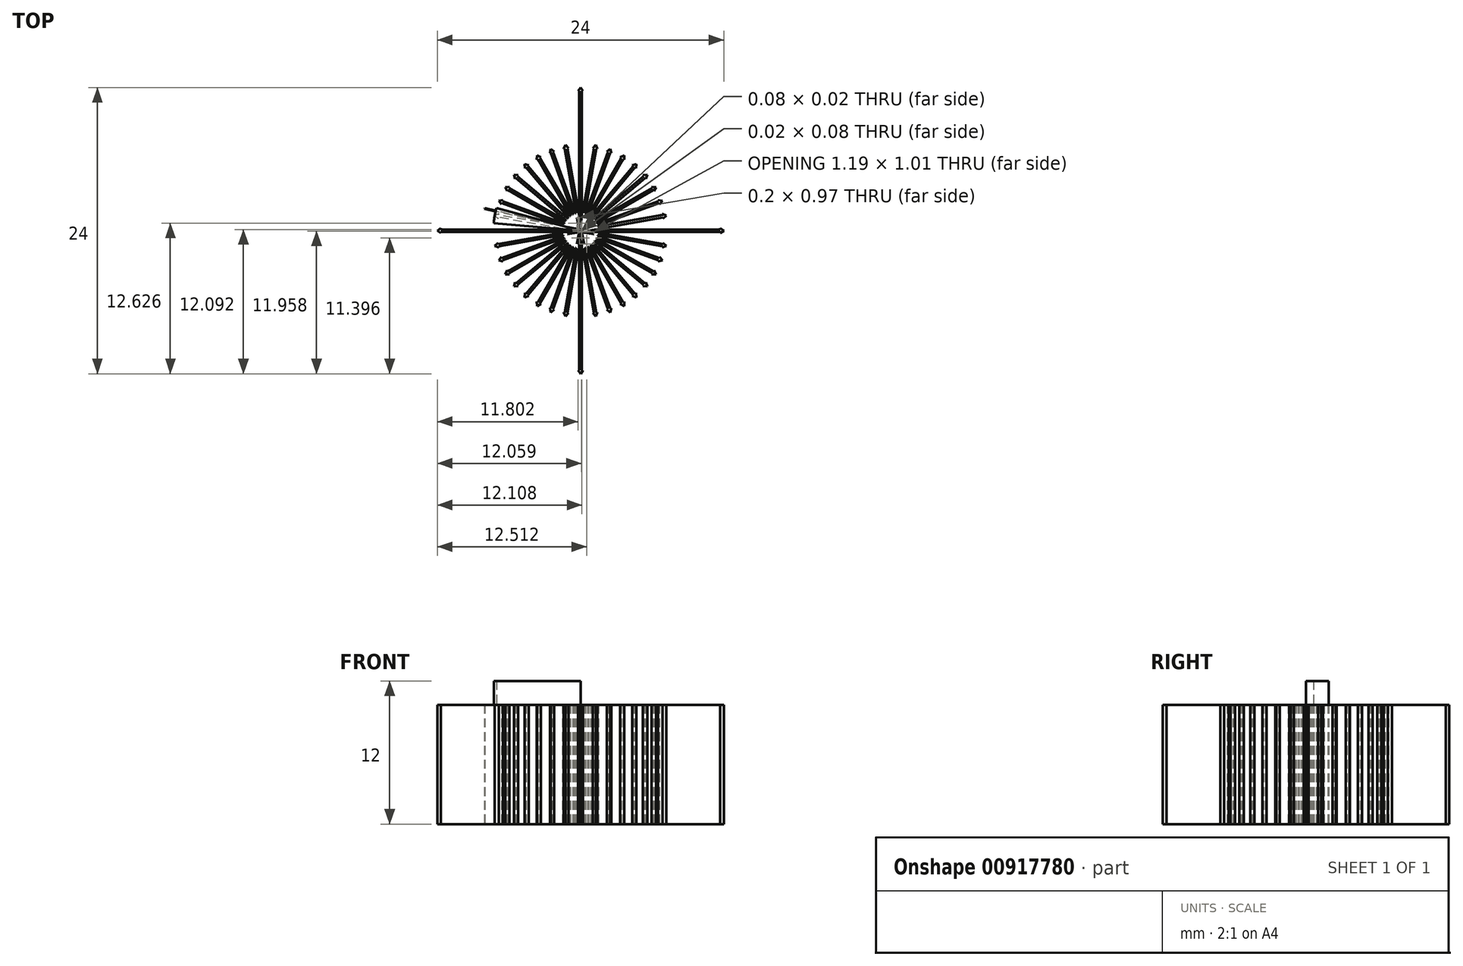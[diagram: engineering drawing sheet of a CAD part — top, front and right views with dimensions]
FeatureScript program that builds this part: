
annotation { "Feature Type Name" : "Feature", "Feature Type Description" : "" }
export const myFeature = defineFeature(function(context is Context, id is Id, definition is map)
    precondition{}
    {
        {
            var Q0;
            Q0=qCreatedBy(makeId("Top.planeOp"),FACE);
            var sketch = newSketch(context, id + "F0", { "sketchPlane" : qUnion([Q0])});
            skCircle(sketch, "E0", {"center": v(0, 0) * mm, "radius": 1.5 * mm});
            skLineSegment(sketch, "E1", {"start": v(0, 0) * mm, "end": v(0, 9.82) * mm, "construction": true});
            skLineSegment(sketch, "E2.bottom", {"start": v(-0.1, 0) * mm, "end": v(0.1, 0) * mm, "construction": true});
            skLineSegment(sketch, "E2.top", {"start": v(-0.1, 11.7) * mm, "end": v(0.1, 11.7) * mm});
            skLineSegment(sketch, "E2.left", {"start": v(-0.1, 0) * mm, "end": v(-0.1, 11.7) * mm});
            skLineSegment(sketch, "E2.right", {"start": v(0.1, 0) * mm, "end": v(0.1, 11.7) * mm});
            skLineSegment(sketch, "E3", {"start": v(0, 12) * mm, "end": v(-0.2, 11.7) * mm});
            skLineSegment(sketch, "E4", {"start": v(-0.2, 11.7) * mm, "end": v(0.2, 11.7) * mm});
            skLineSegment(sketch, "E5", {"start": v(0.2, 11.7) * mm, "end": v(0, 12) * mm});
            skLineSegment(sketch, "E6.1.0", {"start": v(0, 0.1) * mm, "end": v(-11.7, 0.1) * mm});
            skLineSegment(sketch, "E6.1.1", {"start": v(0, -0.1) * mm, "end": v(-11.7, -0.1) * mm});
            skLineSegment(sketch, "E6.1.2", {"start": v(-11.7, 0.2) * mm, "end": v(-12, 0) * mm});
            skLineSegment(sketch, "E6.1.3", {"start": v(-11.7, -0.2) * mm, "end": v(-11.7, 0.2) * mm});
            skLineSegment(sketch, "E6.1.4", {"start": v(-12, 0) * mm, "end": v(-11.7, -0.2) * mm});
            skLineSegment(sketch, "E6.2.0", {"start": v(-0.1, 0) * mm, "end": v(-0.1, -11.7) * mm});
            skLineSegment(sketch, "E6.2.1", {"start": v(0.1, 0) * mm, "end": v(0.1, -11.7) * mm});
            skLineSegment(sketch, "E6.2.2", {"start": v(-0.2, -11.7) * mm, "end": v(0, -12) * mm});
            skLineSegment(sketch, "E6.2.3", {"start": v(0.2, -11.7) * mm, "end": v(-0.2, -11.7) * mm});
            skLineSegment(sketch, "E6.2.4", {"start": v(0, -12) * mm, "end": v(0.2, -11.7) * mm});
            skLineSegment(sketch, "E6.3.0", {"start": v(0, -0.1) * mm, "end": v(11.7, -0.1) * mm});
            skLineSegment(sketch, "E6.3.1", {"start": v(0, 0.1) * mm, "end": v(11.7, 0.1) * mm});
            skLineSegment(sketch, "E6.3.2", {"start": v(11.7, -0.2) * mm, "end": v(12, 0) * mm});
            skLineSegment(sketch, "E6.3.3", {"start": v(11.7, 0.2) * mm, "end": v(11.7, -0.2) * mm});
            skLineSegment(sketch, "E6.3.4", {"start": v(12, 0) * mm, "end": v(11.7, 0.2) * mm});
            skLineSegment(sketch, "E7.anchor1", {"start": v(0, 0) * mm, "end": v(0.1, 0) * mm, "construction": true});
            skLineSegment(sketch, "E7.anchor2", {"start": v(0, 0) * mm, "end": v(0.1, -0.02) * mm, "construction": true});
            skLineSegment(sketch, "E8", {"start": v(0, 0) * mm, "end": v(1.22, 6.9) * mm, "construction": true});
            skLineSegment(sketch, "E9.bottom", {"start": v(-0.1, 0.02) * mm, "end": v(0.1, -0.02) * mm});
            skLineSegment(sketch, "E9.top", {"start": v(1.12, 6.91) * mm, "end": v(1.31, 6.88) * mm});
            skLineSegment(sketch, "E9.left", {"start": v(-0.1, 0.02) * mm, "end": v(1.12, 6.91) * mm});
            skLineSegment(sketch, "E9.right", {"start": v(0.1, -0.02) * mm, "end": v(1.31, 6.88) * mm});
            skLineSegment(sketch, "E10", {"start": v(1.27, 7.19) * mm, "end": v(1.02, 6.91) * mm});
            skLineSegment(sketch, "E11", {"start": v(1.02, 6.91) * mm, "end": v(1.4, 6.84) * mm});
            skLineSegment(sketch, "E12", {"start": v(1.4, 6.84) * mm, "end": v(1.27, 7.19) * mm});
            skLineSegment(sketch, "E13", {"start": v(1.22, 6.9) * mm, "end": v(1.26, 7.17) * mm, "construction": true});
            skLineSegment(sketch, "E14.1.0", {"start": v(0.1, -0.03) * mm, "end": v(2.49, 6.54) * mm});
            skLineSegment(sketch, "E14.1.1", {"start": v(-0.1, 0.03) * mm, "end": v(2.3, 6.61) * mm});
            skLineSegment(sketch, "E14.1.2", {"start": v(2.58, 6.5) * mm, "end": v(2.5, 6.86) * mm});
            skLineSegment(sketch, "E14.1.3", {"start": v(2.5, 6.86) * mm, "end": v(2.2, 6.63) * mm});
            skLineSegment(sketch, "E14.1.4", {"start": v(2.2, 6.63) * mm, "end": v(2.58, 6.5) * mm});
            skLineSegment(sketch, "E14.1.5", {"start": v(2.3, 6.61) * mm, "end": v(2.49, 6.54) * mm});
            skLineSegment(sketch, "E14.2.0", {"start": v(0.09, -0.05) * mm, "end": v(3.59, 6.01) * mm});
            skLineSegment(sketch, "E14.2.1", {"start": v(-0.09, 0.05) * mm, "end": v(3.41, 6.11) * mm});
            skLineSegment(sketch, "E14.2.2", {"start": v(3.66, 5.95) * mm, "end": v(3.65, 6.32) * mm});
            skLineSegment(sketch, "E14.2.3", {"start": v(3.65, 6.32) * mm, "end": v(3.32, 6.15) * mm});
            skLineSegment(sketch, "E14.2.4", {"start": v(3.32, 6.15) * mm, "end": v(3.66, 5.95) * mm});
            skLineSegment(sketch, "E14.2.5", {"start": v(3.41, 6.11) * mm, "end": v(3.59, 6.01) * mm});
            skLineSegment(sketch, "E14.3.0", {"start": v(0.08, -0.06) * mm, "end": v(4.58, 5.3) * mm});
            skLineSegment(sketch, "E14.3.1", {"start": v(-0.08, 0.06) * mm, "end": v(4.42, 5.43) * mm});
            skLineSegment(sketch, "E14.3.2", {"start": v(4.64, 5.22) * mm, "end": v(4.7, 5.6) * mm});
            skLineSegment(sketch, "E14.3.3", {"start": v(4.7, 5.6) * mm, "end": v(4.33, 5.48) * mm});
            skLineSegment(sketch, "E14.3.4", {"start": v(4.33, 5.48) * mm, "end": v(4.64, 5.22) * mm});
            skLineSegment(sketch, "E14.3.5", {"start": v(4.42, 5.43) * mm, "end": v(4.58, 5.3) * mm});
            skLineSegment(sketch, "E14.4.0", {"start": v(0.06, -0.08) * mm, "end": v(5.43, 4.42) * mm});
            skLineSegment(sketch, "E14.4.1", {"start": v(-0.06, 0.08) * mm, "end": v(5.3, 4.58) * mm});
            skLineSegment(sketch, "E14.4.2", {"start": v(5.48, 4.33) * mm, "end": v(5.6, 4.7) * mm});
            skLineSegment(sketch, "E14.4.3", {"start": v(5.6, 4.7) * mm, "end": v(5.22, 4.64) * mm});
            skLineSegment(sketch, "E14.4.4", {"start": v(5.22, 4.64) * mm, "end": v(5.48, 4.33) * mm});
            skLineSegment(sketch, "E14.4.5", {"start": v(5.3, 4.58) * mm, "end": v(5.43, 4.42) * mm});
            skLineSegment(sketch, "E14.5.0", {"start": v(0.05, -0.09) * mm, "end": v(6.11, 3.41) * mm});
            skLineSegment(sketch, "E14.5.1", {"start": v(-0.05, 0.09) * mm, "end": v(6.01, 3.59) * mm});
            skLineSegment(sketch, "E14.5.2", {"start": v(6.15, 3.32) * mm, "end": v(6.32, 3.65) * mm});
            skLineSegment(sketch, "E14.5.3", {"start": v(6.32, 3.65) * mm, "end": v(5.95, 3.66) * mm});
            skLineSegment(sketch, "E14.5.4", {"start": v(5.95, 3.66) * mm, "end": v(6.15, 3.32) * mm});
            skLineSegment(sketch, "E14.5.5", {"start": v(6.01, 3.59) * mm, "end": v(6.11, 3.41) * mm});
            skLineSegment(sketch, "E14.6.0", {"start": v(0.03, -0.1) * mm, "end": v(6.61, 2.3) * mm});
            skLineSegment(sketch, "E14.6.1", {"start": v(-0.03, 0.1) * mm, "end": v(6.54, 2.49) * mm});
            skLineSegment(sketch, "E14.6.2", {"start": v(6.63, 2.2) * mm, "end": v(6.86, 2.5) * mm});
            skLineSegment(sketch, "E14.6.3", {"start": v(6.86, 2.5) * mm, "end": v(6.5, 2.58) * mm});
            skLineSegment(sketch, "E14.6.4", {"start": v(6.5, 2.58) * mm, "end": v(6.63, 2.2) * mm});
            skLineSegment(sketch, "E14.6.5", {"start": v(6.54, 2.49) * mm, "end": v(6.61, 2.3) * mm});
            skLineSegment(sketch, "E14.7.0", {"start": v(0.02, -0.1) * mm, "end": v(6.91, 1.12) * mm});
            skLineSegment(sketch, "E14.7.1", {"start": v(-0.02, 0.1) * mm, "end": v(6.88, 1.31) * mm});
            skLineSegment(sketch, "E14.7.2", {"start": v(6.91, 1.02) * mm, "end": v(7.19, 1.27) * mm});
            skLineSegment(sketch, "E14.7.3", {"start": v(7.19, 1.27) * mm, "end": v(6.84, 1.4) * mm});
            skLineSegment(sketch, "E14.7.4", {"start": v(6.84, 1.4) * mm, "end": v(6.91, 1.02) * mm});
            skLineSegment(sketch, "E14.7.5", {"start": v(6.88, 1.31) * mm, "end": v(6.91, 1.12) * mm});
            skLineSegment(sketch, "E14.8.0", {"start": v(0, -0.1) * mm, "end": v(7, -0.1) * mm});
            skLineSegment(sketch, "E14.8.1", {"start": v(0, 0.1) * mm, "end": v(7, 0.1) * mm});
            skLineSegment(sketch, "E14.8.5", {"start": v(7, 0.1) * mm, "end": v(7, -0.1) * mm});
            skLineSegment(sketch, "E14.9.0", {"start": v(-0.02, -0.1) * mm, "end": v(6.88, -1.31) * mm});
            skLineSegment(sketch, "E14.9.1", {"start": v(0.02, 0.1) * mm, "end": v(6.91, -1.12) * mm});
            skLineSegment(sketch, "E14.9.2", {"start": v(6.84, -1.4) * mm, "end": v(7.19, -1.27) * mm});
            skLineSegment(sketch, "E14.9.3", {"start": v(7.19, -1.27) * mm, "end": v(6.91, -1.02) * mm});
            skLineSegment(sketch, "E14.9.4", {"start": v(6.91, -1.02) * mm, "end": v(6.84, -1.4) * mm});
            skLineSegment(sketch, "E14.9.5", {"start": v(6.91, -1.12) * mm, "end": v(6.88, -1.31) * mm});
            skLineSegment(sketch, "E14.10.0", {"start": v(-0.03, -0.1) * mm, "end": v(6.54, -2.49) * mm});
            skLineSegment(sketch, "E14.10.1", {"start": v(0.03, 0.1) * mm, "end": v(6.61, -2.3) * mm});
            skLineSegment(sketch, "E14.10.2", {"start": v(6.5, -2.58) * mm, "end": v(6.86, -2.5) * mm});
            skLineSegment(sketch, "E14.10.3", {"start": v(6.86, -2.5) * mm, "end": v(6.63, -2.2) * mm});
            skLineSegment(sketch, "E14.10.4", {"start": v(6.63, -2.2) * mm, "end": v(6.5, -2.58) * mm});
            skLineSegment(sketch, "E14.10.5", {"start": v(6.61, -2.3) * mm, "end": v(6.54, -2.49) * mm});
            skLineSegment(sketch, "E14.11.0", {"start": v(-0.05, -0.09) * mm, "end": v(6.01, -3.59) * mm});
            skLineSegment(sketch, "E14.11.1", {"start": v(0.05, 0.09) * mm, "end": v(6.11, -3.41) * mm});
            skLineSegment(sketch, "E14.11.2", {"start": v(5.95, -3.66) * mm, "end": v(6.32, -3.65) * mm});
            skLineSegment(sketch, "E14.11.3", {"start": v(6.32, -3.65) * mm, "end": v(6.15, -3.32) * mm});
            skLineSegment(sketch, "E14.11.4", {"start": v(6.15, -3.32) * mm, "end": v(5.95, -3.66) * mm});
            skLineSegment(sketch, "E14.11.5", {"start": v(6.11, -3.41) * mm, "end": v(6.01, -3.59) * mm});
            skLineSegment(sketch, "E14.12.0", {"start": v(-0.06, -0.08) * mm, "end": v(5.3, -4.58) * mm});
            skLineSegment(sketch, "E14.12.1", {"start": v(0.06, 0.08) * mm, "end": v(5.43, -4.42) * mm});
            skLineSegment(sketch, "E14.12.2", {"start": v(5.22, -4.64) * mm, "end": v(5.6, -4.7) * mm});
            skLineSegment(sketch, "E14.12.3", {"start": v(5.6, -4.7) * mm, "end": v(5.48, -4.33) * mm});
            skLineSegment(sketch, "E14.12.4", {"start": v(5.48, -4.33) * mm, "end": v(5.22, -4.64) * mm});
            skLineSegment(sketch, "E14.12.5", {"start": v(5.43, -4.42) * mm, "end": v(5.3, -4.58) * mm});
            skLineSegment(sketch, "E14.13.0", {"start": v(-0.08, -0.06) * mm, "end": v(4.42, -5.43) * mm});
            skLineSegment(sketch, "E14.13.1", {"start": v(0.08, 0.06) * mm, "end": v(4.58, -5.3) * mm});
            skLineSegment(sketch, "E14.13.2", {"start": v(4.33, -5.48) * mm, "end": v(4.7, -5.6) * mm});
            skLineSegment(sketch, "E14.13.3", {"start": v(4.7, -5.6) * mm, "end": v(4.64, -5.22) * mm});
            skLineSegment(sketch, "E14.13.4", {"start": v(4.64, -5.22) * mm, "end": v(4.33, -5.48) * mm});
            skLineSegment(sketch, "E14.13.5", {"start": v(4.58, -5.3) * mm, "end": v(4.42, -5.43) * mm});
            skLineSegment(sketch, "E14.14.0", {"start": v(-0.09, -0.05) * mm, "end": v(3.41, -6.11) * mm});
            skLineSegment(sketch, "E14.14.1", {"start": v(0.09, 0.05) * mm, "end": v(3.59, -6.01) * mm});
            skLineSegment(sketch, "E14.14.2", {"start": v(3.32, -6.15) * mm, "end": v(3.65, -6.32) * mm});
            skLineSegment(sketch, "E14.14.3", {"start": v(3.65, -6.32) * mm, "end": v(3.66, -5.95) * mm});
            skLineSegment(sketch, "E14.14.4", {"start": v(3.66, -5.95) * mm, "end": v(3.32, -6.15) * mm});
            skLineSegment(sketch, "E14.14.5", {"start": v(3.59, -6.01) * mm, "end": v(3.41, -6.11) * mm});
            skLineSegment(sketch, "E14.15.0", {"start": v(-0.1, -0.03) * mm, "end": v(2.3, -6.61) * mm});
            skLineSegment(sketch, "E14.15.1", {"start": v(0.1, 0.03) * mm, "end": v(2.49, -6.54) * mm});
            skLineSegment(sketch, "E14.15.2", {"start": v(2.2, -6.63) * mm, "end": v(2.5, -6.86) * mm});
            skLineSegment(sketch, "E14.15.3", {"start": v(2.5, -6.86) * mm, "end": v(2.58, -6.5) * mm});
            skLineSegment(sketch, "E14.15.4", {"start": v(2.58, -6.5) * mm, "end": v(2.2, -6.63) * mm});
            skLineSegment(sketch, "E14.15.5", {"start": v(2.49, -6.54) * mm, "end": v(2.3, -6.61) * mm});
            skLineSegment(sketch, "E14.16.0", {"start": v(-0.1, -0.02) * mm, "end": v(1.12, -6.91) * mm});
            skLineSegment(sketch, "E14.16.1", {"start": v(0.1, 0.02) * mm, "end": v(1.31, -6.88) * mm});
            skLineSegment(sketch, "E14.16.2", {"start": v(1.02, -6.91) * mm, "end": v(1.27, -7.19) * mm});
            skLineSegment(sketch, "E14.16.3", {"start": v(1.27, -7.19) * mm, "end": v(1.4, -6.84) * mm});
            skLineSegment(sketch, "E14.16.4", {"start": v(1.4, -6.84) * mm, "end": v(1.02, -6.91) * mm});
            skLineSegment(sketch, "E14.16.5", {"start": v(1.31, -6.88) * mm, "end": v(1.12, -6.91) * mm});
            skLineSegment(sketch, "E14.17.0", {"start": v(-0.1, 0) * mm, "end": v(-0.1, -7) * mm});
            skLineSegment(sketch, "E14.17.1", {"start": v(0.1, 0) * mm, "end": v(0.1, -7) * mm});
            skLineSegment(sketch, "E14.17.5", {"start": v(0.1, -7) * mm, "end": v(-0.1, -7) * mm});
            skLineSegment(sketch, "E14.18.0", {"start": v(-0.1, 0.02) * mm, "end": v(-1.31, -6.88) * mm});
            skLineSegment(sketch, "E14.18.1", {"start": v(0.1, -0.02) * mm, "end": v(-1.12, -6.91) * mm});
            skLineSegment(sketch, "E14.18.2", {"start": v(-1.4, -6.84) * mm, "end": v(-1.27, -7.19) * mm});
            skLineSegment(sketch, "E14.18.3", {"start": v(-1.27, -7.19) * mm, "end": v(-1.02, -6.91) * mm});
            skLineSegment(sketch, "E14.18.4", {"start": v(-1.02, -6.91) * mm, "end": v(-1.4, -6.84) * mm});
            skLineSegment(sketch, "E14.18.5", {"start": v(-1.12, -6.91) * mm, "end": v(-1.31, -6.88) * mm});
            skLineSegment(sketch, "E14.19.0", {"start": v(-0.1, 0.03) * mm, "end": v(-2.49, -6.54) * mm});
            skLineSegment(sketch, "E14.19.1", {"start": v(0.1, -0.03) * mm, "end": v(-2.3, -6.61) * mm});
            skLineSegment(sketch, "E14.19.2", {"start": v(-2.58, -6.5) * mm, "end": v(-2.5, -6.86) * mm});
            skLineSegment(sketch, "E14.19.3", {"start": v(-2.5, -6.86) * mm, "end": v(-2.2, -6.63) * mm});
            skLineSegment(sketch, "E14.19.4", {"start": v(-2.2, -6.63) * mm, "end": v(-2.58, -6.5) * mm});
            skLineSegment(sketch, "E14.19.5", {"start": v(-2.3, -6.61) * mm, "end": v(-2.49, -6.54) * mm});
            skLineSegment(sketch, "E14.20.0", {"start": v(-0.09, 0.05) * mm, "end": v(-3.59, -6.01) * mm});
            skLineSegment(sketch, "E14.20.1", {"start": v(0.09, -0.05) * mm, "end": v(-3.41, -6.11) * mm});
            skLineSegment(sketch, "E14.20.2", {"start": v(-3.66, -5.95) * mm, "end": v(-3.65, -6.32) * mm});
            skLineSegment(sketch, "E14.20.3", {"start": v(-3.65, -6.32) * mm, "end": v(-3.32, -6.15) * mm});
            skLineSegment(sketch, "E14.20.4", {"start": v(-3.32, -6.15) * mm, "end": v(-3.66, -5.95) * mm});
            skLineSegment(sketch, "E14.20.5", {"start": v(-3.41, -6.11) * mm, "end": v(-3.59, -6.01) * mm});
            skLineSegment(sketch, "E14.21.0", {"start": v(-0.08, 0.06) * mm, "end": v(-4.58, -5.3) * mm});
            skLineSegment(sketch, "E14.21.1", {"start": v(0.08, -0.06) * mm, "end": v(-4.42, -5.43) * mm});
            skLineSegment(sketch, "E14.21.2", {"start": v(-4.64, -5.22) * mm, "end": v(-4.7, -5.6) * mm});
            skLineSegment(sketch, "E14.21.3", {"start": v(-4.7, -5.6) * mm, "end": v(-4.33, -5.48) * mm});
            skLineSegment(sketch, "E14.21.4", {"start": v(-4.33, -5.48) * mm, "end": v(-4.64, -5.22) * mm});
            skLineSegment(sketch, "E14.21.5", {"start": v(-4.42, -5.43) * mm, "end": v(-4.58, -5.3) * mm});
            skLineSegment(sketch, "E14.22.0", {"start": v(-0.06, 0.08) * mm, "end": v(-5.43, -4.42) * mm});
            skLineSegment(sketch, "E14.22.1", {"start": v(0.06, -0.08) * mm, "end": v(-5.3, -4.58) * mm});
            skLineSegment(sketch, "E14.22.2", {"start": v(-5.48, -4.33) * mm, "end": v(-5.6, -4.7) * mm});
            skLineSegment(sketch, "E14.22.3", {"start": v(-5.6, -4.7) * mm, "end": v(-5.22, -4.64) * mm});
            skLineSegment(sketch, "E14.22.4", {"start": v(-5.22, -4.64) * mm, "end": v(-5.48, -4.33) * mm});
            skLineSegment(sketch, "E14.22.5", {"start": v(-5.3, -4.58) * mm, "end": v(-5.43, -4.42) * mm});
            skLineSegment(sketch, "E14.23.0", {"start": v(-0.05, 0.09) * mm, "end": v(-6.11, -3.41) * mm});
            skLineSegment(sketch, "E14.23.1", {"start": v(0.05, -0.09) * mm, "end": v(-6.01, -3.59) * mm});
            skLineSegment(sketch, "E14.23.2", {"start": v(-6.15, -3.32) * mm, "end": v(-6.32, -3.65) * mm});
            skLineSegment(sketch, "E14.23.3", {"start": v(-6.32, -3.65) * mm, "end": v(-5.95, -3.66) * mm});
            skLineSegment(sketch, "E14.23.4", {"start": v(-5.95, -3.66) * mm, "end": v(-6.15, -3.32) * mm});
            skLineSegment(sketch, "E14.23.5", {"start": v(-6.01, -3.59) * mm, "end": v(-6.11, -3.41) * mm});
            skLineSegment(sketch, "E14.24.0", {"start": v(-0.03, 0.1) * mm, "end": v(-6.61, -2.3) * mm});
            skLineSegment(sketch, "E14.24.1", {"start": v(0.03, -0.1) * mm, "end": v(-6.54, -2.49) * mm});
            skLineSegment(sketch, "E14.24.2", {"start": v(-6.63, -2.2) * mm, "end": v(-6.86, -2.5) * mm});
            skLineSegment(sketch, "E14.24.3", {"start": v(-6.86, -2.5) * mm, "end": v(-6.5, -2.58) * mm});
            skLineSegment(sketch, "E14.24.4", {"start": v(-6.5, -2.58) * mm, "end": v(-6.63, -2.2) * mm});
            skLineSegment(sketch, "E14.24.5", {"start": v(-6.54, -2.49) * mm, "end": v(-6.61, -2.3) * mm});
            skLineSegment(sketch, "E14.25.0", {"start": v(-0.02, 0.1) * mm, "end": v(-6.91, -1.12) * mm});
            skLineSegment(sketch, "E14.25.1", {"start": v(0.02, -0.1) * mm, "end": v(-6.88, -1.31) * mm});
            skLineSegment(sketch, "E14.25.2", {"start": v(-6.91, -1.02) * mm, "end": v(-7.19, -1.27) * mm});
            skLineSegment(sketch, "E14.25.3", {"start": v(-7.19, -1.27) * mm, "end": v(-6.84, -1.4) * mm});
            skLineSegment(sketch, "E14.25.4", {"start": v(-6.84, -1.4) * mm, "end": v(-6.91, -1.02) * mm});
            skLineSegment(sketch, "E14.25.5", {"start": v(-6.88, -1.31) * mm, "end": v(-6.91, -1.12) * mm});
            skLineSegment(sketch, "E14.26.0", {"start": v(0, 0.1) * mm, "end": v(-7, 0.1) * mm});
            skLineSegment(sketch, "E14.26.1", {"start": v(0, -0.1) * mm, "end": v(-7, -0.1) * mm});
            skLineSegment(sketch, "E14.26.5", {"start": v(-7, -0.1) * mm, "end": v(-7, 0.1) * mm});
            skLineSegment(sketch, "E14.27.0", {"start": v(0.02, 0.1) * mm, "end": v(-6.88, 1.31) * mm});
            skLineSegment(sketch, "E14.27.1", {"start": v(-0.02, -0.1) * mm, "end": v(-6.91, 1.12) * mm});
            skLineSegment(sketch, "E14.27.2", {"start": v(-6.84, 1.4) * mm, "end": v(-7.19, 1.27) * mm});
            skLineSegment(sketch, "E14.27.3", {"start": v(-7.19, 1.27) * mm, "end": v(-6.91, 1.02) * mm});
            skLineSegment(sketch, "E14.27.4", {"start": v(-6.91, 1.02) * mm, "end": v(-6.84, 1.4) * mm});
            skLineSegment(sketch, "E14.27.5", {"start": v(-6.91, 1.12) * mm, "end": v(-6.88, 1.31) * mm});
            skLineSegment(sketch, "E14.28.0", {"start": v(0.03, 0.1) * mm, "end": v(-6.54, 2.49) * mm});
            skLineSegment(sketch, "E14.28.1", {"start": v(-0.03, -0.1) * mm, "end": v(-6.61, 2.3) * mm});
            skLineSegment(sketch, "E14.28.2", {"start": v(-6.5, 2.58) * mm, "end": v(-6.86, 2.5) * mm});
            skLineSegment(sketch, "E14.28.3", {"start": v(-6.86, 2.5) * mm, "end": v(-6.63, 2.2) * mm});
            skLineSegment(sketch, "E14.28.4", {"start": v(-6.63, 2.2) * mm, "end": v(-6.5, 2.58) * mm});
            skLineSegment(sketch, "E14.28.5", {"start": v(-6.61, 2.3) * mm, "end": v(-6.54, 2.49) * mm});
            skLineSegment(sketch, "E14.29.0", {"start": v(0.05, 0.09) * mm, "end": v(-6.01, 3.59) * mm});
            skLineSegment(sketch, "E14.29.1", {"start": v(-0.05, -0.09) * mm, "end": v(-6.11, 3.41) * mm});
            skLineSegment(sketch, "E14.29.2", {"start": v(-5.95, 3.66) * mm, "end": v(-6.32, 3.65) * mm});
            skLineSegment(sketch, "E14.29.3", {"start": v(-6.32, 3.65) * mm, "end": v(-6.15, 3.32) * mm});
            skLineSegment(sketch, "E14.29.4", {"start": v(-6.15, 3.32) * mm, "end": v(-5.95, 3.66) * mm});
            skLineSegment(sketch, "E14.29.5", {"start": v(-6.11, 3.41) * mm, "end": v(-6.01, 3.59) * mm});
            skLineSegment(sketch, "E14.30.0", {"start": v(0.06, 0.08) * mm, "end": v(-5.3, 4.58) * mm});
            skLineSegment(sketch, "E14.30.1", {"start": v(-0.06, -0.08) * mm, "end": v(-5.43, 4.42) * mm});
            skLineSegment(sketch, "E14.30.2", {"start": v(-5.22, 4.64) * mm, "end": v(-5.6, 4.7) * mm});
            skLineSegment(sketch, "E14.30.3", {"start": v(-5.6, 4.7) * mm, "end": v(-5.48, 4.33) * mm});
            skLineSegment(sketch, "E14.30.4", {"start": v(-5.48, 4.33) * mm, "end": v(-5.22, 4.64) * mm});
            skLineSegment(sketch, "E14.30.5", {"start": v(-5.43, 4.42) * mm, "end": v(-5.3, 4.58) * mm});
            skLineSegment(sketch, "E14.31.0", {"start": v(0.08, 0.06) * mm, "end": v(-4.42, 5.43) * mm});
            skLineSegment(sketch, "E14.31.1", {"start": v(-0.08, -0.06) * mm, "end": v(-4.58, 5.3) * mm});
            skLineSegment(sketch, "E14.31.2", {"start": v(-4.33, 5.48) * mm, "end": v(-4.7, 5.6) * mm});
            skLineSegment(sketch, "E14.31.3", {"start": v(-4.7, 5.6) * mm, "end": v(-4.64, 5.22) * mm});
            skLineSegment(sketch, "E14.31.4", {"start": v(-4.64, 5.22) * mm, "end": v(-4.33, 5.48) * mm});
            skLineSegment(sketch, "E14.31.5", {"start": v(-4.58, 5.3) * mm, "end": v(-4.42, 5.43) * mm});
            skLineSegment(sketch, "E14.32.0", {"start": v(0.09, 0.05) * mm, "end": v(-3.41, 6.11) * mm});
            skLineSegment(sketch, "E14.32.1", {"start": v(-0.09, -0.05) * mm, "end": v(-3.59, 6.01) * mm});
            skLineSegment(sketch, "E14.32.2", {"start": v(-3.32, 6.15) * mm, "end": v(-3.65, 6.32) * mm});
            skLineSegment(sketch, "E14.32.3", {"start": v(-3.65, 6.32) * mm, "end": v(-3.66, 5.95) * mm});
            skLineSegment(sketch, "E14.32.4", {"start": v(-3.66, 5.95) * mm, "end": v(-3.32, 6.15) * mm});
            skLineSegment(sketch, "E14.32.5", {"start": v(-3.59, 6.01) * mm, "end": v(-3.41, 6.11) * mm});
            skLineSegment(sketch, "E14.33.0", {"start": v(0.1, 0.03) * mm, "end": v(-2.3, 6.61) * mm});
            skLineSegment(sketch, "E14.33.1", {"start": v(-0.1, -0.03) * mm, "end": v(-2.49, 6.54) * mm});
            skLineSegment(sketch, "E14.33.2", {"start": v(-2.2, 6.63) * mm, "end": v(-2.5, 6.86) * mm});
            skLineSegment(sketch, "E14.33.3", {"start": v(-2.5, 6.86) * mm, "end": v(-2.58, 6.5) * mm});
            skLineSegment(sketch, "E14.33.4", {"start": v(-2.58, 6.5) * mm, "end": v(-2.2, 6.63) * mm});
            skLineSegment(sketch, "E14.33.5", {"start": v(-2.49, 6.54) * mm, "end": v(-2.3, 6.61) * mm});
            skLineSegment(sketch, "E14.34.0", {"start": v(0.1, 0.02) * mm, "end": v(-1.12, 6.91) * mm});
            skLineSegment(sketch, "E14.34.1", {"start": v(-0.1, -0.02) * mm, "end": v(-1.31, 6.88) * mm});
            skLineSegment(sketch, "E14.34.2", {"start": v(-1.02, 6.91) * mm, "end": v(-1.27, 7.19) * mm});
            skLineSegment(sketch, "E14.34.3", {"start": v(-1.27, 7.19) * mm, "end": v(-1.4, 6.84) * mm});
            skLineSegment(sketch, "E14.34.4", {"start": v(-1.4, 6.84) * mm, "end": v(-1.02, 6.91) * mm});
            skLineSegment(sketch, "E14.34.5", {"start": v(-1.31, 6.88) * mm, "end": v(-1.12, 6.91) * mm});
            skLineSegment(sketch, "E14.35.0", {"start": v(0.1, 0) * mm, "end": v(0.1, 7) * mm});
            skLineSegment(sketch, "E14.35.1", {"start": v(-0.1, 0) * mm, "end": v(-0.1, 7) * mm});
            skLineSegment(sketch, "E14.35.5", {"start": v(-0.1, 7) * mm, "end": v(0.1, 7) * mm});
            skLineSegment(sketch, "E14.anchor1", {"start": v(0, 0) * mm, "end": v(-0.1, 0.02) * mm, "construction": true});
            skLineSegment(sketch, "E14.anchor2", {"start": v(0, 0) * mm, "end": v(-0.1, 0) * mm, "construction": true});
            skLineSegment(sketch, "E15", {"start": v(0, 0) * mm, "end": v(-8.04, 1.86) * mm, "construction": true});
            skLineSegment(sketch, "E16.0", {"start": v(-1.47, 0.31) * mm, "end": v(-8.05, 1.83) * mm});
            skLineSegment(sketch, "E17", {"start": v(-8.05, 1.83) * mm, "end": v(-8.04, 1.88) * mm});
            skPoint(sketch, "E18.orphan", {"position": v(0, -0.02) * mm});
            skLineSegment(sketch, "E19.trimOffspring", {"start": v(-1.46, 0.36) * mm, "end": v(-8.04, 1.88) * mm});
            skLineSegment(sketch, "E20.trimOffspring", {"start": v(-0.19, 0.07) * mm, "end": v(-0.19, 0.07) * mm});
            skPoint(sketch, "E21.0.start.orphan", {"position": v(0, 0.02) * mm});
            skSolve(sketch);
        }
        {
            var Q0;
            Q0=makeQuery(id+"F0.imprint","IMPRINT",FACE,{"disambiguationData":[TD([[makeQuery(id+"F0.imprint","IMPRINT",EDGE,{"derivedFrom":sQuery(id+"F0.wireOp",EDGE,"vvanIXAu-rXu3-wId7-brfe-paVfvKl2uOtP")}),1.0]])]});
            var Q1;
            {var subQ4=sQuery(id+"F0.wireOp",EDGE,"E3");Q1=makeQuery(id+"F0.imprint","IMPRINT",FACE,{"disambiguationData":[TD([[makeQuery(id+"F0.imprint","IMPRINT",EDGE,{"derivedFrom":subQ4}),1.0]])]});}
            var Q2;
            {var subQ2=sQuery(id+"F0.wireOp",EDGE,"E6.1.2");Q2=makeQuery(id+"F0.imprint","IMPRINT",FACE,{"disambiguationData":[TD([[makeQuery(id+"F0.imprint","IMPRINT",EDGE,{"derivedFrom":subQ2}),1.0]])]});}
            var Q3;
            {var subQ2=sQuery(id+"F0.wireOp",EDGE,"E6.2.2");Q3=makeQuery(id+"F0.imprint","IMPRINT",FACE,{"disambiguationData":[TD([[makeQuery(id+"F0.imprint","IMPRINT",EDGE,{"derivedFrom":subQ2}),1.0]])]});}
            var Q4;
            {var subQ2=sQuery(id+"F0.wireOp",EDGE,"E6.3.2");Q4=makeQuery(id+"F0.imprint","IMPRINT",FACE,{"disambiguationData":[TD([[makeQuery(id+"F0.imprint","IMPRINT",EDGE,{"derivedFrom":subQ2}),1.0]])]});}
            var Q5;
            {var subQ2=sQuery(id+"F0.wireOp",EDGE,"E9.top");Q5=makeQuery(id+"F0.imprint","IMPRINT",FACE,{"disambiguationData":[TD([[makeQuery(id+"F0.imprint","IMPRINT",EDGE,{"derivedFrom":subQ2}),1.0]])]});}
            var Q6;
            {var subQ5=sQuery(id+"F0.wireOp",EDGE,"E14.1.2");Q6=makeQuery(id+"F0.imprint","IMPRINT",FACE,{"disambiguationData":[TD([[makeQuery(id+"F0.imprint","IMPRINT",EDGE,{"derivedFrom":subQ5}),1.0]])]});}
            var Q7;
            {var subQ5=sQuery(id+"F0.wireOp",EDGE,"E14.2.2");Q7=makeQuery(id+"F0.imprint","IMPRINT",FACE,{"disambiguationData":[TD([[makeQuery(id+"F0.imprint","IMPRINT",EDGE,{"derivedFrom":subQ5}),1.0]])]});}
            var Q8;
            {var subQ5=sQuery(id+"F0.wireOp",EDGE,"E14.3.2");Q8=makeQuery(id+"F0.imprint","IMPRINT",FACE,{"disambiguationData":[TD([[makeQuery(id+"F0.imprint","IMPRINT",EDGE,{"derivedFrom":subQ5}),1.0]])]});}
            var Q9;
            {var subQ5=sQuery(id+"F0.wireOp",EDGE,"E14.4.2");Q9=makeQuery(id+"F0.imprint","IMPRINT",FACE,{"disambiguationData":[TD([[makeQuery(id+"F0.imprint","IMPRINT",EDGE,{"derivedFrom":subQ5}),1.0]])]});}
            var Q10;
            {var subQ5=sQuery(id+"F0.wireOp",EDGE,"E14.5.2");Q10=makeQuery(id+"F0.imprint","IMPRINT",FACE,{"disambiguationData":[TD([[makeQuery(id+"F0.imprint","IMPRINT",EDGE,{"derivedFrom":subQ5}),1.0]])]});}
            var Q11;
            {var subQ5=sQuery(id+"F0.wireOp",EDGE,"E14.6.2");Q11=makeQuery(id+"F0.imprint","IMPRINT",FACE,{"disambiguationData":[TD([[makeQuery(id+"F0.imprint","IMPRINT",EDGE,{"derivedFrom":subQ5}),1.0]])]});}
            var Q12;
            {var subQ5=sQuery(id+"F0.wireOp",EDGE,"E14.7.2");Q12=makeQuery(id+"F0.imprint","IMPRINT",FACE,{"disambiguationData":[TD([[makeQuery(id+"F0.imprint","IMPRINT",EDGE,{"derivedFrom":subQ5}),1.0]])]});}
            var Q13;
            {var subQ5=sQuery(id+"F0.wireOp",EDGE,"E14.9.2");Q13=makeQuery(id+"F0.imprint","IMPRINT",FACE,{"disambiguationData":[TD([[makeQuery(id+"F0.imprint","IMPRINT",EDGE,{"derivedFrom":subQ5}),1.0]])]});}
            var Q14;
            {var subQ5=sQuery(id+"F0.wireOp",EDGE,"E14.10.2");Q14=makeQuery(id+"F0.imprint","IMPRINT",FACE,{"disambiguationData":[TD([[makeQuery(id+"F0.imprint","IMPRINT",EDGE,{"derivedFrom":subQ5}),1.0]])]});}
            var Q15;
            {var subQ5=sQuery(id+"F0.wireOp",EDGE,"E14.11.2");Q15=makeQuery(id+"F0.imprint","IMPRINT",FACE,{"disambiguationData":[TD([[makeQuery(id+"F0.imprint","IMPRINT",EDGE,{"derivedFrom":subQ5}),1.0]])]});}
            var Q16;
            {var subQ5=sQuery(id+"F0.wireOp",EDGE,"E14.12.2");Q16=makeQuery(id+"F0.imprint","IMPRINT",FACE,{"disambiguationData":[TD([[makeQuery(id+"F0.imprint","IMPRINT",EDGE,{"derivedFrom":subQ5}),1.0]])]});}
            var Q17;
            {var subQ5=sQuery(id+"F0.wireOp",EDGE,"E14.13.2");Q17=makeQuery(id+"F0.imprint","IMPRINT",FACE,{"disambiguationData":[TD([[makeQuery(id+"F0.imprint","IMPRINT",EDGE,{"derivedFrom":subQ5}),1.0]])]});}
            var Q18;
            {var subQ5=sQuery(id+"F0.wireOp",EDGE,"E14.14.2");Q18=makeQuery(id+"F0.imprint","IMPRINT",FACE,{"disambiguationData":[TD([[makeQuery(id+"F0.imprint","IMPRINT",EDGE,{"derivedFrom":subQ5}),1.0]])]});}
            var Q19;
            {var subQ5=sQuery(id+"F0.wireOp",EDGE,"E14.15.2");Q19=makeQuery(id+"F0.imprint","IMPRINT",FACE,{"disambiguationData":[TD([[makeQuery(id+"F0.imprint","IMPRINT",EDGE,{"derivedFrom":subQ5}),1.0]])]});}
            var Q20;
            {var subQ5=sQuery(id+"F0.wireOp",EDGE,"E14.16.2");Q20=makeQuery(id+"F0.imprint","IMPRINT",FACE,{"disambiguationData":[TD([[makeQuery(id+"F0.imprint","IMPRINT",EDGE,{"derivedFrom":subQ5}),1.0]])]});}
            var Q21;
            {var subQ5=sQuery(id+"F0.wireOp",EDGE,"E14.18.2");Q21=makeQuery(id+"F0.imprint","IMPRINT",FACE,{"disambiguationData":[TD([[makeQuery(id+"F0.imprint","IMPRINT",EDGE,{"derivedFrom":subQ5}),1.0]])]});}
            var Q22;
            {var subQ5=sQuery(id+"F0.wireOp",EDGE,"E14.19.2");Q22=makeQuery(id+"F0.imprint","IMPRINT",FACE,{"disambiguationData":[TD([[makeQuery(id+"F0.imprint","IMPRINT",EDGE,{"derivedFrom":subQ5}),1.0]])]});}
            var Q23;
            {var subQ5=sQuery(id+"F0.wireOp",EDGE,"E14.20.2");Q23=makeQuery(id+"F0.imprint","IMPRINT",FACE,{"disambiguationData":[TD([[makeQuery(id+"F0.imprint","IMPRINT",EDGE,{"derivedFrom":subQ5}),1.0]])]});}
            var Q24;
            {var subQ5=sQuery(id+"F0.wireOp",EDGE,"E14.21.2");Q24=makeQuery(id+"F0.imprint","IMPRINT",FACE,{"disambiguationData":[TD([[makeQuery(id+"F0.imprint","IMPRINT",EDGE,{"derivedFrom":subQ5}),1.0]])]});}
            var Q25;
            {var subQ5=sQuery(id+"F0.wireOp",EDGE,"E14.22.2");Q25=makeQuery(id+"F0.imprint","IMPRINT",FACE,{"disambiguationData":[TD([[makeQuery(id+"F0.imprint","IMPRINT",EDGE,{"derivedFrom":subQ5}),1.0]])]});}
            var Q26;
            {var subQ5=sQuery(id+"F0.wireOp",EDGE,"E14.23.2");Q26=makeQuery(id+"F0.imprint","IMPRINT",FACE,{"disambiguationData":[TD([[makeQuery(id+"F0.imprint","IMPRINT",EDGE,{"derivedFrom":subQ5}),1.0]])]});}
            var Q27;
            {var subQ5=sQuery(id+"F0.wireOp",EDGE,"E14.24.2");Q27=makeQuery(id+"F0.imprint","IMPRINT",FACE,{"disambiguationData":[TD([[makeQuery(id+"F0.imprint","IMPRINT",EDGE,{"derivedFrom":subQ5}),1.0]])]});}
            var Q28;
            {var subQ5=sQuery(id+"F0.wireOp",EDGE,"E14.25.2");Q28=makeQuery(id+"F0.imprint","IMPRINT",FACE,{"disambiguationData":[TD([[makeQuery(id+"F0.imprint","IMPRINT",EDGE,{"derivedFrom":subQ5}),1.0]])]});}
            var Q29;
            {var subQ5=sQuery(id+"F0.wireOp",EDGE,"E14.27.2");Q29=makeQuery(id+"F0.imprint","IMPRINT",FACE,{"disambiguationData":[TD([[makeQuery(id+"F0.imprint","IMPRINT",EDGE,{"derivedFrom":subQ5}),1.0]])]});}
            var Q30;
            {var subQ5=sQuery(id+"F0.wireOp",EDGE,"E14.28.2");Q30=makeQuery(id+"F0.imprint","IMPRINT",FACE,{"disambiguationData":[TD([[makeQuery(id+"F0.imprint","IMPRINT",EDGE,{"derivedFrom":subQ5}),1.0]])]});}
            var Q31;
            {var subQ5=sQuery(id+"F0.wireOp",EDGE,"E14.29.2");Q31=makeQuery(id+"F0.imprint","IMPRINT",FACE,{"disambiguationData":[TD([[makeQuery(id+"F0.imprint","IMPRINT",EDGE,{"derivedFrom":subQ5}),1.0]])]});}
            var Q32;
            {var subQ5=sQuery(id+"F0.wireOp",EDGE,"E14.30.2");Q32=makeQuery(id+"F0.imprint","IMPRINT",FACE,{"disambiguationData":[TD([[makeQuery(id+"F0.imprint","IMPRINT",EDGE,{"derivedFrom":subQ5}),1.0]])]});}
            var Q33;
            {var subQ5=sQuery(id+"F0.wireOp",EDGE,"E14.31.2");Q33=makeQuery(id+"F0.imprint","IMPRINT",FACE,{"disambiguationData":[TD([[makeQuery(id+"F0.imprint","IMPRINT",EDGE,{"derivedFrom":subQ5}),1.0]])]});}
            var Q34;
            {var subQ5=sQuery(id+"F0.wireOp",EDGE,"E14.32.2");Q34=makeQuery(id+"F0.imprint","IMPRINT",FACE,{"disambiguationData":[TD([[makeQuery(id+"F0.imprint","IMPRINT",EDGE,{"derivedFrom":subQ5}),1.0]])]});}
            var Q35;
            {var subQ5=sQuery(id+"F0.wireOp",EDGE,"E14.33.2");Q35=makeQuery(id+"F0.imprint","IMPRINT",FACE,{"disambiguationData":[TD([[makeQuery(id+"F0.imprint","IMPRINT",EDGE,{"derivedFrom":subQ5}),1.0]])]});}
            var Q36;
            {var subQ5=sQuery(id+"F0.wireOp",EDGE,"E14.34.2");Q36=makeQuery(id+"F0.imprint","IMPRINT",FACE,{"disambiguationData":[TD([[makeQuery(id+"F0.imprint","IMPRINT",EDGE,{"derivedFrom":subQ5}),1.0]])]});}
            var Q37;
            {var subQ0=sQuery(id+"F0.wireOp",EDGE,"E14.7.0");var subQ1=sQuery(id+"F0.wireOp",EDGE,"E0");var subQ2=makeQuery(id+"F0.imprint","INTERSECT",VERTEX,{"derivedFrom":[subQ1,subQ0]});Q37=makeQuery(id+"F0.imprint","IMPRINT",FACE,{"disambiguationData":[TD([[makeQuery(id+"F0.imprint","IMPRINT",EDGE,{"disambiguationData":[TD([[subQ2,1.0]])],"derivedFrom":subQ1}),1.0]])]});}
            var Q38;
            {var subQ0=sQuery(id+"F0.wireOp",EDGE,"E14.7.0");var subQ1=sQuery(id+"F0.wireOp",EDGE,"E0");var subQ2=makeQuery(id+"F0.imprint","INTERSECT",VERTEX,{"derivedFrom":[subQ1,subQ0]});Q38=makeQuery(id+"F0.imprint","IMPRINT",FACE,{"disambiguationData":[TD([[makeQuery(id+"F0.imprint","IMPRINT",EDGE,{"disambiguationData":[TD([[subQ2,-1.0]])],"derivedFrom":subQ1}),-1.0]])]});}
            var Q39;
            {var subQ0=sQuery(id+"F0.wireOp",EDGE,"E14.7.1");var subQ1=sQuery(id+"F0.wireOp",EDGE,"E0");var subQ2=makeQuery(id+"F0.imprint","INTERSECT",VERTEX,{"derivedFrom":[subQ1,subQ0]});Q39=makeQuery(id+"F0.imprint","IMPRINT",FACE,{"disambiguationData":[TD([[makeQuery(id+"F0.imprint","IMPRINT",EDGE,{"disambiguationData":[TD([[subQ2,-1.0]])],"derivedFrom":subQ1}),1.0]])]});}
            var Q40;
            {var subQ0=sQuery(id+"F0.wireOp",EDGE,"E14.6.0");var subQ1=sQuery(id+"F0.wireOp",EDGE,"E0");var subQ2=makeQuery(id+"F0.imprint","INTERSECT",VERTEX,{"derivedFrom":[subQ1,subQ0]});Q40=makeQuery(id+"F0.imprint","IMPRINT",FACE,{"disambiguationData":[TD([[makeQuery(id+"F0.imprint","IMPRINT",EDGE,{"disambiguationData":[TD([[subQ2,-1.0]])],"derivedFrom":subQ1}),-1.0]])]});}
            var Q41;
            {var subQ0=sQuery(id+"F0.wireOp",EDGE,"E14.6.1");var subQ1=sQuery(id+"F0.wireOp",EDGE,"E0");var subQ2=makeQuery(id+"F0.imprint","INTERSECT",VERTEX,{"derivedFrom":[subQ1,subQ0]});Q41=makeQuery(id+"F0.imprint","IMPRINT",FACE,{"disambiguationData":[TD([[makeQuery(id+"F0.imprint","IMPRINT",EDGE,{"disambiguationData":[TD([[subQ2,-1.0]])],"derivedFrom":subQ1}),1.0]])]});}
            var Q42;
            {var subQ0=sQuery(id+"F0.wireOp",EDGE,"E14.5.0");var subQ1=sQuery(id+"F0.wireOp",EDGE,"E0");var subQ2=makeQuery(id+"F0.imprint","INTERSECT",VERTEX,{"derivedFrom":[subQ1,subQ0]});Q42=makeQuery(id+"F0.imprint","IMPRINT",FACE,{"disambiguationData":[TD([[makeQuery(id+"F0.imprint","IMPRINT",EDGE,{"disambiguationData":[TD([[subQ2,-1.0]])],"derivedFrom":subQ1}),-1.0]])]});}
            var Q43;
            {var subQ0=sQuery(id+"F0.wireOp",EDGE,"E14.5.1");var subQ1=sQuery(id+"F0.wireOp",EDGE,"E0");var subQ2=makeQuery(id+"F0.imprint","INTERSECT",VERTEX,{"derivedFrom":[subQ1,subQ0]});Q43=makeQuery(id+"F0.imprint","IMPRINT",FACE,{"disambiguationData":[TD([[makeQuery(id+"F0.imprint","IMPRINT",EDGE,{"disambiguationData":[TD([[subQ2,-1.0]])],"derivedFrom":subQ1}),1.0]])]});}
            var Q44;
            {var subQ0=sQuery(id+"F0.wireOp",EDGE,"E14.4.0");var subQ1=sQuery(id+"F0.wireOp",EDGE,"E0");var subQ2=makeQuery(id+"F0.imprint","INTERSECT",VERTEX,{"derivedFrom":[subQ1,subQ0]});Q44=makeQuery(id+"F0.imprint","IMPRINT",FACE,{"disambiguationData":[TD([[makeQuery(id+"F0.imprint","IMPRINT",EDGE,{"disambiguationData":[TD([[subQ2,-1.0]])],"derivedFrom":subQ1}),-1.0]])]});}
            var Q45;
            {var subQ0=sQuery(id+"F0.wireOp",EDGE,"E14.4.1");var subQ1=sQuery(id+"F0.wireOp",EDGE,"E0");var subQ2=makeQuery(id+"F0.imprint","INTERSECT",VERTEX,{"derivedFrom":[subQ1,subQ0]});Q45=makeQuery(id+"F0.imprint","IMPRINT",FACE,{"disambiguationData":[TD([[makeQuery(id+"F0.imprint","IMPRINT",EDGE,{"disambiguationData":[TD([[subQ2,-1.0]])],"derivedFrom":subQ1}),1.0]])]});}
            var Q46;
            {var subQ0=sQuery(id+"F0.wireOp",EDGE,"E14.3.0");var subQ1=sQuery(id+"F0.wireOp",EDGE,"E0");var subQ2=makeQuery(id+"F0.imprint","INTERSECT",VERTEX,{"derivedFrom":[subQ1,subQ0]});Q46=makeQuery(id+"F0.imprint","IMPRINT",FACE,{"disambiguationData":[TD([[makeQuery(id+"F0.imprint","IMPRINT",EDGE,{"disambiguationData":[TD([[subQ2,-1.0]])],"derivedFrom":subQ1}),-1.0]])]});}
            var Q47;
            {var subQ0=sQuery(id+"F0.wireOp",EDGE,"E14.3.1");var subQ1=sQuery(id+"F0.wireOp",EDGE,"E0");var subQ2=makeQuery(id+"F0.imprint","INTERSECT",VERTEX,{"derivedFrom":[subQ1,subQ0]});Q47=makeQuery(id+"F0.imprint","IMPRINT",FACE,{"disambiguationData":[TD([[makeQuery(id+"F0.imprint","IMPRINT",EDGE,{"disambiguationData":[TD([[subQ2,-1.0]])],"derivedFrom":subQ1}),1.0]])]});}
            var Q48;
            {var subQ0=sQuery(id+"F0.wireOp",EDGE,"E14.2.0");var subQ1=sQuery(id+"F0.wireOp",EDGE,"E0");var subQ2=makeQuery(id+"F0.imprint","INTERSECT",VERTEX,{"derivedFrom":[subQ1,subQ0]});Q48=makeQuery(id+"F0.imprint","IMPRINT",FACE,{"disambiguationData":[TD([[makeQuery(id+"F0.imprint","IMPRINT",EDGE,{"disambiguationData":[TD([[subQ2,-1.0]])],"derivedFrom":subQ1}),-1.0]])]});}
            var Q49;
            {var subQ0=sQuery(id+"F0.wireOp",EDGE,"E14.2.1");var subQ1=sQuery(id+"F0.wireOp",EDGE,"E0");var subQ2=makeQuery(id+"F0.imprint","INTERSECT",VERTEX,{"derivedFrom":[subQ1,subQ0]});Q49=makeQuery(id+"F0.imprint","IMPRINT",FACE,{"disambiguationData":[TD([[makeQuery(id+"F0.imprint","IMPRINT",EDGE,{"disambiguationData":[TD([[subQ2,-1.0]])],"derivedFrom":subQ1}),1.0]])]});}
            var Q50;
            {var subQ0=sQuery(id+"F0.wireOp",EDGE,"E14.1.0");var subQ1=sQuery(id+"F0.wireOp",EDGE,"E0");var subQ2=makeQuery(id+"F0.imprint","INTERSECT",VERTEX,{"derivedFrom":[subQ1,subQ0]});Q50=makeQuery(id+"F0.imprint","IMPRINT",FACE,{"disambiguationData":[TD([[makeQuery(id+"F0.imprint","IMPRINT",EDGE,{"disambiguationData":[TD([[subQ2,-1.0]])],"derivedFrom":subQ1}),-1.0]])]});}
            var Q51;
            {var subQ0=sQuery(id+"F0.wireOp",EDGE,"E14.1.1");var subQ1=sQuery(id+"F0.wireOp",EDGE,"E0");var subQ2=makeQuery(id+"F0.imprint","INTERSECT",VERTEX,{"derivedFrom":[subQ1,subQ0]});Q51=makeQuery(id+"F0.imprint","IMPRINT",FACE,{"disambiguationData":[TD([[makeQuery(id+"F0.imprint","IMPRINT",EDGE,{"disambiguationData":[TD([[subQ2,-1.0]])],"derivedFrom":subQ1}),1.0]])]});}
            var Q52;
            {var subQ0=sQuery(id+"F0.wireOp",EDGE,"E9.right");var subQ1=sQuery(id+"F0.wireOp",EDGE,"E0");var subQ2=makeQuery(id+"F0.imprint","INTERSECT",VERTEX,{"derivedFrom":[subQ1,subQ0]});Q52=makeQuery(id+"F0.imprint","IMPRINT",FACE,{"disambiguationData":[TD([[makeQuery(id+"F0.imprint","IMPRINT",EDGE,{"disambiguationData":[TD([[subQ2,-1.0]])],"derivedFrom":subQ1}),-1.0]])]});}
            var Q53;
            {var subQ0=sQuery(id+"F0.wireOp",EDGE,"E9.left");var subQ1=sQuery(id+"F0.wireOp",EDGE,"E0");var subQ2=makeQuery(id+"F0.imprint","INTERSECT",VERTEX,{"derivedFrom":[subQ1,subQ0]});Q53=makeQuery(id+"F0.imprint","IMPRINT",FACE,{"disambiguationData":[TD([[makeQuery(id+"F0.imprint","IMPRINT",EDGE,{"disambiguationData":[TD([[subQ2,-1.0]])],"derivedFrom":subQ1}),1.0]])]});}
            var Q54;
            {var subQ5=sQuery(id+"F0.wireOp",EDGE,"E14.35.5");Q54=makeQuery(id+"F0.imprint","IMPRINT",FACE,{"disambiguationData":[TD([[makeQuery(id+"F0.imprint","IMPRINT",EDGE,{"derivedFrom":subQ5}),-1.0]])]});}
            var Q55;
            {var subQ0=sQuery(id+"F0.wireOp",EDGE,"E14.35.1");var subQ1=sQuery(id+"F0.wireOp",EDGE,"E0");var subQ2=makeQuery(id+"F0.imprint","INTERSECT",VERTEX,{"derivedFrom":[subQ1,subQ0]});Q55=makeQuery(id+"F0.imprint","IMPRINT",FACE,{"disambiguationData":[TD([[makeQuery(id+"F0.imprint","IMPRINT",EDGE,{"disambiguationData":[TD([[subQ2,-1.0]])],"derivedFrom":subQ1}),1.0]])]});}
            var Q56;
            {var subQ0=sQuery(id+"F0.wireOp",EDGE,"E14.34.0");var subQ1=sQuery(id+"F0.wireOp",EDGE,"E0");var subQ2=makeQuery(id+"F0.imprint","INTERSECT",VERTEX,{"derivedFrom":[subQ1,subQ0]});Q56=makeQuery(id+"F0.imprint","IMPRINT",FACE,{"disambiguationData":[TD([[makeQuery(id+"F0.imprint","IMPRINT",EDGE,{"disambiguationData":[TD([[subQ2,-1.0]])],"derivedFrom":subQ1}),-1.0]])]});}
            var Q57;
            {var subQ0=sQuery(id+"F0.wireOp",EDGE,"E14.34.1");var subQ1=sQuery(id+"F0.wireOp",EDGE,"E0");var subQ2=makeQuery(id+"F0.imprint","INTERSECT",VERTEX,{"derivedFrom":[subQ1,subQ0]});Q57=makeQuery(id+"F0.imprint","IMPRINT",FACE,{"disambiguationData":[TD([[makeQuery(id+"F0.imprint","IMPRINT",EDGE,{"disambiguationData":[TD([[subQ2,-1.0]])],"derivedFrom":subQ1}),1.0]])]});}
            var Q58;
            {var subQ0=sQuery(id+"F0.wireOp",EDGE,"E14.33.0");var subQ1=sQuery(id+"F0.wireOp",EDGE,"E0");var subQ2=makeQuery(id+"F0.imprint","INTERSECT",VERTEX,{"derivedFrom":[subQ1,subQ0]});Q58=makeQuery(id+"F0.imprint","IMPRINT",FACE,{"disambiguationData":[TD([[makeQuery(id+"F0.imprint","IMPRINT",EDGE,{"disambiguationData":[TD([[subQ2,-1.0]])],"derivedFrom":subQ1}),-1.0]])]});}
            var Q59;
            {var subQ0=sQuery(id+"F0.wireOp",EDGE,"E14.33.1");var subQ1=sQuery(id+"F0.wireOp",EDGE,"E0");var subQ2=makeQuery(id+"F0.imprint","INTERSECT",VERTEX,{"derivedFrom":[subQ1,subQ0]});Q59=makeQuery(id+"F0.imprint","IMPRINT",FACE,{"disambiguationData":[TD([[makeQuery(id+"F0.imprint","IMPRINT",EDGE,{"disambiguationData":[TD([[subQ2,-1.0]])],"derivedFrom":subQ1}),1.0]])]});}
            var Q60;
            {var subQ0=sQuery(id+"F0.wireOp",EDGE,"E14.32.0");var subQ1=sQuery(id+"F0.wireOp",EDGE,"E0");var subQ2=makeQuery(id+"F0.imprint","INTERSECT",VERTEX,{"derivedFrom":[subQ1,subQ0]});Q60=makeQuery(id+"F0.imprint","IMPRINT",FACE,{"disambiguationData":[TD([[makeQuery(id+"F0.imprint","IMPRINT",EDGE,{"disambiguationData":[TD([[subQ2,-1.0]])],"derivedFrom":subQ1}),-1.0]])]});}
            var Q61;
            {var subQ0=sQuery(id+"F0.wireOp",EDGE,"E14.32.1");var subQ1=sQuery(id+"F0.wireOp",EDGE,"E0");var subQ2=makeQuery(id+"F0.imprint","INTERSECT",VERTEX,{"derivedFrom":[subQ1,subQ0]});Q61=makeQuery(id+"F0.imprint","IMPRINT",FACE,{"disambiguationData":[TD([[makeQuery(id+"F0.imprint","IMPRINT",EDGE,{"disambiguationData":[TD([[subQ2,-1.0]])],"derivedFrom":subQ1}),1.0]])]});}
            var Q62;
            {var subQ0=sQuery(id+"F0.wireOp",EDGE,"E14.31.0");var subQ1=sQuery(id+"F0.wireOp",EDGE,"E0");var subQ2=makeQuery(id+"F0.imprint","INTERSECT",VERTEX,{"derivedFrom":[subQ1,subQ0]});Q62=makeQuery(id+"F0.imprint","IMPRINT",FACE,{"disambiguationData":[TD([[makeQuery(id+"F0.imprint","IMPRINT",EDGE,{"disambiguationData":[TD([[subQ2,-1.0]])],"derivedFrom":subQ1}),-1.0]])]});}
            var Q63;
            {var subQ0=sQuery(id+"F0.wireOp",EDGE,"E14.31.1");var subQ1=sQuery(id+"F0.wireOp",EDGE,"E0");var subQ2=makeQuery(id+"F0.imprint","INTERSECT",VERTEX,{"derivedFrom":[subQ1,subQ0]});Q63=makeQuery(id+"F0.imprint","IMPRINT",FACE,{"disambiguationData":[TD([[makeQuery(id+"F0.imprint","IMPRINT",EDGE,{"disambiguationData":[TD([[subQ2,-1.0]])],"derivedFrom":subQ1}),1.0]])]});}
            var Q64;
            {var subQ0=sQuery(id+"F0.wireOp",EDGE,"E14.30.0");var subQ1=sQuery(id+"F0.wireOp",EDGE,"E0");var subQ2=makeQuery(id+"F0.imprint","INTERSECT",VERTEX,{"derivedFrom":[subQ1,subQ0]});Q64=makeQuery(id+"F0.imprint","IMPRINT",FACE,{"disambiguationData":[TD([[makeQuery(id+"F0.imprint","IMPRINT",EDGE,{"disambiguationData":[TD([[subQ2,-1.0]])],"derivedFrom":subQ1}),-1.0]])]});}
            var Q65;
            {var subQ0=sQuery(id+"F0.wireOp",EDGE,"E14.30.1");var subQ1=sQuery(id+"F0.wireOp",EDGE,"E0");var subQ2=makeQuery(id+"F0.imprint","INTERSECT",VERTEX,{"derivedFrom":[subQ1,subQ0]});Q65=makeQuery(id+"F0.imprint","IMPRINT",FACE,{"disambiguationData":[TD([[makeQuery(id+"F0.imprint","IMPRINT",EDGE,{"disambiguationData":[TD([[subQ2,-1.0]])],"derivedFrom":subQ1}),1.0]])]});}
            var Q66;
            {var subQ0=sQuery(id+"F0.wireOp",EDGE,"E14.29.0");var subQ1=sQuery(id+"F0.wireOp",EDGE,"E0");var subQ2=makeQuery(id+"F0.imprint","INTERSECT",VERTEX,{"derivedFrom":[subQ1,subQ0]});Q66=makeQuery(id+"F0.imprint","IMPRINT",FACE,{"disambiguationData":[TD([[makeQuery(id+"F0.imprint","IMPRINT",EDGE,{"disambiguationData":[TD([[subQ2,-1.0]])],"derivedFrom":subQ1}),-1.0]])]});}
            var Q67;
            {var subQ0=sQuery(id+"F0.wireOp",EDGE,"E14.29.1");var subQ1=sQuery(id+"F0.wireOp",EDGE,"E0");var subQ2=makeQuery(id+"F0.imprint","INTERSECT",VERTEX,{"derivedFrom":[subQ1,subQ0]});Q67=makeQuery(id+"F0.imprint","IMPRINT",FACE,{"disambiguationData":[TD([[makeQuery(id+"F0.imprint","IMPRINT",EDGE,{"disambiguationData":[TD([[subQ2,-1.0]])],"derivedFrom":subQ1}),1.0]])]});}
            var Q68;
            {var subQ0=sQuery(id+"F0.wireOp",EDGE,"E14.28.0");var subQ1=sQuery(id+"F0.wireOp",EDGE,"E0");var subQ2=makeQuery(id+"F0.imprint","INTERSECT",VERTEX,{"derivedFrom":[subQ1,subQ0]});Q68=makeQuery(id+"F0.imprint","IMPRINT",FACE,{"disambiguationData":[TD([[makeQuery(id+"F0.imprint","IMPRINT",EDGE,{"disambiguationData":[TD([[subQ2,-1.0]])],"derivedFrom":subQ1}),-1.0]])]});}
            var Q69;
            {var subQ0=sQuery(id+"F0.wireOp",EDGE,"E14.28.1");var subQ1=sQuery(id+"F0.wireOp",EDGE,"E0");var subQ2=makeQuery(id+"F0.imprint","INTERSECT",VERTEX,{"derivedFrom":[subQ1,subQ0]});Q69=makeQuery(id+"F0.imprint","IMPRINT",FACE,{"disambiguationData":[TD([[makeQuery(id+"F0.imprint","IMPRINT",EDGE,{"disambiguationData":[TD([[subQ2,-1.0]])],"derivedFrom":subQ1}),1.0]])]});}
            var Q70;
            {var subQ0=sQuery(id+"F0.wireOp",EDGE,"E14.27.0");var subQ1=sQuery(id+"F0.wireOp",EDGE,"E0");var subQ2=makeQuery(id+"F0.imprint","INTERSECT",VERTEX,{"derivedFrom":[subQ1,subQ0]});Q70=makeQuery(id+"F0.imprint","IMPRINT",FACE,{"disambiguationData":[TD([[makeQuery(id+"F0.imprint","IMPRINT",EDGE,{"disambiguationData":[TD([[subQ2,-1.0]])],"derivedFrom":subQ1}),-1.0]])]});}
            var Q71;
            {var subQ0=sQuery(id+"F0.wireOp",EDGE,"E14.27.1");var subQ1=sQuery(id+"F0.wireOp",EDGE,"E0");var subQ2=makeQuery(id+"F0.imprint","INTERSECT",VERTEX,{"derivedFrom":[subQ1,subQ0]});Q71=makeQuery(id+"F0.imprint","IMPRINT",FACE,{"disambiguationData":[TD([[makeQuery(id+"F0.imprint","IMPRINT",EDGE,{"disambiguationData":[TD([[subQ2,-1.0]])],"derivedFrom":subQ1}),1.0]])]});}
            var Q72;
            {var subQ5=sQuery(id+"F0.wireOp",EDGE,"E14.26.5");Q72=makeQuery(id+"F0.imprint","IMPRINT",FACE,{"disambiguationData":[TD([[makeQuery(id+"F0.imprint","IMPRINT",EDGE,{"derivedFrom":subQ5}),-1.0]])]});}
            var Q73;
            {var subQ0=sQuery(id+"F0.wireOp",EDGE,"E14.26.1");var subQ1=sQuery(id+"F0.wireOp",EDGE,"E0");var subQ2=makeQuery(id+"F0.imprint","INTERSECT",VERTEX,{"derivedFrom":[subQ1,subQ0]});Q73=makeQuery(id+"F0.imprint","IMPRINT",FACE,{"disambiguationData":[TD([[makeQuery(id+"F0.imprint","IMPRINT",EDGE,{"disambiguationData":[TD([[subQ2,-1.0]])],"derivedFrom":subQ1}),1.0]])]});}
            var Q74;
            {var subQ0=sQuery(id+"F0.wireOp",EDGE,"E14.25.0");var subQ1=sQuery(id+"F0.wireOp",EDGE,"E0");var subQ2=makeQuery(id+"F0.imprint","INTERSECT",VERTEX,{"derivedFrom":[subQ1,subQ0]});Q74=makeQuery(id+"F0.imprint","IMPRINT",FACE,{"disambiguationData":[TD([[makeQuery(id+"F0.imprint","IMPRINT",EDGE,{"disambiguationData":[TD([[subQ2,-1.0]])],"derivedFrom":subQ1}),-1.0]])]});}
            var Q75;
            {var subQ0=sQuery(id+"F0.wireOp",EDGE,"E14.25.1");var subQ1=sQuery(id+"F0.wireOp",EDGE,"E0");var subQ2=makeQuery(id+"F0.imprint","INTERSECT",VERTEX,{"derivedFrom":[subQ1,subQ0]});Q75=makeQuery(id+"F0.imprint","IMPRINT",FACE,{"disambiguationData":[TD([[makeQuery(id+"F0.imprint","IMPRINT",EDGE,{"disambiguationData":[TD([[subQ2,-1.0]])],"derivedFrom":subQ1}),1.0]])]});}
            var Q76;
            {var subQ0=sQuery(id+"F0.wireOp",EDGE,"E14.24.0");var subQ1=sQuery(id+"F0.wireOp",EDGE,"E0");var subQ2=makeQuery(id+"F0.imprint","INTERSECT",VERTEX,{"derivedFrom":[subQ1,subQ0]});Q76=makeQuery(id+"F0.imprint","IMPRINT",FACE,{"disambiguationData":[TD([[makeQuery(id+"F0.imprint","IMPRINT",EDGE,{"disambiguationData":[TD([[subQ2,-1.0]])],"derivedFrom":subQ1}),-1.0]])]});}
            var Q77;
            {var subQ0=sQuery(id+"F0.wireOp",EDGE,"E14.24.1");var subQ1=sQuery(id+"F0.wireOp",EDGE,"E0");var subQ2=makeQuery(id+"F0.imprint","INTERSECT",VERTEX,{"derivedFrom":[subQ1,subQ0]});Q77=makeQuery(id+"F0.imprint","IMPRINT",FACE,{"disambiguationData":[TD([[makeQuery(id+"F0.imprint","IMPRINT",EDGE,{"disambiguationData":[TD([[subQ2,-1.0]])],"derivedFrom":subQ1}),1.0]])]});}
            var Q78;
            {var subQ0=sQuery(id+"F0.wireOp",EDGE,"E14.23.0");var subQ1=sQuery(id+"F0.wireOp",EDGE,"E0");var subQ2=makeQuery(id+"F0.imprint","INTERSECT",VERTEX,{"derivedFrom":[subQ1,subQ0]});Q78=makeQuery(id+"F0.imprint","IMPRINT",FACE,{"disambiguationData":[TD([[makeQuery(id+"F0.imprint","IMPRINT",EDGE,{"disambiguationData":[TD([[subQ2,-1.0]])],"derivedFrom":subQ1}),-1.0]])]});}
            var Q79;
            {var subQ0=sQuery(id+"F0.wireOp",EDGE,"E14.23.1");var subQ1=sQuery(id+"F0.wireOp",EDGE,"E0");var subQ2=makeQuery(id+"F0.imprint","INTERSECT",VERTEX,{"derivedFrom":[subQ1,subQ0]});Q79=makeQuery(id+"F0.imprint","IMPRINT",FACE,{"disambiguationData":[TD([[makeQuery(id+"F0.imprint","IMPRINT",EDGE,{"disambiguationData":[TD([[subQ2,-1.0]])],"derivedFrom":subQ1}),1.0]])]});}
            var Q80;
            {var subQ0=sQuery(id+"F0.wireOp",EDGE,"E14.22.0");var subQ1=sQuery(id+"F0.wireOp",EDGE,"E0");var subQ2=makeQuery(id+"F0.imprint","INTERSECT",VERTEX,{"derivedFrom":[subQ1,subQ0]});Q80=makeQuery(id+"F0.imprint","IMPRINT",FACE,{"disambiguationData":[TD([[makeQuery(id+"F0.imprint","IMPRINT",EDGE,{"disambiguationData":[TD([[subQ2,-1.0]])],"derivedFrom":subQ1}),-1.0]])]});}
            var Q81;
            {var subQ0=sQuery(id+"F0.wireOp",EDGE,"E14.22.1");var subQ1=sQuery(id+"F0.wireOp",EDGE,"E0");var subQ2=makeQuery(id+"F0.imprint","INTERSECT",VERTEX,{"derivedFrom":[subQ1,subQ0]});Q81=makeQuery(id+"F0.imprint","IMPRINT",FACE,{"disambiguationData":[TD([[makeQuery(id+"F0.imprint","IMPRINT",EDGE,{"disambiguationData":[TD([[subQ2,-1.0]])],"derivedFrom":subQ1}),1.0]])]});}
            var Q82;
            {var subQ0=sQuery(id+"F0.wireOp",EDGE,"E14.21.0");var subQ1=sQuery(id+"F0.wireOp",EDGE,"E0");var subQ2=makeQuery(id+"F0.imprint","INTERSECT",VERTEX,{"derivedFrom":[subQ1,subQ0]});Q82=makeQuery(id+"F0.imprint","IMPRINT",FACE,{"disambiguationData":[TD([[makeQuery(id+"F0.imprint","IMPRINT",EDGE,{"disambiguationData":[TD([[subQ2,-1.0]])],"derivedFrom":subQ1}),-1.0]])]});}
            var Q83;
            {var subQ0=sQuery(id+"F0.wireOp",EDGE,"E14.21.1");var subQ1=sQuery(id+"F0.wireOp",EDGE,"E0");var subQ2=makeQuery(id+"F0.imprint","INTERSECT",VERTEX,{"derivedFrom":[subQ1,subQ0]});Q83=makeQuery(id+"F0.imprint","IMPRINT",FACE,{"disambiguationData":[TD([[makeQuery(id+"F0.imprint","IMPRINT",EDGE,{"disambiguationData":[TD([[subQ2,-1.0]])],"derivedFrom":subQ1}),1.0]])]});}
            var Q84;
            {var subQ0=sQuery(id+"F0.wireOp",EDGE,"E14.20.0");var subQ1=sQuery(id+"F0.wireOp",EDGE,"E0");var subQ2=makeQuery(id+"F0.imprint","INTERSECT",VERTEX,{"derivedFrom":[subQ1,subQ0]});Q84=makeQuery(id+"F0.imprint","IMPRINT",FACE,{"disambiguationData":[TD([[makeQuery(id+"F0.imprint","IMPRINT",EDGE,{"disambiguationData":[TD([[subQ2,-1.0]])],"derivedFrom":subQ1}),-1.0]])]});}
            var Q85;
            {var subQ0=sQuery(id+"F0.wireOp",EDGE,"E14.20.1");var subQ1=sQuery(id+"F0.wireOp",EDGE,"E0");var subQ2=makeQuery(id+"F0.imprint","INTERSECT",VERTEX,{"derivedFrom":[subQ1,subQ0]});Q85=makeQuery(id+"F0.imprint","IMPRINT",FACE,{"disambiguationData":[TD([[makeQuery(id+"F0.imprint","IMPRINT",EDGE,{"disambiguationData":[TD([[subQ2,-1.0]])],"derivedFrom":subQ1}),1.0]])]});}
            var Q86;
            {var subQ0=sQuery(id+"F0.wireOp",EDGE,"E14.19.0");var subQ1=sQuery(id+"F0.wireOp",EDGE,"E0");var subQ2=makeQuery(id+"F0.imprint","INTERSECT",VERTEX,{"derivedFrom":[subQ1,subQ0]});Q86=makeQuery(id+"F0.imprint","IMPRINT",FACE,{"disambiguationData":[TD([[makeQuery(id+"F0.imprint","IMPRINT",EDGE,{"disambiguationData":[TD([[subQ2,-1.0]])],"derivedFrom":subQ1}),-1.0]])]});}
            var Q87;
            {var subQ0=sQuery(id+"F0.wireOp",EDGE,"E14.19.1");var subQ1=sQuery(id+"F0.wireOp",EDGE,"E0");var subQ2=makeQuery(id+"F0.imprint","INTERSECT",VERTEX,{"derivedFrom":[subQ1,subQ0]});Q87=makeQuery(id+"F0.imprint","IMPRINT",FACE,{"disambiguationData":[TD([[makeQuery(id+"F0.imprint","IMPRINT",EDGE,{"disambiguationData":[TD([[subQ2,-1.0]])],"derivedFrom":subQ1}),1.0]])]});}
            var Q88;
            {var subQ0=sQuery(id+"F0.wireOp",EDGE,"E14.18.0");var subQ1=sQuery(id+"F0.wireOp",EDGE,"E0");var subQ2=makeQuery(id+"F0.imprint","INTERSECT",VERTEX,{"derivedFrom":[subQ1,subQ0]});Q88=makeQuery(id+"F0.imprint","IMPRINT",FACE,{"disambiguationData":[TD([[makeQuery(id+"F0.imprint","IMPRINT",EDGE,{"disambiguationData":[TD([[subQ2,-1.0]])],"derivedFrom":subQ1}),-1.0]])]});}
            var Q89;
            {var subQ0=sQuery(id+"F0.wireOp",EDGE,"E14.18.1");var subQ1=sQuery(id+"F0.wireOp",EDGE,"E0");var subQ2=makeQuery(id+"F0.imprint","INTERSECT",VERTEX,{"derivedFrom":[subQ1,subQ0]});Q89=makeQuery(id+"F0.imprint","IMPRINT",FACE,{"disambiguationData":[TD([[makeQuery(id+"F0.imprint","IMPRINT",EDGE,{"disambiguationData":[TD([[subQ2,-1.0]])],"derivedFrom":subQ1}),1.0]])]});}
            var Q90;
            {var subQ5=sQuery(id+"F0.wireOp",EDGE,"E14.17.5");Q90=makeQuery(id+"F0.imprint","IMPRINT",FACE,{"disambiguationData":[TD([[makeQuery(id+"F0.imprint","IMPRINT",EDGE,{"derivedFrom":subQ5}),-1.0]])]});}
            var Q91;
            {var subQ0=sQuery(id+"F0.wireOp",EDGE,"E14.17.1");var subQ1=sQuery(id+"F0.wireOp",EDGE,"E0");var subQ2=makeQuery(id+"F0.imprint","INTERSECT",VERTEX,{"derivedFrom":[subQ1,subQ0]});Q91=makeQuery(id+"F0.imprint","IMPRINT",FACE,{"disambiguationData":[TD([[makeQuery(id+"F0.imprint","IMPRINT",EDGE,{"disambiguationData":[TD([[subQ2,-1.0]])],"derivedFrom":subQ1}),1.0]])]});}
            var Q92;
            {var subQ0=sQuery(id+"F0.wireOp",EDGE,"E14.16.0");var subQ1=sQuery(id+"F0.wireOp",EDGE,"E0");var subQ2=makeQuery(id+"F0.imprint","INTERSECT",VERTEX,{"derivedFrom":[subQ1,subQ0]});Q92=makeQuery(id+"F0.imprint","IMPRINT",FACE,{"disambiguationData":[TD([[makeQuery(id+"F0.imprint","IMPRINT",EDGE,{"disambiguationData":[TD([[subQ2,-1.0]])],"derivedFrom":subQ1}),-1.0]])]});}
            var Q93;
            {var subQ0=sQuery(id+"F0.wireOp",EDGE,"E14.16.1");var subQ1=sQuery(id+"F0.wireOp",EDGE,"E0");var subQ2=makeQuery(id+"F0.imprint","INTERSECT",VERTEX,{"derivedFrom":[subQ1,subQ0]});Q93=makeQuery(id+"F0.imprint","IMPRINT",FACE,{"disambiguationData":[TD([[makeQuery(id+"F0.imprint","IMPRINT",EDGE,{"disambiguationData":[TD([[subQ2,-1.0]])],"derivedFrom":subQ1}),1.0]])]});}
            var Q94;
            {var subQ0=sQuery(id+"F0.wireOp",EDGE,"E14.15.0");var subQ1=sQuery(id+"F0.wireOp",EDGE,"E0");var subQ2=makeQuery(id+"F0.imprint","INTERSECT",VERTEX,{"derivedFrom":[subQ1,subQ0]});Q94=makeQuery(id+"F0.imprint","IMPRINT",FACE,{"disambiguationData":[TD([[makeQuery(id+"F0.imprint","IMPRINT",EDGE,{"disambiguationData":[TD([[subQ2,-1.0]])],"derivedFrom":subQ1}),-1.0]])]});}
            var Q95;
            {var subQ0=sQuery(id+"F0.wireOp",EDGE,"E14.15.1");var subQ1=sQuery(id+"F0.wireOp",EDGE,"E0");var subQ2=makeQuery(id+"F0.imprint","INTERSECT",VERTEX,{"derivedFrom":[subQ1,subQ0]});Q95=makeQuery(id+"F0.imprint","IMPRINT",FACE,{"disambiguationData":[TD([[makeQuery(id+"F0.imprint","IMPRINT",EDGE,{"disambiguationData":[TD([[subQ2,-1.0]])],"derivedFrom":subQ1}),1.0]])]});}
            var Q96;
            {var subQ0=sQuery(id+"F0.wireOp",EDGE,"E14.14.0");var subQ1=sQuery(id+"F0.wireOp",EDGE,"E0");var subQ2=makeQuery(id+"F0.imprint","INTERSECT",VERTEX,{"derivedFrom":[subQ1,subQ0]});Q96=makeQuery(id+"F0.imprint","IMPRINT",FACE,{"disambiguationData":[TD([[makeQuery(id+"F0.imprint","IMPRINT",EDGE,{"disambiguationData":[TD([[subQ2,-1.0]])],"derivedFrom":subQ1}),-1.0]])]});}
            var Q97;
            {var subQ0=sQuery(id+"F0.wireOp",EDGE,"E14.14.1");var subQ1=sQuery(id+"F0.wireOp",EDGE,"E0");var subQ2=makeQuery(id+"F0.imprint","INTERSECT",VERTEX,{"derivedFrom":[subQ1,subQ0]});Q97=makeQuery(id+"F0.imprint","IMPRINT",FACE,{"disambiguationData":[TD([[makeQuery(id+"F0.imprint","IMPRINT",EDGE,{"disambiguationData":[TD([[subQ2,-1.0]])],"derivedFrom":subQ1}),1.0]])]});}
            var Q98;
            {var subQ0=sQuery(id+"F0.wireOp",EDGE,"E14.13.0");var subQ1=sQuery(id+"F0.wireOp",EDGE,"E0");var subQ2=makeQuery(id+"F0.imprint","INTERSECT",VERTEX,{"derivedFrom":[subQ1,subQ0]});Q98=makeQuery(id+"F0.imprint","IMPRINT",FACE,{"disambiguationData":[TD([[makeQuery(id+"F0.imprint","IMPRINT",EDGE,{"disambiguationData":[TD([[subQ2,-1.0]])],"derivedFrom":subQ1}),-1.0]])]});}
            var Q99;
            {var subQ0=sQuery(id+"F0.wireOp",EDGE,"E14.13.1");var subQ1=sQuery(id+"F0.wireOp",EDGE,"E0");var subQ2=makeQuery(id+"F0.imprint","INTERSECT",VERTEX,{"derivedFrom":[subQ1,subQ0]});Q99=makeQuery(id+"F0.imprint","IMPRINT",FACE,{"disambiguationData":[TD([[makeQuery(id+"F0.imprint","IMPRINT",EDGE,{"disambiguationData":[TD([[subQ2,-1.0]])],"derivedFrom":subQ1}),1.0]])]});}
            var Q100;
            {var subQ0=sQuery(id+"F0.wireOp",EDGE,"E14.12.0");var subQ1=sQuery(id+"F0.wireOp",EDGE,"E0");var subQ2=makeQuery(id+"F0.imprint","INTERSECT",VERTEX,{"derivedFrom":[subQ1,subQ0]});Q100=makeQuery(id+"F0.imprint","IMPRINT",FACE,{"disambiguationData":[TD([[makeQuery(id+"F0.imprint","IMPRINT",EDGE,{"disambiguationData":[TD([[subQ2,-1.0]])],"derivedFrom":subQ1}),-1.0]])]});}
            var Q101;
            {var subQ0=sQuery(id+"F0.wireOp",EDGE,"E14.12.1");var subQ1=sQuery(id+"F0.wireOp",EDGE,"E0");var subQ2=makeQuery(id+"F0.imprint","INTERSECT",VERTEX,{"derivedFrom":[subQ1,subQ0]});Q101=makeQuery(id+"F0.imprint","IMPRINT",FACE,{"disambiguationData":[TD([[makeQuery(id+"F0.imprint","IMPRINT",EDGE,{"disambiguationData":[TD([[subQ2,-1.0]])],"derivedFrom":subQ1}),1.0]])]});}
            var Q102;
            {var subQ0=sQuery(id+"F0.wireOp",EDGE,"E14.11.0");var subQ1=sQuery(id+"F0.wireOp",EDGE,"E0");var subQ2=makeQuery(id+"F0.imprint","INTERSECT",VERTEX,{"derivedFrom":[subQ1,subQ0]});Q102=makeQuery(id+"F0.imprint","IMPRINT",FACE,{"disambiguationData":[TD([[makeQuery(id+"F0.imprint","IMPRINT",EDGE,{"disambiguationData":[TD([[subQ2,-1.0]])],"derivedFrom":subQ1}),-1.0]])]});}
            var Q103;
            {var subQ0=sQuery(id+"F0.wireOp",EDGE,"E14.11.1");var subQ1=sQuery(id+"F0.wireOp",EDGE,"E0");var subQ2=makeQuery(id+"F0.imprint","INTERSECT",VERTEX,{"derivedFrom":[subQ1,subQ0]});Q103=makeQuery(id+"F0.imprint","IMPRINT",FACE,{"disambiguationData":[TD([[makeQuery(id+"F0.imprint","IMPRINT",EDGE,{"disambiguationData":[TD([[subQ2,-1.0]])],"derivedFrom":subQ1}),1.0]])]});}
            var Q104;
            {var subQ0=sQuery(id+"F0.wireOp",EDGE,"E14.10.0");var subQ1=sQuery(id+"F0.wireOp",EDGE,"E0");var subQ2=makeQuery(id+"F0.imprint","INTERSECT",VERTEX,{"derivedFrom":[subQ1,subQ0]});Q104=makeQuery(id+"F0.imprint","IMPRINT",FACE,{"disambiguationData":[TD([[makeQuery(id+"F0.imprint","IMPRINT",EDGE,{"disambiguationData":[TD([[subQ2,-1.0]])],"derivedFrom":subQ1}),-1.0]])]});}
            var Q105;
            {var subQ0=sQuery(id+"F0.wireOp",EDGE,"E14.10.1");var subQ1=sQuery(id+"F0.wireOp",EDGE,"E0");var subQ2=makeQuery(id+"F0.imprint","INTERSECT",VERTEX,{"derivedFrom":[subQ1,subQ0]});Q105=makeQuery(id+"F0.imprint","IMPRINT",FACE,{"disambiguationData":[TD([[makeQuery(id+"F0.imprint","IMPRINT",EDGE,{"disambiguationData":[TD([[subQ2,-1.0]])],"derivedFrom":subQ1}),1.0]])]});}
            var Q106;
            {var subQ0=sQuery(id+"F0.wireOp",EDGE,"E14.9.0");var subQ1=sQuery(id+"F0.wireOp",EDGE,"E0");var subQ2=makeQuery(id+"F0.imprint","INTERSECT",VERTEX,{"derivedFrom":[subQ1,subQ0]});Q106=makeQuery(id+"F0.imprint","IMPRINT",FACE,{"disambiguationData":[TD([[makeQuery(id+"F0.imprint","IMPRINT",EDGE,{"disambiguationData":[TD([[subQ2,-1.0]])],"derivedFrom":subQ1}),-1.0]])]});}
            var Q107;
            {var subQ0=sQuery(id+"F0.wireOp",EDGE,"E14.9.1");var subQ1=sQuery(id+"F0.wireOp",EDGE,"E0");var subQ2=makeQuery(id+"F0.imprint","INTERSECT",VERTEX,{"derivedFrom":[subQ1,subQ0]});Q107=makeQuery(id+"F0.imprint","IMPRINT",FACE,{"disambiguationData":[TD([[makeQuery(id+"F0.imprint","IMPRINT",EDGE,{"disambiguationData":[TD([[subQ2,-1.0]])],"derivedFrom":subQ1}),1.0]])]});}
            var Q108;
            {var subQ5=sQuery(id+"F0.wireOp",EDGE,"E14.8.5");Q108=makeQuery(id+"F0.imprint","IMPRINT",FACE,{"disambiguationData":[TD([[makeQuery(id+"F0.imprint","IMPRINT",EDGE,{"derivedFrom":subQ5}),-1.0]])]});}
            var Q109;
            {var subQ0=sQuery(id+"F0.wireOp",EDGE,"E2.left");Q109=makeQuery(id+"F0.imprint","IMPRINT",FACE,{"disambiguationData":[TD([[makeQuery(id+"F0.imprint","IMPRINT",EDGE,{"derivedFrom":subQ0}),-1.0]])]});}
            var Q110;
            {var subQ0=sQuery(id+"F0.wireOp",EDGE,"E6.1.0");Q110=makeQuery(id+"F0.imprint","IMPRINT",FACE,{"disambiguationData":[TD([[makeQuery(id+"F0.imprint","IMPRINT",EDGE,{"derivedFrom":subQ0}),1.0]])]});}
            var Q111;
            {var subQ0=sQuery(id+"F0.wireOp",EDGE,"E6.2.0");Q111=makeQuery(id+"F0.imprint","IMPRINT",FACE,{"disambiguationData":[TD([[makeQuery(id+"F0.imprint","IMPRINT",EDGE,{"derivedFrom":subQ0}),1.0]])]});}
            var Q112;
            {var subQ0=sQuery(id+"F0.wireOp",EDGE,"E6.3.0");Q112=makeQuery(id+"F0.imprint","IMPRINT",FACE,{"disambiguationData":[TD([[makeQuery(id+"F0.imprint","IMPRINT",EDGE,{"derivedFrom":subQ0}),1.0]])]});}
            var Q113;
            {var subQ0=sQuery(id+"F0.wireOp",EDGE,"E9.top");Q113=makeQuery(id+"F0.imprint","IMPRINT",FACE,{"disambiguationData":[TD([[makeQuery(id+"F0.imprint","IMPRINT",EDGE,{"derivedFrom":subQ0}),-1.0]])]});}
            var Q114;
            {var subQ0=sQuery(id+"F0.wireOp",EDGE,"E14.1.5");Q114=makeQuery(id+"F0.imprint","IMPRINT",FACE,{"disambiguationData":[TD([[makeQuery(id+"F0.imprint","IMPRINT",EDGE,{"derivedFrom":subQ0}),-1.0]])]});}
            var Q115;
            {var subQ0=sQuery(id+"F0.wireOp",EDGE,"E14.2.5");Q115=makeQuery(id+"F0.imprint","IMPRINT",FACE,{"disambiguationData":[TD([[makeQuery(id+"F0.imprint","IMPRINT",EDGE,{"derivedFrom":subQ0}),-1.0]])]});}
            var Q116;
            {var subQ0=sQuery(id+"F0.wireOp",EDGE,"E14.3.5");Q116=makeQuery(id+"F0.imprint","IMPRINT",FACE,{"disambiguationData":[TD([[makeQuery(id+"F0.imprint","IMPRINT",EDGE,{"derivedFrom":subQ0}),-1.0]])]});}
            var Q117;
            {var subQ0=sQuery(id+"F0.wireOp",EDGE,"E14.4.5");Q117=makeQuery(id+"F0.imprint","IMPRINT",FACE,{"disambiguationData":[TD([[makeQuery(id+"F0.imprint","IMPRINT",EDGE,{"derivedFrom":subQ0}),-1.0]])]});}
            var Q118;
            {var subQ0=sQuery(id+"F0.wireOp",EDGE,"E14.5.5");Q118=makeQuery(id+"F0.imprint","IMPRINT",FACE,{"disambiguationData":[TD([[makeQuery(id+"F0.imprint","IMPRINT",EDGE,{"derivedFrom":subQ0}),-1.0]])]});}
            var Q119;
            {var subQ0=sQuery(id+"F0.wireOp",EDGE,"E14.6.5");Q119=makeQuery(id+"F0.imprint","IMPRINT",FACE,{"disambiguationData":[TD([[makeQuery(id+"F0.imprint","IMPRINT",EDGE,{"derivedFrom":subQ0}),-1.0]])]});}
            var Q120;
            {var subQ0=sQuery(id+"F0.wireOp",EDGE,"E14.7.5");Q120=makeQuery(id+"F0.imprint","IMPRINT",FACE,{"disambiguationData":[TD([[makeQuery(id+"F0.imprint","IMPRINT",EDGE,{"derivedFrom":subQ0}),-1.0]])]});}
            var Q121;
            {var subQ0=sQuery(id+"F0.wireOp",EDGE,"E14.9.5");Q121=makeQuery(id+"F0.imprint","IMPRINT",FACE,{"disambiguationData":[TD([[makeQuery(id+"F0.imprint","IMPRINT",EDGE,{"derivedFrom":subQ0}),-1.0]])]});}
            var Q122;
            {var subQ0=sQuery(id+"F0.wireOp",EDGE,"E14.10.5");Q122=makeQuery(id+"F0.imprint","IMPRINT",FACE,{"disambiguationData":[TD([[makeQuery(id+"F0.imprint","IMPRINT",EDGE,{"derivedFrom":subQ0}),-1.0]])]});}
            var Q123;
            {var subQ0=sQuery(id+"F0.wireOp",EDGE,"E14.11.5");Q123=makeQuery(id+"F0.imprint","IMPRINT",FACE,{"disambiguationData":[TD([[makeQuery(id+"F0.imprint","IMPRINT",EDGE,{"derivedFrom":subQ0}),-1.0]])]});}
            var Q124;
            {var subQ0=sQuery(id+"F0.wireOp",EDGE,"E14.12.5");Q124=makeQuery(id+"F0.imprint","IMPRINT",FACE,{"disambiguationData":[TD([[makeQuery(id+"F0.imprint","IMPRINT",EDGE,{"derivedFrom":subQ0}),-1.0]])]});}
            var Q125;
            {var subQ0=sQuery(id+"F0.wireOp",EDGE,"E14.13.5");Q125=makeQuery(id+"F0.imprint","IMPRINT",FACE,{"disambiguationData":[TD([[makeQuery(id+"F0.imprint","IMPRINT",EDGE,{"derivedFrom":subQ0}),-1.0]])]});}
            var Q126;
            {var subQ0=sQuery(id+"F0.wireOp",EDGE,"E14.14.5");Q126=makeQuery(id+"F0.imprint","IMPRINT",FACE,{"disambiguationData":[TD([[makeQuery(id+"F0.imprint","IMPRINT",EDGE,{"derivedFrom":subQ0}),-1.0]])]});}
            var Q127;
            {var subQ0=sQuery(id+"F0.wireOp",EDGE,"E14.15.5");Q127=makeQuery(id+"F0.imprint","IMPRINT",FACE,{"disambiguationData":[TD([[makeQuery(id+"F0.imprint","IMPRINT",EDGE,{"derivedFrom":subQ0}),-1.0]])]});}
            var Q128;
            {var subQ0=sQuery(id+"F0.wireOp",EDGE,"E14.16.5");Q128=makeQuery(id+"F0.imprint","IMPRINT",FACE,{"disambiguationData":[TD([[makeQuery(id+"F0.imprint","IMPRINT",EDGE,{"derivedFrom":subQ0}),-1.0]])]});}
            var Q129;
            {var subQ0=sQuery(id+"F0.wireOp",EDGE,"E14.18.5");Q129=makeQuery(id+"F0.imprint","IMPRINT",FACE,{"disambiguationData":[TD([[makeQuery(id+"F0.imprint","IMPRINT",EDGE,{"derivedFrom":subQ0}),-1.0]])]});}
            var Q130;
            {var subQ0=sQuery(id+"F0.wireOp",EDGE,"E14.19.5");Q130=makeQuery(id+"F0.imprint","IMPRINT",FACE,{"disambiguationData":[TD([[makeQuery(id+"F0.imprint","IMPRINT",EDGE,{"derivedFrom":subQ0}),-1.0]])]});}
            var Q131;
            {var subQ0=sQuery(id+"F0.wireOp",EDGE,"E14.20.5");Q131=makeQuery(id+"F0.imprint","IMPRINT",FACE,{"disambiguationData":[TD([[makeQuery(id+"F0.imprint","IMPRINT",EDGE,{"derivedFrom":subQ0}),-1.0]])]});}
            var Q132;
            {var subQ0=sQuery(id+"F0.wireOp",EDGE,"E14.21.5");Q132=makeQuery(id+"F0.imprint","IMPRINT",FACE,{"disambiguationData":[TD([[makeQuery(id+"F0.imprint","IMPRINT",EDGE,{"derivedFrom":subQ0}),-1.0]])]});}
            var Q133;
            {var subQ0=sQuery(id+"F0.wireOp",EDGE,"E14.22.5");Q133=makeQuery(id+"F0.imprint","IMPRINT",FACE,{"disambiguationData":[TD([[makeQuery(id+"F0.imprint","IMPRINT",EDGE,{"derivedFrom":subQ0}),-1.0]])]});}
            var Q134;
            {var subQ0=sQuery(id+"F0.wireOp",EDGE,"E14.23.5");Q134=makeQuery(id+"F0.imprint","IMPRINT",FACE,{"disambiguationData":[TD([[makeQuery(id+"F0.imprint","IMPRINT",EDGE,{"derivedFrom":subQ0}),-1.0]])]});}
            var Q135;
            {var subQ0=sQuery(id+"F0.wireOp",EDGE,"E14.24.5");Q135=makeQuery(id+"F0.imprint","IMPRINT",FACE,{"disambiguationData":[TD([[makeQuery(id+"F0.imprint","IMPRINT",EDGE,{"derivedFrom":subQ0}),-1.0]])]});}
            var Q136;
            {var subQ0=sQuery(id+"F0.wireOp",EDGE,"E14.25.5");Q136=makeQuery(id+"F0.imprint","IMPRINT",FACE,{"disambiguationData":[TD([[makeQuery(id+"F0.imprint","IMPRINT",EDGE,{"derivedFrom":subQ0}),-1.0]])]});}
            var Q137;
            {var subQ0=sQuery(id+"F0.wireOp",EDGE,"E14.27.5");Q137=makeQuery(id+"F0.imprint","IMPRINT",FACE,{"disambiguationData":[TD([[makeQuery(id+"F0.imprint","IMPRINT",EDGE,{"derivedFrom":subQ0}),-1.0]])]});}
            var Q138;
            {var subQ0=sQuery(id+"F0.wireOp",EDGE,"E14.28.5");Q138=makeQuery(id+"F0.imprint","IMPRINT",FACE,{"disambiguationData":[TD([[makeQuery(id+"F0.imprint","IMPRINT",EDGE,{"derivedFrom":subQ0}),-1.0]])]});}
            var Q139;
            {var subQ0=sQuery(id+"F0.wireOp",EDGE,"E14.29.5");Q139=makeQuery(id+"F0.imprint","IMPRINT",FACE,{"disambiguationData":[TD([[makeQuery(id+"F0.imprint","IMPRINT",EDGE,{"derivedFrom":subQ0}),-1.0]])]});}
            var Q140;
            {var subQ0=sQuery(id+"F0.wireOp",EDGE,"E14.30.5");Q140=makeQuery(id+"F0.imprint","IMPRINT",FACE,{"disambiguationData":[TD([[makeQuery(id+"F0.imprint","IMPRINT",EDGE,{"derivedFrom":subQ0}),-1.0]])]});}
            var Q141;
            {var subQ0=sQuery(id+"F0.wireOp",EDGE,"E14.31.5");Q141=makeQuery(id+"F0.imprint","IMPRINT",FACE,{"disambiguationData":[TD([[makeQuery(id+"F0.imprint","IMPRINT",EDGE,{"derivedFrom":subQ0}),-1.0]])]});}
            var Q142;
            {var subQ0=sQuery(id+"F0.wireOp",EDGE,"E14.32.5");Q142=makeQuery(id+"F0.imprint","IMPRINT",FACE,{"disambiguationData":[TD([[makeQuery(id+"F0.imprint","IMPRINT",EDGE,{"derivedFrom":subQ0}),-1.0]])]});}
            var Q143;
            {var subQ0=sQuery(id+"F0.wireOp",EDGE,"E14.33.5");Q143=makeQuery(id+"F0.imprint","IMPRINT",FACE,{"disambiguationData":[TD([[makeQuery(id+"F0.imprint","IMPRINT",EDGE,{"derivedFrom":subQ0}),-1.0]])]});}
            var Q144;
            {var subQ0=sQuery(id+"F0.wireOp",EDGE,"E14.34.5");Q144=makeQuery(id+"F0.imprint","IMPRINT",FACE,{"disambiguationData":[TD([[makeQuery(id+"F0.imprint","IMPRINT",EDGE,{"derivedFrom":subQ0}),-1.0]])]});}
            var Q145;
            {var subQ5=sQuery(id+"F0.wireOp",EDGE,"E0");var subQ7=sQuery(id+"F0.wireOp",EDGE,"E14.7.0");var subQ9=makeQuery(id+"F0.imprint","INTERSECT",VERTEX,{"derivedFrom":[subQ5,subQ7]});Q145=makeQuery(id+"F0.imprint","IMPRINT",FACE,{"disambiguationData":[TD([[makeQuery(id+"F0.imprint","IMPRINT",EDGE,{"disambiguationData":[TD([[subQ9,-1.0]])],"derivedFrom":subQ5}),1.0]])]});}
            var Q146;
            {var subQ1=sQuery(id+"F0.wireOp",EDGE,"E0");var subQ5=sQuery(id+"F0.wireOp",EDGE,"E14.6.0");var subQ6=makeQuery(id+"F0.imprint","INTERSECT",VERTEX,{"derivedFrom":[subQ1,subQ5]});Q146=makeQuery(id+"F0.imprint","IMPRINT",FACE,{"disambiguationData":[TD([[makeQuery(id+"F0.imprint","IMPRINT",EDGE,{"disambiguationData":[TD([[subQ6,-1.0]])],"derivedFrom":subQ1}),1.0]])]});}
            var Q147;
            {var subQ1=sQuery(id+"F0.wireOp",EDGE,"E0");var subQ5=sQuery(id+"F0.wireOp",EDGE,"E14.5.0");var subQ6=makeQuery(id+"F0.imprint","INTERSECT",VERTEX,{"derivedFrom":[subQ1,subQ5]});Q147=makeQuery(id+"F0.imprint","IMPRINT",FACE,{"disambiguationData":[TD([[makeQuery(id+"F0.imprint","IMPRINT",EDGE,{"disambiguationData":[TD([[subQ6,-1.0]])],"derivedFrom":subQ1}),1.0]])]});}
            var Q148;
            {var subQ1=sQuery(id+"F0.wireOp",EDGE,"E0");var subQ5=sQuery(id+"F0.wireOp",EDGE,"E14.4.0");var subQ6=makeQuery(id+"F0.imprint","INTERSECT",VERTEX,{"derivedFrom":[subQ1,subQ5]});Q148=makeQuery(id+"F0.imprint","IMPRINT",FACE,{"disambiguationData":[TD([[makeQuery(id+"F0.imprint","IMPRINT",EDGE,{"disambiguationData":[TD([[subQ6,-1.0]])],"derivedFrom":subQ1}),1.0]])]});}
            var Q149;
            {var subQ1=sQuery(id+"F0.wireOp",EDGE,"E0");var subQ5=sQuery(id+"F0.wireOp",EDGE,"E14.3.0");var subQ6=makeQuery(id+"F0.imprint","INTERSECT",VERTEX,{"derivedFrom":[subQ1,subQ5]});Q149=makeQuery(id+"F0.imprint","IMPRINT",FACE,{"disambiguationData":[TD([[makeQuery(id+"F0.imprint","IMPRINT",EDGE,{"disambiguationData":[TD([[subQ6,-1.0]])],"derivedFrom":subQ1}),1.0]])]});}
            var Q150;
            {var subQ5=sQuery(id+"F0.wireOp",EDGE,"E0");var subQ7=sQuery(id+"F0.wireOp",EDGE,"E14.2.0");var subQ8=makeQuery(id+"F0.imprint","INTERSECT",VERTEX,{"derivedFrom":[subQ5,subQ7]});Q150=makeQuery(id+"F0.imprint","IMPRINT",FACE,{"disambiguationData":[TD([[makeQuery(id+"F0.imprint","IMPRINT",EDGE,{"disambiguationData":[TD([[subQ8,-1.0]])],"derivedFrom":subQ5}),1.0]])]});}
            var Q151;
            {var subQ1=sQuery(id+"F0.wireOp",EDGE,"E0");var subQ5=sQuery(id+"F0.wireOp",EDGE,"E14.1.0");var subQ6=makeQuery(id+"F0.imprint","INTERSECT",VERTEX,{"derivedFrom":[subQ1,subQ5]});Q151=makeQuery(id+"F0.imprint","IMPRINT",FACE,{"disambiguationData":[TD([[makeQuery(id+"F0.imprint","IMPRINT",EDGE,{"disambiguationData":[TD([[subQ6,-1.0]])],"derivedFrom":subQ1}),1.0]])]});}
            var Q152;
            {var subQ1=sQuery(id+"F0.wireOp",EDGE,"E9.right");var subQ5=sQuery(id+"F0.wireOp",EDGE,"E0");var subQ6=makeQuery(id+"F0.imprint","INTERSECT",VERTEX,{"derivedFrom":[subQ5,subQ1]});Q152=makeQuery(id+"F0.imprint","IMPRINT",FACE,{"disambiguationData":[TD([[makeQuery(id+"F0.imprint","IMPRINT",EDGE,{"disambiguationData":[TD([[subQ6,-1.0]])],"derivedFrom":subQ5}),1.0]])]});}
            var Q153;
            {var subQ0=sQuery(id+"F0.wireOp",EDGE,"E14.35.0");var subQ1=sQuery(id+"F0.wireOp",EDGE,"E0");var subQ2=makeQuery(id+"F0.imprint","INTERSECT",VERTEX,{"derivedFrom":[subQ1,subQ0]});Q153=makeQuery(id+"F0.imprint","IMPRINT",FACE,{"disambiguationData":[TD([[makeQuery(id+"F0.imprint","IMPRINT",EDGE,{"disambiguationData":[TD([[subQ2,-1.0]])],"derivedFrom":subQ1}),1.0]])]});}
            var Q154;
            {var subQ1=sQuery(id+"F0.wireOp",EDGE,"E0");var subQ7=sQuery(id+"F0.wireOp",EDGE,"E14.34.0");var subQ9=makeQuery(id+"F0.imprint","INTERSECT",VERTEX,{"derivedFrom":[subQ1,subQ7]});Q154=makeQuery(id+"F0.imprint","IMPRINT",FACE,{"disambiguationData":[TD([[makeQuery(id+"F0.imprint","IMPRINT",EDGE,{"disambiguationData":[TD([[subQ9,-1.0]])],"derivedFrom":subQ1}),1.0]])]});}
            var Q155;
            {var subQ5=sQuery(id+"F0.wireOp",EDGE,"E0");var subQ7=sQuery(id+"F0.wireOp",EDGE,"E14.33.0");var subQ8=makeQuery(id+"F0.imprint","INTERSECT",VERTEX,{"derivedFrom":[subQ5,subQ7]});Q155=makeQuery(id+"F0.imprint","IMPRINT",FACE,{"disambiguationData":[TD([[makeQuery(id+"F0.imprint","IMPRINT",EDGE,{"disambiguationData":[TD([[subQ8,-1.0]])],"derivedFrom":subQ5}),1.0]])]});}
            var Q156;
            {var subQ1=sQuery(id+"F0.wireOp",EDGE,"E0");var subQ5=sQuery(id+"F0.wireOp",EDGE,"E14.32.0");var subQ6=makeQuery(id+"F0.imprint","INTERSECT",VERTEX,{"derivedFrom":[subQ1,subQ5]});Q156=makeQuery(id+"F0.imprint","IMPRINT",FACE,{"disambiguationData":[TD([[makeQuery(id+"F0.imprint","IMPRINT",EDGE,{"disambiguationData":[TD([[subQ6,-1.0]])],"derivedFrom":subQ1}),1.0]])]});}
            var Q157;
            {var subQ1=sQuery(id+"F0.wireOp",EDGE,"E0");var subQ5=sQuery(id+"F0.wireOp",EDGE,"E14.31.0");var subQ6=makeQuery(id+"F0.imprint","INTERSECT",VERTEX,{"derivedFrom":[subQ1,subQ5]});Q157=makeQuery(id+"F0.imprint","IMPRINT",FACE,{"disambiguationData":[TD([[makeQuery(id+"F0.imprint","IMPRINT",EDGE,{"disambiguationData":[TD([[subQ6,-1.0]])],"derivedFrom":subQ1}),1.0]])]});}
            var Q158;
            {var subQ1=sQuery(id+"F0.wireOp",EDGE,"E0");var subQ5=sQuery(id+"F0.wireOp",EDGE,"E14.30.0");var subQ6=makeQuery(id+"F0.imprint","INTERSECT",VERTEX,{"derivedFrom":[subQ1,subQ5]});Q158=makeQuery(id+"F0.imprint","IMPRINT",FACE,{"disambiguationData":[TD([[makeQuery(id+"F0.imprint","IMPRINT",EDGE,{"disambiguationData":[TD([[subQ6,-1.0]])],"derivedFrom":subQ1}),1.0]])]});}
            var Q159;
            {var subQ1=sQuery(id+"F0.wireOp",EDGE,"E0");var subQ5=sQuery(id+"F0.wireOp",EDGE,"E14.29.0");var subQ6=makeQuery(id+"F0.imprint","INTERSECT",VERTEX,{"derivedFrom":[subQ1,subQ5]});Q159=makeQuery(id+"F0.imprint","IMPRINT",FACE,{"disambiguationData":[TD([[makeQuery(id+"F0.imprint","IMPRINT",EDGE,{"disambiguationData":[TD([[subQ6,-1.0]])],"derivedFrom":subQ1}),1.0]])]});}
            var Q160;
            {var subQ5=sQuery(id+"F0.wireOp",EDGE,"E0");var subQ7=sQuery(id+"F0.wireOp",EDGE,"E14.28.0");var subQ8=makeQuery(id+"F0.imprint","INTERSECT",VERTEX,{"derivedFrom":[subQ5,subQ7]});Q160=makeQuery(id+"F0.imprint","IMPRINT",FACE,{"disambiguationData":[TD([[makeQuery(id+"F0.imprint","IMPRINT",EDGE,{"disambiguationData":[TD([[subQ8,-1.0]])],"derivedFrom":subQ5}),1.0]])]});}
            var Q161;
            {var subQ1=sQuery(id+"F0.wireOp",EDGE,"E0");var subQ5=sQuery(id+"F0.wireOp",EDGE,"E14.27.0");var subQ6=makeQuery(id+"F0.imprint","INTERSECT",VERTEX,{"derivedFrom":[subQ1,subQ5]});Q161=makeQuery(id+"F0.imprint","IMPRINT",FACE,{"disambiguationData":[TD([[makeQuery(id+"F0.imprint","IMPRINT",EDGE,{"disambiguationData":[TD([[subQ6,-1.0]])],"derivedFrom":subQ1}),1.0]])]});}
            var Q162;
            {var subQ0=sQuery(id+"F0.wireOp",EDGE,"E14.26.0");var subQ1=sQuery(id+"F0.wireOp",EDGE,"E0");var subQ2=makeQuery(id+"F0.imprint","INTERSECT",VERTEX,{"derivedFrom":[subQ1,subQ0]});Q162=makeQuery(id+"F0.imprint","IMPRINT",FACE,{"disambiguationData":[TD([[makeQuery(id+"F0.imprint","IMPRINT",EDGE,{"disambiguationData":[TD([[subQ2,-1.0]])],"derivedFrom":subQ1}),1.0]])]});}
            var Q163;
            {var subQ1=sQuery(id+"F0.wireOp",EDGE,"E0");var subQ7=sQuery(id+"F0.wireOp",EDGE,"E14.25.0");var subQ9=makeQuery(id+"F0.imprint","INTERSECT",VERTEX,{"derivedFrom":[subQ1,subQ7]});Q163=makeQuery(id+"F0.imprint","IMPRINT",FACE,{"disambiguationData":[TD([[makeQuery(id+"F0.imprint","IMPRINT",EDGE,{"disambiguationData":[TD([[subQ9,-1.0]])],"derivedFrom":subQ1}),1.0]])]});}
            var Q164;
            {var subQ5=sQuery(id+"F0.wireOp",EDGE,"E0");var subQ7=sQuery(id+"F0.wireOp",EDGE,"E14.24.0");var subQ8=makeQuery(id+"F0.imprint","INTERSECT",VERTEX,{"derivedFrom":[subQ5,subQ7]});Q164=makeQuery(id+"F0.imprint","IMPRINT",FACE,{"disambiguationData":[TD([[makeQuery(id+"F0.imprint","IMPRINT",EDGE,{"disambiguationData":[TD([[subQ8,-1.0]])],"derivedFrom":subQ5}),1.0]])]});}
            var Q165;
            {var subQ1=sQuery(id+"F0.wireOp",EDGE,"E0");var subQ5=sQuery(id+"F0.wireOp",EDGE,"E14.23.0");var subQ6=makeQuery(id+"F0.imprint","INTERSECT",VERTEX,{"derivedFrom":[subQ1,subQ5]});Q165=makeQuery(id+"F0.imprint","IMPRINT",FACE,{"disambiguationData":[TD([[makeQuery(id+"F0.imprint","IMPRINT",EDGE,{"disambiguationData":[TD([[subQ6,-1.0]])],"derivedFrom":subQ1}),1.0]])]});}
            var Q166;
            {var subQ1=sQuery(id+"F0.wireOp",EDGE,"E0");var subQ5=sQuery(id+"F0.wireOp",EDGE,"E14.22.0");var subQ6=makeQuery(id+"F0.imprint","INTERSECT",VERTEX,{"derivedFrom":[subQ1,subQ5]});Q166=makeQuery(id+"F0.imprint","IMPRINT",FACE,{"disambiguationData":[TD([[makeQuery(id+"F0.imprint","IMPRINT",EDGE,{"disambiguationData":[TD([[subQ6,-1.0]])],"derivedFrom":subQ1}),1.0]])]});}
            var Q167;
            {var subQ1=sQuery(id+"F0.wireOp",EDGE,"E0");var subQ5=sQuery(id+"F0.wireOp",EDGE,"E14.21.0");var subQ6=makeQuery(id+"F0.imprint","INTERSECT",VERTEX,{"derivedFrom":[subQ1,subQ5]});Q167=makeQuery(id+"F0.imprint","IMPRINT",FACE,{"disambiguationData":[TD([[makeQuery(id+"F0.imprint","IMPRINT",EDGE,{"disambiguationData":[TD([[subQ6,-1.0]])],"derivedFrom":subQ1}),1.0]])]});}
            var Q168;
            {var subQ1=sQuery(id+"F0.wireOp",EDGE,"E0");var subQ5=sQuery(id+"F0.wireOp",EDGE,"E14.20.0");var subQ6=makeQuery(id+"F0.imprint","INTERSECT",VERTEX,{"derivedFrom":[subQ1,subQ5]});Q168=makeQuery(id+"F0.imprint","IMPRINT",FACE,{"disambiguationData":[TD([[makeQuery(id+"F0.imprint","IMPRINT",EDGE,{"disambiguationData":[TD([[subQ6,-1.0]])],"derivedFrom":subQ1}),1.0]])]});}
            var Q169;
            {var subQ5=sQuery(id+"F0.wireOp",EDGE,"E0");var subQ7=sQuery(id+"F0.wireOp",EDGE,"E14.19.0");var subQ8=makeQuery(id+"F0.imprint","INTERSECT",VERTEX,{"derivedFrom":[subQ5,subQ7]});Q169=makeQuery(id+"F0.imprint","IMPRINT",FACE,{"disambiguationData":[TD([[makeQuery(id+"F0.imprint","IMPRINT",EDGE,{"disambiguationData":[TD([[subQ8,-1.0]])],"derivedFrom":subQ5}),1.0]])]});}
            var Q170;
            {var subQ1=sQuery(id+"F0.wireOp",EDGE,"E0");var subQ5=sQuery(id+"F0.wireOp",EDGE,"E14.18.0");var subQ6=makeQuery(id+"F0.imprint","INTERSECT",VERTEX,{"derivedFrom":[subQ1,subQ5]});Q170=makeQuery(id+"F0.imprint","IMPRINT",FACE,{"disambiguationData":[TD([[makeQuery(id+"F0.imprint","IMPRINT",EDGE,{"disambiguationData":[TD([[subQ6,-1.0]])],"derivedFrom":subQ1}),1.0]])]});}
            var Q171;
            {var subQ0=sQuery(id+"F0.wireOp",EDGE,"E14.17.0");var subQ1=sQuery(id+"F0.wireOp",EDGE,"E0");var subQ2=makeQuery(id+"F0.imprint","INTERSECT",VERTEX,{"derivedFrom":[subQ1,subQ0]});Q171=makeQuery(id+"F0.imprint","IMPRINT",FACE,{"disambiguationData":[TD([[makeQuery(id+"F0.imprint","IMPRINT",EDGE,{"disambiguationData":[TD([[subQ2,-1.0]])],"derivedFrom":subQ1}),1.0]])]});}
            var Q172;
            {var subQ1=sQuery(id+"F0.wireOp",EDGE,"E0");var subQ7=sQuery(id+"F0.wireOp",EDGE,"E14.16.0");var subQ9=makeQuery(id+"F0.imprint","INTERSECT",VERTEX,{"derivedFrom":[subQ1,subQ7]});Q172=makeQuery(id+"F0.imprint","IMPRINT",FACE,{"disambiguationData":[TD([[makeQuery(id+"F0.imprint","IMPRINT",EDGE,{"disambiguationData":[TD([[subQ9,-1.0]])],"derivedFrom":subQ1}),1.0]])]});}
            var Q173;
            {var subQ5=sQuery(id+"F0.wireOp",EDGE,"E0");var subQ7=sQuery(id+"F0.wireOp",EDGE,"E14.15.0");var subQ8=makeQuery(id+"F0.imprint","INTERSECT",VERTEX,{"derivedFrom":[subQ5,subQ7]});Q173=makeQuery(id+"F0.imprint","IMPRINT",FACE,{"disambiguationData":[TD([[makeQuery(id+"F0.imprint","IMPRINT",EDGE,{"disambiguationData":[TD([[subQ8,-1.0]])],"derivedFrom":subQ5}),1.0]])]});}
            var Q174;
            {var subQ1=sQuery(id+"F0.wireOp",EDGE,"E0");var subQ5=sQuery(id+"F0.wireOp",EDGE,"E14.14.0");var subQ6=makeQuery(id+"F0.imprint","INTERSECT",VERTEX,{"derivedFrom":[subQ1,subQ5]});Q174=makeQuery(id+"F0.imprint","IMPRINT",FACE,{"disambiguationData":[TD([[makeQuery(id+"F0.imprint","IMPRINT",EDGE,{"disambiguationData":[TD([[subQ6,-1.0]])],"derivedFrom":subQ1}),1.0]])]});}
            var Q175;
            {var subQ1=sQuery(id+"F0.wireOp",EDGE,"E0");var subQ5=sQuery(id+"F0.wireOp",EDGE,"E14.13.0");var subQ6=makeQuery(id+"F0.imprint","INTERSECT",VERTEX,{"derivedFrom":[subQ1,subQ5]});Q175=makeQuery(id+"F0.imprint","IMPRINT",FACE,{"disambiguationData":[TD([[makeQuery(id+"F0.imprint","IMPRINT",EDGE,{"disambiguationData":[TD([[subQ6,-1.0]])],"derivedFrom":subQ1}),1.0]])]});}
            var Q176;
            {var subQ1=sQuery(id+"F0.wireOp",EDGE,"E0");var subQ5=sQuery(id+"F0.wireOp",EDGE,"E14.12.0");var subQ6=makeQuery(id+"F0.imprint","INTERSECT",VERTEX,{"derivedFrom":[subQ1,subQ5]});Q176=makeQuery(id+"F0.imprint","IMPRINT",FACE,{"disambiguationData":[TD([[makeQuery(id+"F0.imprint","IMPRINT",EDGE,{"disambiguationData":[TD([[subQ6,-1.0]])],"derivedFrom":subQ1}),1.0]])]});}
            var Q177;
            {var subQ1=sQuery(id+"F0.wireOp",EDGE,"E0");var subQ5=sQuery(id+"F0.wireOp",EDGE,"E14.11.0");var subQ6=makeQuery(id+"F0.imprint","INTERSECT",VERTEX,{"derivedFrom":[subQ1,subQ5]});Q177=makeQuery(id+"F0.imprint","IMPRINT",FACE,{"disambiguationData":[TD([[makeQuery(id+"F0.imprint","IMPRINT",EDGE,{"disambiguationData":[TD([[subQ6,-1.0]])],"derivedFrom":subQ1}),1.0]])]});}
            var Q178;
            {var subQ5=sQuery(id+"F0.wireOp",EDGE,"E0");var subQ7=sQuery(id+"F0.wireOp",EDGE,"E14.10.0");var subQ8=makeQuery(id+"F0.imprint","INTERSECT",VERTEX,{"derivedFrom":[subQ5,subQ7]});Q178=makeQuery(id+"F0.imprint","IMPRINT",FACE,{"disambiguationData":[TD([[makeQuery(id+"F0.imprint","IMPRINT",EDGE,{"disambiguationData":[TD([[subQ8,-1.0]])],"derivedFrom":subQ5}),1.0]])]});}
            var Q179;
            {var subQ1=sQuery(id+"F0.wireOp",EDGE,"E0");var subQ5=sQuery(id+"F0.wireOp",EDGE,"E14.9.0");var subQ6=makeQuery(id+"F0.imprint","INTERSECT",VERTEX,{"derivedFrom":[subQ1,subQ5]});Q179=makeQuery(id+"F0.imprint","IMPRINT",FACE,{"disambiguationData":[TD([[makeQuery(id+"F0.imprint","IMPRINT",EDGE,{"disambiguationData":[TD([[subQ6,-1.0]])],"derivedFrom":subQ1}),1.0]])]});}
            var Q180;
            {var subQ1=sQuery(id+"F0.wireOp",EDGE,"E0");var subQ7=sQuery(id+"F0.wireOp",EDGE,"E14.8.1");var subQ9=makeQuery(id+"F0.imprint","INTERSECT",VERTEX,{"derivedFrom":[subQ1,subQ7]});Q180=makeQuery(id+"F0.imprint","IMPRINT",FACE,{"disambiguationData":[TD([[makeQuery(id+"F0.imprint","IMPRINT",EDGE,{"disambiguationData":[TD([[subQ9,1.0]])],"derivedFrom":subQ1}),1.0]])]});}
            var Q181;
            {var subQ0=sQuery(id+"F0.wireOp",EDGE,"E14.3.1");var subQ1=sQuery(id+"F0.wireOp",EDGE,"E9.right");var subQ2=makeQuery(id+"F0.imprint","INTERSECT",VERTEX,{"derivedFrom":[subQ1,subQ0]});Q181=makeQuery(id+"F0.imprint","IMPRINT",FACE,{"disambiguationData":[TD([[makeQuery(id+"F0.imprint","IMPRINT",EDGE,{"disambiguationData":[TD([[subQ2,-1.0]])],"derivedFrom":subQ1}),1.0]])]});}
            var Q182;
            {var subQ10=sQuery(id+"F0.wireOp",EDGE,"E9.bottom");Q182=makeQuery(id+"F0.imprint","IMPRINT",FACE,{"disambiguationData":[TD([[makeQuery(id+"F0.imprint","IMPRINT",EDGE,{"derivedFrom":subQ10}),-1.0]])]});}
            var Q183;
            {var subQ0=sQuery(id+"F0.wireOp",EDGE,"E14.10.1");var subQ1=sQuery(id+"F0.wireOp",EDGE,"E14.5.0");var subQ2=makeQuery(id+"F0.imprint","INTERSECT",VERTEX,{"derivedFrom":[subQ1,subQ0]});Q183=makeQuery(id+"F0.imprint","IMPRINT",FACE,{"disambiguationData":[TD([[makeQuery(id+"F0.imprint","IMPRINT",EDGE,{"disambiguationData":[TD([[subQ2,-1.0]])],"derivedFrom":subQ1}),-1.0]])]});}
            var Q184;
            {var subQ0=sQuery(id+"F0.wireOp",EDGE,"E14.29.1");var subQ1=sQuery(id+"F0.wireOp",EDGE,"E14.26.0");var subQ2=makeQuery(id+"F0.imprint","INTERSECT",VERTEX,{"derivedFrom":[subQ1,subQ0]});Q184=makeQuery(id+"F0.imprint","IMPRINT",FACE,{"disambiguationData":[TD([[makeQuery(id+"F0.imprint","IMPRINT",EDGE,{"disambiguationData":[TD([[subQ2,-1.0]])],"derivedFrom":subQ1}),-1.0]])]});}
            var Q185;
            {var subQ0=sQuery(id+"F0.wireOp",EDGE,"E14.8.1");var subQ1=sQuery(id+"F0.wireOp",EDGE,"E14.3.0");var subQ2=makeQuery(id+"F0.imprint","INTERSECT",VERTEX,{"derivedFrom":[subQ1,subQ0]});Q185=makeQuery(id+"F0.imprint","IMPRINT",FACE,{"disambiguationData":[TD([[makeQuery(id+"F0.imprint","IMPRINT",EDGE,{"disambiguationData":[TD([[subQ2,-1.0]])],"derivedFrom":subQ1}),-1.0]])]});}
            var Q186;
            {var subQ0=sQuery(id+"F0.wireOp",EDGE,"E14.20.1");var subQ1=sQuery(id+"F0.wireOp",EDGE,"E14.15.0");var subQ2=makeQuery(id+"F0.imprint","INTERSECT",VERTEX,{"derivedFrom":[subQ1,subQ0]});Q186=makeQuery(id+"F0.imprint","IMPRINT",FACE,{"disambiguationData":[TD([[makeQuery(id+"F0.imprint","IMPRINT",EDGE,{"disambiguationData":[TD([[subQ2,-1.0]])],"derivedFrom":subQ1}),-1.0]])]});}
            var Q187;
            {var subQ0=sQuery(id+"F0.wireOp",EDGE,"E14.5.1");var subQ1=sQuery(id+"F0.wireOp",EDGE,"E14.2.0");var subQ2=makeQuery(id+"F0.imprint","INTERSECT",VERTEX,{"derivedFrom":[subQ1,subQ0]});Q187=makeQuery(id+"F0.imprint","IMPRINT",FACE,{"disambiguationData":[TD([[makeQuery(id+"F0.imprint","IMPRINT",EDGE,{"disambiguationData":[TD([[subQ2,-1.0]])],"derivedFrom":subQ1}),-1.0]])]});}
            var Q188;
            {var subQ0=sQuery(id+"F0.wireOp",EDGE,"E14.30.1");var subQ1=sQuery(id+"F0.wireOp",EDGE,"E14.25.0");var subQ2=makeQuery(id+"F0.imprint","INTERSECT",VERTEX,{"derivedFrom":[subQ1,subQ0]});Q188=makeQuery(id+"F0.imprint","IMPRINT",FACE,{"disambiguationData":[TD([[makeQuery(id+"F0.imprint","IMPRINT",EDGE,{"disambiguationData":[TD([[subQ2,-1.0]])],"derivedFrom":subQ1}),-1.0]])]});}
            var Q189;
            {var subQ0=sQuery(id+"F0.wireOp",EDGE,"E14.34.1");var subQ1=sQuery(id+"F0.wireOp",EDGE,"E14.29.0");var subQ2=makeQuery(id+"F0.imprint","INTERSECT",VERTEX,{"derivedFrom":[subQ1,subQ0]});Q189=makeQuery(id+"F0.imprint","IMPRINT",FACE,{"disambiguationData":[TD([[makeQuery(id+"F0.imprint","IMPRINT",EDGE,{"disambiguationData":[TD([[subQ2,-1.0]])],"derivedFrom":subQ1}),-1.0]])]});}
            var Q190;
            {var subQ0=sQuery(id+"F0.wireOp",EDGE,"E14.32.1");var subQ1=sQuery(id+"F0.wireOp",EDGE,"E14.25.0");var subQ2=makeQuery(id+"F0.imprint","INTERSECT",VERTEX,{"derivedFrom":[subQ1,subQ0]});Q190=makeQuery(id+"F0.imprint","IMPRINT",FACE,{"disambiguationData":[TD([[makeQuery(id+"F0.imprint","IMPRINT",EDGE,{"disambiguationData":[TD([[subQ2,-1.0]])],"derivedFrom":subQ1}),-1.0]])]});}
            var Q191;
            {var subQ0=sQuery(id+"F0.wireOp",EDGE,"E14.18.1");var subQ1=sQuery(id+"F0.wireOp",EDGE,"E14.15.0");var subQ2=makeQuery(id+"F0.imprint","INTERSECT",VERTEX,{"derivedFrom":[subQ1,subQ0]});Q191=makeQuery(id+"F0.imprint","IMPRINT",FACE,{"disambiguationData":[TD([[makeQuery(id+"F0.imprint","IMPRINT",EDGE,{"disambiguationData":[TD([[subQ2,-1.0]])],"derivedFrom":subQ1}),-1.0]])]});}
            var Q192;
            {var subQ0=sQuery(id+"F0.wireOp",EDGE,"E14.12.1");var subQ1=sQuery(id+"F0.wireOp",EDGE,"E14.8.0");var subQ2=makeQuery(id+"F0.imprint","INTERSECT",VERTEX,{"derivedFrom":[subQ1,subQ0]});Q192=makeQuery(id+"F0.imprint","IMPRINT",FACE,{"disambiguationData":[TD([[makeQuery(id+"F0.imprint","IMPRINT",EDGE,{"disambiguationData":[TD([[subQ2,-1.0]])],"derivedFrom":subQ1}),-1.0]])]});}
            var Q193;
            {var subQ0=sQuery(id+"F0.wireOp",EDGE,"E14.21.1");var subQ1=sQuery(id+"F0.wireOp",EDGE,"E14.14.0");var subQ2=makeQuery(id+"F0.imprint","INTERSECT",VERTEX,{"derivedFrom":[subQ1,subQ0]});Q193=makeQuery(id+"F0.imprint","IMPRINT",FACE,{"disambiguationData":[TD([[makeQuery(id+"F0.imprint","IMPRINT",EDGE,{"disambiguationData":[TD([[subQ2,-1.0]])],"derivedFrom":subQ1}),-1.0]])]});}
            var Q194;
            {var subQ0=sQuery(id+"F0.wireOp",EDGE,"E14.13.1");var subQ1=sQuery(id+"F0.wireOp",EDGE,"E14.7.0");var subQ2=makeQuery(id+"F0.imprint","INTERSECT",VERTEX,{"derivedFrom":[subQ1,subQ0]});Q194=makeQuery(id+"F0.imprint","IMPRINT",FACE,{"disambiguationData":[TD([[makeQuery(id+"F0.imprint","IMPRINT",EDGE,{"disambiguationData":[TD([[subQ2,-1.0]])],"derivedFrom":subQ1}),-1.0]])]});}
            var Q195;
            {var subQ0=sQuery(id+"F0.wireOp",EDGE,"E14.30.1");var subQ1=sQuery(id+"F0.wireOp",EDGE,"E14.26.0");var subQ2=makeQuery(id+"F0.imprint","INTERSECT",VERTEX,{"derivedFrom":[subQ1,subQ0]});Q195=makeQuery(id+"F0.imprint","IMPRINT",FACE,{"disambiguationData":[TD([[makeQuery(id+"F0.imprint","IMPRINT",EDGE,{"disambiguationData":[TD([[subQ2,-1.0]])],"derivedFrom":subQ1}),-1.0]])]});}
            var Q196;
            {var subQ0=sQuery(id+"F0.wireOp",EDGE,"E14.33.0");var subQ1=sQuery(id+"F0.wireOp",EDGE,"E14.2.1");var subQ2=makeQuery(id+"F0.imprint","INTERSECT",VERTEX,{"derivedFrom":[subQ1,subQ0]});Q196=makeQuery(id+"F0.imprint","IMPRINT",FACE,{"disambiguationData":[TD([[makeQuery(id+"F0.imprint","IMPRINT",EDGE,{"disambiguationData":[TD([[subQ2,-1.0]])],"derivedFrom":subQ1}),-1.0]])]});}
            var Q197;
            {var subQ0=sQuery(id+"F0.wireOp",EDGE,"E14.29.1");var subQ1=sQuery(id+"F0.wireOp",EDGE,"E14.23.0");var subQ2=makeQuery(id+"F0.imprint","INTERSECT",VERTEX,{"derivedFrom":[subQ1,subQ0]});Q197=makeQuery(id+"F0.imprint","IMPRINT",FACE,{"disambiguationData":[TD([[makeQuery(id+"F0.imprint","IMPRINT",EDGE,{"disambiguationData":[TD([[subQ2,-1.0]])],"derivedFrom":subQ1}),-1.0]])]});}
            var Q198;
            {var subQ0=sQuery(id+"F0.wireOp",EDGE,"E14.13.1");var subQ1=sQuery(id+"F0.wireOp",EDGE,"E14.8.0");var subQ2=makeQuery(id+"F0.imprint","INTERSECT",VERTEX,{"derivedFrom":[subQ1,subQ0]});Q198=makeQuery(id+"F0.imprint","IMPRINT",FACE,{"disambiguationData":[TD([[makeQuery(id+"F0.imprint","IMPRINT",EDGE,{"disambiguationData":[TD([[subQ2,-1.0]])],"derivedFrom":subQ1}),-1.0]])]});}
            var Q199;
            {var subQ0=sQuery(id+"F0.wireOp",EDGE,"E14.18.1");var subQ1=sQuery(id+"F0.wireOp",EDGE,"E14.13.0");var subQ2=makeQuery(id+"F0.imprint","INTERSECT",VERTEX,{"derivedFrom":[subQ1,subQ0]});Q199=makeQuery(id+"F0.imprint","IMPRINT",FACE,{"disambiguationData":[TD([[makeQuery(id+"F0.imprint","IMPRINT",EDGE,{"disambiguationData":[TD([[subQ2,-1.0]])],"derivedFrom":subQ1}),-1.0]])]});}
            var Q200;
            {var subQ0=sQuery(id+"F0.wireOp",EDGE,"E14.32.0");var subQ1=sQuery(id+"F0.wireOp",EDGE,"E14.3.1");var subQ2=makeQuery(id+"F0.imprint","INTERSECT",VERTEX,{"derivedFrom":[subQ1,subQ0]});Q200=makeQuery(id+"F0.imprint","IMPRINT",FACE,{"disambiguationData":[TD([[makeQuery(id+"F0.imprint","IMPRINT",EDGE,{"disambiguationData":[TD([[subQ2,-1.0]])],"derivedFrom":subQ1}),-1.0]])]});}
            var Q201;
            {var subQ0=sQuery(id+"F0.wireOp",EDGE,"E14.22.1");var subQ1=sQuery(id+"F0.wireOp",EDGE,"E14.18.0");var subQ2=makeQuery(id+"F0.imprint","INTERSECT",VERTEX,{"derivedFrom":[subQ1,subQ0]});Q201=makeQuery(id+"F0.imprint","IMPRINT",FACE,{"disambiguationData":[TD([[makeQuery(id+"F0.imprint","IMPRINT",EDGE,{"disambiguationData":[TD([[subQ2,-1.0]])],"derivedFrom":subQ1}),-1.0]])]});}
            var Q202;
            {var subQ0=sQuery(id+"F0.wireOp",EDGE,"E14.24.1");var subQ1=sQuery(id+"F0.wireOp",EDGE,"E14.21.0");var subQ2=makeQuery(id+"F0.imprint","INTERSECT",VERTEX,{"derivedFrom":[subQ1,subQ0]});Q202=makeQuery(id+"F0.imprint","IMPRINT",FACE,{"disambiguationData":[TD([[makeQuery(id+"F0.imprint","IMPRINT",EDGE,{"disambiguationData":[TD([[subQ2,-1.0]])],"derivedFrom":subQ1}),-1.0]])]});}
            var Q203;
            {var subQ0=sQuery(id+"F0.wireOp",EDGE,"E14.8.1");var subQ1=sQuery(id+"F0.wireOp",EDGE,"E14.2.0");var subQ2=makeQuery(id+"F0.imprint","INTERSECT",VERTEX,{"derivedFrom":[subQ1,subQ0]});Q203=makeQuery(id+"F0.imprint","IMPRINT",FACE,{"disambiguationData":[TD([[makeQuery(id+"F0.imprint","IMPRINT",EDGE,{"disambiguationData":[TD([[subQ2,-1.0]])],"derivedFrom":subQ1}),-1.0]])]});}
            var Q204;
            {var subQ0=sQuery(id+"F0.wireOp",EDGE,"E14.9.1");var subQ1=sQuery(id+"F0.wireOp",EDGE,"E14.3.0");var subQ2=makeQuery(id+"F0.imprint","INTERSECT",VERTEX,{"derivedFrom":[subQ1,subQ0]});Q204=makeQuery(id+"F0.imprint","IMPRINT",FACE,{"disambiguationData":[TD([[makeQuery(id+"F0.imprint","IMPRINT",EDGE,{"disambiguationData":[TD([[subQ2,-1.0]])],"derivedFrom":subQ1}),-1.0]])]});}
            var Q205;
            {var subQ0=sQuery(id+"F0.wireOp",EDGE,"E14.35.1");var subQ1=sQuery(id+"F0.wireOp",EDGE,"E14.29.0");var subQ2=makeQuery(id+"F0.imprint","INTERSECT",VERTEX,{"derivedFrom":[subQ1,subQ0]});Q205=makeQuery(id+"F0.imprint","IMPRINT",FACE,{"disambiguationData":[TD([[makeQuery(id+"F0.imprint","IMPRINT",EDGE,{"disambiguationData":[TD([[subQ2,-1.0]])],"derivedFrom":subQ1}),-1.0]])]});}
            var Q206;
            {var subQ0=sQuery(id+"F0.wireOp",EDGE,"E14.19.1");var subQ1=sQuery(id+"F0.wireOp",EDGE,"E14.14.0");var subQ2=makeQuery(id+"F0.imprint","INTERSECT",VERTEX,{"derivedFrom":[subQ1,subQ0]});Q206=makeQuery(id+"F0.imprint","IMPRINT",FACE,{"disambiguationData":[TD([[makeQuery(id+"F0.imprint","IMPRINT",EDGE,{"disambiguationData":[TD([[subQ2,-1.0]])],"derivedFrom":subQ1}),-1.0]])]});}
            var Q207;
            {var subQ0=sQuery(id+"F0.wireOp",EDGE,"E14.12.1");var subQ1=sQuery(id+"F0.wireOp",EDGE,"E14.9.0");var subQ2=makeQuery(id+"F0.imprint","INTERSECT",VERTEX,{"derivedFrom":[subQ1,subQ0]});Q207=makeQuery(id+"F0.imprint","IMPRINT",FACE,{"disambiguationData":[TD([[makeQuery(id+"F0.imprint","IMPRINT",EDGE,{"disambiguationData":[TD([[subQ2,-1.0]])],"derivedFrom":subQ1}),-1.0]])]});}
            var Q208;
            {var subQ0=sQuery(id+"F0.wireOp",EDGE,"E14.20.1");var subQ1=sQuery(id+"F0.wireOp",EDGE,"E14.16.0");var subQ2=makeQuery(id+"F0.imprint","INTERSECT",VERTEX,{"derivedFrom":[subQ1,subQ0]});Q208=makeQuery(id+"F0.imprint","IMPRINT",FACE,{"disambiguationData":[TD([[makeQuery(id+"F0.imprint","IMPRINT",EDGE,{"disambiguationData":[TD([[subQ2,-1.0]])],"derivedFrom":subQ1}),-1.0]])]});}
            var Q209;
            {var subQ0=sQuery(id+"F0.wireOp",EDGE,"E14.14.1");var subQ1=sQuery(id+"F0.wireOp",EDGE,"E14.10.0");var subQ2=makeQuery(id+"F0.imprint","INTERSECT",VERTEX,{"derivedFrom":[subQ1,subQ0]});Q209=makeQuery(id+"F0.imprint","IMPRINT",FACE,{"disambiguationData":[TD([[makeQuery(id+"F0.imprint","IMPRINT",EDGE,{"disambiguationData":[TD([[subQ2,-1.0]])],"derivedFrom":subQ1}),-1.0]])]});}
            var Q210;
            {var subQ0=sQuery(id+"F0.wireOp",EDGE,"E14.11.1");var subQ1=sQuery(id+"F0.wireOp",EDGE,"E14.5.0");var subQ2=makeQuery(id+"F0.imprint","INTERSECT",VERTEX,{"derivedFrom":[subQ1,subQ0]});Q210=makeQuery(id+"F0.imprint","IMPRINT",FACE,{"disambiguationData":[TD([[makeQuery(id+"F0.imprint","IMPRINT",EDGE,{"disambiguationData":[TD([[subQ2,-1.0]])],"derivedFrom":subQ1}),-1.0]])]});}
            var Q211;
            {var subQ0=sQuery(id+"F0.wireOp",EDGE,"E14.27.1");var subQ1=sQuery(id+"F0.wireOp",EDGE,"E14.22.0");var subQ2=makeQuery(id+"F0.imprint","INTERSECT",VERTEX,{"derivedFrom":[subQ1,subQ0]});Q211=makeQuery(id+"F0.imprint","IMPRINT",FACE,{"disambiguationData":[TD([[makeQuery(id+"F0.imprint","IMPRINT",EDGE,{"disambiguationData":[TD([[subQ2,-1.0]])],"derivedFrom":subQ1}),-1.0]])]});}
            var Q212;
            {var subQ0=sQuery(id+"F0.wireOp",EDGE,"E14.32.0");var subQ1=sQuery(id+"F0.wireOp",EDGE,"E14.2.1");var subQ2=makeQuery(id+"F0.imprint","INTERSECT",VERTEX,{"derivedFrom":[subQ1,subQ0]});Q212=makeQuery(id+"F0.imprint","IMPRINT",FACE,{"disambiguationData":[TD([[makeQuery(id+"F0.imprint","IMPRINT",EDGE,{"disambiguationData":[TD([[subQ2,-1.0]])],"derivedFrom":subQ1}),-1.0]])]});}
            var Q213;
            {var subQ0=sQuery(id+"F0.wireOp",EDGE,"E14.23.1");var subQ1=sQuery(id+"F0.wireOp",EDGE,"E14.18.0");var subQ2=makeQuery(id+"F0.imprint","INTERSECT",VERTEX,{"derivedFrom":[subQ1,subQ0]});Q213=makeQuery(id+"F0.imprint","IMPRINT",FACE,{"disambiguationData":[TD([[makeQuery(id+"F0.imprint","IMPRINT",EDGE,{"disambiguationData":[TD([[subQ2,-1.0]])],"derivedFrom":subQ1}),-1.0]])]});}
            var Q214;
            {var subQ0=sQuery(id+"F0.wireOp",EDGE,"E14.7.1");var subQ1=sQuery(id+"F0.wireOp",EDGE,"E14.3.0");var subQ2=makeQuery(id+"F0.imprint","INTERSECT",VERTEX,{"derivedFrom":[subQ1,subQ0]});Q214=makeQuery(id+"F0.imprint","IMPRINT",FACE,{"disambiguationData":[TD([[makeQuery(id+"F0.imprint","IMPRINT",EDGE,{"disambiguationData":[TD([[subQ2,-1.0]])],"derivedFrom":subQ1}),-1.0]])]});}
            var Q215;
            {var subQ0=sQuery(id+"F0.wireOp",EDGE,"E14.27.1");var subQ1=sQuery(id+"F0.wireOp",EDGE,"E14.24.0");var subQ2=makeQuery(id+"F0.imprint","INTERSECT",VERTEX,{"derivedFrom":[subQ1,subQ0]});Q215=makeQuery(id+"F0.imprint","IMPRINT",FACE,{"disambiguationData":[TD([[makeQuery(id+"F0.imprint","IMPRINT",EDGE,{"disambiguationData":[TD([[subQ2,-1.0]])],"derivedFrom":subQ1}),-1.0]])]});}
            var Q216;
            {var subQ0=sQuery(id+"F0.wireOp",EDGE,"E14.28.1");var subQ1=sQuery(id+"F0.wireOp",EDGE,"E14.22.0");var subQ2=makeQuery(id+"F0.imprint","INTERSECT",VERTEX,{"derivedFrom":[subQ1,subQ0]});Q216=makeQuery(id+"F0.imprint","IMPRINT",FACE,{"disambiguationData":[TD([[makeQuery(id+"F0.imprint","IMPRINT",EDGE,{"disambiguationData":[TD([[subQ2,-1.0]])],"derivedFrom":subQ1}),-1.0]])]});}
            var Q217;
            {var subQ0=sQuery(id+"F0.wireOp",EDGE,"E14.6.1");var subQ1=sQuery(id+"F0.wireOp",EDGE,"E9.right");var subQ2=makeQuery(id+"F0.imprint","INTERSECT",VERTEX,{"derivedFrom":[subQ1,subQ0]});Q217=makeQuery(id+"F0.imprint","IMPRINT",FACE,{"disambiguationData":[TD([[makeQuery(id+"F0.imprint","IMPRINT",EDGE,{"disambiguationData":[TD([[subQ2,-1.0]])],"derivedFrom":subQ1}),-1.0]])]});}
            var Q218;
            {var subQ0=sQuery(id+"F0.wireOp",EDGE,"E14.34.0");var subQ1=sQuery(id+"F0.wireOp",EDGE,"E9.left");var subQ2=makeQuery(id+"F0.imprint","INTERSECT",VERTEX,{"derivedFrom":[subQ1,subQ0]});Q218=makeQuery(id+"F0.imprint","IMPRINT",FACE,{"disambiguationData":[TD([[makeQuery(id+"F0.imprint","IMPRINT",EDGE,{"disambiguationData":[TD([[subQ2,-1.0]])],"derivedFrom":subQ1}),-1.0]])]});}
            var Q219;
            {var subQ0=sQuery(id+"F0.wireOp",EDGE,"E14.17.1");var subQ1=sQuery(id+"F0.wireOp",EDGE,"E14.14.0");var subQ2=makeQuery(id+"F0.imprint","INTERSECT",VERTEX,{"derivedFrom":[subQ1,subQ0]});Q219=makeQuery(id+"F0.imprint","IMPRINT",FACE,{"disambiguationData":[TD([[makeQuery(id+"F0.imprint","IMPRINT",EDGE,{"disambiguationData":[TD([[subQ2,-1.0]])],"derivedFrom":subQ1}),-1.0]])]});}
            var Q220;
            {var subQ0=sQuery(id+"F0.wireOp",EDGE,"E14.23.1");var subQ1=sQuery(id+"F0.wireOp",EDGE,"E14.20.0");var subQ2=makeQuery(id+"F0.imprint","INTERSECT",VERTEX,{"derivedFrom":[subQ1,subQ0]});Q220=makeQuery(id+"F0.imprint","IMPRINT",FACE,{"disambiguationData":[TD([[makeQuery(id+"F0.imprint","IMPRINT",EDGE,{"disambiguationData":[TD([[subQ2,-1.0]])],"derivedFrom":subQ1}),-1.0]])]});}
            var Q221;
            {var subQ0=sQuery(id+"F0.wireOp",EDGE,"E14.11.1");var subQ1=sQuery(id+"F0.wireOp",EDGE,"E14.4.0");var subQ2=makeQuery(id+"F0.imprint","INTERSECT",VERTEX,{"derivedFrom":[subQ1,subQ0]});Q221=makeQuery(id+"F0.imprint","IMPRINT",FACE,{"disambiguationData":[TD([[makeQuery(id+"F0.imprint","IMPRINT",EDGE,{"disambiguationData":[TD([[subQ2,-1.0]])],"derivedFrom":subQ1}),-1.0]])]});}
            var Q222;
            {var subQ0=sQuery(id+"F0.wireOp",EDGE,"E14.22.1");var subQ1=sQuery(id+"F0.wireOp",EDGE,"E14.17.0");var subQ2=makeQuery(id+"F0.imprint","INTERSECT",VERTEX,{"derivedFrom":[subQ1,subQ0]});Q222=makeQuery(id+"F0.imprint","IMPRINT",FACE,{"disambiguationData":[TD([[makeQuery(id+"F0.imprint","IMPRINT",EDGE,{"disambiguationData":[TD([[subQ2,-1.0]])],"derivedFrom":subQ1}),-1.0]])]});}
            var Q223;
            {var subQ0=sQuery(id+"F0.wireOp",EDGE,"E14.28.1");var subQ1=sQuery(id+"F0.wireOp",EDGE,"E14.21.0");var subQ2=makeQuery(id+"F0.imprint","INTERSECT",VERTEX,{"derivedFrom":[subQ1,subQ0]});Q223=makeQuery(id+"F0.imprint","IMPRINT",FACE,{"disambiguationData":[TD([[makeQuery(id+"F0.imprint","IMPRINT",EDGE,{"disambiguationData":[TD([[subQ2,-1.0]])],"derivedFrom":subQ1}),-1.0]])]});}
            var Q224;
            {var subQ0=sQuery(id+"F0.wireOp",EDGE,"E14.10.1");var subQ1=sQuery(id+"F0.wireOp",EDGE,"E14.7.0");var subQ2=makeQuery(id+"F0.imprint","INTERSECT",VERTEX,{"derivedFrom":[subQ1,subQ0]});Q224=makeQuery(id+"F0.imprint","IMPRINT",FACE,{"disambiguationData":[TD([[makeQuery(id+"F0.imprint","IMPRINT",EDGE,{"disambiguationData":[TD([[subQ2,-1.0]])],"derivedFrom":subQ1}),-1.0]])]});}
            var Q225;
            {var subQ0=sQuery(id+"F0.wireOp",EDGE,"E14.32.1");var subQ1=sQuery(id+"F0.wireOp",EDGE,"E14.26.0");var subQ2=makeQuery(id+"F0.imprint","INTERSECT",VERTEX,{"derivedFrom":[subQ1,subQ0]});Q225=makeQuery(id+"F0.imprint","IMPRINT",FACE,{"disambiguationData":[TD([[makeQuery(id+"F0.imprint","IMPRINT",EDGE,{"disambiguationData":[TD([[subQ2,-1.0]])],"derivedFrom":subQ1}),-1.0]])]});}
            var Q226;
            {var subQ0=sQuery(id+"F0.wireOp",EDGE,"E14.7.1");var subQ1=sQuery(id+"F0.wireOp",EDGE,"E14.4.0");var subQ2=makeQuery(id+"F0.imprint","INTERSECT",VERTEX,{"derivedFrom":[subQ1,subQ0]});Q226=makeQuery(id+"F0.imprint","IMPRINT",FACE,{"disambiguationData":[TD([[makeQuery(id+"F0.imprint","IMPRINT",EDGE,{"disambiguationData":[TD([[subQ2,-1.0]])],"derivedFrom":subQ1}),-1.0]])]});}
            var Q227;
            {var subQ0=sQuery(id+"F0.wireOp",EDGE,"E14.32.0");var subQ1=sQuery(id+"F0.wireOp",EDGE,"E14.4.1");var subQ2=makeQuery(id+"F0.imprint","INTERSECT",VERTEX,{"derivedFrom":[subQ1,subQ0]});Q227=makeQuery(id+"F0.imprint","IMPRINT",FACE,{"disambiguationData":[TD([[makeQuery(id+"F0.imprint","IMPRINT",EDGE,{"disambiguationData":[TD([[subQ2,-1.0]])],"derivedFrom":subQ1}),-1.0]])]});}
            var Q228;
            {var subQ0=sQuery(id+"F0.wireOp",EDGE,"E14.33.1");var subQ1=sQuery(id+"F0.wireOp",EDGE,"E14.27.0");var subQ2=makeQuery(id+"F0.imprint","INTERSECT",VERTEX,{"derivedFrom":[subQ1,subQ0]});Q228=makeQuery(id+"F0.imprint","IMPRINT",FACE,{"disambiguationData":[TD([[makeQuery(id+"F0.imprint","IMPRINT",EDGE,{"disambiguationData":[TD([[subQ2,-1.0]])],"derivedFrom":subQ1}),-1.0]])]});}
            var Q229;
            {var subQ0=sQuery(id+"F0.wireOp",EDGE,"E14.32.1");var subQ1=sQuery(id+"F0.wireOp",EDGE,"E14.29.0");var subQ2=makeQuery(id+"F0.imprint","INTERSECT",VERTEX,{"derivedFrom":[subQ1,subQ0]});Q229=makeQuery(id+"F0.imprint","IMPRINT",FACE,{"disambiguationData":[TD([[makeQuery(id+"F0.imprint","IMPRINT",EDGE,{"disambiguationData":[TD([[subQ2,-1.0]])],"derivedFrom":subQ1}),-1.0]])]});}
            var Q230;
            {var subQ0=sQuery(id+"F0.wireOp",EDGE,"E14.34.1");var subQ1=sQuery(id+"F0.wireOp",EDGE,"E14.30.0");var subQ2=makeQuery(id+"F0.imprint","INTERSECT",VERTEX,{"derivedFrom":[subQ1,subQ0]});Q230=makeQuery(id+"F0.imprint","IMPRINT",FACE,{"disambiguationData":[TD([[makeQuery(id+"F0.imprint","IMPRINT",EDGE,{"disambiguationData":[TD([[subQ2,-1.0]])],"derivedFrom":subQ1}),-1.0]])]});}
            var Q231;
            {var subQ0=sQuery(id+"F0.wireOp",EDGE,"E14.26.1");var subQ1=sQuery(id+"F0.wireOp",EDGE,"E14.22.0");var subQ2=makeQuery(id+"F0.imprint","INTERSECT",VERTEX,{"derivedFrom":[subQ1,subQ0]});Q231=makeQuery(id+"F0.imprint","IMPRINT",FACE,{"disambiguationData":[TD([[makeQuery(id+"F0.imprint","IMPRINT",EDGE,{"disambiguationData":[TD([[subQ2,-1.0]])],"derivedFrom":subQ1}),-1.0]])]});}
            var Q232;
            {var subQ0=sQuery(id+"F0.wireOp",EDGE,"E14.35.1");var subQ1=sQuery(id+"F0.wireOp",EDGE,"E14.30.0");var subQ2=makeQuery(id+"F0.imprint","INTERSECT",VERTEX,{"derivedFrom":[subQ1,subQ0]});Q232=makeQuery(id+"F0.imprint","IMPRINT",FACE,{"disambiguationData":[TD([[makeQuery(id+"F0.imprint","IMPRINT",EDGE,{"disambiguationData":[TD([[subQ2,-1.0]])],"derivedFrom":subQ1}),-1.0]])]});}
            var Q233;
            {var subQ0=sQuery(id+"F0.wireOp",EDGE,"E14.8.1");var subQ1=sQuery(id+"F0.wireOp",EDGE,"E14.5.0");var subQ2=makeQuery(id+"F0.imprint","INTERSECT",VERTEX,{"derivedFrom":[subQ1,subQ0]});Q233=makeQuery(id+"F0.imprint","IMPRINT",FACE,{"disambiguationData":[TD([[makeQuery(id+"F0.imprint","IMPRINT",EDGE,{"disambiguationData":[TD([[subQ2,-1.0]])],"derivedFrom":subQ1}),-1.0]])]});}
            var Q234;
            {var subQ0=sQuery(id+"F0.wireOp",EDGE,"E14.15.1");var subQ1=sQuery(id+"F0.wireOp",EDGE,"E14.11.0");var subQ2=makeQuery(id+"F0.imprint","INTERSECT",VERTEX,{"derivedFrom":[subQ1,subQ0]});Q234=makeQuery(id+"F0.imprint","IMPRINT",FACE,{"disambiguationData":[TD([[makeQuery(id+"F0.imprint","IMPRINT",EDGE,{"disambiguationData":[TD([[subQ2,-1.0]])],"derivedFrom":subQ1}),-1.0]])]});}
            var Q235;
            {var subQ0=sQuery(id+"F0.wireOp",EDGE,"E14.30.1");var subQ1=sQuery(id+"F0.wireOp",EDGE,"E14.27.0");var subQ2=makeQuery(id+"F0.imprint","INTERSECT",VERTEX,{"derivedFrom":[subQ1,subQ0]});Q235=makeQuery(id+"F0.imprint","IMPRINT",FACE,{"disambiguationData":[TD([[makeQuery(id+"F0.imprint","IMPRINT",EDGE,{"disambiguationData":[TD([[subQ2,-1.0]])],"derivedFrom":subQ1}),-1.0]])]});}
            var Q236;
            {var subQ0=sQuery(id+"F0.wireOp",EDGE,"E14.35.1");var subQ1=sQuery(id+"F0.wireOp",EDGE,"E14.28.0");var subQ2=makeQuery(id+"F0.imprint","INTERSECT",VERTEX,{"derivedFrom":[subQ1,subQ0]});Q236=makeQuery(id+"F0.imprint","IMPRINT",FACE,{"disambiguationData":[TD([[makeQuery(id+"F0.imprint","IMPRINT",EDGE,{"disambiguationData":[TD([[subQ2,-1.0]])],"derivedFrom":subQ1}),-1.0]])]});}
            var Q237;
            {var subQ0=sQuery(id+"F0.wireOp",EDGE,"E14.16.1");var subQ1=sQuery(id+"F0.wireOp",EDGE,"E14.11.0");var subQ2=makeQuery(id+"F0.imprint","INTERSECT",VERTEX,{"derivedFrom":[subQ1,subQ0]});Q237=makeQuery(id+"F0.imprint","IMPRINT",FACE,{"disambiguationData":[TD([[makeQuery(id+"F0.imprint","IMPRINT",EDGE,{"disambiguationData":[TD([[subQ2,-1.0]])],"derivedFrom":subQ1}),-1.0]])]});}
            var Q238;
            {var subQ0=sQuery(id+"F0.wireOp",EDGE,"E14.19.1");var subQ1=sQuery(id+"F0.wireOp",EDGE,"E14.15.0");var subQ2=makeQuery(id+"F0.imprint","INTERSECT",VERTEX,{"derivedFrom":[subQ1,subQ0]});Q238=makeQuery(id+"F0.imprint","IMPRINT",FACE,{"disambiguationData":[TD([[makeQuery(id+"F0.imprint","IMPRINT",EDGE,{"disambiguationData":[TD([[subQ2,-1.0]])],"derivedFrom":subQ1}),-1.0]])]});}
            var Q239;
            {var subQ0=sQuery(id+"F0.wireOp",EDGE,"E14.16.1");var subQ1=sQuery(id+"F0.wireOp",EDGE,"E14.12.0");var subQ2=makeQuery(id+"F0.imprint","INTERSECT",VERTEX,{"derivedFrom":[subQ1,subQ0]});Q239=makeQuery(id+"F0.imprint","IMPRINT",FACE,{"disambiguationData":[TD([[makeQuery(id+"F0.imprint","IMPRINT",EDGE,{"disambiguationData":[TD([[subQ2,-1.0]])],"derivedFrom":subQ1}),-1.0]])]});}
            var Q240;
            {var subQ0=sQuery(id+"F0.wireOp",EDGE,"E14.32.1");var subQ1=sQuery(id+"F0.wireOp",EDGE,"E14.28.0");var subQ2=makeQuery(id+"F0.imprint","INTERSECT",VERTEX,{"derivedFrom":[subQ1,subQ0]});Q240=makeQuery(id+"F0.imprint","IMPRINT",FACE,{"disambiguationData":[TD([[makeQuery(id+"F0.imprint","IMPRINT",EDGE,{"disambiguationData":[TD([[subQ2,-1.0]])],"derivedFrom":subQ1}),-1.0]])]});}
            var Q241;
            {var subQ0=sQuery(id+"F0.wireOp",EDGE,"E14.33.1");var subQ1=sQuery(id+"F0.wireOp",EDGE,"E14.30.0");var subQ2=makeQuery(id+"F0.imprint","INTERSECT",VERTEX,{"derivedFrom":[subQ1,subQ0]});Q241=makeQuery(id+"F0.imprint","IMPRINT",FACE,{"disambiguationData":[TD([[makeQuery(id+"F0.imprint","IMPRINT",EDGE,{"disambiguationData":[TD([[subQ2,-1.0]])],"derivedFrom":subQ1}),-1.0]])]});}
            var Q242;
            {var subQ0=sQuery(id+"F0.wireOp",EDGE,"E14.28.1");var subQ1=sQuery(id+"F0.wireOp",EDGE,"E14.25.0");var subQ2=makeQuery(id+"F0.imprint","INTERSECT",VERTEX,{"derivedFrom":[subQ1,subQ0]});Q242=makeQuery(id+"F0.imprint","IMPRINT",FACE,{"disambiguationData":[TD([[makeQuery(id+"F0.imprint","IMPRINT",EDGE,{"disambiguationData":[TD([[subQ2,-1.0]])],"derivedFrom":subQ1}),-1.0]])]});}
            var Q243;
            {var subQ0=sQuery(id+"F0.wireOp",EDGE,"E14.24.1");var subQ1=sQuery(id+"F0.wireOp",EDGE,"E14.20.0");var subQ2=makeQuery(id+"F0.imprint","INTERSECT",VERTEX,{"derivedFrom":[subQ1,subQ0]});Q243=makeQuery(id+"F0.imprint","IMPRINT",FACE,{"disambiguationData":[TD([[makeQuery(id+"F0.imprint","IMPRINT",EDGE,{"disambiguationData":[TD([[subQ2,-1.0]])],"derivedFrom":subQ1}),-1.0]])]});}
            var Q244;
            {var subQ0=sQuery(id+"F0.wireOp",EDGE,"E14.33.0");var subQ1=sQuery(id+"F0.wireOp",EDGE,"E14.1.1");var subQ2=makeQuery(id+"F0.imprint","INTERSECT",VERTEX,{"derivedFrom":[subQ1,subQ0]});Q244=makeQuery(id+"F0.imprint","IMPRINT",FACE,{"disambiguationData":[TD([[makeQuery(id+"F0.imprint","IMPRINT",EDGE,{"disambiguationData":[TD([[subQ2,-1.0]])],"derivedFrom":subQ1}),-1.0]])]});}
            var Q245;
            {var subQ0=sQuery(id+"F0.wireOp",EDGE,"E14.10.1");var subQ1=sQuery(id+"F0.wireOp",EDGE,"E14.6.0");var subQ2=makeQuery(id+"F0.imprint","INTERSECT",VERTEX,{"derivedFrom":[subQ1,subQ0]});Q245=makeQuery(id+"F0.imprint","IMPRINT",FACE,{"disambiguationData":[TD([[makeQuery(id+"F0.imprint","IMPRINT",EDGE,{"disambiguationData":[TD([[subQ2,-1.0]])],"derivedFrom":subQ1}),-1.0]])]});}
            var Q246;
            {var subQ0=sQuery(id+"F0.wireOp",EDGE,"E14.31.0");var subQ1=sQuery(id+"F0.wireOp",EDGE,"E14.1.1");var subQ2=makeQuery(id+"F0.imprint","INTERSECT",VERTEX,{"derivedFrom":[subQ1,subQ0]});Q246=makeQuery(id+"F0.imprint","IMPRINT",FACE,{"disambiguationData":[TD([[makeQuery(id+"F0.imprint","IMPRINT",EDGE,{"disambiguationData":[TD([[subQ2,-1.0]])],"derivedFrom":subQ1}),-1.0]])]});}
            var Q247;
            {var subQ0=sQuery(id+"F0.wireOp",EDGE,"E14.33.0");var subQ1=sQuery(id+"F0.wireOp",EDGE,"E9.left");var subQ2=makeQuery(id+"F0.imprint","INTERSECT",VERTEX,{"derivedFrom":[subQ1,subQ0]});Q247=makeQuery(id+"F0.imprint","IMPRINT",FACE,{"disambiguationData":[TD([[makeQuery(id+"F0.imprint","IMPRINT",EDGE,{"disambiguationData":[TD([[subQ2,-1.0]])],"derivedFrom":subQ1}),-1.0]])]});}
            var Q248;
            {var subQ0=sQuery(id+"F0.wireOp",EDGE,"E14.33.0");var subQ1=sQuery(id+"F0.wireOp",EDGE,"E14.3.1");var subQ2=makeQuery(id+"F0.imprint","INTERSECT",VERTEX,{"derivedFrom":[subQ1,subQ0]});Q248=makeQuery(id+"F0.imprint","IMPRINT",FACE,{"disambiguationData":[TD([[makeQuery(id+"F0.imprint","IMPRINT",EDGE,{"disambiguationData":[TD([[subQ2,-1.0]])],"derivedFrom":subQ1}),-1.0]])]});}
            var Q249;
            {var subQ0=sQuery(id+"F0.wireOp",EDGE,"E14.31.1");var subQ1=sQuery(id+"F0.wireOp",EDGE,"E14.26.0");var subQ2=makeQuery(id+"F0.imprint","INTERSECT",VERTEX,{"derivedFrom":[subQ1,subQ0]});Q249=makeQuery(id+"F0.imprint","IMPRINT",FACE,{"disambiguationData":[TD([[makeQuery(id+"F0.imprint","IMPRINT",EDGE,{"disambiguationData":[TD([[subQ2,-1.0]])],"derivedFrom":subQ1}),-1.0]])]});}
            var Q250;
            {var subQ0=sQuery(id+"F0.wireOp",EDGE,"E14.13.1");var subQ1=sQuery(id+"F0.wireOp",EDGE,"E14.10.0");var subQ2=makeQuery(id+"F0.imprint","INTERSECT",VERTEX,{"derivedFrom":[subQ1,subQ0]});Q250=makeQuery(id+"F0.imprint","IMPRINT",FACE,{"disambiguationData":[TD([[makeQuery(id+"F0.imprint","IMPRINT",EDGE,{"disambiguationData":[TD([[subQ2,-1.0]])],"derivedFrom":subQ1}),-1.0]])]});}
            var Q251;
            {var subQ0=sQuery(id+"F0.wireOp",EDGE,"E14.9.1");var subQ1=sQuery(id+"F0.wireOp",EDGE,"E14.5.0");var subQ2=makeQuery(id+"F0.imprint","INTERSECT",VERTEX,{"derivedFrom":[subQ1,subQ0]});Q251=makeQuery(id+"F0.imprint","IMPRINT",FACE,{"disambiguationData":[TD([[makeQuery(id+"F0.imprint","IMPRINT",EDGE,{"disambiguationData":[TD([[subQ2,-1.0]])],"derivedFrom":subQ1}),-1.0]])]});}
            var Q252;
            {var subQ0=sQuery(id+"F0.wireOp",EDGE,"E14.32.0");var subQ1=sQuery(id+"F0.wireOp",EDGE,"E14.1.1");var subQ2=makeQuery(id+"F0.imprint","INTERSECT",VERTEX,{"derivedFrom":[subQ1,subQ0]});Q252=makeQuery(id+"F0.imprint","IMPRINT",FACE,{"disambiguationData":[TD([[makeQuery(id+"F0.imprint","IMPRINT",EDGE,{"disambiguationData":[TD([[subQ2,-1.0]])],"derivedFrom":subQ1}),-1.0]])]});}
            var Q253;
            {var subQ0=sQuery(id+"F0.wireOp",EDGE,"E14.14.1");var subQ1=sQuery(id+"F0.wireOp",EDGE,"E14.7.0");var subQ2=makeQuery(id+"F0.imprint","INTERSECT",VERTEX,{"derivedFrom":[subQ1,subQ0]});Q253=makeQuery(id+"F0.imprint","IMPRINT",FACE,{"disambiguationData":[TD([[makeQuery(id+"F0.imprint","IMPRINT",EDGE,{"disambiguationData":[TD([[subQ2,-1.0]])],"derivedFrom":subQ1}),-1.0]])]});}
            var Q254;
            {var subQ0=sQuery(id+"F0.wireOp",EDGE,"E14.19.1");var subQ1=sQuery(id+"F0.wireOp",EDGE,"E14.13.0");var subQ2=makeQuery(id+"F0.imprint","INTERSECT",VERTEX,{"derivedFrom":[subQ1,subQ0]});Q254=makeQuery(id+"F0.imprint","IMPRINT",FACE,{"disambiguationData":[TD([[makeQuery(id+"F0.imprint","IMPRINT",EDGE,{"disambiguationData":[TD([[subQ2,-1.0]])],"derivedFrom":subQ1}),-1.0]])]});}
            var Q255;
            {var subQ0=sQuery(id+"F0.wireOp",EDGE,"E14.15.1");var subQ1=sQuery(id+"F0.wireOp",EDGE,"E14.12.0");var subQ2=makeQuery(id+"F0.imprint","INTERSECT",VERTEX,{"derivedFrom":[subQ1,subQ0]});Q255=makeQuery(id+"F0.imprint","IMPRINT",FACE,{"disambiguationData":[TD([[makeQuery(id+"F0.imprint","IMPRINT",EDGE,{"disambiguationData":[TD([[subQ2,-1.0]])],"derivedFrom":subQ1}),-1.0]])]});}
            var Q256;
            {var subQ0=sQuery(id+"F0.wireOp",EDGE,"E14.4.1");var subQ1=sQuery(id+"F0.wireOp",EDGE,"E9.right");var subQ2=makeQuery(id+"F0.imprint","INTERSECT",VERTEX,{"derivedFrom":[subQ1,subQ0]});Q256=makeQuery(id+"F0.imprint","IMPRINT",FACE,{"disambiguationData":[TD([[makeQuery(id+"F0.imprint","IMPRINT",EDGE,{"disambiguationData":[TD([[subQ2,-1.0]])],"derivedFrom":subQ1}),1.0]])]});}
            var Q257;
            {var subQ0=sQuery(id+"F0.wireOp",EDGE,"E14.14.1");var subQ1=sQuery(id+"F0.wireOp",EDGE,"E14.8.0");var subQ2=makeQuery(id+"F0.imprint","INTERSECT",VERTEX,{"derivedFrom":[subQ1,subQ0]});Q257=makeQuery(id+"F0.imprint","IMPRINT",FACE,{"disambiguationData":[TD([[makeQuery(id+"F0.imprint","IMPRINT",EDGE,{"disambiguationData":[TD([[subQ2,-1.0]])],"derivedFrom":subQ1}),-1.0]])]});}
            var Q258;
            {var subQ0=sQuery(id+"F0.wireOp",EDGE,"E14.32.1");var subQ1=sQuery(id+"F0.wireOp",EDGE,"E14.27.0");var subQ2=makeQuery(id+"F0.imprint","INTERSECT",VERTEX,{"derivedFrom":[subQ1,subQ0]});Q258=makeQuery(id+"F0.imprint","IMPRINT",FACE,{"disambiguationData":[TD([[makeQuery(id+"F0.imprint","IMPRINT",EDGE,{"disambiguationData":[TD([[subQ2,-1.0]])],"derivedFrom":subQ1}),-1.0]])]});}
            var Q259;
            {var subQ0=sQuery(id+"F0.wireOp",EDGE,"E14.30.1");var subQ1=sQuery(id+"F0.wireOp",EDGE,"E14.24.0");var subQ2=makeQuery(id+"F0.imprint","INTERSECT",VERTEX,{"derivedFrom":[subQ1,subQ0]});Q259=makeQuery(id+"F0.imprint","IMPRINT",FACE,{"disambiguationData":[TD([[makeQuery(id+"F0.imprint","IMPRINT",EDGE,{"disambiguationData":[TD([[subQ2,-1.0]])],"derivedFrom":subQ1}),-1.0]])]});}
            var Q260;
            {var subQ0=sQuery(id+"F0.wireOp",EDGE,"E14.17.1");var subQ1=sQuery(id+"F0.wireOp",EDGE,"E14.12.0");var subQ2=makeQuery(id+"F0.imprint","INTERSECT",VERTEX,{"derivedFrom":[subQ1,subQ0]});Q260=makeQuery(id+"F0.imprint","IMPRINT",FACE,{"disambiguationData":[TD([[makeQuery(id+"F0.imprint","IMPRINT",EDGE,{"disambiguationData":[TD([[subQ2,-1.0]])],"derivedFrom":subQ1}),-1.0]])]});}
            var Q261;
            {var subQ0=sQuery(id+"F0.wireOp",EDGE,"E14.6.1");var subQ1=sQuery(id+"F0.wireOp",EDGE,"E14.2.0");var subQ2=makeQuery(id+"F0.imprint","INTERSECT",VERTEX,{"derivedFrom":[subQ1,subQ0]});Q261=makeQuery(id+"F0.imprint","IMPRINT",FACE,{"disambiguationData":[TD([[makeQuery(id+"F0.imprint","IMPRINT",EDGE,{"disambiguationData":[TD([[subQ2,-1.0]])],"derivedFrom":subQ1}),-1.0]])]});}
            var Q262;
            {var subQ0=sQuery(id+"F0.wireOp",EDGE,"E14.11.1");var subQ1=sQuery(id+"F0.wireOp",EDGE,"E14.7.0");var subQ2=makeQuery(id+"F0.imprint","INTERSECT",VERTEX,{"derivedFrom":[subQ1,subQ0]});Q262=makeQuery(id+"F0.imprint","IMPRINT",FACE,{"disambiguationData":[TD([[makeQuery(id+"F0.imprint","IMPRINT",EDGE,{"disambiguationData":[TD([[subQ2,-1.0]])],"derivedFrom":subQ1}),-1.0]])]});}
            var Q263;
            {var subQ0=sQuery(id+"F0.wireOp",EDGE,"E14.15.1");var subQ1=sQuery(id+"F0.wireOp",EDGE,"E14.10.0");var subQ2=makeQuery(id+"F0.imprint","INTERSECT",VERTEX,{"derivedFrom":[subQ1,subQ0]});Q263=makeQuery(id+"F0.imprint","IMPRINT",FACE,{"disambiguationData":[TD([[makeQuery(id+"F0.imprint","IMPRINT",EDGE,{"disambiguationData":[TD([[subQ2,-1.0]])],"derivedFrom":subQ1}),-1.0]])]});}
            var Q264;
            {var subQ0=sQuery(id+"F0.wireOp",EDGE,"E14.33.1");var subQ1=sQuery(id+"F0.wireOp",EDGE,"E14.28.0");var subQ2=makeQuery(id+"F0.imprint","INTERSECT",VERTEX,{"derivedFrom":[subQ1,subQ0]});Q264=makeQuery(id+"F0.imprint","IMPRINT",FACE,{"disambiguationData":[TD([[makeQuery(id+"F0.imprint","IMPRINT",EDGE,{"disambiguationData":[TD([[subQ2,-1.0]])],"derivedFrom":subQ1}),-1.0]])]});}
            var Q265;
            {var subQ0=sQuery(id+"F0.wireOp",EDGE,"E14.32.0");var subQ1=sQuery(id+"F0.wireOp",EDGE,"E9.left");var subQ2=makeQuery(id+"F0.imprint","INTERSECT",VERTEX,{"derivedFrom":[subQ1,subQ0]});Q265=makeQuery(id+"F0.imprint","IMPRINT",FACE,{"disambiguationData":[TD([[makeQuery(id+"F0.imprint","IMPRINT",EDGE,{"disambiguationData":[TD([[subQ2,-1.0]])],"derivedFrom":subQ1}),-1.0]])]});}
            var Q266;
            {var subQ0=sQuery(id+"F0.wireOp",EDGE,"E14.9.1");var subQ1=sQuery(id+"F0.wireOp",EDGE,"E14.6.0");var subQ2=makeQuery(id+"F0.imprint","INTERSECT",VERTEX,{"derivedFrom":[subQ1,subQ0]});Q266=makeQuery(id+"F0.imprint","IMPRINT",FACE,{"disambiguationData":[TD([[makeQuery(id+"F0.imprint","IMPRINT",EDGE,{"disambiguationData":[TD([[subQ2,-1.0]])],"derivedFrom":subQ1}),-1.0]])]});}
            var Q267;
            {var subQ0=sQuery(id+"F0.wireOp",EDGE,"E14.25.1");var subQ1=sQuery(id+"F0.wireOp",EDGE,"E14.21.0");var subQ2=makeQuery(id+"F0.imprint","INTERSECT",VERTEX,{"derivedFrom":[subQ1,subQ0]});Q267=makeQuery(id+"F0.imprint","IMPRINT",FACE,{"disambiguationData":[TD([[makeQuery(id+"F0.imprint","IMPRINT",EDGE,{"disambiguationData":[TD([[subQ2,-1.0]])],"derivedFrom":subQ1}),-1.0]])]});}
            var Q268;
            {var subQ0=sQuery(id+"F0.wireOp",EDGE,"E14.15.1");var subQ1=sQuery(id+"F0.wireOp",EDGE,"E14.9.0");var subQ2=makeQuery(id+"F0.imprint","INTERSECT",VERTEX,{"derivedFrom":[subQ1,subQ0]});Q268=makeQuery(id+"F0.imprint","IMPRINT",FACE,{"disambiguationData":[TD([[makeQuery(id+"F0.imprint","IMPRINT",EDGE,{"disambiguationData":[TD([[subQ2,-1.0]])],"derivedFrom":subQ1}),-1.0]])]});}
            var Q269;
            {var subQ0=sQuery(id+"F0.wireOp",EDGE,"E14.25.1");var subQ1=sQuery(id+"F0.wireOp",EDGE,"E14.19.0");var subQ2=makeQuery(id+"F0.imprint","INTERSECT",VERTEX,{"derivedFrom":[subQ1,subQ0]});Q269=makeQuery(id+"F0.imprint","IMPRINT",FACE,{"disambiguationData":[TD([[makeQuery(id+"F0.imprint","IMPRINT",EDGE,{"disambiguationData":[TD([[subQ2,-1.0]])],"derivedFrom":subQ1}),-1.0]])]});}
            var Q270;
            {var subQ0=sQuery(id+"F0.wireOp",EDGE,"E14.33.1");var subQ1=sQuery(id+"F0.wireOp",EDGE,"E14.29.0");var subQ2=makeQuery(id+"F0.imprint","INTERSECT",VERTEX,{"derivedFrom":[subQ1,subQ0]});Q270=makeQuery(id+"F0.imprint","IMPRINT",FACE,{"disambiguationData":[TD([[makeQuery(id+"F0.imprint","IMPRINT",EDGE,{"disambiguationData":[TD([[subQ2,-1.0]])],"derivedFrom":subQ1}),-1.0]])]});}
            var Q271;
            {var subQ0=sQuery(id+"F0.wireOp",EDGE,"E14.13.1");var subQ1=sQuery(id+"F0.wireOp",EDGE,"E14.9.0");var subQ2=makeQuery(id+"F0.imprint","INTERSECT",VERTEX,{"derivedFrom":[subQ1,subQ0]});Q271=makeQuery(id+"F0.imprint","IMPRINT",FACE,{"disambiguationData":[TD([[makeQuery(id+"F0.imprint","IMPRINT",EDGE,{"disambiguationData":[TD([[subQ2,-1.0]])],"derivedFrom":subQ1}),-1.0]])]});}
            var Q272;
            {var subQ0=sQuery(id+"F0.wireOp",EDGE,"E14.31.1");var subQ1=sQuery(id+"F0.wireOp",EDGE,"E14.25.0");var subQ2=makeQuery(id+"F0.imprint","INTERSECT",VERTEX,{"derivedFrom":[subQ1,subQ0]});Q272=makeQuery(id+"F0.imprint","IMPRINT",FACE,{"disambiguationData":[TD([[makeQuery(id+"F0.imprint","IMPRINT",EDGE,{"disambiguationData":[TD([[subQ2,-1.0]])],"derivedFrom":subQ1}),-1.0]])]});}
            var Q273;
            {var subQ0=sQuery(id+"F0.wireOp",EDGE,"E14.26.1");var subQ1=sQuery(id+"F0.wireOp",EDGE,"E14.20.0");var subQ2=makeQuery(id+"F0.imprint","INTERSECT",VERTEX,{"derivedFrom":[subQ1,subQ0]});Q273=makeQuery(id+"F0.imprint","IMPRINT",FACE,{"disambiguationData":[TD([[makeQuery(id+"F0.imprint","IMPRINT",EDGE,{"disambiguationData":[TD([[subQ2,-1.0]])],"derivedFrom":subQ1}),-1.0]])]});}
            var Q274;
            {var subQ0=sQuery(id+"F0.wireOp",EDGE,"E14.34.0");var subQ1=sQuery(id+"F0.wireOp",EDGE,"E14.3.1");var subQ2=makeQuery(id+"F0.imprint","INTERSECT",VERTEX,{"derivedFrom":[subQ1,subQ0]});Q274=makeQuery(id+"F0.imprint","IMPRINT",FACE,{"disambiguationData":[TD([[makeQuery(id+"F0.imprint","IMPRINT",EDGE,{"disambiguationData":[TD([[subQ2,-1.0]])],"derivedFrom":subQ1}),-1.0]])]});}
            var Q275;
            {var subQ0=sQuery(id+"F0.wireOp",EDGE,"E14.18.1");var subQ1=sQuery(id+"F0.wireOp",EDGE,"E14.12.0");var subQ2=makeQuery(id+"F0.imprint","INTERSECT",VERTEX,{"derivedFrom":[subQ1,subQ0]});Q275=makeQuery(id+"F0.imprint","IMPRINT",FACE,{"disambiguationData":[TD([[makeQuery(id+"F0.imprint","IMPRINT",EDGE,{"disambiguationData":[TD([[subQ2,-1.0]])],"derivedFrom":subQ1}),-1.0]])]});}
            var Q276;
            {var subQ0=sQuery(id+"F0.wireOp",EDGE,"E14.31.1");var subQ1=sQuery(id+"F0.wireOp",EDGE,"E14.28.0");var subQ2=makeQuery(id+"F0.imprint","INTERSECT",VERTEX,{"derivedFrom":[subQ1,subQ0]});Q276=makeQuery(id+"F0.imprint","IMPRINT",FACE,{"disambiguationData":[TD([[makeQuery(id+"F0.imprint","IMPRINT",EDGE,{"disambiguationData":[TD([[subQ2,-1.0]])],"derivedFrom":subQ1}),-1.0]])]});}
            var Q277;
            {var subQ0=sQuery(id+"F0.wireOp",EDGE,"E14.34.1");var subQ1=sQuery(id+"F0.wireOp",EDGE,"E14.28.0");var subQ2=makeQuery(id+"F0.imprint","INTERSECT",VERTEX,{"derivedFrom":[subQ1,subQ0]});Q277=makeQuery(id+"F0.imprint","IMPRINT",FACE,{"disambiguationData":[TD([[makeQuery(id+"F0.imprint","IMPRINT",EDGE,{"disambiguationData":[TD([[subQ2,-1.0]])],"derivedFrom":subQ1}),-1.0]])]});}
            var Q278;
            {var subQ0=sQuery(id+"F0.wireOp",EDGE,"E14.30.0");var subQ1=sQuery(id+"F0.wireOp",EDGE,"E9.left");var subQ2=makeQuery(id+"F0.imprint","INTERSECT",VERTEX,{"derivedFrom":[subQ1,subQ0]});Q278=makeQuery(id+"F0.imprint","IMPRINT",FACE,{"disambiguationData":[TD([[makeQuery(id+"F0.imprint","IMPRINT",EDGE,{"disambiguationData":[TD([[subQ2,-1.0]])],"derivedFrom":subQ1}),1.0]])]});}
            var Q279;
            {var subQ0=sQuery(id+"F0.wireOp",EDGE,"E14.3.1");var subQ1=sQuery(id+"F0.wireOp",EDGE,"E9.right");var subQ2=makeQuery(id+"F0.imprint","INTERSECT",VERTEX,{"derivedFrom":[subQ1,subQ0]});Q279=makeQuery(id+"F0.imprint","IMPRINT",FACE,{"disambiguationData":[TD([[makeQuery(id+"F0.imprint","IMPRINT",EDGE,{"disambiguationData":[TD([[subQ2,-1.0]])],"derivedFrom":subQ1}),-1.0]])]});}
            var Q280;
            {var subQ0=sQuery(id+"F0.wireOp",EDGE,"E14.9.1");var subQ1=sQuery(id+"F0.wireOp",EDGE,"E14.4.0");var subQ2=makeQuery(id+"F0.imprint","INTERSECT",VERTEX,{"derivedFrom":[subQ1,subQ0]});Q280=makeQuery(id+"F0.imprint","IMPRINT",FACE,{"disambiguationData":[TD([[makeQuery(id+"F0.imprint","IMPRINT",EDGE,{"disambiguationData":[TD([[subQ2,-1.0]])],"derivedFrom":subQ1}),-1.0]])]});}
            var Q281;
            {var subQ0=sQuery(id+"F0.wireOp",EDGE,"E14.31.1");var subQ1=sQuery(id+"F0.wireOp",EDGE,"E14.27.0");var subQ2=makeQuery(id+"F0.imprint","INTERSECT",VERTEX,{"derivedFrom":[subQ1,subQ0]});Q281=makeQuery(id+"F0.imprint","IMPRINT",FACE,{"disambiguationData":[TD([[makeQuery(id+"F0.imprint","IMPRINT",EDGE,{"disambiguationData":[TD([[subQ2,-1.0]])],"derivedFrom":subQ1}),-1.0]])]});}
            var Q282;
            {var subQ0=sQuery(id+"F0.wireOp",EDGE,"E14.8.1");var subQ1=sQuery(id+"F0.wireOp",EDGE,"E14.4.0");var subQ2=makeQuery(id+"F0.imprint","INTERSECT",VERTEX,{"derivedFrom":[subQ1,subQ0]});Q282=makeQuery(id+"F0.imprint","IMPRINT",FACE,{"disambiguationData":[TD([[makeQuery(id+"F0.imprint","IMPRINT",EDGE,{"disambiguationData":[TD([[subQ2,-1.0]])],"derivedFrom":subQ1}),-1.0]])]});}
            var Q283;
            {var subQ0=sQuery(id+"F0.wireOp",EDGE,"E14.6.1");var subQ1=sQuery(id+"F0.wireOp",EDGE,"E14.1.0");var subQ2=makeQuery(id+"F0.imprint","INTERSECT",VERTEX,{"derivedFrom":[subQ1,subQ0]});Q283=makeQuery(id+"F0.imprint","IMPRINT",FACE,{"disambiguationData":[TD([[makeQuery(id+"F0.imprint","IMPRINT",EDGE,{"disambiguationData":[TD([[subQ2,-1.0]])],"derivedFrom":subQ1}),-1.0]])]});}
            var Q284;
            {var subQ0=sQuery(id+"F0.wireOp",EDGE,"E14.26.1");var subQ1=sQuery(id+"F0.wireOp",EDGE,"E14.21.0");var subQ2=makeQuery(id+"F0.imprint","INTERSECT",VERTEX,{"derivedFrom":[subQ1,subQ0]});Q284=makeQuery(id+"F0.imprint","IMPRINT",FACE,{"disambiguationData":[TD([[makeQuery(id+"F0.imprint","IMPRINT",EDGE,{"disambiguationData":[TD([[subQ2,-1.0]])],"derivedFrom":subQ1}),-1.0]])]});}
            var Q285;
            {var subQ0=sQuery(id+"F0.wireOp",EDGE,"E14.21.1");var subQ1=sQuery(id+"F0.wireOp",EDGE,"E14.17.0");var subQ2=makeQuery(id+"F0.imprint","INTERSECT",VERTEX,{"derivedFrom":[subQ1,subQ0]});Q285=makeQuery(id+"F0.imprint","IMPRINT",FACE,{"disambiguationData":[TD([[makeQuery(id+"F0.imprint","IMPRINT",EDGE,{"disambiguationData":[TD([[subQ2,-1.0]])],"derivedFrom":subQ1}),-1.0]])]});}
            var Q286;
            {var subQ0=sQuery(id+"F0.wireOp",EDGE,"E14.22.1");var subQ1=sQuery(id+"F0.wireOp",EDGE,"E14.16.0");var subQ2=makeQuery(id+"F0.imprint","INTERSECT",VERTEX,{"derivedFrom":[subQ1,subQ0]});Q286=makeQuery(id+"F0.imprint","IMPRINT",FACE,{"disambiguationData":[TD([[makeQuery(id+"F0.imprint","IMPRINT",EDGE,{"disambiguationData":[TD([[subQ2,-1.0]])],"derivedFrom":subQ1}),-1.0]])]});}
            var Q287;
            {var subQ0=sQuery(id+"F0.wireOp",EDGE,"E14.21.1");var subQ1=sQuery(id+"F0.wireOp",EDGE,"E14.16.0");var subQ2=makeQuery(id+"F0.imprint","INTERSECT",VERTEX,{"derivedFrom":[subQ1,subQ0]});Q287=makeQuery(id+"F0.imprint","IMPRINT",FACE,{"disambiguationData":[TD([[makeQuery(id+"F0.imprint","IMPRINT",EDGE,{"disambiguationData":[TD([[subQ2,-1.0]])],"derivedFrom":subQ1}),-1.0]])]});}
            var Q288;
            {var subQ0=sQuery(id+"F0.wireOp",EDGE,"E14.10.1");var subQ1=sQuery(id+"F0.wireOp",EDGE,"E14.4.0");var subQ2=makeQuery(id+"F0.imprint","INTERSECT",VERTEX,{"derivedFrom":[subQ1,subQ0]});Q288=makeQuery(id+"F0.imprint","IMPRINT",FACE,{"disambiguationData":[TD([[makeQuery(id+"F0.imprint","IMPRINT",EDGE,{"disambiguationData":[TD([[subQ2,-1.0]])],"derivedFrom":subQ1}),-1.0]])]});}
            var Q289;
            {var subQ0=sQuery(id+"F0.wireOp",EDGE,"E14.22.1");var subQ1=sQuery(id+"F0.wireOp",EDGE,"E14.19.0");var subQ2=makeQuery(id+"F0.imprint","INTERSECT",VERTEX,{"derivedFrom":[subQ1,subQ0]});Q289=makeQuery(id+"F0.imprint","IMPRINT",FACE,{"disambiguationData":[TD([[makeQuery(id+"F0.imprint","IMPRINT",EDGE,{"disambiguationData":[TD([[subQ2,-1.0]])],"derivedFrom":subQ1}),-1.0]])]});}
            var Q290;
            {var subQ0=sQuery(id+"F0.wireOp",EDGE,"E14.34.1");var subQ1=sQuery(id+"F0.wireOp",EDGE,"E14.31.0");var subQ2=makeQuery(id+"F0.imprint","INTERSECT",VERTEX,{"derivedFrom":[subQ1,subQ0]});Q290=makeQuery(id+"F0.imprint","IMPRINT",FACE,{"disambiguationData":[TD([[makeQuery(id+"F0.imprint","IMPRINT",EDGE,{"disambiguationData":[TD([[subQ2,-1.0]])],"derivedFrom":subQ1}),-1.0]])]});}
            var Q291;
            {var subQ0=sQuery(id+"F0.wireOp",EDGE,"E14.15.1");var subQ1=sQuery(id+"F0.wireOp",EDGE,"E14.7.0");var subQ2=makeQuery(id+"F0.imprint","INTERSECT",VERTEX,{"derivedFrom":[subQ1,subQ0]});Q291=makeQuery(id+"F0.imprint","IMPRINT",FACE,{"disambiguationData":[TD([[makeQuery(id+"F0.imprint","IMPRINT",EDGE,{"disambiguationData":[TD([[subQ2,-1.0]])],"derivedFrom":subQ1}),-1.0]])]});}
            var Q292;
            {var subQ0=sQuery(id+"F0.wireOp",EDGE,"E14.12.1");var subQ1=sQuery(id+"F0.wireOp",EDGE,"E14.6.0");var subQ2=makeQuery(id+"F0.imprint","INTERSECT",VERTEX,{"derivedFrom":[subQ1,subQ0]});Q292=makeQuery(id+"F0.imprint","IMPRINT",FACE,{"disambiguationData":[TD([[makeQuery(id+"F0.imprint","IMPRINT",EDGE,{"disambiguationData":[TD([[subQ2,-1.0]])],"derivedFrom":subQ1}),-1.0]])]});}
            var Q293;
            {var subQ0=sQuery(id+"F0.wireOp",EDGE,"E14.33.0");var subQ1=sQuery(id+"F0.wireOp",EDGE,"E9.left");var subQ2=makeQuery(id+"F0.imprint","INTERSECT",VERTEX,{"derivedFrom":[subQ1,subQ0]});Q293=makeQuery(id+"F0.imprint","IMPRINT",FACE,{"disambiguationData":[TD([[makeQuery(id+"F0.imprint","IMPRINT",EDGE,{"disambiguationData":[TD([[subQ2,-1.0]])],"derivedFrom":subQ1}),1.0]])]});}
            var Q294;
            {var subQ0=sQuery(id+"F0.wireOp",EDGE,"E14.4.1");var subQ1=sQuery(id+"F0.wireOp",EDGE,"E9.right");var subQ2=makeQuery(id+"F0.imprint","INTERSECT",VERTEX,{"derivedFrom":[subQ1,subQ0]});Q294=makeQuery(id+"F0.imprint","IMPRINT",FACE,{"disambiguationData":[TD([[makeQuery(id+"F0.imprint","IMPRINT",EDGE,{"disambiguationData":[TD([[subQ2,-1.0]])],"derivedFrom":subQ1}),-1.0]])]});}
            var Q295;
            {var subQ0=sQuery(id+"F0.wireOp",EDGE,"E14.34.0");var subQ1=sQuery(id+"F0.wireOp",EDGE,"E14.2.1");var subQ2=makeQuery(id+"F0.imprint","INTERSECT",VERTEX,{"derivedFrom":[subQ1,subQ0]});Q295=makeQuery(id+"F0.imprint","IMPRINT",FACE,{"disambiguationData":[TD([[makeQuery(id+"F0.imprint","IMPRINT",EDGE,{"disambiguationData":[TD([[subQ2,-1.0]])],"derivedFrom":subQ1}),-1.0]])]});}
            var Q296;
            {var subQ0=sQuery(id+"F0.wireOp",EDGE,"E14.31.0");var subQ1=sQuery(id+"F0.wireOp",EDGE,"E9.left");var subQ2=makeQuery(id+"F0.imprint","INTERSECT",VERTEX,{"derivedFrom":[subQ1,subQ0]});Q296=makeQuery(id+"F0.imprint","IMPRINT",FACE,{"disambiguationData":[TD([[makeQuery(id+"F0.imprint","IMPRINT",EDGE,{"disambiguationData":[TD([[subQ2,-1.0]])],"derivedFrom":subQ1}),1.0]])]});}
            var Q297;
            {var subQ0=sQuery(id+"F0.wireOp",EDGE,"E14.27.1");var subQ1=sQuery(id+"F0.wireOp",EDGE,"E14.21.0");var subQ2=makeQuery(id+"F0.imprint","INTERSECT",VERTEX,{"derivedFrom":[subQ1,subQ0]});Q297=makeQuery(id+"F0.imprint","IMPRINT",FACE,{"disambiguationData":[TD([[makeQuery(id+"F0.imprint","IMPRINT",EDGE,{"disambiguationData":[TD([[subQ2,-1.0]])],"derivedFrom":subQ1}),-1.0]])]});}
            var Q298;
            {var subQ0=sQuery(id+"F0.wireOp",EDGE,"E14.2.1");var subQ1=sQuery(id+"F0.wireOp",EDGE,"E9.right");var subQ2=makeQuery(id+"F0.imprint","INTERSECT",VERTEX,{"derivedFrom":[subQ1,subQ0]});Q298=makeQuery(id+"F0.imprint","IMPRINT",FACE,{"disambiguationData":[TD([[makeQuery(id+"F0.imprint","IMPRINT",EDGE,{"disambiguationData":[TD([[subQ2,-1.0]])],"derivedFrom":subQ1}),1.0]])]});}
            var Q299;
            {var subQ0=sQuery(id+"F0.wireOp",EDGE,"E14.23.1");var subQ1=sQuery(id+"F0.wireOp",EDGE,"E14.19.0");var subQ2=makeQuery(id+"F0.imprint","INTERSECT",VERTEX,{"derivedFrom":[subQ1,subQ0]});Q299=makeQuery(id+"F0.imprint","IMPRINT",FACE,{"disambiguationData":[TD([[makeQuery(id+"F0.imprint","IMPRINT",EDGE,{"disambiguationData":[TD([[subQ2,-1.0]])],"derivedFrom":subQ1}),-1.0]])]});}
            var Q300;
            {var subQ0=sQuery(id+"F0.wireOp",EDGE,"E14.14.1");var subQ1=sQuery(id+"F0.wireOp",EDGE,"E14.11.0");var subQ2=makeQuery(id+"F0.imprint","INTERSECT",VERTEX,{"derivedFrom":[subQ1,subQ0]});Q300=makeQuery(id+"F0.imprint","IMPRINT",FACE,{"disambiguationData":[TD([[makeQuery(id+"F0.imprint","IMPRINT",EDGE,{"disambiguationData":[TD([[subQ2,-1.0]])],"derivedFrom":subQ1}),-1.0]])]});}
            var Q301;
            {var subQ0=sQuery(id+"F0.wireOp",EDGE,"E14.26.1");var subQ1=sQuery(id+"F0.wireOp",EDGE,"E14.23.0");var subQ2=makeQuery(id+"F0.imprint","INTERSECT",VERTEX,{"derivedFrom":[subQ1,subQ0]});Q301=makeQuery(id+"F0.imprint","IMPRINT",FACE,{"disambiguationData":[TD([[makeQuery(id+"F0.imprint","IMPRINT",EDGE,{"disambiguationData":[TD([[subQ2,-1.0]])],"derivedFrom":subQ1}),-1.0]])]});}
            var Q302;
            {var subQ0=sQuery(id+"F0.wireOp",EDGE,"E14.18.1");var subQ1=sQuery(id+"F0.wireOp",EDGE,"E14.14.0");var subQ2=makeQuery(id+"F0.imprint","INTERSECT",VERTEX,{"derivedFrom":[subQ1,subQ0]});Q302=makeQuery(id+"F0.imprint","IMPRINT",FACE,{"disambiguationData":[TD([[makeQuery(id+"F0.imprint","IMPRINT",EDGE,{"disambiguationData":[TD([[subQ2,-1.0]])],"derivedFrom":subQ1}),-1.0]])]});}
            var Q303;
            {var subQ0=sQuery(id+"F0.wireOp",EDGE,"E14.16.1");var subQ1=sQuery(id+"F0.wireOp",EDGE,"E14.13.0");var subQ2=makeQuery(id+"F0.imprint","INTERSECT",VERTEX,{"derivedFrom":[subQ1,subQ0]});Q303=makeQuery(id+"F0.imprint","IMPRINT",FACE,{"disambiguationData":[TD([[makeQuery(id+"F0.imprint","IMPRINT",EDGE,{"disambiguationData":[TD([[subQ2,-1.0]])],"derivedFrom":subQ1}),-1.0]])]});}
            var Q304;
            {var subQ0=sQuery(id+"F0.wireOp",EDGE,"E14.35.1");var subQ1=sQuery(id+"F0.wireOp",EDGE,"E14.31.0");var subQ2=makeQuery(id+"F0.imprint","INTERSECT",VERTEX,{"derivedFrom":[subQ1,subQ0]});Q304=makeQuery(id+"F0.imprint","IMPRINT",FACE,{"disambiguationData":[TD([[makeQuery(id+"F0.imprint","IMPRINT",EDGE,{"disambiguationData":[TD([[subQ2,-1.0]])],"derivedFrom":subQ1}),-1.0]])]});}
            var Q305;
            {var subQ0=sQuery(id+"F0.wireOp",EDGE,"E14.29.1");var subQ1=sQuery(id+"F0.wireOp",EDGE,"E14.25.0");var subQ2=makeQuery(id+"F0.imprint","INTERSECT",VERTEX,{"derivedFrom":[subQ1,subQ0]});Q305=makeQuery(id+"F0.imprint","IMPRINT",FACE,{"disambiguationData":[TD([[makeQuery(id+"F0.imprint","IMPRINT",EDGE,{"disambiguationData":[TD([[subQ2,-1.0]])],"derivedFrom":subQ1}),-1.0]])]});}
            var Q306;
            {var subQ0=sQuery(id+"F0.wireOp",EDGE,"E14.21.1");var subQ1=sQuery(id+"F0.wireOp",EDGE,"E14.18.0");var subQ2=makeQuery(id+"F0.imprint","INTERSECT",VERTEX,{"derivedFrom":[subQ1,subQ0]});Q306=makeQuery(id+"F0.imprint","IMPRINT",FACE,{"disambiguationData":[TD([[makeQuery(id+"F0.imprint","IMPRINT",EDGE,{"disambiguationData":[TD([[subQ2,-1.0]])],"derivedFrom":subQ1}),-1.0]])]});}
            var Q307;
            {var subQ0=sQuery(id+"F0.wireOp",EDGE,"E14.19.1");var subQ1=sQuery(id+"F0.wireOp",EDGE,"E14.16.0");var subQ2=makeQuery(id+"F0.imprint","INTERSECT",VERTEX,{"derivedFrom":[subQ1,subQ0]});Q307=makeQuery(id+"F0.imprint","IMPRINT",FACE,{"disambiguationData":[TD([[makeQuery(id+"F0.imprint","IMPRINT",EDGE,{"disambiguationData":[TD([[subQ2,-1.0]])],"derivedFrom":subQ1}),-1.0]])]});}
            var Q308;
            {var subQ0=sQuery(id+"F0.wireOp",EDGE,"E14.5.1");var subQ1=sQuery(id+"F0.wireOp",EDGE,"E14.1.0");var subQ2=makeQuery(id+"F0.imprint","INTERSECT",VERTEX,{"derivedFrom":[subQ1,subQ0]});Q308=makeQuery(id+"F0.imprint","IMPRINT",FACE,{"disambiguationData":[TD([[makeQuery(id+"F0.imprint","IMPRINT",EDGE,{"disambiguationData":[TD([[subQ2,-1.0]])],"derivedFrom":subQ1}),-1.0]])]});}
            var Q309;
            {var subQ0=sQuery(id+"F0.wireOp",EDGE,"E14.30.1");var subQ1=sQuery(id+"F0.wireOp",EDGE,"E14.22.0");var subQ2=makeQuery(id+"F0.imprint","INTERSECT",VERTEX,{"derivedFrom":[subQ1,subQ0]});Q309=makeQuery(id+"F0.imprint","IMPRINT",FACE,{"disambiguationData":[TD([[makeQuery(id+"F0.imprint","IMPRINT",EDGE,{"disambiguationData":[TD([[subQ2,-1.0]])],"derivedFrom":subQ1}),-1.0]])]});}
            var Q310;
            {var subQ0=sQuery(id+"F0.wireOp",EDGE,"E14.29.1");var subQ1=sQuery(id+"F0.wireOp",EDGE,"E14.24.0");var subQ2=makeQuery(id+"F0.imprint","INTERSECT",VERTEX,{"derivedFrom":[subQ1,subQ0]});Q310=makeQuery(id+"F0.imprint","IMPRINT",FACE,{"disambiguationData":[TD([[makeQuery(id+"F0.imprint","IMPRINT",EDGE,{"disambiguationData":[TD([[subQ2,-1.0]])],"derivedFrom":subQ1}),-1.0]])]});}
            var Q311;
            {var subQ0=sQuery(id+"F0.wireOp",EDGE,"E14.25.1");var subQ1=sQuery(id+"F0.wireOp",EDGE,"E14.22.0");var subQ2=makeQuery(id+"F0.imprint","INTERSECT",VERTEX,{"derivedFrom":[subQ1,subQ0]});Q311=makeQuery(id+"F0.imprint","IMPRINT",FACE,{"disambiguationData":[TD([[makeQuery(id+"F0.imprint","IMPRINT",EDGE,{"disambiguationData":[TD([[subQ2,-1.0]])],"derivedFrom":subQ1}),-1.0]])]});}
            var Q312;
            {var subQ0=sQuery(id+"F0.wireOp",EDGE,"E14.16.1");var subQ1=sQuery(id+"F0.wireOp",EDGE,"E14.10.0");var subQ2=makeQuery(id+"F0.imprint","INTERSECT",VERTEX,{"derivedFrom":[subQ1,subQ0]});Q312=makeQuery(id+"F0.imprint","IMPRINT",FACE,{"disambiguationData":[TD([[makeQuery(id+"F0.imprint","IMPRINT",EDGE,{"disambiguationData":[TD([[subQ2,-1.0]])],"derivedFrom":subQ1}),-1.0]])]});}
            var Q313;
            {var subQ0=sQuery(id+"F0.wireOp",EDGE,"E14.28.1");var subQ1=sQuery(id+"F0.wireOp",EDGE,"E14.24.0");var subQ2=makeQuery(id+"F0.imprint","INTERSECT",VERTEX,{"derivedFrom":[subQ1,subQ0]});Q313=makeQuery(id+"F0.imprint","IMPRINT",FACE,{"disambiguationData":[TD([[makeQuery(id+"F0.imprint","IMPRINT",EDGE,{"disambiguationData":[TD([[subQ2,-1.0]])],"derivedFrom":subQ1}),-1.0]])]});}
            var Q314;
            {var subQ0=sQuery(id+"F0.wireOp",EDGE,"E14.5.1");var subQ1=sQuery(id+"F0.wireOp",EDGE,"E9.right");var subQ2=makeQuery(id+"F0.imprint","INTERSECT",VERTEX,{"derivedFrom":[subQ1,subQ0]});Q314=makeQuery(id+"F0.imprint","IMPRINT",FACE,{"disambiguationData":[TD([[makeQuery(id+"F0.imprint","IMPRINT",EDGE,{"disambiguationData":[TD([[subQ2,-1.0]])],"derivedFrom":subQ1}),1.0]])]});}
            var Q315;
            {var subQ0=sQuery(id+"F0.wireOp",EDGE,"E14.34.0");var subQ1=sQuery(id+"F0.wireOp",EDGE,"E14.4.1");var subQ2=makeQuery(id+"F0.imprint","INTERSECT",VERTEX,{"derivedFrom":[subQ1,subQ0]});Q315=makeQuery(id+"F0.imprint","IMPRINT",FACE,{"disambiguationData":[TD([[makeQuery(id+"F0.imprint","IMPRINT",EDGE,{"disambiguationData":[TD([[subQ2,-1.0]])],"derivedFrom":subQ1}),-1.0]])]});}
            var Q316;
            {var subQ0=sQuery(id+"F0.wireOp",EDGE,"E14.20.1");var subQ1=sQuery(id+"F0.wireOp",EDGE,"E14.17.0");var subQ2=makeQuery(id+"F0.imprint","INTERSECT",VERTEX,{"derivedFrom":[subQ1,subQ0]});Q316=makeQuery(id+"F0.imprint","IMPRINT",FACE,{"disambiguationData":[TD([[makeQuery(id+"F0.imprint","IMPRINT",EDGE,{"disambiguationData":[TD([[subQ2,-1.0]])],"derivedFrom":subQ1}),-1.0]])]});}
            var Q317;
            {var subQ0=sQuery(id+"F0.wireOp",EDGE,"E14.17.1");var subQ1=sQuery(id+"F0.wireOp",EDGE,"E14.13.0");var subQ2=makeQuery(id+"F0.imprint","INTERSECT",VERTEX,{"derivedFrom":[subQ1,subQ0]});Q317=makeQuery(id+"F0.imprint","IMPRINT",FACE,{"disambiguationData":[TD([[makeQuery(id+"F0.imprint","IMPRINT",EDGE,{"disambiguationData":[TD([[subQ2,-1.0]])],"derivedFrom":subQ1}),-1.0]])]});}
            var Q318;
            {var subQ0=sQuery(id+"F0.wireOp",EDGE,"E14.12.1");var subQ1=sQuery(id+"F0.wireOp",EDGE,"E14.7.0");var subQ2=makeQuery(id+"F0.imprint","INTERSECT",VERTEX,{"derivedFrom":[subQ1,subQ0]});Q318=makeQuery(id+"F0.imprint","IMPRINT",FACE,{"disambiguationData":[TD([[makeQuery(id+"F0.imprint","IMPRINT",EDGE,{"disambiguationData":[TD([[subQ2,-1.0]])],"derivedFrom":subQ1}),-1.0]])]});}
            var Q319;
            {var subQ0=sQuery(id+"F0.wireOp",EDGE,"E14.20.1");var subQ1=sQuery(id+"F0.wireOp",EDGE,"E14.14.0");var subQ2=makeQuery(id+"F0.imprint","INTERSECT",VERTEX,{"derivedFrom":[subQ1,subQ0]});Q319=makeQuery(id+"F0.imprint","IMPRINT",FACE,{"disambiguationData":[TD([[makeQuery(id+"F0.imprint","IMPRINT",EDGE,{"disambiguationData":[TD([[subQ2,-1.0]])],"derivedFrom":subQ1}),-1.0]])]});}
            var Q320;
            {var subQ0=sQuery(id+"F0.wireOp",EDGE,"E14.24.1");var subQ1=sQuery(id+"F0.wireOp",EDGE,"E14.18.0");var subQ2=makeQuery(id+"F0.imprint","INTERSECT",VERTEX,{"derivedFrom":[subQ1,subQ0]});Q320=makeQuery(id+"F0.imprint","IMPRINT",FACE,{"disambiguationData":[TD([[makeQuery(id+"F0.imprint","IMPRINT",EDGE,{"disambiguationData":[TD([[subQ2,-1.0]])],"derivedFrom":subQ1}),-1.0]])]});}
            var Q321;
            {var subQ0=sQuery(id+"F0.wireOp",EDGE,"E14.34.0");var subQ1=sQuery(id+"F0.wireOp",EDGE,"E14.1.1");var subQ2=makeQuery(id+"F0.imprint","INTERSECT",VERTEX,{"derivedFrom":[subQ1,subQ0]});Q321=makeQuery(id+"F0.imprint","IMPRINT",FACE,{"disambiguationData":[TD([[makeQuery(id+"F0.imprint","IMPRINT",EDGE,{"disambiguationData":[TD([[subQ2,-1.0]])],"derivedFrom":subQ1}),-1.0]])]});}
            var Q322;
            {var subQ0=sQuery(id+"F0.wireOp",EDGE,"E14.4.1");var subQ1=sQuery(id+"F0.wireOp",EDGE,"E14.1.0");var subQ2=makeQuery(id+"F0.imprint","INTERSECT",VERTEX,{"derivedFrom":[subQ1,subQ0]});Q322=makeQuery(id+"F0.imprint","IMPRINT",FACE,{"disambiguationData":[TD([[makeQuery(id+"F0.imprint","IMPRINT",EDGE,{"disambiguationData":[TD([[subQ2,-1.0]])],"derivedFrom":subQ1}),-1.0]])]});}
            var Q323;
            {var subQ0=sQuery(id+"F0.wireOp",EDGE,"E14.11.1");var subQ1=sQuery(id+"F0.wireOp",EDGE,"E14.6.0");var subQ2=makeQuery(id+"F0.imprint","INTERSECT",VERTEX,{"derivedFrom":[subQ1,subQ0]});Q323=makeQuery(id+"F0.imprint","IMPRINT",FACE,{"disambiguationData":[TD([[makeQuery(id+"F0.imprint","IMPRINT",EDGE,{"disambiguationData":[TD([[subQ2,-1.0]])],"derivedFrom":subQ1}),-1.0]])]});}
            var Q324;
            {var subQ0=sQuery(id+"F0.wireOp",EDGE,"E14.27.1");var subQ1=sQuery(id+"F0.wireOp",EDGE,"E14.20.0");var subQ2=makeQuery(id+"F0.imprint","INTERSECT",VERTEX,{"derivedFrom":[subQ1,subQ0]});Q324=makeQuery(id+"F0.imprint","IMPRINT",FACE,{"disambiguationData":[TD([[makeQuery(id+"F0.imprint","IMPRINT",EDGE,{"disambiguationData":[TD([[subQ2,-1.0]])],"derivedFrom":subQ1}),-1.0]])]});}
            var Q325;
            {var subQ0=sQuery(id+"F0.wireOp",EDGE,"E14.7.1");var subQ1=sQuery(id+"F0.wireOp",EDGE,"E14.1.0");var subQ2=makeQuery(id+"F0.imprint","INTERSECT",VERTEX,{"derivedFrom":[subQ1,subQ0]});Q325=makeQuery(id+"F0.imprint","IMPRINT",FACE,{"disambiguationData":[TD([[makeQuery(id+"F0.imprint","IMPRINT",EDGE,{"disambiguationData":[TD([[subQ2,-1.0]])],"derivedFrom":subQ1}),-1.0]])]});}
            var Q326;
            {var subQ0=sQuery(id+"F0.wireOp",EDGE,"E14.7.1");var subQ1=sQuery(id+"F0.wireOp",EDGE,"E14.2.0");var subQ2=makeQuery(id+"F0.imprint","INTERSECT",VERTEX,{"derivedFrom":[subQ1,subQ0]});Q326=makeQuery(id+"F0.imprint","IMPRINT",FACE,{"disambiguationData":[TD([[makeQuery(id+"F0.imprint","IMPRINT",EDGE,{"disambiguationData":[TD([[subQ2,-1.0]])],"derivedFrom":subQ1}),-1.0]])]});}
            var Q327;
            {var subQ0=sQuery(id+"F0.wireOp",EDGE,"E14.23.1");var subQ1=sQuery(id+"F0.wireOp",EDGE,"E14.17.0");var subQ2=makeQuery(id+"F0.imprint","INTERSECT",VERTEX,{"derivedFrom":[subQ1,subQ0]});Q327=makeQuery(id+"F0.imprint","IMPRINT",FACE,{"disambiguationData":[TD([[makeQuery(id+"F0.imprint","IMPRINT",EDGE,{"disambiguationData":[TD([[subQ2,-1.0]])],"derivedFrom":subQ1}),-1.0]])]});}
            var Q328;
            {var subQ0=sQuery(id+"F0.wireOp",EDGE,"E14.14.1");var subQ1=sQuery(id+"F0.wireOp",EDGE,"E14.9.0");var subQ2=makeQuery(id+"F0.imprint","INTERSECT",VERTEX,{"derivedFrom":[subQ1,subQ0]});Q328=makeQuery(id+"F0.imprint","IMPRINT",FACE,{"disambiguationData":[TD([[makeQuery(id+"F0.imprint","IMPRINT",EDGE,{"disambiguationData":[TD([[subQ2,-1.0]])],"derivedFrom":subQ1}),-1.0]])]});}
            var Q329;
            {var subQ0=sQuery(id+"F0.wireOp",EDGE,"E14.32.0");var subQ1=sQuery(id+"F0.wireOp",EDGE,"E9.left");var subQ2=makeQuery(id+"F0.imprint","INTERSECT",VERTEX,{"derivedFrom":[subQ1,subQ0]});Q329=makeQuery(id+"F0.imprint","IMPRINT",FACE,{"disambiguationData":[TD([[makeQuery(id+"F0.imprint","IMPRINT",EDGE,{"disambiguationData":[TD([[subQ2,-1.0]])],"derivedFrom":subQ1}),1.0]])]});}
            var Q330;
            {var subQ0=sQuery(id+"F0.wireOp",EDGE,"E14.6.1");var subQ1=sQuery(id+"F0.wireOp",EDGE,"E14.3.0");var subQ2=makeQuery(id+"F0.imprint","INTERSECT",VERTEX,{"derivedFrom":[subQ1,subQ0]});Q330=makeQuery(id+"F0.imprint","IMPRINT",FACE,{"disambiguationData":[TD([[makeQuery(id+"F0.imprint","IMPRINT",EDGE,{"disambiguationData":[TD([[subQ2,-1.0]])],"derivedFrom":subQ1}),-1.0]])]});}
            var Q331;
            {var subQ0=sQuery(id+"F0.wireOp",EDGE,"E14.35.1");var subQ1=sQuery(id+"F0.wireOp",EDGE,"E14.32.0");var subQ2=makeQuery(id+"F0.imprint","INTERSECT",VERTEX,{"derivedFrom":[subQ1,subQ0]});Q331=makeQuery(id+"F0.imprint","IMPRINT",FACE,{"disambiguationData":[TD([[makeQuery(id+"F0.imprint","IMPRINT",EDGE,{"disambiguationData":[TD([[subQ2,-1.0]])],"derivedFrom":subQ1}),-1.0]])]});}
            var Q332;
            {var subQ0=sQuery(id+"F0.wireOp",EDGE,"E14.25.1");var subQ1=sQuery(id+"F0.wireOp",EDGE,"E14.20.0");var subQ2=makeQuery(id+"F0.imprint","INTERSECT",VERTEX,{"derivedFrom":[subQ1,subQ0]});Q332=makeQuery(id+"F0.imprint","IMPRINT",FACE,{"disambiguationData":[TD([[makeQuery(id+"F0.imprint","IMPRINT",EDGE,{"disambiguationData":[TD([[subQ2,-1.0]])],"derivedFrom":subQ1}),-1.0]])]});}
            var Q333;
            {var subQ0=sQuery(id+"F0.wireOp",EDGE,"E14.31.1");var subQ1=sQuery(id+"F0.wireOp",EDGE,"E14.23.0");var subQ2=makeQuery(id+"F0.imprint","INTERSECT",VERTEX,{"derivedFrom":[subQ1,subQ0]});Q333=makeQuery(id+"F0.imprint","IMPRINT",FACE,{"disambiguationData":[TD([[makeQuery(id+"F0.imprint","IMPRINT",EDGE,{"disambiguationData":[TD([[subQ2,-1.0]])],"derivedFrom":subQ1}),-1.0]])]});}
            var Q334;
            {var subQ0=sQuery(id+"F0.wireOp",EDGE,"E14.24.1");var subQ1=sQuery(id+"F0.wireOp",EDGE,"E14.19.0");var subQ2=makeQuery(id+"F0.imprint","INTERSECT",VERTEX,{"derivedFrom":[subQ1,subQ0]});Q334=makeQuery(id+"F0.imprint","IMPRINT",FACE,{"disambiguationData":[TD([[makeQuery(id+"F0.imprint","IMPRINT",EDGE,{"disambiguationData":[TD([[subQ2,-1.0]])],"derivedFrom":subQ1}),-1.0]])]});}
            var Q335;
            {var subQ0=sQuery(id+"F0.wireOp",EDGE,"E14.11.1");var subQ1=sQuery(id+"F0.wireOp",EDGE,"E14.8.0");var subQ2=makeQuery(id+"F0.imprint","INTERSECT",VERTEX,{"derivedFrom":[subQ1,subQ0]});Q335=makeQuery(id+"F0.imprint","IMPRINT",FACE,{"disambiguationData":[TD([[makeQuery(id+"F0.imprint","IMPRINT",EDGE,{"disambiguationData":[TD([[subQ2,-1.0]])],"derivedFrom":subQ1}),-1.0]])]});}
            var Q336;
            {var subQ0=sQuery(id+"F0.wireOp",EDGE,"E14.28.1");var subQ1=sQuery(id+"F0.wireOp",EDGE,"E14.23.0");var subQ2=makeQuery(id+"F0.imprint","INTERSECT",VERTEX,{"derivedFrom":[subQ1,subQ0]});Q336=makeQuery(id+"F0.imprint","IMPRINT",FACE,{"disambiguationData":[TD([[makeQuery(id+"F0.imprint","IMPRINT",EDGE,{"disambiguationData":[TD([[subQ2,-1.0]])],"derivedFrom":subQ1}),-1.0]])]});}
            var Q337;
            {var subQ0=sQuery(id+"F0.wireOp",EDGE,"E14.27.1");var subQ1=sQuery(id+"F0.wireOp",EDGE,"E14.23.0");var subQ2=makeQuery(id+"F0.imprint","INTERSECT",VERTEX,{"derivedFrom":[subQ1,subQ0]});Q337=makeQuery(id+"F0.imprint","IMPRINT",FACE,{"disambiguationData":[TD([[makeQuery(id+"F0.imprint","IMPRINT",EDGE,{"disambiguationData":[TD([[subQ2,-1.0]])],"derivedFrom":subQ1}),-1.0]])]});}
            var Q338;
            {var subQ0=sQuery(id+"F0.wireOp",EDGE,"E14.18.1");var subQ1=sQuery(id+"F0.wireOp",EDGE,"E14.10.0");var subQ2=makeQuery(id+"F0.imprint","INTERSECT",VERTEX,{"derivedFrom":[subQ1,subQ0]});Q338=makeQuery(id+"F0.imprint","IMPRINT",FACE,{"disambiguationData":[TD([[makeQuery(id+"F0.imprint","IMPRINT",EDGE,{"disambiguationData":[TD([[subQ2,-1.0]])],"derivedFrom":subQ1}),-1.0]])]});}
            var Q339;
            {var subQ0=sQuery(id+"F0.wireOp",EDGE,"E14.16.1");var subQ1=sQuery(id+"F0.wireOp",EDGE,"E14.9.0");var subQ2=makeQuery(id+"F0.imprint","INTERSECT",VERTEX,{"derivedFrom":[subQ1,subQ0]});Q339=makeQuery(id+"F0.imprint","IMPRINT",FACE,{"disambiguationData":[TD([[makeQuery(id+"F0.imprint","IMPRINT",EDGE,{"disambiguationData":[TD([[subQ2,-1.0]])],"derivedFrom":subQ1}),-1.0]])]});}
            var Q340;
            {var subQ0=sQuery(id+"F0.wireOp",EDGE,"E14.23.1");var subQ1=sQuery(id+"F0.wireOp",EDGE,"E14.15.0");var subQ2=makeQuery(id+"F0.imprint","INTERSECT",VERTEX,{"derivedFrom":[subQ1,subQ0]});Q340=makeQuery(id+"F0.imprint","IMPRINT",FACE,{"disambiguationData":[TD([[makeQuery(id+"F0.imprint","IMPRINT",EDGE,{"disambiguationData":[TD([[subQ2,-1.0]])],"derivedFrom":subQ1}),-1.0]])]});}
            var Q341;
            {var subQ0=sQuery(id+"F0.wireOp",EDGE,"E14.20.1");var subQ1=sQuery(id+"F0.wireOp",EDGE,"E14.13.0");var subQ2=makeQuery(id+"F0.imprint","INTERSECT",VERTEX,{"derivedFrom":[subQ1,subQ0]});Q341=makeQuery(id+"F0.imprint","IMPRINT",FACE,{"disambiguationData":[TD([[makeQuery(id+"F0.imprint","IMPRINT",EDGE,{"disambiguationData":[TD([[subQ2,-1.0]])],"derivedFrom":subQ1}),-1.0]])]});}
            var Q342;
            {var subQ0=sQuery(id+"F0.wireOp",EDGE,"E14.17.1");var subQ1=sQuery(id+"F0.wireOp",EDGE,"E14.10.0");var subQ2=makeQuery(id+"F0.imprint","INTERSECT",VERTEX,{"derivedFrom":[subQ1,subQ0]});Q342=makeQuery(id+"F0.imprint","IMPRINT",FACE,{"disambiguationData":[TD([[makeQuery(id+"F0.imprint","IMPRINT",EDGE,{"disambiguationData":[TD([[subQ2,-1.0]])],"derivedFrom":subQ1}),-1.0]])]});}
            var Q343;
            {var subQ0=sQuery(id+"F0.wireOp",EDGE,"E14.31.0");var subQ1=sQuery(id+"F0.wireOp",EDGE,"E14.3.1");var subQ2=makeQuery(id+"F0.imprint","INTERSECT",VERTEX,{"derivedFrom":[subQ1,subQ0]});Q343=makeQuery(id+"F0.imprint","IMPRINT",FACE,{"disambiguationData":[TD([[makeQuery(id+"F0.imprint","IMPRINT",EDGE,{"disambiguationData":[TD([[subQ2,-1.0]])],"derivedFrom":subQ1}),-1.0]])]});}
            var Q344;
            {var subQ0=sQuery(id+"F0.wireOp",EDGE,"E14.5.1");var subQ1=sQuery(id+"F0.wireOp",EDGE,"E9.right");var subQ2=makeQuery(id+"F0.imprint","INTERSECT",VERTEX,{"derivedFrom":[subQ1,subQ0]});Q344=makeQuery(id+"F0.imprint","IMPRINT",FACE,{"disambiguationData":[TD([[makeQuery(id+"F0.imprint","IMPRINT",EDGE,{"disambiguationData":[TD([[subQ2,-1.0]])],"derivedFrom":subQ1}),-1.0]])]});}
            var Q345;
            {var subQ0=sQuery(id+"F0.wireOp",EDGE,"E14.31.1");var subQ1=sQuery(id+"F0.wireOp",EDGE,"E14.24.0");var subQ2=makeQuery(id+"F0.imprint","INTERSECT",VERTEX,{"derivedFrom":[subQ1,subQ0]});Q345=makeQuery(id+"F0.imprint","IMPRINT",FACE,{"disambiguationData":[TD([[makeQuery(id+"F0.imprint","IMPRINT",EDGE,{"disambiguationData":[TD([[subQ2,-1.0]])],"derivedFrom":subQ1}),-1.0]])]});}
            var Q346;
            {var subQ0=sQuery(id+"F0.wireOp",EDGE,"E14.10.1");var subQ1=sQuery(id+"F0.wireOp",EDGE,"E14.3.0");var subQ2=makeQuery(id+"F0.imprint","INTERSECT",VERTEX,{"derivedFrom":[subQ1,subQ0]});Q346=makeQuery(id+"F0.imprint","IMPRINT",FACE,{"disambiguationData":[TD([[makeQuery(id+"F0.imprint","IMPRINT",EDGE,{"disambiguationData":[TD([[subQ2,-1.0]])],"derivedFrom":subQ1}),-1.0]])]});}
            var Q347;
            {var subQ0=sQuery(id+"F0.wireOp",EDGE,"E14.17.1");var subQ1=sQuery(id+"F0.wireOp",EDGE,"E14.11.0");var subQ2=makeQuery(id+"F0.imprint","INTERSECT",VERTEX,{"derivedFrom":[subQ1,subQ0]});Q347=makeQuery(id+"F0.imprint","IMPRINT",FACE,{"disambiguationData":[TD([[makeQuery(id+"F0.imprint","IMPRINT",EDGE,{"disambiguationData":[TD([[subQ2,-1.0]])],"derivedFrom":subQ1}),-1.0]])]});}
            var Q348;
            {var subQ0=sQuery(id+"F0.wireOp",EDGE,"E14.26.1");var subQ1=sQuery(id+"F0.wireOp",EDGE,"E14.18.0");var subQ2=makeQuery(id+"F0.imprint","INTERSECT",VERTEX,{"derivedFrom":[subQ1,subQ0]});Q348=makeQuery(id+"F0.imprint","IMPRINT",FACE,{"disambiguationData":[TD([[makeQuery(id+"F0.imprint","IMPRINT",EDGE,{"disambiguationData":[TD([[subQ2,-1.0]])],"derivedFrom":subQ1}),-1.0]])]});}
            var Q349;
            {var subQ0=sQuery(id+"F0.wireOp",EDGE,"E14.29.1");var subQ1=sQuery(id+"F0.wireOp",EDGE,"E14.22.0");var subQ2=makeQuery(id+"F0.imprint","INTERSECT",VERTEX,{"derivedFrom":[subQ1,subQ0]});Q349=makeQuery(id+"F0.imprint","IMPRINT",FACE,{"disambiguationData":[TD([[makeQuery(id+"F0.imprint","IMPRINT",EDGE,{"disambiguationData":[TD([[subQ2,-1.0]])],"derivedFrom":subQ1}),-1.0]])]});}
            var Q350;
            {var subQ0=sQuery(id+"F0.wireOp",EDGE,"E14.25.1");var subQ1=sQuery(id+"F0.wireOp",EDGE,"E14.18.0");var subQ2=makeQuery(id+"F0.imprint","INTERSECT",VERTEX,{"derivedFrom":[subQ1,subQ0]});Q350=makeQuery(id+"F0.imprint","IMPRINT",FACE,{"disambiguationData":[TD([[makeQuery(id+"F0.imprint","IMPRINT",EDGE,{"disambiguationData":[TD([[subQ2,-1.0]])],"derivedFrom":subQ1}),-1.0]])]});}
            var Q351;
            {var subQ0=sQuery(id+"F0.wireOp",EDGE,"E14.29.0");var subQ1=sQuery(id+"F0.wireOp",EDGE,"E9.left");var subQ2=makeQuery(id+"F0.imprint","INTERSECT",VERTEX,{"derivedFrom":[subQ1,subQ0]});Q351=makeQuery(id+"F0.imprint","IMPRINT",FACE,{"disambiguationData":[TD([[makeQuery(id+"F0.imprint","IMPRINT",EDGE,{"disambiguationData":[TD([[subQ2,-1.0]])],"derivedFrom":subQ1}),1.0]])]});}
            var Q352;
            {var subQ0=sQuery(id+"F0.wireOp",EDGE,"E14.19.1");var subQ1=sQuery(id+"F0.wireOp",EDGE,"E14.12.0");var subQ2=makeQuery(id+"F0.imprint","INTERSECT",VERTEX,{"derivedFrom":[subQ1,subQ0]});Q352=makeQuery(id+"F0.imprint","IMPRINT",FACE,{"disambiguationData":[TD([[makeQuery(id+"F0.imprint","IMPRINT",EDGE,{"disambiguationData":[TD([[subQ2,-1.0]])],"derivedFrom":subQ1}),-1.0]])]});}
            var Q353;
            {var subQ0=sQuery(id+"F0.wireOp",EDGE,"E14.32.1");var subQ1=sQuery(id+"F0.wireOp",EDGE,"E14.23.0");var subQ2=makeQuery(id+"F0.imprint","INTERSECT",VERTEX,{"derivedFrom":[subQ1,subQ0]});Q353=makeQuery(id+"F0.imprint","IMPRINT",FACE,{"disambiguationData":[TD([[makeQuery(id+"F0.imprint","IMPRINT",EDGE,{"disambiguationData":[TD([[subQ2,-1.0]])],"derivedFrom":subQ1}),-1.0]])]});}
            var Q354;
            {var subQ0=sQuery(id+"F0.wireOp",EDGE,"E14.28.1");var subQ1=sQuery(id+"F0.wireOp",EDGE,"E14.20.0");var subQ2=makeQuery(id+"F0.imprint","INTERSECT",VERTEX,{"derivedFrom":[subQ1,subQ0]});Q354=makeQuery(id+"F0.imprint","IMPRINT",FACE,{"disambiguationData":[TD([[makeQuery(id+"F0.imprint","IMPRINT",EDGE,{"disambiguationData":[TD([[subQ2,-1.0]])],"derivedFrom":subQ1}),-1.0]])]});}
            var Q355;
            {var subQ0=sQuery(id+"F0.wireOp",EDGE,"E14.15.1");var subQ1=sQuery(id+"F0.wireOp",EDGE,"E14.8.0");var subQ2=makeQuery(id+"F0.imprint","INTERSECT",VERTEX,{"derivedFrom":[subQ1,subQ0]});Q355=makeQuery(id+"F0.imprint","IMPRINT",FACE,{"disambiguationData":[TD([[makeQuery(id+"F0.imprint","IMPRINT",EDGE,{"disambiguationData":[TD([[subQ2,-1.0]])],"derivedFrom":subQ1}),-1.0]])]});}
            var Q356;
            {var subQ0=sQuery(id+"F0.wireOp",EDGE,"E14.12.1");var subQ1=sQuery(id+"F0.wireOp",EDGE,"E14.4.0");var subQ2=makeQuery(id+"F0.imprint","INTERSECT",VERTEX,{"derivedFrom":[subQ1,subQ0]});Q356=makeQuery(id+"F0.imprint","IMPRINT",FACE,{"disambiguationData":[TD([[makeQuery(id+"F0.imprint","IMPRINT",EDGE,{"disambiguationData":[TD([[subQ2,-1.0]])],"derivedFrom":subQ1}),-1.0]])]});}
            var Q357;
            {var subQ0=sQuery(id+"F0.wireOp",EDGE,"E14.33.0");var subQ1=sQuery(id+"F0.wireOp",EDGE,"E14.4.1");var subQ2=makeQuery(id+"F0.imprint","INTERSECT",VERTEX,{"derivedFrom":[subQ1,subQ0]});Q357=makeQuery(id+"F0.imprint","IMPRINT",FACE,{"disambiguationData":[TD([[makeQuery(id+"F0.imprint","IMPRINT",EDGE,{"disambiguationData":[TD([[subQ2,-1.0]])],"derivedFrom":subQ1}),-1.0]])]});}
            var Q358;
            {var subQ0=sQuery(id+"F0.wireOp",EDGE,"E14.31.0");var subQ1=sQuery(id+"F0.wireOp",EDGE,"E14.2.1");var subQ2=makeQuery(id+"F0.imprint","INTERSECT",VERTEX,{"derivedFrom":[subQ1,subQ0]});Q358=makeQuery(id+"F0.imprint","IMPRINT",FACE,{"disambiguationData":[TD([[makeQuery(id+"F0.imprint","IMPRINT",EDGE,{"disambiguationData":[TD([[subQ2,-1.0]])],"derivedFrom":subQ1}),-1.0]])]});}
            var Q359;
            {var subQ0=sQuery(id+"F0.wireOp",EDGE,"E14.34.1");var subQ1=sQuery(id+"F0.wireOp",EDGE,"E14.26.0");var subQ2=makeQuery(id+"F0.imprint","INTERSECT",VERTEX,{"derivedFrom":[subQ1,subQ0]});Q359=makeQuery(id+"F0.imprint","IMPRINT",FACE,{"disambiguationData":[TD([[makeQuery(id+"F0.imprint","IMPRINT",EDGE,{"disambiguationData":[TD([[subQ2,-1.0]])],"derivedFrom":subQ1}),-1.0]])]});}
            var Q360;
            {var subQ0=sQuery(id+"F0.wireOp",EDGE,"E14.33.1");var subQ1=sQuery(id+"F0.wireOp",EDGE,"E14.26.0");var subQ2=makeQuery(id+"F0.imprint","INTERSECT",VERTEX,{"derivedFrom":[subQ1,subQ0]});Q360=makeQuery(id+"F0.imprint","IMPRINT",FACE,{"disambiguationData":[TD([[makeQuery(id+"F0.imprint","IMPRINT",EDGE,{"disambiguationData":[TD([[subQ2,-1.0]])],"derivedFrom":subQ1}),-1.0]])]});}
            var Q361;
            {var subQ0=sQuery(id+"F0.wireOp",EDGE,"E14.33.1");var subQ1=sQuery(id+"F0.wireOp",EDGE,"E14.24.0");var subQ2=makeQuery(id+"F0.imprint","INTERSECT",VERTEX,{"derivedFrom":[subQ1,subQ0]});Q361=makeQuery(id+"F0.imprint","IMPRINT",FACE,{"disambiguationData":[TD([[makeQuery(id+"F0.imprint","IMPRINT",EDGE,{"disambiguationData":[TD([[subQ2,-1.0]])],"derivedFrom":subQ1}),-1.0]])]});}
            var Q362;
            {var subQ0=sQuery(id+"F0.wireOp",EDGE,"E14.12.1");var subQ1=sQuery(id+"F0.wireOp",EDGE,"E14.5.0");var subQ2=makeQuery(id+"F0.imprint","INTERSECT",VERTEX,{"derivedFrom":[subQ1,subQ0]});Q362=makeQuery(id+"F0.imprint","IMPRINT",FACE,{"disambiguationData":[TD([[makeQuery(id+"F0.imprint","IMPRINT",EDGE,{"disambiguationData":[TD([[subQ2,-1.0]])],"derivedFrom":subQ1}),-1.0]])]});}
            var Q363;
            {var subQ0=sQuery(id+"F0.wireOp",EDGE,"E14.28.1");var subQ1=sQuery(id+"F0.wireOp",EDGE,"E14.19.0");var subQ2=makeQuery(id+"F0.imprint","INTERSECT",VERTEX,{"derivedFrom":[subQ1,subQ0]});Q363=makeQuery(id+"F0.imprint","IMPRINT",FACE,{"disambiguationData":[TD([[makeQuery(id+"F0.imprint","IMPRINT",EDGE,{"disambiguationData":[TD([[subQ2,-1.0]])],"derivedFrom":subQ1}),-1.0]])]});}
            var Q364;
            {var subQ0=sQuery(id+"F0.wireOp",EDGE,"E14.31.0");var subQ1=sQuery(id+"F0.wireOp",EDGE,"E9.left");var subQ2=makeQuery(id+"F0.imprint","INTERSECT",VERTEX,{"derivedFrom":[subQ1,subQ0]});Q364=makeQuery(id+"F0.imprint","IMPRINT",FACE,{"disambiguationData":[TD([[makeQuery(id+"F0.imprint","IMPRINT",EDGE,{"disambiguationData":[TD([[subQ2,-1.0]])],"derivedFrom":subQ1}),-1.0]])]});}
            var Q365;
            {var subQ0=sQuery(id+"F0.wireOp",EDGE,"E14.7.1");var subQ1=sQuery(id+"F0.wireOp",EDGE,"E9.right");var subQ2=makeQuery(id+"F0.imprint","INTERSECT",VERTEX,{"derivedFrom":[subQ1,subQ0]});Q365=makeQuery(id+"F0.imprint","IMPRINT",FACE,{"disambiguationData":[TD([[makeQuery(id+"F0.imprint","IMPRINT",EDGE,{"disambiguationData":[TD([[subQ2,-1.0]])],"derivedFrom":subQ1}),-1.0]])]});}
            var Q366;
            {var subQ0=sQuery(id+"F0.wireOp",EDGE,"E14.13.1");var subQ1=sQuery(id+"F0.wireOp",EDGE,"E14.6.0");var subQ2=makeQuery(id+"F0.imprint","INTERSECT",VERTEX,{"derivedFrom":[subQ1,subQ0]});Q366=makeQuery(id+"F0.imprint","IMPRINT",FACE,{"disambiguationData":[TD([[makeQuery(id+"F0.imprint","IMPRINT",EDGE,{"disambiguationData":[TD([[subQ2,-1.0]])],"derivedFrom":subQ1}),-1.0]])]});}
            var Q367;
            {var subQ0=sQuery(id+"F0.wireOp",EDGE,"E14.30.1");var subQ1=sQuery(id+"F0.wireOp",EDGE,"E14.23.0");var subQ2=makeQuery(id+"F0.imprint","INTERSECT",VERTEX,{"derivedFrom":[subQ1,subQ0]});Q367=makeQuery(id+"F0.imprint","IMPRINT",FACE,{"disambiguationData":[TD([[makeQuery(id+"F0.imprint","IMPRINT",EDGE,{"disambiguationData":[TD([[subQ2,-1.0]])],"derivedFrom":subQ1}),-1.0]])]});}
            var Q368;
            {var subQ0=sQuery(id+"F0.wireOp",EDGE,"E14.31.1");var subQ1=sQuery(id+"F0.wireOp",EDGE,"E14.21.0");var subQ2=makeQuery(id+"F0.imprint","INTERSECT",VERTEX,{"derivedFrom":[subQ1,subQ0]});Q368=makeQuery(id+"F0.imprint","IMPRINT",FACE,{"disambiguationData":[TD([[makeQuery(id+"F0.imprint","IMPRINT",EDGE,{"disambiguationData":[TD([[subQ2,-1.0]])],"derivedFrom":subQ1}),-1.0]])]});}
            var Q369;
            {var subQ0=sQuery(id+"F0.wireOp",EDGE,"E14.34.1");var subQ1=sQuery(id+"F0.wireOp",EDGE,"E14.27.0");var subQ2=makeQuery(id+"F0.imprint","INTERSECT",VERTEX,{"derivedFrom":[subQ1,subQ0]});Q369=makeQuery(id+"F0.imprint","IMPRINT",FACE,{"disambiguationData":[TD([[makeQuery(id+"F0.imprint","IMPRINT",EDGE,{"disambiguationData":[TD([[subQ2,-1.0]])],"derivedFrom":subQ1}),-1.0]])]});}
            var Q370;
            {var subQ0=sQuery(id+"F0.wireOp",EDGE,"E14.6.1");var subQ1=sQuery(id+"F0.wireOp",EDGE,"E9.right");var subQ2=makeQuery(id+"F0.imprint","INTERSECT",VERTEX,{"derivedFrom":[subQ1,subQ0]});Q370=makeQuery(id+"F0.imprint","IMPRINT",FACE,{"disambiguationData":[TD([[makeQuery(id+"F0.imprint","IMPRINT",EDGE,{"disambiguationData":[TD([[subQ2,-1.0]])],"derivedFrom":subQ1}),1.0]])]});}
            var Q371;
            {var subQ0=sQuery(id+"F0.wireOp",EDGE,"E14.21.1");var subQ1=sQuery(id+"F0.wireOp",EDGE,"E14.15.0");var subQ2=makeQuery(id+"F0.imprint","INTERSECT",VERTEX,{"derivedFrom":[subQ1,subQ0]});Q371=makeQuery(id+"F0.imprint","IMPRINT",FACE,{"disambiguationData":[TD([[makeQuery(id+"F0.imprint","IMPRINT",EDGE,{"disambiguationData":[TD([[subQ2,-1.0]])],"derivedFrom":subQ1}),-1.0]])]});}
            var Q372;
            {var subQ0=sQuery(id+"F0.wireOp",EDGE,"E14.23.1");var subQ1=sQuery(id+"F0.wireOp",EDGE,"E14.16.0");var subQ2=makeQuery(id+"F0.imprint","INTERSECT",VERTEX,{"derivedFrom":[subQ1,subQ0]});Q372=makeQuery(id+"F0.imprint","IMPRINT",FACE,{"disambiguationData":[TD([[makeQuery(id+"F0.imprint","IMPRINT",EDGE,{"disambiguationData":[TD([[subQ2,-1.0]])],"derivedFrom":subQ1}),-1.0]])]});}
            var Q373;
            {var subQ0=sQuery(id+"F0.wireOp",EDGE,"E14.8.1");var subQ1=sQuery(id+"F0.wireOp",EDGE,"E14.1.0");var subQ2=makeQuery(id+"F0.imprint","INTERSECT",VERTEX,{"derivedFrom":[subQ1,subQ0]});Q373=makeQuery(id+"F0.imprint","IMPRINT",FACE,{"disambiguationData":[TD([[makeQuery(id+"F0.imprint","IMPRINT",EDGE,{"disambiguationData":[TD([[subQ2,-1.0]])],"derivedFrom":subQ1}),-1.0]])]});}
            var Q374;
            {var subQ0=sQuery(id+"F0.wireOp",EDGE,"E14.24.1");var subQ1=sQuery(id+"F0.wireOp",EDGE,"E14.17.0");var subQ2=makeQuery(id+"F0.imprint","INTERSECT",VERTEX,{"derivedFrom":[subQ1,subQ0]});Q374=makeQuery(id+"F0.imprint","IMPRINT",FACE,{"disambiguationData":[TD([[makeQuery(id+"F0.imprint","IMPRINT",EDGE,{"disambiguationData":[TD([[subQ2,-1.0]])],"derivedFrom":subQ1}),-1.0]])]});}
            var Q375;
            {var subQ0=sQuery(id+"F0.wireOp",EDGE,"E14.30.0");var subQ1=sQuery(id+"F0.wireOp",EDGE,"E14.1.1");var subQ2=makeQuery(id+"F0.imprint","INTERSECT",VERTEX,{"derivedFrom":[subQ1,subQ0]});Q375=makeQuery(id+"F0.imprint","IMPRINT",FACE,{"disambiguationData":[TD([[makeQuery(id+"F0.imprint","IMPRINT",EDGE,{"disambiguationData":[TD([[subQ2,-1.0]])],"derivedFrom":subQ1}),-1.0]])]});}
            var Q376;
            {var subQ0=sQuery(id+"F0.wireOp",EDGE,"E14.21.1");var subQ1=sQuery(id+"F0.wireOp",EDGE,"E14.13.0");var subQ2=makeQuery(id+"F0.imprint","INTERSECT",VERTEX,{"derivedFrom":[subQ1,subQ0]});Q376=makeQuery(id+"F0.imprint","IMPRINT",FACE,{"disambiguationData":[TD([[makeQuery(id+"F0.imprint","IMPRINT",EDGE,{"disambiguationData":[TD([[subQ2,-1.0]])],"derivedFrom":subQ1}),-1.0]])]});}
            var Q377;
            {var subQ0=sQuery(id+"F0.wireOp",EDGE,"E14.26.1");var subQ1=sQuery(id+"F0.wireOp",EDGE,"E14.19.0");var subQ2=makeQuery(id+"F0.imprint","INTERSECT",VERTEX,{"derivedFrom":[subQ1,subQ0]});Q377=makeQuery(id+"F0.imprint","IMPRINT",FACE,{"disambiguationData":[TD([[makeQuery(id+"F0.imprint","IMPRINT",EDGE,{"disambiguationData":[TD([[subQ2,-1.0]])],"derivedFrom":subQ1}),-1.0]])]});}
            var Q378;
            {var subQ0=sQuery(id+"F0.wireOp",EDGE,"E14.22.1");var subQ1=sQuery(id+"F0.wireOp",EDGE,"E14.15.0");var subQ2=makeQuery(id+"F0.imprint","INTERSECT",VERTEX,{"derivedFrom":[subQ1,subQ0]});Q378=makeQuery(id+"F0.imprint","IMPRINT",FACE,{"disambiguationData":[TD([[makeQuery(id+"F0.imprint","IMPRINT",EDGE,{"disambiguationData":[TD([[subQ2,-1.0]])],"derivedFrom":subQ1}),-1.0]])]});}
            var Q379;
            {var subQ0=sQuery(id+"F0.wireOp",EDGE,"E14.28.0");var subQ1=sQuery(id+"F0.wireOp",EDGE,"E9.left");var subQ2=makeQuery(id+"F0.imprint","INTERSECT",VERTEX,{"derivedFrom":[subQ1,subQ0]});Q379=makeQuery(id+"F0.imprint","IMPRINT",FACE,{"disambiguationData":[TD([[makeQuery(id+"F0.imprint","IMPRINT",EDGE,{"disambiguationData":[TD([[subQ2,-1.0]])],"derivedFrom":subQ1}),1.0]])]});}
            var Q380;
            {var subQ0=sQuery(id+"F0.wireOp",EDGE,"E14.33.1");var subQ1=sQuery(id+"F0.wireOp",EDGE,"E14.25.0");var subQ2=makeQuery(id+"F0.imprint","INTERSECT",VERTEX,{"derivedFrom":[subQ1,subQ0]});Q380=makeQuery(id+"F0.imprint","IMPRINT",FACE,{"disambiguationData":[TD([[makeQuery(id+"F0.imprint","IMPRINT",EDGE,{"disambiguationData":[TD([[subQ2,-1.0]])],"derivedFrom":subQ1}),-1.0]])]});}
            var Q381;
            {var subQ0=sQuery(id+"F0.wireOp",EDGE,"E14.22.1");var subQ1=sQuery(id+"F0.wireOp",EDGE,"E14.14.0");var subQ2=makeQuery(id+"F0.imprint","INTERSECT",VERTEX,{"derivedFrom":[subQ1,subQ0]});Q381=makeQuery(id+"F0.imprint","IMPRINT",FACE,{"disambiguationData":[TD([[makeQuery(id+"F0.imprint","IMPRINT",EDGE,{"disambiguationData":[TD([[subQ2,-1.0]])],"derivedFrom":subQ1}),-1.0]])]});}
            var Q382;
            {var subQ0=sQuery(id+"F0.wireOp",EDGE,"E14.27.1");var subQ1=sQuery(id+"F0.wireOp",EDGE,"E14.19.0");var subQ2=makeQuery(id+"F0.imprint","INTERSECT",VERTEX,{"derivedFrom":[subQ1,subQ0]});Q382=makeQuery(id+"F0.imprint","IMPRINT",FACE,{"disambiguationData":[TD([[makeQuery(id+"F0.imprint","IMPRINT",EDGE,{"disambiguationData":[TD([[subQ2,-1.0]])],"derivedFrom":subQ1}),-1.0]])]});}
            var Q383;
            {var subQ0=sQuery(id+"F0.wireOp",EDGE,"E14.9.1");var subQ1=sQuery(id+"F0.wireOp",EDGE,"E14.2.0");var subQ2=makeQuery(id+"F0.imprint","INTERSECT",VERTEX,{"derivedFrom":[subQ1,subQ0]});Q383=makeQuery(id+"F0.imprint","IMPRINT",FACE,{"disambiguationData":[TD([[makeQuery(id+"F0.imprint","IMPRINT",EDGE,{"disambiguationData":[TD([[subQ2,-1.0]])],"derivedFrom":subQ1}),-1.0]])]});}
            var Q384;
            {var subQ0=sQuery(id+"F0.wireOp",EDGE,"E14.30.0");var subQ1=sQuery(id+"F0.wireOp",EDGE,"E9.left");var subQ2=makeQuery(id+"F0.imprint","INTERSECT",VERTEX,{"derivedFrom":[subQ1,subQ0]});Q384=makeQuery(id+"F0.imprint","IMPRINT",FACE,{"disambiguationData":[TD([[makeQuery(id+"F0.imprint","IMPRINT",EDGE,{"disambiguationData":[TD([[subQ2,-1.0]])],"derivedFrom":subQ1}),-1.0]])]});}
            var Q385;
            {var subQ0=sQuery(id+"F0.wireOp",EDGE,"E14.25.1");var subQ1=sQuery(id+"F0.wireOp",EDGE,"E14.17.0");var subQ2=makeQuery(id+"F0.imprint","INTERSECT",VERTEX,{"derivedFrom":[subQ1,subQ0]});Q385=makeQuery(id+"F0.imprint","IMPRINT",FACE,{"disambiguationData":[TD([[makeQuery(id+"F0.imprint","IMPRINT",EDGE,{"disambiguationData":[TD([[subQ2,-1.0]])],"derivedFrom":subQ1}),-1.0]])]});}
            var Q386;
            {var subQ0=sQuery(id+"F0.wireOp",EDGE,"E14.14.1");var subQ1=sQuery(id+"F0.wireOp",EDGE,"E14.6.0");var subQ2=makeQuery(id+"F0.imprint","INTERSECT",VERTEX,{"derivedFrom":[subQ1,subQ0]});Q386=makeQuery(id+"F0.imprint","IMPRINT",FACE,{"disambiguationData":[TD([[makeQuery(id+"F0.imprint","IMPRINT",EDGE,{"disambiguationData":[TD([[subQ2,-1.0]])],"derivedFrom":subQ1}),-1.0]])]});}
            var Q387;
            {var subQ0=sQuery(id+"F0.wireOp",EDGE,"E14.32.1");var subQ1=sQuery(id+"F0.wireOp",EDGE,"E14.24.0");var subQ2=makeQuery(id+"F0.imprint","INTERSECT",VERTEX,{"derivedFrom":[subQ1,subQ0]});Q387=makeQuery(id+"F0.imprint","IMPRINT",FACE,{"disambiguationData":[TD([[makeQuery(id+"F0.imprint","IMPRINT",EDGE,{"disambiguationData":[TD([[subQ2,-1.0]])],"derivedFrom":subQ1}),-1.0]])]});}
            var Q388;
            {var subQ0=sQuery(id+"F0.wireOp",EDGE,"E14.11.1");var subQ1=sQuery(id+"F0.wireOp",EDGE,"E14.3.0");var subQ2=makeQuery(id+"F0.imprint","INTERSECT",VERTEX,{"derivedFrom":[subQ1,subQ0]});Q388=makeQuery(id+"F0.imprint","IMPRINT",FACE,{"disambiguationData":[TD([[makeQuery(id+"F0.imprint","IMPRINT",EDGE,{"disambiguationData":[TD([[subQ2,-1.0]])],"derivedFrom":subQ1}),-1.0]])]});}
            var Q389;
            {var subQ0=sQuery(id+"F0.wireOp",EDGE,"E14.8.1");var subQ1=sQuery(id+"F0.wireOp",EDGE,"E9.right");var subQ2=makeQuery(id+"F0.imprint","INTERSECT",VERTEX,{"derivedFrom":[subQ1,subQ0]});Q389=makeQuery(id+"F0.imprint","IMPRINT",FACE,{"disambiguationData":[TD([[makeQuery(id+"F0.imprint","IMPRINT",EDGE,{"disambiguationData":[TD([[subQ2,-1.0]])],"derivedFrom":subQ1}),-1.0]])]});}
            var Q390;
            {var subQ0=sQuery(id+"F0.wireOp",EDGE,"E14.16.1");var subQ1=sQuery(id+"F0.wireOp",EDGE,"E14.8.0");var subQ2=makeQuery(id+"F0.imprint","INTERSECT",VERTEX,{"derivedFrom":[subQ1,subQ0]});Q390=makeQuery(id+"F0.imprint","IMPRINT",FACE,{"disambiguationData":[TD([[makeQuery(id+"F0.imprint","IMPRINT",EDGE,{"disambiguationData":[TD([[subQ2,-1.0]])],"derivedFrom":subQ1}),-1.0]])]});}
            var Q391;
            {var subQ0=sQuery(id+"F0.wireOp",EDGE,"E14.24.1");var subQ1=sQuery(id+"F0.wireOp",EDGE,"E14.16.0");var subQ2=makeQuery(id+"F0.imprint","INTERSECT",VERTEX,{"derivedFrom":[subQ1,subQ0]});Q391=makeQuery(id+"F0.imprint","IMPRINT",FACE,{"disambiguationData":[TD([[makeQuery(id+"F0.imprint","IMPRINT",EDGE,{"disambiguationData":[TD([[subQ2,-1.0]])],"derivedFrom":subQ1}),-1.0]])]});}
            var Q392;
            {var subQ0=sQuery(id+"F0.wireOp",EDGE,"E14.13.1");var subQ1=sQuery(id+"F0.wireOp",EDGE,"E14.5.0");var subQ2=makeQuery(id+"F0.imprint","INTERSECT",VERTEX,{"derivedFrom":[subQ1,subQ0]});Q392=makeQuery(id+"F0.imprint","IMPRINT",FACE,{"disambiguationData":[TD([[makeQuery(id+"F0.imprint","IMPRINT",EDGE,{"disambiguationData":[TD([[subQ2,-1.0]])],"derivedFrom":subQ1}),-1.0]])]});}
            var Q393;
            {var subQ0=sQuery(id+"F0.wireOp",EDGE,"E14.10.1");var subQ1=sQuery(id+"F0.wireOp",EDGE,"E14.2.0");var subQ2=makeQuery(id+"F0.imprint","INTERSECT",VERTEX,{"derivedFrom":[subQ1,subQ0]});Q393=makeQuery(id+"F0.imprint","IMPRINT",FACE,{"disambiguationData":[TD([[makeQuery(id+"F0.imprint","IMPRINT",EDGE,{"disambiguationData":[TD([[subQ2,-1.0]])],"derivedFrom":subQ1}),-1.0]])]});}
            var Q394;
            {var subQ0=sQuery(id+"F0.wireOp",EDGE,"E14.34.0");var subQ1=sQuery(id+"F0.wireOp",EDGE,"E14.5.1");var subQ2=makeQuery(id+"F0.imprint","INTERSECT",VERTEX,{"derivedFrom":[subQ1,subQ0]});Q394=makeQuery(id+"F0.imprint","IMPRINT",FACE,{"disambiguationData":[TD([[makeQuery(id+"F0.imprint","IMPRINT",EDGE,{"disambiguationData":[TD([[subQ2,-1.0]])],"derivedFrom":subQ1}),-1.0]])]});}
            var Q395;
            {var subQ0=sQuery(id+"F0.wireOp",EDGE,"E14.29.0");var subQ1=sQuery(id+"F0.wireOp",EDGE,"E9.left");var subQ2=makeQuery(id+"F0.imprint","INTERSECT",VERTEX,{"derivedFrom":[subQ1,subQ0]});Q395=makeQuery(id+"F0.imprint","IMPRINT",FACE,{"disambiguationData":[TD([[makeQuery(id+"F0.imprint","IMPRINT",EDGE,{"disambiguationData":[TD([[subQ2,-1.0]])],"derivedFrom":subQ1}),-1.0]])]});}
            var Q396;
            {var subQ0=sQuery(id+"F0.wireOp",EDGE,"E14.30.1");var subQ1=sQuery(id+"F0.wireOp",EDGE,"E14.21.0");var subQ2=makeQuery(id+"F0.imprint","INTERSECT",VERTEX,{"derivedFrom":[subQ1,subQ0]});Q396=makeQuery(id+"F0.imprint","IMPRINT",FACE,{"disambiguationData":[TD([[makeQuery(id+"F0.imprint","IMPRINT",EDGE,{"disambiguationData":[TD([[subQ2,-1.0]])],"derivedFrom":subQ1}),-1.0]])]});}
            var Q397;
            {var subQ0=sQuery(id+"F0.wireOp",EDGE,"E14.18.1");var subQ1=sQuery(id+"F0.wireOp",EDGE,"E14.11.0");var subQ2=makeQuery(id+"F0.imprint","INTERSECT",VERTEX,{"derivedFrom":[subQ1,subQ0]});Q397=makeQuery(id+"F0.imprint","IMPRINT",FACE,{"disambiguationData":[TD([[makeQuery(id+"F0.imprint","IMPRINT",EDGE,{"disambiguationData":[TD([[subQ2,-1.0]])],"derivedFrom":subQ1}),-1.0]])]});}
            var Q398;
            {var subQ0=sQuery(id+"F0.wireOp",EDGE,"E14.30.0");var subQ1=sQuery(id+"F0.wireOp",EDGE,"E14.2.1");var subQ2=makeQuery(id+"F0.imprint","INTERSECT",VERTEX,{"derivedFrom":[subQ1,subQ0]});Q398=makeQuery(id+"F0.imprint","IMPRINT",FACE,{"disambiguationData":[TD([[makeQuery(id+"F0.imprint","IMPRINT",EDGE,{"disambiguationData":[TD([[subQ2,-1.0]])],"derivedFrom":subQ1}),-1.0]])]});}
            var Q399;
            {var subQ0=sQuery(id+"F0.wireOp",EDGE,"E14.29.1");var subQ1=sQuery(id+"F0.wireOp",EDGE,"E14.21.0");var subQ2=makeQuery(id+"F0.imprint","INTERSECT",VERTEX,{"derivedFrom":[subQ1,subQ0]});Q399=makeQuery(id+"F0.imprint","IMPRINT",FACE,{"disambiguationData":[TD([[makeQuery(id+"F0.imprint","IMPRINT",EDGE,{"disambiguationData":[TD([[subQ2,-1.0]])],"derivedFrom":subQ1}),-1.0]])]});}
            var Q400;
            {var subQ0=sQuery(id+"F0.wireOp",EDGE,"E14.23.1");var subQ1=sQuery(id+"F0.wireOp",EDGE,"E14.14.0");var subQ2=makeQuery(id+"F0.imprint","INTERSECT",VERTEX,{"derivedFrom":[subQ1,subQ0]});Q400=makeQuery(id+"F0.imprint","IMPRINT",FACE,{"disambiguationData":[TD([[makeQuery(id+"F0.imprint","IMPRINT",EDGE,{"disambiguationData":[TD([[subQ2,-1.0]])],"derivedFrom":subQ1}),-1.0]])]});}
            var Q401;
            {var subQ0=sQuery(id+"F0.wireOp",EDGE,"E14.20.1");var subQ1=sQuery(id+"F0.wireOp",EDGE,"E14.12.0");var subQ2=makeQuery(id+"F0.imprint","INTERSECT",VERTEX,{"derivedFrom":[subQ1,subQ0]});Q401=makeQuery(id+"F0.imprint","IMPRINT",FACE,{"disambiguationData":[TD([[makeQuery(id+"F0.imprint","IMPRINT",EDGE,{"disambiguationData":[TD([[subQ2,-1.0]])],"derivedFrom":subQ1}),-1.0]])]});}
            var Q402;
            {var subQ0=sQuery(id+"F0.wireOp",EDGE,"E14.9.1");var subQ1=sQuery(id+"F0.wireOp",EDGE,"E14.1.0");var subQ2=makeQuery(id+"F0.imprint","INTERSECT",VERTEX,{"derivedFrom":[subQ1,subQ0]});Q402=makeQuery(id+"F0.imprint","IMPRINT",FACE,{"disambiguationData":[TD([[makeQuery(id+"F0.imprint","IMPRINT",EDGE,{"disambiguationData":[TD([[subQ2,-1.0]])],"derivedFrom":subQ1}),-1.0]])]});}
            var Q403;
            {var subQ0=sQuery(id+"F0.wireOp",EDGE,"E14.35.1");var subQ1=sQuery(id+"F0.wireOp",EDGE,"E14.27.0");var subQ2=makeQuery(id+"F0.imprint","INTERSECT",VERTEX,{"derivedFrom":[subQ1,subQ0]});Q403=makeQuery(id+"F0.imprint","IMPRINT",FACE,{"disambiguationData":[TD([[makeQuery(id+"F0.imprint","IMPRINT",EDGE,{"disambiguationData":[TD([[subQ2,-1.0]])],"derivedFrom":subQ1}),-1.0]])]});}
            var Q404;
            {var subQ0=sQuery(id+"F0.wireOp",EDGE,"E14.22.1");var subQ1=sQuery(id+"F0.wireOp",EDGE,"E14.13.0");var subQ2=makeQuery(id+"F0.imprint","INTERSECT",VERTEX,{"derivedFrom":[subQ1,subQ0]});Q404=makeQuery(id+"F0.imprint","IMPRINT",FACE,{"disambiguationData":[TD([[makeQuery(id+"F0.imprint","IMPRINT",EDGE,{"disambiguationData":[TD([[subQ2,-1.0]])],"derivedFrom":subQ1}),-1.0]])]});}
            var Q405;
            {var subQ0=sQuery(id+"F0.wireOp",EDGE,"E14.29.0");var subQ1=sQuery(id+"F0.wireOp",EDGE,"E14.1.1");var subQ2=makeQuery(id+"F0.imprint","INTERSECT",VERTEX,{"derivedFrom":[subQ1,subQ0]});Q405=makeQuery(id+"F0.imprint","IMPRINT",FACE,{"disambiguationData":[TD([[makeQuery(id+"F0.imprint","IMPRINT",EDGE,{"disambiguationData":[TD([[subQ2,-1.0]])],"derivedFrom":subQ1}),-1.0]])]});}
            var Q406;
            {var subQ0=sQuery(id+"F0.wireOp",EDGE,"E14.7.1");var subQ1=sQuery(id+"F0.wireOp",EDGE,"E9.right");var subQ2=makeQuery(id+"F0.imprint","INTERSECT",VERTEX,{"derivedFrom":[subQ1,subQ0]});Q406=makeQuery(id+"F0.imprint","IMPRINT",FACE,{"disambiguationData":[TD([[makeQuery(id+"F0.imprint","IMPRINT",EDGE,{"disambiguationData":[TD([[subQ2,-1.0]])],"derivedFrom":subQ1}),1.0]])]});}
            var Q407;
            {var subQ0=sQuery(id+"F0.wireOp",EDGE,"E14.21.1");var subQ1=sQuery(id+"F0.wireOp",EDGE,"E14.12.0");var subQ2=makeQuery(id+"F0.imprint","INTERSECT",VERTEX,{"derivedFrom":[subQ1,subQ0]});Q407=makeQuery(id+"F0.imprint","IMPRINT",FACE,{"disambiguationData":[TD([[makeQuery(id+"F0.imprint","IMPRINT",EDGE,{"disambiguationData":[TD([[subQ2,-1.0]])],"derivedFrom":subQ1}),-1.0]])]});}
            var Q408;
            {var subQ0=sQuery(id+"F0.wireOp",EDGE,"E14.13.1");var subQ1=sQuery(id+"F0.wireOp",EDGE,"E14.4.0");var subQ2=makeQuery(id+"F0.imprint","INTERSECT",VERTEX,{"derivedFrom":[subQ1,subQ0]});Q408=makeQuery(id+"F0.imprint","IMPRINT",FACE,{"disambiguationData":[TD([[makeQuery(id+"F0.imprint","IMPRINT",EDGE,{"disambiguationData":[TD([[subQ2,-1.0]])],"derivedFrom":subQ1}),-1.0]])]});}
            var Q409;
            {var subQ0=sQuery(id+"F0.wireOp",EDGE,"E14.14.1");var subQ1=sQuery(id+"F0.wireOp",EDGE,"E14.5.0");var subQ2=makeQuery(id+"F0.imprint","INTERSECT",VERTEX,{"derivedFrom":[subQ1,subQ0]});Q409=makeQuery(id+"F0.imprint","IMPRINT",FACE,{"disambiguationData":[TD([[makeQuery(id+"F0.imprint","IMPRINT",EDGE,{"disambiguationData":[TD([[subQ2,-1.0]])],"derivedFrom":subQ1}),-1.0]])]});}
            var Q410;
            {var subQ0=sQuery(id+"F0.wireOp",EDGE,"E14.31.1");var subQ1=sQuery(id+"F0.wireOp",EDGE,"E14.22.0");var subQ2=makeQuery(id+"F0.imprint","INTERSECT",VERTEX,{"derivedFrom":[subQ1,subQ0]});Q410=makeQuery(id+"F0.imprint","IMPRINT",FACE,{"disambiguationData":[TD([[makeQuery(id+"F0.imprint","IMPRINT",EDGE,{"disambiguationData":[TD([[subQ2,-1.0]])],"derivedFrom":subQ1}),-1.0]])]});}
            var Q411;
            {var subQ0=sQuery(id+"F0.wireOp",EDGE,"E14.29.1");var subQ1=sQuery(id+"F0.wireOp",EDGE,"E14.20.0");var subQ2=makeQuery(id+"F0.imprint","INTERSECT",VERTEX,{"derivedFrom":[subQ1,subQ0]});Q411=makeQuery(id+"F0.imprint","IMPRINT",FACE,{"disambiguationData":[TD([[makeQuery(id+"F0.imprint","IMPRINT",EDGE,{"disambiguationData":[TD([[subQ2,-1.0]])],"derivedFrom":subQ1}),-1.0]])]});}
            var Q412;
            {var subQ0=sQuery(id+"F0.wireOp",EDGE,"E14.17.1");var subQ1=sQuery(id+"F0.wireOp",EDGE,"E14.9.0");var subQ2=makeQuery(id+"F0.imprint","INTERSECT",VERTEX,{"derivedFrom":[subQ1,subQ0]});Q412=makeQuery(id+"F0.imprint","IMPRINT",FACE,{"disambiguationData":[TD([[makeQuery(id+"F0.imprint","IMPRINT",EDGE,{"disambiguationData":[TD([[subQ2,-1.0]])],"derivedFrom":subQ1}),-1.0]])]});}
            var Q413;
            {var subQ0=sQuery(id+"F0.wireOp",EDGE,"E14.19.1");var subQ1=sQuery(id+"F0.wireOp",EDGE,"E14.11.0");var subQ2=makeQuery(id+"F0.imprint","INTERSECT",VERTEX,{"derivedFrom":[subQ1,subQ0]});Q413=makeQuery(id+"F0.imprint","IMPRINT",FACE,{"disambiguationData":[TD([[makeQuery(id+"F0.imprint","IMPRINT",EDGE,{"disambiguationData":[TD([[subQ2,-1.0]])],"derivedFrom":subQ1}),-1.0]])]});}
            var Q414;
            {var subQ0=sQuery(id+"F0.wireOp",EDGE,"E14.11.1");var subQ1=sQuery(id+"F0.wireOp",EDGE,"E14.2.0");var subQ2=makeQuery(id+"F0.imprint","INTERSECT",VERTEX,{"derivedFrom":[subQ1,subQ0]});Q414=makeQuery(id+"F0.imprint","IMPRINT",FACE,{"disambiguationData":[TD([[makeQuery(id+"F0.imprint","IMPRINT",EDGE,{"disambiguationData":[TD([[subQ2,-1.0]])],"derivedFrom":subQ1}),-1.0]])]});}
            var Q415;
            {var subQ0=sQuery(id+"F0.wireOp",EDGE,"E14.12.1");var subQ1=sQuery(id+"F0.wireOp",EDGE,"E14.3.0");var subQ2=makeQuery(id+"F0.imprint","INTERSECT",VERTEX,{"derivedFrom":[subQ1,subQ0]});Q415=makeQuery(id+"F0.imprint","IMPRINT",FACE,{"disambiguationData":[TD([[makeQuery(id+"F0.imprint","IMPRINT",EDGE,{"disambiguationData":[TD([[subQ2,-1.0]])],"derivedFrom":subQ1}),-1.0]])]});}
            var Q416;
            {var subQ0=sQuery(id+"F0.wireOp",EDGE,"E14.18.1");var subQ1=sQuery(id+"F0.wireOp",EDGE,"E14.7.0");var subQ2=makeQuery(id+"F0.imprint","INTERSECT",VERTEX,{"derivedFrom":[subQ1,subQ0]});Q416=makeQuery(id+"F0.imprint","IMPRINT",FACE,{"disambiguationData":[TD([[makeQuery(id+"F0.imprint","IMPRINT",EDGE,{"disambiguationData":[TD([[subQ2,-1.0]])],"derivedFrom":subQ1}),-1.0]])]});}
            var Q417;
            {var subQ0=sQuery(id+"F0.wireOp",EDGE,"E14.34.0");var subQ1=sQuery(id+"F0.wireOp",EDGE,"E14.7.1");var subQ2=makeQuery(id+"F0.imprint","INTERSECT",VERTEX,{"derivedFrom":[subQ1,subQ0]});Q417=makeQuery(id+"F0.imprint","IMPRINT",FACE,{"disambiguationData":[TD([[makeQuery(id+"F0.imprint","IMPRINT",EDGE,{"disambiguationData":[TD([[subQ2,-1.0]])],"derivedFrom":subQ1}),-1.0]])]});}
            var Q418;
            {var subQ0=sQuery(id+"F0.wireOp",EDGE,"E14.18.1");var subQ1=sQuery(id+"F0.wireOp",EDGE,"E14.9.0");var subQ2=makeQuery(id+"F0.imprint","INTERSECT",VERTEX,{"derivedFrom":[subQ1,subQ0]});Q418=makeQuery(id+"F0.imprint","IMPRINT",FACE,{"disambiguationData":[TD([[makeQuery(id+"F0.imprint","IMPRINT",EDGE,{"disambiguationData":[TD([[subQ2,-1.0]])],"derivedFrom":subQ1}),-1.0]])]});}
            var Q419;
            {var subQ0=sQuery(id+"F0.wireOp",EDGE,"E14.20.1");var subQ1=sQuery(id+"F0.wireOp",EDGE,"E14.11.0");var subQ2=makeQuery(id+"F0.imprint","INTERSECT",VERTEX,{"derivedFrom":[subQ1,subQ0]});Q419=makeQuery(id+"F0.imprint","IMPRINT",FACE,{"disambiguationData":[TD([[makeQuery(id+"F0.imprint","IMPRINT",EDGE,{"disambiguationData":[TD([[subQ2,-1.0]])],"derivedFrom":subQ1}),-1.0]])]});}
            var Q420;
            {var subQ0=sQuery(id+"F0.wireOp",EDGE,"E14.9.1");var subQ1=sQuery(id+"F0.wireOp",EDGE,"E9.right");var subQ2=makeQuery(id+"F0.imprint","INTERSECT",VERTEX,{"derivedFrom":[subQ1,subQ0]});Q420=makeQuery(id+"F0.imprint","IMPRINT",FACE,{"disambiguationData":[TD([[makeQuery(id+"F0.imprint","IMPRINT",EDGE,{"disambiguationData":[TD([[subQ2,-1.0]])],"derivedFrom":subQ1}),-1.0]])]});}
            var Q421;
            {var subQ0=sQuery(id+"F0.wireOp",EDGE,"E14.34.1");var subQ1=sQuery(id+"F0.wireOp",EDGE,"E14.25.0");var subQ2=makeQuery(id+"F0.imprint","INTERSECT",VERTEX,{"derivedFrom":[subQ1,subQ0]});Q421=makeQuery(id+"F0.imprint","IMPRINT",FACE,{"disambiguationData":[TD([[makeQuery(id+"F0.imprint","IMPRINT",EDGE,{"disambiguationData":[TD([[subQ2,-1.0]])],"derivedFrom":subQ1}),-1.0]])]});}
            var Q422;
            {var subQ0=sQuery(id+"F0.wireOp",EDGE,"E14.16.1");var subQ1=sQuery(id+"F0.wireOp",EDGE,"E14.7.0");var subQ2=makeQuery(id+"F0.imprint","INTERSECT",VERTEX,{"derivedFrom":[subQ1,subQ0]});Q422=makeQuery(id+"F0.imprint","IMPRINT",FACE,{"disambiguationData":[TD([[makeQuery(id+"F0.imprint","IMPRINT",EDGE,{"disambiguationData":[TD([[subQ2,-1.0]])],"derivedFrom":subQ1}),-1.0]])]});}
            var Q423;
            {var subQ0=sQuery(id+"F0.wireOp",EDGE,"E14.34.0");var subQ1=sQuery(id+"F0.wireOp",EDGE,"E14.6.1");var subQ2=makeQuery(id+"F0.imprint","INTERSECT",VERTEX,{"derivedFrom":[subQ1,subQ0]});Q423=makeQuery(id+"F0.imprint","IMPRINT",FACE,{"disambiguationData":[TD([[makeQuery(id+"F0.imprint","IMPRINT",EDGE,{"disambiguationData":[TD([[subQ2,-1.0]])],"derivedFrom":subQ1}),-1.0]])]});}
            var Q424;
            {var subQ0=sQuery(id+"F0.wireOp",EDGE,"E14.27.1");var subQ1=sQuery(id+"F0.wireOp",EDGE,"E14.18.0");var subQ2=makeQuery(id+"F0.imprint","INTERSECT",VERTEX,{"derivedFrom":[subQ1,subQ0]});Q424=makeQuery(id+"F0.imprint","IMPRINT",FACE,{"disambiguationData":[TD([[makeQuery(id+"F0.imprint","IMPRINT",EDGE,{"disambiguationData":[TD([[subQ2,-1.0]])],"derivedFrom":subQ1}),-1.0]])]});}
            var Q425;
            {var subQ0=sQuery(id+"F0.wireOp",EDGE,"E14.17.1");var subQ1=sQuery(id+"F0.wireOp",EDGE,"E14.7.0");var subQ2=makeQuery(id+"F0.imprint","INTERSECT",VERTEX,{"derivedFrom":[subQ1,subQ0]});Q425=makeQuery(id+"F0.imprint","IMPRINT",FACE,{"disambiguationData":[TD([[makeQuery(id+"F0.imprint","IMPRINT",EDGE,{"disambiguationData":[TD([[subQ2,-1.0]])],"derivedFrom":subQ1}),-1.0]])]});}
            var Q426;
            {var subQ0=sQuery(id+"F0.wireOp",EDGE,"E14.33.0");var subQ1=sQuery(id+"F0.wireOp",EDGE,"E14.6.1");var subQ2=makeQuery(id+"F0.imprint","INTERSECT",VERTEX,{"derivedFrom":[subQ1,subQ0]});Q426=makeQuery(id+"F0.imprint","IMPRINT",FACE,{"disambiguationData":[TD([[makeQuery(id+"F0.imprint","IMPRINT",EDGE,{"disambiguationData":[TD([[subQ2,-1.0]])],"derivedFrom":subQ1}),-1.0]])]});}
            var Q427;
            {var subQ0=sQuery(id+"F0.wireOp",EDGE,"E14.20.1");var subQ1=sQuery(id+"F0.wireOp",EDGE,"E14.7.0");var subQ2=makeQuery(id+"F0.imprint","INTERSECT",VERTEX,{"derivedFrom":[subQ1,subQ0]});Q427=makeQuery(id+"F0.imprint","IMPRINT",FACE,{"disambiguationData":[TD([[makeQuery(id+"F0.imprint","IMPRINT",EDGE,{"disambiguationData":[TD([[subQ2,-1.0]])],"derivedFrom":subQ1}),-1.0]])]});}
            var Q428;
            {var subQ0=sQuery(id+"F0.wireOp",EDGE,"E14.32.0");var subQ1=sQuery(id+"F0.wireOp",EDGE,"E14.6.1");var subQ2=makeQuery(id+"F0.imprint","INTERSECT",VERTEX,{"derivedFrom":[subQ1,subQ0]});Q428=makeQuery(id+"F0.imprint","IMPRINT",FACE,{"disambiguationData":[TD([[makeQuery(id+"F0.imprint","IMPRINT",EDGE,{"disambiguationData":[TD([[subQ2,-1.0]])],"derivedFrom":subQ1}),-1.0]])]});}
            var Q429;
            {var subQ0=sQuery(id+"F0.wireOp",EDGE,"E14.35.1");var subQ1=sQuery(id+"F0.wireOp",EDGE,"E14.26.0");var subQ2=makeQuery(id+"F0.imprint","INTERSECT",VERTEX,{"derivedFrom":[subQ1,subQ0]});Q429=makeQuery(id+"F0.imprint","IMPRINT",FACE,{"disambiguationData":[TD([[makeQuery(id+"F0.imprint","IMPRINT",EDGE,{"disambiguationData":[TD([[subQ2,-1.0]])],"derivedFrom":subQ1}),-1.0]])]});}
            var Q430;
            {var subQ0=sQuery(id+"F0.wireOp",EDGE,"E14.26.1");var subQ1=sQuery(id+"F0.wireOp",EDGE,"E14.17.0");var subQ2=makeQuery(id+"F0.imprint","INTERSECT",VERTEX,{"derivedFrom":[subQ1,subQ0]});Q430=makeQuery(id+"F0.imprint","IMPRINT",FACE,{"disambiguationData":[TD([[makeQuery(id+"F0.imprint","IMPRINT",EDGE,{"disambiguationData":[TD([[subQ2,-1.0]])],"derivedFrom":subQ1}),-1.0]])]});}
            var Q431;
            {var subQ0=sQuery(id+"F0.wireOp",EDGE,"E14.34.0");var subQ1=sQuery(id+"F0.wireOp",EDGE,"E14.8.1");var subQ2=makeQuery(id+"F0.imprint","INTERSECT",VERTEX,{"derivedFrom":[subQ1,subQ0]});Q431=makeQuery(id+"F0.imprint","IMPRINT",FACE,{"disambiguationData":[TD([[makeQuery(id+"F0.imprint","IMPRINT",EDGE,{"disambiguationData":[TD([[subQ2,-1.0]])],"derivedFrom":subQ1}),-1.0]])]});}
            var Q432;
            {var subQ0=sQuery(id+"F0.wireOp",EDGE,"E14.19.1");var subQ1=sQuery(id+"F0.wireOp",EDGE,"E14.9.0");var subQ2=makeQuery(id+"F0.imprint","INTERSECT",VERTEX,{"derivedFrom":[subQ1,subQ0]});Q432=makeQuery(id+"F0.imprint","IMPRINT",FACE,{"disambiguationData":[TD([[makeQuery(id+"F0.imprint","IMPRINT",EDGE,{"disambiguationData":[TD([[subQ2,-1.0]])],"derivedFrom":subQ1}),-1.0]])]});}
            var Q433;
            {var subQ0=sQuery(id+"F0.wireOp",EDGE,"E14.25.1");var subQ1=sQuery(id+"F0.wireOp",EDGE,"E14.16.0");var subQ2=makeQuery(id+"F0.imprint","INTERSECT",VERTEX,{"derivedFrom":[subQ1,subQ0]});Q433=makeQuery(id+"F0.imprint","IMPRINT",FACE,{"disambiguationData":[TD([[makeQuery(id+"F0.imprint","IMPRINT",EDGE,{"disambiguationData":[TD([[subQ2,-1.0]])],"derivedFrom":subQ1}),-1.0]])]});}
            var Q434;
            {var subQ0=sQuery(id+"F0.wireOp",EDGE,"E14.19.1");var subQ1=sQuery(id+"F0.wireOp",EDGE,"E14.7.0");var subQ2=makeQuery(id+"F0.imprint","INTERSECT",VERTEX,{"derivedFrom":[subQ1,subQ0]});Q434=makeQuery(id+"F0.imprint","IMPRINT",FACE,{"disambiguationData":[TD([[makeQuery(id+"F0.imprint","IMPRINT",EDGE,{"disambiguationData":[TD([[subQ2,-1.0]])],"derivedFrom":subQ1}),-1.0]])]});}
            var Q435;
            {var subQ0=sQuery(id+"F0.wireOp",EDGE,"E14.19.1");var subQ1=sQuery(id+"F0.wireOp",EDGE,"E14.10.0");var subQ2=makeQuery(id+"F0.imprint","INTERSECT",VERTEX,{"derivedFrom":[subQ1,subQ0]});Q435=makeQuery(id+"F0.imprint","IMPRINT",FACE,{"disambiguationData":[TD([[makeQuery(id+"F0.imprint","IMPRINT",EDGE,{"disambiguationData":[TD([[subQ2,-1.0]])],"derivedFrom":subQ1}),-1.0]])]});}
            var Q436;
            {var subQ0=sQuery(id+"F0.wireOp",EDGE,"E14.32.0");var subQ1=sQuery(id+"F0.wireOp",EDGE,"E14.7.1");var subQ2=makeQuery(id+"F0.imprint","INTERSECT",VERTEX,{"derivedFrom":[subQ1,subQ0]});Q436=makeQuery(id+"F0.imprint","IMPRINT",FACE,{"disambiguationData":[TD([[makeQuery(id+"F0.imprint","IMPRINT",EDGE,{"disambiguationData":[TD([[subQ2,-1.0]])],"derivedFrom":subQ1}),-1.0]])]});}
            var Q437;
            {var subQ0=sQuery(id+"F0.wireOp",EDGE,"E14.27.0");var subQ1=sQuery(id+"F0.wireOp",EDGE,"E9.left");var subQ2=makeQuery(id+"F0.imprint","INTERSECT",VERTEX,{"derivedFrom":[subQ1,subQ0]});Q437=makeQuery(id+"F0.imprint","IMPRINT",FACE,{"disambiguationData":[TD([[makeQuery(id+"F0.imprint","IMPRINT",EDGE,{"disambiguationData":[TD([[subQ2,-1.0]])],"derivedFrom":subQ1}),1.0]])]});}
            var Q438;
            {var subQ0=sQuery(id+"F0.wireOp",EDGE,"E14.27.1");var subQ1=sQuery(id+"F0.wireOp",EDGE,"E14.17.0");var subQ2=makeQuery(id+"F0.imprint","INTERSECT",VERTEX,{"derivedFrom":[subQ1,subQ0]});Q438=makeQuery(id+"F0.imprint","IMPRINT",FACE,{"disambiguationData":[TD([[makeQuery(id+"F0.imprint","IMPRINT",EDGE,{"disambiguationData":[TD([[subQ2,-1.0]])],"derivedFrom":subQ1}),-1.0]])]});}
            var Q439;
            {var subQ0=sQuery(id+"F0.wireOp",EDGE,"E14.8.1");var subQ1=sQuery(id+"F0.wireOp",EDGE,"E9.right");var subQ2=makeQuery(id+"F0.imprint","INTERSECT",VERTEX,{"derivedFrom":[subQ1,subQ0]});Q439=makeQuery(id+"F0.imprint","IMPRINT",FACE,{"disambiguationData":[TD([[makeQuery(id+"F0.imprint","IMPRINT",EDGE,{"disambiguationData":[TD([[subQ2,-1.0]])],"derivedFrom":subQ1}),1.0]])]});}
            var Q440;
            {var subQ0=sQuery(id+"F0.wireOp",EDGE,"E14.18.1");var subQ1=sQuery(id+"F0.wireOp",EDGE,"E14.8.0");var subQ2=makeQuery(id+"F0.imprint","INTERSECT",VERTEX,{"derivedFrom":[subQ1,subQ0]});Q440=makeQuery(id+"F0.imprint","IMPRINT",FACE,{"disambiguationData":[TD([[makeQuery(id+"F0.imprint","IMPRINT",EDGE,{"disambiguationData":[TD([[subQ2,-1.0]])],"derivedFrom":subQ1}),-1.0]])]});}
            var Q441;
            {var subQ0=sQuery(id+"F0.wireOp",EDGE,"E14.33.0");var subQ1=sQuery(id+"F0.wireOp",EDGE,"E14.5.1");var subQ2=makeQuery(id+"F0.imprint","INTERSECT",VERTEX,{"derivedFrom":[subQ1,subQ0]});Q441=makeQuery(id+"F0.imprint","IMPRINT",FACE,{"disambiguationData":[TD([[makeQuery(id+"F0.imprint","IMPRINT",EDGE,{"disambiguationData":[TD([[subQ2,-1.0]])],"derivedFrom":subQ1}),-1.0]])]});}
            var Q442;
            {var subQ0=sQuery(id+"F0.wireOp",EDGE,"E14.35.1");var subQ1=sQuery(id+"F0.wireOp",EDGE,"E14.25.0");var subQ2=makeQuery(id+"F0.imprint","INTERSECT",VERTEX,{"derivedFrom":[subQ1,subQ0]});Q442=makeQuery(id+"F0.imprint","IMPRINT",FACE,{"disambiguationData":[TD([[makeQuery(id+"F0.imprint","IMPRINT",EDGE,{"disambiguationData":[TD([[subQ2,-1.0]])],"derivedFrom":subQ1}),-1.0]])]});}
            var Q443;
            {var subQ0=sQuery(id+"F0.wireOp",EDGE,"E14.20.1");var subQ1=sQuery(id+"F0.wireOp",EDGE,"E14.9.0");var subQ2=makeQuery(id+"F0.imprint","INTERSECT",VERTEX,{"derivedFrom":[subQ1,subQ0]});Q443=makeQuery(id+"F0.imprint","IMPRINT",FACE,{"disambiguationData":[TD([[makeQuery(id+"F0.imprint","IMPRINT",EDGE,{"disambiguationData":[TD([[subQ2,-1.0]])],"derivedFrom":subQ1}),-1.0]])]});}
            var Q444;
            {var subQ0=sQuery(id+"F0.wireOp",EDGE,"E14.35.1");var subQ1=sQuery(id+"F0.wireOp",EDGE,"E14.22.0");var subQ2=makeQuery(id+"F0.imprint","INTERSECT",VERTEX,{"derivedFrom":[subQ1,subQ0]});Q444=makeQuery(id+"F0.imprint","IMPRINT",FACE,{"disambiguationData":[TD([[makeQuery(id+"F0.imprint","IMPRINT",EDGE,{"disambiguationData":[TD([[subQ2,-1.0]])],"derivedFrom":subQ1}),-1.0]])]});}
            var Q445;
            {var subQ0=sQuery(id+"F0.wireOp",EDGE,"E14.33.1");var subQ1=sQuery(id+"F0.wireOp",EDGE,"E14.23.0");var subQ2=makeQuery(id+"F0.imprint","INTERSECT",VERTEX,{"derivedFrom":[subQ1,subQ0]});Q445=makeQuery(id+"F0.imprint","IMPRINT",FACE,{"disambiguationData":[TD([[makeQuery(id+"F0.imprint","IMPRINT",EDGE,{"disambiguationData":[TD([[subQ2,-1.0]])],"derivedFrom":subQ1}),-1.0]])]});}
            var Q446;
            {var subQ0=sQuery(id+"F0.wireOp",EDGE,"E14.34.0");var subQ1=sQuery(id+"F0.wireOp",EDGE,"E14.9.1");var subQ2=makeQuery(id+"F0.imprint","INTERSECT",VERTEX,{"derivedFrom":[subQ1,subQ0]});Q446=makeQuery(id+"F0.imprint","IMPRINT",FACE,{"disambiguationData":[TD([[makeQuery(id+"F0.imprint","IMPRINT",EDGE,{"disambiguationData":[TD([[subQ2,-1.0]])],"derivedFrom":subQ1}),-1.0]])]});}
            var Q447;
            {var subQ49=sQuery(id+"F0.wireOp",EDGE,"E9.bottom");Q447=makeQuery(id+"F0.imprint","IMPRINT",FACE,{"disambiguationData":[TD([[makeQuery(id+"F0.imprint","IMPRINT",EDGE,{"derivedFrom":subQ49}),1.0]])]});}
            var Q448;
            {var subQ0=sQuery(id+"F0.wireOp",EDGE,"E14.26.0");var subQ1=sQuery(id+"F0.wireOp",EDGE,"E9.left");var subQ2=makeQuery(id+"F0.imprint","INTERSECT",VERTEX,{"derivedFrom":[subQ1,subQ0]});Q448=makeQuery(id+"F0.imprint","IMPRINT",FACE,{"disambiguationData":[TD([[makeQuery(id+"F0.imprint","IMPRINT",EDGE,{"disambiguationData":[TD([[subQ2,-1.0]])],"derivedFrom":subQ1}),1.0]])]});}
            var Q449;
            {var subQ0=sQuery(id+"F0.wireOp",EDGE,"E14.32.0");var subQ1=sQuery(id+"F0.wireOp",EDGE,"E14.5.1");var subQ2=makeQuery(id+"F0.imprint","INTERSECT",VERTEX,{"derivedFrom":[subQ1,subQ0]});Q449=makeQuery(id+"F0.imprint","IMPRINT",FACE,{"disambiguationData":[TD([[makeQuery(id+"F0.imprint","IMPRINT",EDGE,{"disambiguationData":[TD([[subQ2,-1.0]])],"derivedFrom":subQ1}),-1.0]])]});}
            var Q450;
            {var subQ0=sQuery(id+"F0.wireOp",EDGE,"E14.26.1");var subQ1=sQuery(id+"F0.wireOp",EDGE,"E14.16.0");var subQ2=makeQuery(id+"F0.imprint","INTERSECT",VERTEX,{"derivedFrom":[subQ1,subQ0]});Q450=makeQuery(id+"F0.imprint","IMPRINT",FACE,{"disambiguationData":[TD([[makeQuery(id+"F0.imprint","IMPRINT",EDGE,{"disambiguationData":[TD([[subQ2,-1.0]])],"derivedFrom":subQ1}),-1.0]])]});}
            var Q451;
            {var subQ0=sQuery(id+"F0.wireOp",EDGE,"E14.20.1");var subQ1=sQuery(id+"F0.wireOp",EDGE,"E14.8.0");var subQ2=makeQuery(id+"F0.imprint","INTERSECT",VERTEX,{"derivedFrom":[subQ1,subQ0]});Q451=makeQuery(id+"F0.imprint","IMPRINT",FACE,{"disambiguationData":[TD([[makeQuery(id+"F0.imprint","IMPRINT",EDGE,{"disambiguationData":[TD([[subQ2,-1.0]])],"derivedFrom":subQ1}),-1.0]])]});}
            var Q452;
            {var subQ0=sQuery(id+"F0.wireOp",EDGE,"E14.10.1");var subQ1=sQuery(id+"F0.wireOp",EDGE,"E14.1.0");var subQ2=makeQuery(id+"F0.imprint","INTERSECT",VERTEX,{"derivedFrom":[subQ1,subQ0]});Q452=makeQuery(id+"F0.imprint","IMPRINT",FACE,{"disambiguationData":[TD([[makeQuery(id+"F0.imprint","IMPRINT",EDGE,{"disambiguationData":[TD([[subQ2,-1.0]])],"derivedFrom":subQ1}),-1.0]])]});}
            var Q453;
            {var subQ0=sQuery(id+"F0.wireOp",EDGE,"E14.17.1");var subQ1=sQuery(id+"F0.wireOp",EDGE,"E14.8.0");var subQ2=makeQuery(id+"F0.imprint","INTERSECT",VERTEX,{"derivedFrom":[subQ1,subQ0]});Q453=makeQuery(id+"F0.imprint","IMPRINT",FACE,{"disambiguationData":[TD([[makeQuery(id+"F0.imprint","IMPRINT",EDGE,{"disambiguationData":[TD([[subQ2,-1.0]])],"derivedFrom":subQ1}),-1.0]])]});}
            var Q454;
            {var subQ0=sQuery(id+"F0.wireOp",EDGE,"E14.32.0");var subQ1=sQuery(id+"F0.wireOp",EDGE,"E14.8.1");var subQ2=makeQuery(id+"F0.imprint","INTERSECT",VERTEX,{"derivedFrom":[subQ1,subQ0]});Q454=makeQuery(id+"F0.imprint","IMPRINT",FACE,{"disambiguationData":[TD([[makeQuery(id+"F0.imprint","IMPRINT",EDGE,{"disambiguationData":[TD([[subQ2,-1.0]])],"derivedFrom":subQ1}),-1.0]])]});}
            var Q455;
            {var subQ0=sQuery(id+"F0.wireOp",EDGE,"E14.9.1");var subQ1=sQuery(id+"F0.wireOp",EDGE,"E9.right");var subQ2=makeQuery(id+"F0.imprint","INTERSECT",VERTEX,{"derivedFrom":[subQ1,subQ0]});Q455=makeQuery(id+"F0.imprint","IMPRINT",FACE,{"disambiguationData":[TD([[makeQuery(id+"F0.imprint","IMPRINT",EDGE,{"disambiguationData":[TD([[subQ2,-1.0]])],"derivedFrom":subQ1}),1.0]])]});}
            var Q456;
            {var subQ0=sQuery(id+"F0.wireOp",EDGE,"E14.29.0");var subQ1=sQuery(id+"F0.wireOp",EDGE,"E14.2.1");var subQ2=makeQuery(id+"F0.imprint","INTERSECT",VERTEX,{"derivedFrom":[subQ1,subQ0]});Q456=makeQuery(id+"F0.imprint","IMPRINT",FACE,{"disambiguationData":[TD([[makeQuery(id+"F0.imprint","IMPRINT",EDGE,{"disambiguationData":[TD([[subQ2,-1.0]])],"derivedFrom":subQ1}),-1.0]])]});}
            var Q457;
            {var subQ0=sQuery(id+"F0.wireOp",EDGE,"E14.33.0");var subQ1=sQuery(id+"F0.wireOp",EDGE,"E14.8.1");var subQ2=makeQuery(id+"F0.imprint","INTERSECT",VERTEX,{"derivedFrom":[subQ1,subQ0]});Q457=makeQuery(id+"F0.imprint","IMPRINT",FACE,{"disambiguationData":[TD([[makeQuery(id+"F0.imprint","IMPRINT",EDGE,{"disambiguationData":[TD([[subQ2,-1.0]])],"derivedFrom":subQ1}),-1.0]])]});}
            var Q458;
            {var subQ0=sQuery(id+"F0.wireOp",EDGE,"E14.24.0");var subQ1=sQuery(id+"F0.wireOp",EDGE,"E14.5.1");var subQ2=makeQuery(id+"F0.imprint","INTERSECT",VERTEX,{"derivedFrom":[subQ1,subQ0]});Q458=makeQuery(id+"F0.imprint","IMPRINT",FACE,{"disambiguationData":[TD([[makeQuery(id+"F0.imprint","IMPRINT",EDGE,{"disambiguationData":[TD([[subQ2,-1.0]])],"derivedFrom":subQ1}),-1.0]])]});}
            var Q459;
            {var subQ0=sQuery(id+"F0.wireOp",EDGE,"E14.26.0");var subQ1=sQuery(id+"F0.wireOp",EDGE,"E14.2.1");var subQ2=makeQuery(id+"F0.imprint","INTERSECT",VERTEX,{"derivedFrom":[subQ1,subQ0]});Q459=makeQuery(id+"F0.imprint","IMPRINT",FACE,{"disambiguationData":[TD([[makeQuery(id+"F0.imprint","IMPRINT",EDGE,{"disambiguationData":[TD([[subQ2,-1.0]])],"derivedFrom":subQ1}),-1.0]])]});}
            var Q460;
            {var subQ0=sQuery(id+"F0.wireOp",EDGE,"E14.34.1");var subQ1=sQuery(id+"F0.wireOp",EDGE,"E14.24.0");var subQ2=makeQuery(id+"F0.imprint","INTERSECT",VERTEX,{"derivedFrom":[subQ1,subQ0]});Q460=makeQuery(id+"F0.imprint","IMPRINT",FACE,{"disambiguationData":[TD([[makeQuery(id+"F0.imprint","IMPRINT",EDGE,{"disambiguationData":[TD([[subQ2,-1.0]])],"derivedFrom":subQ1}),-1.0]])]});}
            var Q461;
            {var subQ0=sQuery(id+"F0.wireOp",EDGE,"E14.21.0");var subQ1=sQuery(id+"F0.wireOp",EDGE,"E14.2.1");var subQ2=makeQuery(id+"F0.imprint","INTERSECT",VERTEX,{"derivedFrom":[subQ1,subQ0]});Q461=makeQuery(id+"F0.imprint","IMPRINT",FACE,{"disambiguationData":[TD([[makeQuery(id+"F0.imprint","IMPRINT",EDGE,{"disambiguationData":[TD([[subQ2,-1.0]])],"derivedFrom":subQ1}),-1.0]])]});}
            var Q462;
            {var subQ0=sQuery(id+"F0.wireOp",EDGE,"E14.19.1");var subQ1=sQuery(id+"F0.wireOp",EDGE,"E14.8.0");var subQ2=makeQuery(id+"F0.imprint","INTERSECT",VERTEX,{"derivedFrom":[subQ1,subQ0]});Q462=makeQuery(id+"F0.imprint","IMPRINT",FACE,{"disambiguationData":[TD([[makeQuery(id+"F0.imprint","IMPRINT",EDGE,{"disambiguationData":[TD([[subQ2,-1.0]])],"derivedFrom":subQ1}),-1.0]])]});}
            var Q463;
            {var subQ0=sQuery(id+"F0.wireOp",EDGE,"E14.35.1");var subQ1=sQuery(id+"F0.wireOp",EDGE,"E14.23.0");var subQ2=makeQuery(id+"F0.imprint","INTERSECT",VERTEX,{"derivedFrom":[subQ1,subQ0]});Q463=makeQuery(id+"F0.imprint","IMPRINT",FACE,{"disambiguationData":[TD([[makeQuery(id+"F0.imprint","IMPRINT",EDGE,{"disambiguationData":[TD([[subQ2,-1.0]])],"derivedFrom":subQ1}),-1.0]])]});}
            var Q464;
            {var subQ0=sQuery(id+"F0.wireOp",EDGE,"E14.30.0");var subQ1=sQuery(id+"F0.wireOp",EDGE,"E14.4.1");var subQ2=makeQuery(id+"F0.imprint","INTERSECT",VERTEX,{"derivedFrom":[subQ1,subQ0]});Q464=makeQuery(id+"F0.imprint","IMPRINT",FACE,{"disambiguationData":[TD([[makeQuery(id+"F0.imprint","IMPRINT",EDGE,{"disambiguationData":[TD([[subQ2,-1.0]])],"derivedFrom":subQ1}),-1.0]])]});}
            var Q465;
            {var subQ0=sQuery(id+"F0.wireOp",EDGE,"E14.26.0");var subQ1=sQuery(id+"F0.wireOp",EDGE,"E14.7.1");var subQ2=makeQuery(id+"F0.imprint","INTERSECT",VERTEX,{"derivedFrom":[subQ1,subQ0]});Q465=makeQuery(id+"F0.imprint","IMPRINT",FACE,{"disambiguationData":[TD([[makeQuery(id+"F0.imprint","IMPRINT",EDGE,{"disambiguationData":[TD([[subQ2,-1.0]])],"derivedFrom":subQ1}),-1.0]])]});}
            var Q466;
            {var subQ0=sQuery(id+"F0.wireOp",EDGE,"E14.28.0");var subQ1=sQuery(id+"F0.wireOp",EDGE,"E14.9.1");var subQ2=makeQuery(id+"F0.imprint","INTERSECT",VERTEX,{"derivedFrom":[subQ1,subQ0]});Q466=makeQuery(id+"F0.imprint","IMPRINT",FACE,{"disambiguationData":[TD([[makeQuery(id+"F0.imprint","IMPRINT",EDGE,{"disambiguationData":[TD([[subQ2,-1.0]])],"derivedFrom":subQ1}),-1.0]])]});}
            var Q467;
            {var subQ0=sQuery(id+"F0.wireOp",EDGE,"E14.20.1");var subQ1=sQuery(id+"F0.wireOp",EDGE,"E14.10.0");var subQ2=makeQuery(id+"F0.imprint","INTERSECT",VERTEX,{"derivedFrom":[subQ1,subQ0]});Q467=makeQuery(id+"F0.imprint","IMPRINT",FACE,{"disambiguationData":[TD([[makeQuery(id+"F0.imprint","IMPRINT",EDGE,{"disambiguationData":[TD([[subQ2,-1.0]])],"derivedFrom":subQ1}),-1.0]])]});}
            var Q468;
            {var subQ0=sQuery(id+"F0.wireOp",EDGE,"E14.27.1");var subQ1=sQuery(id+"F0.wireOp",EDGE,"E14.16.0");var subQ2=makeQuery(id+"F0.imprint","INTERSECT",VERTEX,{"derivedFrom":[subQ1,subQ0]});Q468=makeQuery(id+"F0.imprint","IMPRINT",FACE,{"disambiguationData":[TD([[makeQuery(id+"F0.imprint","IMPRINT",EDGE,{"disambiguationData":[TD([[subQ2,-1.0]])],"derivedFrom":subQ1}),-1.0]])]});}
            var Q469;
            {var subQ0=sQuery(id+"F0.wireOp",EDGE,"E14.25.0");var subQ1=sQuery(id+"F0.wireOp",EDGE,"E9.left");var subQ2=makeQuery(id+"F0.imprint","INTERSECT",VERTEX,{"derivedFrom":[subQ1,subQ0]});Q469=makeQuery(id+"F0.imprint","IMPRINT",FACE,{"disambiguationData":[TD([[makeQuery(id+"F0.imprint","IMPRINT",EDGE,{"disambiguationData":[TD([[subQ2,-1.0]])],"derivedFrom":subQ1}),1.0]])]});}
            var Q470;
            {var subQ0=sQuery(id+"F0.wireOp",EDGE,"E14.29.0");var subQ1=sQuery(id+"F0.wireOp",EDGE,"E14.10.1");var subQ2=makeQuery(id+"F0.imprint","INTERSECT",VERTEX,{"derivedFrom":[subQ1,subQ0]});Q470=makeQuery(id+"F0.imprint","IMPRINT",FACE,{"disambiguationData":[TD([[makeQuery(id+"F0.imprint","IMPRINT",EDGE,{"disambiguationData":[TD([[subQ2,-1.0]])],"derivedFrom":subQ1}),-1.0]])]});}
            var Q471;
            {var subQ0=sQuery(id+"F0.wireOp",EDGE,"E14.30.0");var subQ1=sQuery(id+"F0.wireOp",EDGE,"E14.11.1");var subQ2=makeQuery(id+"F0.imprint","INTERSECT",VERTEX,{"derivedFrom":[subQ1,subQ0]});Q471=makeQuery(id+"F0.imprint","IMPRINT",FACE,{"disambiguationData":[TD([[makeQuery(id+"F0.imprint","IMPRINT",EDGE,{"disambiguationData":[TD([[subQ2,-1.0]])],"derivedFrom":subQ1}),-1.0]])]});}
            var Q472;
            {var subQ0=sQuery(id+"F0.wireOp",EDGE,"E14.28.0");var subQ1=sQuery(id+"F0.wireOp",EDGE,"E14.1.1");var subQ2=makeQuery(id+"F0.imprint","INTERSECT",VERTEX,{"derivedFrom":[subQ1,subQ0]});Q472=makeQuery(id+"F0.imprint","IMPRINT",FACE,{"disambiguationData":[TD([[makeQuery(id+"F0.imprint","IMPRINT",EDGE,{"disambiguationData":[TD([[subQ2,-1.0]])],"derivedFrom":subQ1}),-1.0]])]});}
            var Q473;
            {var subQ0=sQuery(id+"F0.wireOp",EDGE,"E14.11.1");var subQ1=sQuery(id+"F0.wireOp",EDGE,"E14.1.0");var subQ2=makeQuery(id+"F0.imprint","INTERSECT",VERTEX,{"derivedFrom":[subQ1,subQ0]});Q473=makeQuery(id+"F0.imprint","IMPRINT",FACE,{"disambiguationData":[TD([[makeQuery(id+"F0.imprint","IMPRINT",EDGE,{"disambiguationData":[TD([[subQ2,-1.0]])],"derivedFrom":subQ1}),-1.0]])]});}
            var Q474;
            {var subQ0=sQuery(id+"F0.wireOp",EDGE,"E14.10.1");var subQ1=sQuery(id+"F0.wireOp",EDGE,"E9.right");var subQ2=makeQuery(id+"F0.imprint","INTERSECT",VERTEX,{"derivedFrom":[subQ1,subQ0]});Q474=makeQuery(id+"F0.imprint","IMPRINT",FACE,{"disambiguationData":[TD([[makeQuery(id+"F0.imprint","IMPRINT",EDGE,{"disambiguationData":[TD([[subQ2,-1.0]])],"derivedFrom":subQ1}),1.0]])]});}
            var Q475;
            {var subQ0=sQuery(id+"F0.wireOp",EDGE,"E14.31.0");var subQ1=sQuery(id+"F0.wireOp",EDGE,"E14.5.1");var subQ2=makeQuery(id+"F0.imprint","INTERSECT",VERTEX,{"derivedFrom":[subQ1,subQ0]});Q475=makeQuery(id+"F0.imprint","IMPRINT",FACE,{"disambiguationData":[TD([[makeQuery(id+"F0.imprint","IMPRINT",EDGE,{"disambiguationData":[TD([[subQ2,-1.0]])],"derivedFrom":subQ1}),-1.0]])]});}
            var Q476;
            {var subQ0=sQuery(id+"F0.wireOp",EDGE,"E14.29.0");var subQ1=sQuery(id+"F0.wireOp",EDGE,"E14.4.1");var subQ2=makeQuery(id+"F0.imprint","INTERSECT",VERTEX,{"derivedFrom":[subQ1,subQ0]});Q476=makeQuery(id+"F0.imprint","IMPRINT",FACE,{"disambiguationData":[TD([[makeQuery(id+"F0.imprint","IMPRINT",EDGE,{"disambiguationData":[TD([[subQ2,-1.0]])],"derivedFrom":subQ1}),-1.0]])]});}
            var Q477;
            {var subQ0=sQuery(id+"F0.wireOp",EDGE,"E14.27.0");var subQ1=sQuery(id+"F0.wireOp",EDGE,"E14.5.1");var subQ2=makeQuery(id+"F0.imprint","INTERSECT",VERTEX,{"derivedFrom":[subQ1,subQ0]});Q477=makeQuery(id+"F0.imprint","IMPRINT",FACE,{"disambiguationData":[TD([[makeQuery(id+"F0.imprint","IMPRINT",EDGE,{"disambiguationData":[TD([[subQ2,-1.0]])],"derivedFrom":subQ1}),-1.0]])]});}
            var Q478;
            {var subQ0=sQuery(id+"F0.wireOp",EDGE,"E14.29.0");var subQ1=sQuery(id+"F0.wireOp",EDGE,"E14.9.1");var subQ2=makeQuery(id+"F0.imprint","INTERSECT",VERTEX,{"derivedFrom":[subQ1,subQ0]});Q478=makeQuery(id+"F0.imprint","IMPRINT",FACE,{"disambiguationData":[TD([[makeQuery(id+"F0.imprint","IMPRINT",EDGE,{"disambiguationData":[TD([[subQ2,-1.0]])],"derivedFrom":subQ1}),-1.0]])]});}
            var Q479;
            {var subQ0=sQuery(id+"F0.wireOp",EDGE,"E14.21.1");var subQ1=sQuery(id+"F0.wireOp",EDGE,"E14.7.0");var subQ2=makeQuery(id+"F0.imprint","INTERSECT",VERTEX,{"derivedFrom":[subQ1,subQ0]});Q479=makeQuery(id+"F0.imprint","IMPRINT",FACE,{"disambiguationData":[TD([[makeQuery(id+"F0.imprint","IMPRINT",EDGE,{"disambiguationData":[TD([[subQ2,-1.0]])],"derivedFrom":subQ1}),-1.0]])]});}
            var Q480;
            {var subQ0=sQuery(id+"F0.wireOp",EDGE,"E14.31.0");var subQ1=sQuery(id+"F0.wireOp",EDGE,"E14.9.1");var subQ2=makeQuery(id+"F0.imprint","INTERSECT",VERTEX,{"derivedFrom":[subQ1,subQ0]});Q480=makeQuery(id+"F0.imprint","IMPRINT",FACE,{"disambiguationData":[TD([[makeQuery(id+"F0.imprint","IMPRINT",EDGE,{"disambiguationData":[TD([[subQ2,-1.0]])],"derivedFrom":subQ1}),-1.0]])]});}
            var Q481;
            {var subQ0=sQuery(id+"F0.wireOp",EDGE,"E14.24.0");var subQ1=sQuery(id+"F0.wireOp",EDGE,"E14.1.1");var subQ2=makeQuery(id+"F0.imprint","INTERSECT",VERTEX,{"derivedFrom":[subQ1,subQ0]});Q481=makeQuery(id+"F0.imprint","IMPRINT",FACE,{"disambiguationData":[TD([[makeQuery(id+"F0.imprint","IMPRINT",EDGE,{"disambiguationData":[TD([[subQ2,-1.0]])],"derivedFrom":subQ1}),-1.0]])]});}
            var Q482;
            {var subQ0=sQuery(id+"F0.wireOp",EDGE,"E14.23.1");var subQ1=sQuery(id+"F0.wireOp",EDGE,"E14.13.0");var subQ2=makeQuery(id+"F0.imprint","INTERSECT",VERTEX,{"derivedFrom":[subQ1,subQ0]});Q482=makeQuery(id+"F0.imprint","IMPRINT",FACE,{"disambiguationData":[TD([[makeQuery(id+"F0.imprint","IMPRINT",EDGE,{"disambiguationData":[TD([[subQ2,-1.0]])],"derivedFrom":subQ1}),-1.0]])]});}
            var Q483;
            {var subQ0=sQuery(id+"F0.wireOp",EDGE,"E14.28.0");var subQ1=sQuery(id+"F0.wireOp",EDGE,"E14.2.1");var subQ2=makeQuery(id+"F0.imprint","INTERSECT",VERTEX,{"derivedFrom":[subQ1,subQ0]});Q483=makeQuery(id+"F0.imprint","IMPRINT",FACE,{"disambiguationData":[TD([[makeQuery(id+"F0.imprint","IMPRINT",EDGE,{"disambiguationData":[TD([[subQ2,-1.0]])],"derivedFrom":subQ1}),-1.0]])]});}
            var Q484;
            {var subQ0=sQuery(id+"F0.wireOp",EDGE,"E14.29.0");var subQ1=sQuery(id+"F0.wireOp",EDGE,"E14.6.1");var subQ2=makeQuery(id+"F0.imprint","INTERSECT",VERTEX,{"derivedFrom":[subQ1,subQ0]});Q484=makeQuery(id+"F0.imprint","IMPRINT",FACE,{"disambiguationData":[TD([[makeQuery(id+"F0.imprint","IMPRINT",EDGE,{"disambiguationData":[TD([[subQ2,-1.0]])],"derivedFrom":subQ1}),-1.0]])]});}
            var Q485;
            {var subQ0=sQuery(id+"F0.wireOp",EDGE,"E14.23.1");var subQ1=sQuery(id+"F0.wireOp",EDGE,"E14.11.0");var subQ2=makeQuery(id+"F0.imprint","INTERSECT",VERTEX,{"derivedFrom":[subQ1,subQ0]});Q485=makeQuery(id+"F0.imprint","IMPRINT",FACE,{"disambiguationData":[TD([[makeQuery(id+"F0.imprint","IMPRINT",EDGE,{"disambiguationData":[TD([[subQ2,-1.0]])],"derivedFrom":subQ1}),-1.0]])]});}
            var Q486;
            {var subQ0=sQuery(id+"F0.wireOp",EDGE,"E14.34.1");var subQ1=sQuery(id+"F0.wireOp",EDGE,"E14.23.0");var subQ2=makeQuery(id+"F0.imprint","INTERSECT",VERTEX,{"derivedFrom":[subQ1,subQ0]});Q486=makeQuery(id+"F0.imprint","IMPRINT",FACE,{"disambiguationData":[TD([[makeQuery(id+"F0.imprint","IMPRINT",EDGE,{"disambiguationData":[TD([[subQ2,-1.0]])],"derivedFrom":subQ1}),-1.0]])]});}
            var Q487;
            {var subQ0=sQuery(id+"F0.wireOp",EDGE,"E14.26.0");var subQ1=sQuery(id+"F0.wireOp",EDGE,"E14.6.1");var subQ2=makeQuery(id+"F0.imprint","INTERSECT",VERTEX,{"derivedFrom":[subQ1,subQ0]});Q487=makeQuery(id+"F0.imprint","IMPRINT",FACE,{"disambiguationData":[TD([[makeQuery(id+"F0.imprint","IMPRINT",EDGE,{"disambiguationData":[TD([[subQ2,-1.0]])],"derivedFrom":subQ1}),-1.0]])]});}
            var Q488;
            {var subQ0=sQuery(id+"F0.wireOp",EDGE,"E14.25.0");var subQ1=sQuery(id+"F0.wireOp",EDGE,"E14.2.1");var subQ2=makeQuery(id+"F0.imprint","INTERSECT",VERTEX,{"derivedFrom":[subQ1,subQ0]});Q488=makeQuery(id+"F0.imprint","IMPRINT",FACE,{"disambiguationData":[TD([[makeQuery(id+"F0.imprint","IMPRINT",EDGE,{"disambiguationData":[TD([[subQ2,-1.0]])],"derivedFrom":subQ1}),-1.0]])]});}
            var Q489;
            {var subQ0=sQuery(id+"F0.wireOp",EDGE,"E14.27.1");var subQ1=sQuery(id+"F0.wireOp",EDGE,"E14.14.0");var subQ2=makeQuery(id+"F0.imprint","INTERSECT",VERTEX,{"derivedFrom":[subQ1,subQ0]});Q489=makeQuery(id+"F0.imprint","IMPRINT",FACE,{"disambiguationData":[TD([[makeQuery(id+"F0.imprint","IMPRINT",EDGE,{"disambiguationData":[TD([[subQ2,-1.0]])],"derivedFrom":subQ1}),-1.0]])]});}
            var Q490;
            {var subQ0=sQuery(id+"F0.wireOp",EDGE,"E14.21.1");var subQ1=sQuery(id+"F0.wireOp",EDGE,"E14.10.0");var subQ2=makeQuery(id+"F0.imprint","INTERSECT",VERTEX,{"derivedFrom":[subQ1,subQ0]});Q490=makeQuery(id+"F0.imprint","IMPRINT",FACE,{"disambiguationData":[TD([[makeQuery(id+"F0.imprint","IMPRINT",EDGE,{"disambiguationData":[TD([[subQ2,-1.0]])],"derivedFrom":subQ1}),-1.0]])]});}
            var Q491;
            {var subQ0=sQuery(id+"F0.wireOp",EDGE,"E14.10.1");var subQ1=sQuery(id+"F0.wireOp",EDGE,"E9.right");var subQ2=makeQuery(id+"F0.imprint","INTERSECT",VERTEX,{"derivedFrom":[subQ1,subQ0]});Q491=makeQuery(id+"F0.imprint","IMPRINT",FACE,{"disambiguationData":[TD([[makeQuery(id+"F0.imprint","IMPRINT",EDGE,{"disambiguationData":[TD([[subQ2,-1.0]])],"derivedFrom":subQ1}),-1.0]])]});}
            var Q492;
            {var subQ0=sQuery(id+"F0.wireOp",EDGE,"E14.24.1");var subQ1=sQuery(id+"F0.wireOp",EDGE,"E14.14.0");var subQ2=makeQuery(id+"F0.imprint","INTERSECT",VERTEX,{"derivedFrom":[subQ1,subQ0]});Q492=makeQuery(id+"F0.imprint","IMPRINT",FACE,{"disambiguationData":[TD([[makeQuery(id+"F0.imprint","IMPRINT",EDGE,{"disambiguationData":[TD([[subQ2,-1.0]])],"derivedFrom":subQ1}),-1.0]])]});}
            var Q493;
            {var subQ0=sQuery(id+"F0.wireOp",EDGE,"E14.31.0");var subQ1=sQuery(id+"F0.wireOp",EDGE,"E14.4.1");var subQ2=makeQuery(id+"F0.imprint","INTERSECT",VERTEX,{"derivedFrom":[subQ1,subQ0]});Q493=makeQuery(id+"F0.imprint","IMPRINT",FACE,{"disambiguationData":[TD([[makeQuery(id+"F0.imprint","IMPRINT",EDGE,{"disambiguationData":[TD([[subQ2,-1.0]])],"derivedFrom":subQ1}),-1.0]])]});}
            var Q494;
            {var subQ0=sQuery(id+"F0.wireOp",EDGE,"E14.33.0");var subQ1=sQuery(id+"F0.wireOp",EDGE,"E14.7.1");var subQ2=makeQuery(id+"F0.imprint","INTERSECT",VERTEX,{"derivedFrom":[subQ1,subQ0]});Q494=makeQuery(id+"F0.imprint","IMPRINT",FACE,{"disambiguationData":[TD([[makeQuery(id+"F0.imprint","IMPRINT",EDGE,{"disambiguationData":[TD([[subQ2,-1.0]])],"derivedFrom":subQ1}),-1.0]])]});}
            var Q495;
            {var subQ0=sQuery(id+"F0.wireOp",EDGE,"E14.28.0");var subQ1=sQuery(id+"F0.wireOp",EDGE,"E9.left");var subQ2=makeQuery(id+"F0.imprint","INTERSECT",VERTEX,{"derivedFrom":[subQ1,subQ0]});Q495=makeQuery(id+"F0.imprint","IMPRINT",FACE,{"disambiguationData":[TD([[makeQuery(id+"F0.imprint","IMPRINT",EDGE,{"disambiguationData":[TD([[subQ2,-1.0]])],"derivedFrom":subQ1}),-1.0]])]});}
            var Q496;
            {var subQ0=sQuery(id+"F0.wireOp",EDGE,"E14.21.1");var subQ1=sQuery(id+"F0.wireOp",EDGE,"E14.11.0");var subQ2=makeQuery(id+"F0.imprint","INTERSECT",VERTEX,{"derivedFrom":[subQ1,subQ0]});Q496=makeQuery(id+"F0.imprint","IMPRINT",FACE,{"disambiguationData":[TD([[makeQuery(id+"F0.imprint","IMPRINT",EDGE,{"disambiguationData":[TD([[subQ2,-1.0]])],"derivedFrom":subQ1}),-1.0]])]});}
            var Q497;
            {var subQ0=sQuery(id+"F0.wireOp",EDGE,"E14.30.0");var subQ1=sQuery(id+"F0.wireOp",EDGE,"E14.6.1");var subQ2=makeQuery(id+"F0.imprint","INTERSECT",VERTEX,{"derivedFrom":[subQ1,subQ0]});Q497=makeQuery(id+"F0.imprint","IMPRINT",FACE,{"disambiguationData":[TD([[makeQuery(id+"F0.imprint","IMPRINT",EDGE,{"disambiguationData":[TD([[subQ2,-1.0]])],"derivedFrom":subQ1}),-1.0]])]});}
            var Q498;
            {var subQ0=sQuery(id+"F0.wireOp",EDGE,"E14.28.0");var subQ1=sQuery(id+"F0.wireOp",EDGE,"E14.7.1");var subQ2=makeQuery(id+"F0.imprint","INTERSECT",VERTEX,{"derivedFrom":[subQ1,subQ0]});Q498=makeQuery(id+"F0.imprint","IMPRINT",FACE,{"disambiguationData":[TD([[makeQuery(id+"F0.imprint","IMPRINT",EDGE,{"disambiguationData":[TD([[subQ2,-1.0]])],"derivedFrom":subQ1}),-1.0]])]});}
            var Q499;
            {var subQ0=sQuery(id+"F0.wireOp",EDGE,"E14.25.1");var subQ1=sQuery(id+"F0.wireOp",EDGE,"E14.7.0");var subQ2=makeQuery(id+"F0.imprint","INTERSECT",VERTEX,{"derivedFrom":[subQ1,subQ0]});Q499=makeQuery(id+"F0.imprint","IMPRINT",FACE,{"disambiguationData":[TD([[makeQuery(id+"F0.imprint","IMPRINT",EDGE,{"disambiguationData":[TD([[subQ2,-1.0]])],"derivedFrom":subQ1}),-1.0]])]});}
            var Q500;
            {var subQ0=sQuery(id+"F0.wireOp",EDGE,"E14.26.0");var subQ1=sQuery(id+"F0.wireOp",EDGE,"E14.5.1");var subQ2=makeQuery(id+"F0.imprint","INTERSECT",VERTEX,{"derivedFrom":[subQ1,subQ0]});Q500=makeQuery(id+"F0.imprint","IMPRINT",FACE,{"disambiguationData":[TD([[makeQuery(id+"F0.imprint","IMPRINT",EDGE,{"disambiguationData":[TD([[subQ2,-1.0]])],"derivedFrom":subQ1}),-1.0]])]});}
            var Q501;
            {var subQ0=sQuery(id+"F0.wireOp",EDGE,"E14.24.1");var subQ1=sQuery(id+"F0.wireOp",EDGE,"E14.6.0");var subQ2=makeQuery(id+"F0.imprint","INTERSECT",VERTEX,{"derivedFrom":[subQ1,subQ0]});Q501=makeQuery(id+"F0.imprint","IMPRINT",FACE,{"disambiguationData":[TD([[makeQuery(id+"F0.imprint","IMPRINT",EDGE,{"disambiguationData":[TD([[subQ2,-1.0]])],"derivedFrom":subQ1}),-1.0]])]});}
            var Q502;
            {var subQ0=sQuery(id+"F0.wireOp",EDGE,"E14.23.0");var subQ1=sQuery(id+"F0.wireOp",EDGE,"E14.1.1");var subQ2=makeQuery(id+"F0.imprint","INTERSECT",VERTEX,{"derivedFrom":[subQ1,subQ0]});Q502=makeQuery(id+"F0.imprint","IMPRINT",FACE,{"disambiguationData":[TD([[makeQuery(id+"F0.imprint","IMPRINT",EDGE,{"disambiguationData":[TD([[subQ2,-1.0]])],"derivedFrom":subQ1}),-1.0]])]});}
            var Q503;
            {var subQ0=sQuery(id+"F0.wireOp",EDGE,"E14.31.0");var subQ1=sQuery(id+"F0.wireOp",EDGE,"E14.7.1");var subQ2=makeQuery(id+"F0.imprint","INTERSECT",VERTEX,{"derivedFrom":[subQ1,subQ0]});Q503=makeQuery(id+"F0.imprint","IMPRINT",FACE,{"disambiguationData":[TD([[makeQuery(id+"F0.imprint","IMPRINT",EDGE,{"disambiguationData":[TD([[subQ2,-1.0]])],"derivedFrom":subQ1}),-1.0]])]});}
            var Q504;
            {var subQ0=sQuery(id+"F0.wireOp",EDGE,"E14.22.1");var subQ1=sQuery(id+"F0.wireOp",EDGE,"E14.11.0");var subQ2=makeQuery(id+"F0.imprint","INTERSECT",VERTEX,{"derivedFrom":[subQ1,subQ0]});Q504=makeQuery(id+"F0.imprint","IMPRINT",FACE,{"disambiguationData":[TD([[makeQuery(id+"F0.imprint","IMPRINT",EDGE,{"disambiguationData":[TD([[subQ2,-1.0]])],"derivedFrom":subQ1}),-1.0]])]});}
            var Q505;
            {var subQ0=sQuery(id+"F0.wireOp",EDGE,"E14.30.0");var subQ1=sQuery(id+"F0.wireOp",EDGE,"E14.5.1");var subQ2=makeQuery(id+"F0.imprint","INTERSECT",VERTEX,{"derivedFrom":[subQ1,subQ0]});Q505=makeQuery(id+"F0.imprint","IMPRINT",FACE,{"disambiguationData":[TD([[makeQuery(id+"F0.imprint","IMPRINT",EDGE,{"disambiguationData":[TD([[subQ2,-1.0]])],"derivedFrom":subQ1}),-1.0]])]});}
            var Q506;
            {var subQ0=sQuery(id+"F0.wireOp",EDGE,"E14.21.1");var subQ1=sQuery(id+"F0.wireOp",EDGE,"E14.8.0");var subQ2=makeQuery(id+"F0.imprint","INTERSECT",VERTEX,{"derivedFrom":[subQ1,subQ0]});Q506=makeQuery(id+"F0.imprint","IMPRINT",FACE,{"disambiguationData":[TD([[makeQuery(id+"F0.imprint","IMPRINT",EDGE,{"disambiguationData":[TD([[subQ2,-1.0]])],"derivedFrom":subQ1}),-1.0]])]});}
            var Q507;
            {var subQ0=sQuery(id+"F0.wireOp",EDGE,"E14.11.1");var subQ1=sQuery(id+"F0.wireOp",EDGE,"E9.right");var subQ2=makeQuery(id+"F0.imprint","INTERSECT",VERTEX,{"derivedFrom":[subQ1,subQ0]});Q507=makeQuery(id+"F0.imprint","IMPRINT",FACE,{"disambiguationData":[TD([[makeQuery(id+"F0.imprint","IMPRINT",EDGE,{"disambiguationData":[TD([[subQ2,-1.0]])],"derivedFrom":subQ1}),-1.0]])]});}
            var Q508;
            {var subQ0=sQuery(id+"F0.wireOp",EDGE,"E14.27.0");var subQ1=sQuery(id+"F0.wireOp",EDGE,"E9.left");var subQ2=makeQuery(id+"F0.imprint","INTERSECT",VERTEX,{"derivedFrom":[subQ1,subQ0]});Q508=makeQuery(id+"F0.imprint","IMPRINT",FACE,{"disambiguationData":[TD([[makeQuery(id+"F0.imprint","IMPRINT",EDGE,{"disambiguationData":[TD([[subQ2,-1.0]])],"derivedFrom":subQ1}),-1.0]])]});}
            var Q509;
            {var subQ0=sQuery(id+"F0.wireOp",EDGE,"E14.27.1");var subQ1=sQuery(id+"F0.wireOp",EDGE,"E14.9.0");var subQ2=makeQuery(id+"F0.imprint","INTERSECT",VERTEX,{"derivedFrom":[subQ1,subQ0]});Q509=makeQuery(id+"F0.imprint","IMPRINT",FACE,{"disambiguationData":[TD([[makeQuery(id+"F0.imprint","IMPRINT",EDGE,{"disambiguationData":[TD([[subQ2,-1.0]])],"derivedFrom":subQ1}),-1.0]])]});}
            var Q510;
            {var subQ0=sQuery(id+"F0.wireOp",EDGE,"E14.25.1");var subQ1=sQuery(id+"F0.wireOp",EDGE,"E14.15.0");var subQ2=makeQuery(id+"F0.imprint","INTERSECT",VERTEX,{"derivedFrom":[subQ1,subQ0]});Q510=makeQuery(id+"F0.imprint","IMPRINT",FACE,{"disambiguationData":[TD([[makeQuery(id+"F0.imprint","IMPRINT",EDGE,{"disambiguationData":[TD([[subQ2,-1.0]])],"derivedFrom":subQ1}),-1.0]])]});}
            var Q511;
            {var subQ0=sQuery(id+"F0.wireOp",EDGE,"E14.24.0");var subQ1=sQuery(id+"F0.wireOp",EDGE,"E9.left");var subQ2=makeQuery(id+"F0.imprint","INTERSECT",VERTEX,{"derivedFrom":[subQ1,subQ0]});Q511=makeQuery(id+"F0.imprint","IMPRINT",FACE,{"disambiguationData":[TD([[makeQuery(id+"F0.imprint","IMPRINT",EDGE,{"disambiguationData":[TD([[subQ2,-1.0]])],"derivedFrom":subQ1}),1.0]])]});}
            var Q512;
            {var subQ0=sQuery(id+"F0.wireOp",EDGE,"E14.25.0");var subQ1=sQuery(id+"F0.wireOp",EDGE,"E14.1.1");var subQ2=makeQuery(id+"F0.imprint","INTERSECT",VERTEX,{"derivedFrom":[subQ1,subQ0]});Q512=makeQuery(id+"F0.imprint","IMPRINT",FACE,{"disambiguationData":[TD([[makeQuery(id+"F0.imprint","IMPRINT",EDGE,{"disambiguationData":[TD([[subQ2,-1.0]])],"derivedFrom":subQ1}),-1.0]])]});}
            var Q513;
            {var subQ0=sQuery(id+"F0.wireOp",EDGE,"E14.30.0");var subQ1=sQuery(id+"F0.wireOp",EDGE,"E14.9.1");var subQ2=makeQuery(id+"F0.imprint","INTERSECT",VERTEX,{"derivedFrom":[subQ1,subQ0]});Q513=makeQuery(id+"F0.imprint","IMPRINT",FACE,{"disambiguationData":[TD([[makeQuery(id+"F0.imprint","IMPRINT",EDGE,{"disambiguationData":[TD([[subQ2,-1.0]])],"derivedFrom":subQ1}),-1.0]])]});}
            var Q514;
            {var subQ0=sQuery(id+"F0.wireOp",EDGE,"E14.29.0");var subQ1=sQuery(id+"F0.wireOp",EDGE,"E14.3.1");var subQ2=makeQuery(id+"F0.imprint","INTERSECT",VERTEX,{"derivedFrom":[subQ1,subQ0]});Q514=makeQuery(id+"F0.imprint","IMPRINT",FACE,{"disambiguationData":[TD([[makeQuery(id+"F0.imprint","IMPRINT",EDGE,{"disambiguationData":[TD([[subQ2,-1.0]])],"derivedFrom":subQ1}),-1.0]])]});}
            var Q515;
            {var subQ0=sQuery(id+"F0.wireOp",EDGE,"E14.33.0");var subQ1=sQuery(id+"F0.wireOp",EDGE,"E14.9.1");var subQ2=makeQuery(id+"F0.imprint","INTERSECT",VERTEX,{"derivedFrom":[subQ1,subQ0]});Q515=makeQuery(id+"F0.imprint","IMPRINT",FACE,{"disambiguationData":[TD([[makeQuery(id+"F0.imprint","IMPRINT",EDGE,{"disambiguationData":[TD([[subQ2,-1.0]])],"derivedFrom":subQ1}),-1.0]])]});}
            var Q516;
            {var subQ0=sQuery(id+"F0.wireOp",EDGE,"E14.30.0");var subQ1=sQuery(id+"F0.wireOp",EDGE,"E14.3.1");var subQ2=makeQuery(id+"F0.imprint","INTERSECT",VERTEX,{"derivedFrom":[subQ1,subQ0]});Q516=makeQuery(id+"F0.imprint","IMPRINT",FACE,{"disambiguationData":[TD([[makeQuery(id+"F0.imprint","IMPRINT",EDGE,{"disambiguationData":[TD([[subQ2,-1.0]])],"derivedFrom":subQ1}),-1.0]])]});}
            var Q517;
            {var subQ0=sQuery(id+"F0.wireOp",EDGE,"E14.26.1");var subQ1=sQuery(id+"F0.wireOp",EDGE,"E14.14.0");var subQ2=makeQuery(id+"F0.imprint","INTERSECT",VERTEX,{"derivedFrom":[subQ1,subQ0]});Q517=makeQuery(id+"F0.imprint","IMPRINT",FACE,{"disambiguationData":[TD([[makeQuery(id+"F0.imprint","IMPRINT",EDGE,{"disambiguationData":[TD([[subQ2,-1.0]])],"derivedFrom":subQ1}),-1.0]])]});}
            var Q518;
            {var subQ0=sQuery(id+"F0.wireOp",EDGE,"E14.24.1");var subQ1=sQuery(id+"F0.wireOp",EDGE,"E14.13.0");var subQ2=makeQuery(id+"F0.imprint","INTERSECT",VERTEX,{"derivedFrom":[subQ1,subQ0]});Q518=makeQuery(id+"F0.imprint","IMPRINT",FACE,{"disambiguationData":[TD([[makeQuery(id+"F0.imprint","IMPRINT",EDGE,{"disambiguationData":[TD([[subQ2,-1.0]])],"derivedFrom":subQ1}),-1.0]])]});}
            var Q519;
            {var subQ0=sQuery(id+"F0.wireOp",EDGE,"E14.28.0");var subQ1=sQuery(id+"F0.wireOp",EDGE,"E14.3.1");var subQ2=makeQuery(id+"F0.imprint","INTERSECT",VERTEX,{"derivedFrom":[subQ1,subQ0]});Q519=makeQuery(id+"F0.imprint","IMPRINT",FACE,{"disambiguationData":[TD([[makeQuery(id+"F0.imprint","IMPRINT",EDGE,{"disambiguationData":[TD([[subQ2,-1.0]])],"derivedFrom":subQ1}),-1.0]])]});}
            var Q520;
            {var subQ0=sQuery(id+"F0.wireOp",EDGE,"E14.31.0");var subQ1=sQuery(id+"F0.wireOp",EDGE,"E14.6.1");var subQ2=makeQuery(id+"F0.imprint","INTERSECT",VERTEX,{"derivedFrom":[subQ1,subQ0]});Q520=makeQuery(id+"F0.imprint","IMPRINT",FACE,{"disambiguationData":[TD([[makeQuery(id+"F0.imprint","IMPRINT",EDGE,{"disambiguationData":[TD([[subQ2,-1.0]])],"derivedFrom":subQ1}),-1.0]])]});}
            var Q521;
            {var subQ0=sQuery(id+"F0.wireOp",EDGE,"E14.34.0");var subQ1=sQuery(id+"F0.wireOp",EDGE,"E14.10.1");var subQ2=makeQuery(id+"F0.imprint","INTERSECT",VERTEX,{"derivedFrom":[subQ1,subQ0]});Q521=makeQuery(id+"F0.imprint","IMPRINT",FACE,{"disambiguationData":[TD([[makeQuery(id+"F0.imprint","IMPRINT",EDGE,{"disambiguationData":[TD([[subQ2,-1.0]])],"derivedFrom":subQ1}),-1.0]])]});}
            var Q522;
            {var subQ0=sQuery(id+"F0.wireOp",EDGE,"E14.29.0");var subQ1=sQuery(id+"F0.wireOp",EDGE,"E14.5.1");var subQ2=makeQuery(id+"F0.imprint","INTERSECT",VERTEX,{"derivedFrom":[subQ1,subQ0]});Q522=makeQuery(id+"F0.imprint","IMPRINT",FACE,{"disambiguationData":[TD([[makeQuery(id+"F0.imprint","IMPRINT",EDGE,{"disambiguationData":[TD([[subQ2,-1.0]])],"derivedFrom":subQ1}),-1.0]])]});}
            var Q523;
            {var subQ0=sQuery(id+"F0.wireOp",EDGE,"E14.30.0");var subQ1=sQuery(id+"F0.wireOp",EDGE,"E14.10.1");var subQ2=makeQuery(id+"F0.imprint","INTERSECT",VERTEX,{"derivedFrom":[subQ1,subQ0]});Q523=makeQuery(id+"F0.imprint","IMPRINT",FACE,{"disambiguationData":[TD([[makeQuery(id+"F0.imprint","IMPRINT",EDGE,{"disambiguationData":[TD([[subQ2,-1.0]])],"derivedFrom":subQ1}),-1.0]])]});}
            var Q524;
            {var subQ0=sQuery(id+"F0.wireOp",EDGE,"E14.27.0");var subQ1=sQuery(id+"F0.wireOp",EDGE,"E14.1.1");var subQ2=makeQuery(id+"F0.imprint","INTERSECT",VERTEX,{"derivedFrom":[subQ1,subQ0]});Q524=makeQuery(id+"F0.imprint","IMPRINT",FACE,{"disambiguationData":[TD([[makeQuery(id+"F0.imprint","IMPRINT",EDGE,{"disambiguationData":[TD([[subQ2,-1.0]])],"derivedFrom":subQ1}),-1.0]])]});}
            var Q525;
            {var subQ0=sQuery(id+"F0.wireOp",EDGE,"E14.23.1");var subQ1=sQuery(id+"F0.wireOp",EDGE,"E14.12.0");var subQ2=makeQuery(id+"F0.imprint","INTERSECT",VERTEX,{"derivedFrom":[subQ1,subQ0]});Q525=makeQuery(id+"F0.imprint","IMPRINT",FACE,{"disambiguationData":[TD([[makeQuery(id+"F0.imprint","IMPRINT",EDGE,{"disambiguationData":[TD([[subQ2,-1.0]])],"derivedFrom":subQ1}),-1.0]])]});}
            var Q526;
            {var subQ0=sQuery(id+"F0.wireOp",EDGE,"E14.22.1");var subQ1=sQuery(id+"F0.wireOp",EDGE,"E14.10.0");var subQ2=makeQuery(id+"F0.imprint","INTERSECT",VERTEX,{"derivedFrom":[subQ1,subQ0]});Q526=makeQuery(id+"F0.imprint","IMPRINT",FACE,{"disambiguationData":[TD([[makeQuery(id+"F0.imprint","IMPRINT",EDGE,{"disambiguationData":[TD([[subQ2,-1.0]])],"derivedFrom":subQ1}),-1.0]])]});}
            var Q527;
            {var subQ0=sQuery(id+"F0.wireOp",EDGE,"E14.23.1");var subQ1=sQuery(id+"F0.wireOp",EDGE,"E14.7.0");var subQ2=makeQuery(id+"F0.imprint","INTERSECT",VERTEX,{"derivedFrom":[subQ1,subQ0]});Q527=makeQuery(id+"F0.imprint","IMPRINT",FACE,{"disambiguationData":[TD([[makeQuery(id+"F0.imprint","IMPRINT",EDGE,{"disambiguationData":[TD([[subQ2,-1.0]])],"derivedFrom":subQ1}),-1.0]])]});}
            var Q528;
            {var subQ0=sQuery(id+"F0.wireOp",EDGE,"E14.24.1");var subQ1=sQuery(id+"F0.wireOp",EDGE,"E14.15.0");var subQ2=makeQuery(id+"F0.imprint","INTERSECT",VERTEX,{"derivedFrom":[subQ1,subQ0]});Q528=makeQuery(id+"F0.imprint","IMPRINT",FACE,{"disambiguationData":[TD([[makeQuery(id+"F0.imprint","IMPRINT",EDGE,{"disambiguationData":[TD([[subQ2,-1.0]])],"derivedFrom":subQ1}),-1.0]])]});}
            var Q529;
            {var subQ0=sQuery(id+"F0.wireOp",EDGE,"E14.24.0");var subQ1=sQuery(id+"F0.wireOp",EDGE,"E9.left");var subQ2=makeQuery(id+"F0.imprint","INTERSECT",VERTEX,{"derivedFrom":[subQ1,subQ0]});Q529=makeQuery(id+"F0.imprint","IMPRINT",FACE,{"disambiguationData":[TD([[makeQuery(id+"F0.imprint","IMPRINT",EDGE,{"disambiguationData":[TD([[subQ2,-1.0]])],"derivedFrom":subQ1}),-1.0]])]});}
            var Q530;
            {var subQ0=sQuery(id+"F0.wireOp",EDGE,"E14.19.1");var subQ1=sQuery(id+"F0.wireOp",EDGE,"E14.6.0");var subQ2=makeQuery(id+"F0.imprint","INTERSECT",VERTEX,{"derivedFrom":[subQ1,subQ0]});Q530=makeQuery(id+"F0.imprint","IMPRINT",FACE,{"disambiguationData":[TD([[makeQuery(id+"F0.imprint","IMPRINT",EDGE,{"disambiguationData":[TD([[subQ2,-1.0]])],"derivedFrom":subQ1}),-1.0]])]});}
            var Q531;
            {var subQ0=sQuery(id+"F0.wireOp",EDGE,"E14.27.1");var subQ1=sQuery(id+"F0.wireOp",EDGE,"E14.10.0");var subQ2=makeQuery(id+"F0.imprint","INTERSECT",VERTEX,{"derivedFrom":[subQ1,subQ0]});Q531=makeQuery(id+"F0.imprint","IMPRINT",FACE,{"disambiguationData":[TD([[makeQuery(id+"F0.imprint","IMPRINT",EDGE,{"disambiguationData":[TD([[subQ2,-1.0]])],"derivedFrom":subQ1}),-1.0]])]});}
            var Q532;
            {var subQ0=sQuery(id+"F0.wireOp",EDGE,"E14.25.1");var subQ1=sQuery(id+"F0.wireOp",EDGE,"E14.8.0");var subQ2=makeQuery(id+"F0.imprint","INTERSECT",VERTEX,{"derivedFrom":[subQ1,subQ0]});Q532=makeQuery(id+"F0.imprint","IMPRINT",FACE,{"disambiguationData":[TD([[makeQuery(id+"F0.imprint","IMPRINT",EDGE,{"disambiguationData":[TD([[subQ2,-1.0]])],"derivedFrom":subQ1}),-1.0]])]});}
            var Q533;
            {var subQ0=sQuery(id+"F0.wireOp",EDGE,"E14.25.1");var subQ1=sQuery(id+"F0.wireOp",EDGE,"E14.14.0");var subQ2=makeQuery(id+"F0.imprint","INTERSECT",VERTEX,{"derivedFrom":[subQ1,subQ0]});Q533=makeQuery(id+"F0.imprint","IMPRINT",FACE,{"disambiguationData":[TD([[makeQuery(id+"F0.imprint","IMPRINT",EDGE,{"disambiguationData":[TD([[subQ2,-1.0]])],"derivedFrom":subQ1}),-1.0]])]});}
            var Q534;
            {var subQ0=sQuery(id+"F0.wireOp",EDGE,"E14.26.0");var subQ1=sQuery(id+"F0.wireOp",EDGE,"E9.left");var subQ2=makeQuery(id+"F0.imprint","INTERSECT",VERTEX,{"derivedFrom":[subQ1,subQ0]});Q534=makeQuery(id+"F0.imprint","IMPRINT",FACE,{"disambiguationData":[TD([[makeQuery(id+"F0.imprint","IMPRINT",EDGE,{"disambiguationData":[TD([[subQ2,-1.0]])],"derivedFrom":subQ1}),-1.0]])]});}
            var Q535;
            {var subQ0=sQuery(id+"F0.wireOp",EDGE,"E14.22.0");var subQ1=sQuery(id+"F0.wireOp",EDGE,"E14.1.1");var subQ2=makeQuery(id+"F0.imprint","INTERSECT",VERTEX,{"derivedFrom":[subQ1,subQ0]});Q535=makeQuery(id+"F0.imprint","IMPRINT",FACE,{"disambiguationData":[TD([[makeQuery(id+"F0.imprint","IMPRINT",EDGE,{"disambiguationData":[TD([[subQ2,-1.0]])],"derivedFrom":subQ1}),-1.0]])]});}
            var Q536;
            {var subQ0=sQuery(id+"F0.wireOp",EDGE,"E14.27.0");var subQ1=sQuery(id+"F0.wireOp",EDGE,"E14.4.1");var subQ2=makeQuery(id+"F0.imprint","INTERSECT",VERTEX,{"derivedFrom":[subQ1,subQ0]});Q536=makeQuery(id+"F0.imprint","IMPRINT",FACE,{"disambiguationData":[TD([[makeQuery(id+"F0.imprint","IMPRINT",EDGE,{"disambiguationData":[TD([[subQ2,-1.0]])],"derivedFrom":subQ1}),-1.0]])]});}
            var Q537;
            {var subQ0=sQuery(id+"F0.wireOp",EDGE,"E14.31.0");var subQ1=sQuery(id+"F0.wireOp",EDGE,"E14.8.1");var subQ2=makeQuery(id+"F0.imprint","INTERSECT",VERTEX,{"derivedFrom":[subQ1,subQ0]});Q537=makeQuery(id+"F0.imprint","IMPRINT",FACE,{"disambiguationData":[TD([[makeQuery(id+"F0.imprint","IMPRINT",EDGE,{"disambiguationData":[TD([[subQ2,-1.0]])],"derivedFrom":subQ1}),-1.0]])]});}
            var Q538;
            {var subQ0=sQuery(id+"F0.wireOp",EDGE,"E14.33.1");var subQ1=sQuery(id+"F0.wireOp",EDGE,"E14.22.0");var subQ2=makeQuery(id+"F0.imprint","INTERSECT",VERTEX,{"derivedFrom":[subQ1,subQ0]});Q538=makeQuery(id+"F0.imprint","IMPRINT",FACE,{"disambiguationData":[TD([[makeQuery(id+"F0.imprint","IMPRINT",EDGE,{"disambiguationData":[TD([[subQ2,-1.0]])],"derivedFrom":subQ1}),-1.0]])]});}
            var Q539;
            {var subQ0=sQuery(id+"F0.wireOp",EDGE,"E14.28.1");var subQ1=sQuery(id+"F0.wireOp",EDGE,"E14.18.0");var subQ2=makeQuery(id+"F0.imprint","INTERSECT",VERTEX,{"derivedFrom":[subQ1,subQ0]});Q539=makeQuery(id+"F0.imprint","IMPRINT",FACE,{"disambiguationData":[TD([[makeQuery(id+"F0.imprint","IMPRINT",EDGE,{"disambiguationData":[TD([[subQ2,-1.0]])],"derivedFrom":subQ1}),-1.0]])]});}
            var Q540;
            {var subQ0=sQuery(id+"F0.wireOp",EDGE,"E14.24.1");var subQ1=sQuery(id+"F0.wireOp",EDGE,"E14.8.0");var subQ2=makeQuery(id+"F0.imprint","INTERSECT",VERTEX,{"derivedFrom":[subQ1,subQ0]});Q540=makeQuery(id+"F0.imprint","IMPRINT",FACE,{"disambiguationData":[TD([[makeQuery(id+"F0.imprint","IMPRINT",EDGE,{"disambiguationData":[TD([[subQ2,-1.0]])],"derivedFrom":subQ1}),-1.0]])]});}
            var Q541;
            {var subQ0=sQuery(id+"F0.wireOp",EDGE,"E14.30.1");var subQ1=sQuery(id+"F0.wireOp",EDGE,"E14.17.0");var subQ2=makeQuery(id+"F0.imprint","INTERSECT",VERTEX,{"derivedFrom":[subQ1,subQ0]});Q541=makeQuery(id+"F0.imprint","IMPRINT",FACE,{"disambiguationData":[TD([[makeQuery(id+"F0.imprint","IMPRINT",EDGE,{"disambiguationData":[TD([[subQ2,-1.0]])],"derivedFrom":subQ1}),-1.0]])]});}
            var Q542;
            {var subQ0=sQuery(id+"F0.wireOp",EDGE,"E14.32.0");var subQ1=sQuery(id+"F0.wireOp",EDGE,"E14.9.1");var subQ2=makeQuery(id+"F0.imprint","INTERSECT",VERTEX,{"derivedFrom":[subQ1,subQ0]});Q542=makeQuery(id+"F0.imprint","IMPRINT",FACE,{"disambiguationData":[TD([[makeQuery(id+"F0.imprint","IMPRINT",EDGE,{"disambiguationData":[TD([[subQ2,-1.0]])],"derivedFrom":subQ1}),-1.0]])]});}
            var Q543;
            {var subQ0=sQuery(id+"F0.wireOp",EDGE,"E14.25.0");var subQ1=sQuery(id+"F0.wireOp",EDGE,"E9.left");var subQ2=makeQuery(id+"F0.imprint","INTERSECT",VERTEX,{"derivedFrom":[subQ1,subQ0]});Q543=makeQuery(id+"F0.imprint","IMPRINT",FACE,{"disambiguationData":[TD([[makeQuery(id+"F0.imprint","IMPRINT",EDGE,{"disambiguationData":[TD([[subQ2,-1.0]])],"derivedFrom":subQ1}),-1.0]])]});}
            var Q544;
            {var subQ0=sQuery(id+"F0.wireOp",EDGE,"E14.32.1");var subQ1=sQuery(id+"F0.wireOp",EDGE,"E14.18.0");var subQ2=makeQuery(id+"F0.imprint","INTERSECT",VERTEX,{"derivedFrom":[subQ1,subQ0]});Q544=makeQuery(id+"F0.imprint","IMPRINT",FACE,{"disambiguationData":[TD([[makeQuery(id+"F0.imprint","IMPRINT",EDGE,{"disambiguationData":[TD([[subQ2,-1.0]])],"derivedFrom":subQ1}),-1.0]])]});}
            var Q545;
            {var subQ0=sQuery(id+"F0.wireOp",EDGE,"E14.34.0");var subQ1=sQuery(id+"F0.wireOp",EDGE,"E14.12.1");var subQ2=makeQuery(id+"F0.imprint","INTERSECT",VERTEX,{"derivedFrom":[subQ1,subQ0]});Q545=makeQuery(id+"F0.imprint","IMPRINT",FACE,{"disambiguationData":[TD([[makeQuery(id+"F0.imprint","IMPRINT",EDGE,{"disambiguationData":[TD([[subQ2,-1.0]])],"derivedFrom":subQ1}),-1.0]])]});}
            var Q546;
            {var subQ0=sQuery(id+"F0.wireOp",EDGE,"E14.26.1");var subQ1=sQuery(id+"F0.wireOp",EDGE,"E14.10.0");var subQ2=makeQuery(id+"F0.imprint","INTERSECT",VERTEX,{"derivedFrom":[subQ1,subQ0]});Q546=makeQuery(id+"F0.imprint","IMPRINT",FACE,{"disambiguationData":[TD([[makeQuery(id+"F0.imprint","IMPRINT",EDGE,{"disambiguationData":[TD([[subQ2,-1.0]])],"derivedFrom":subQ1}),-1.0]])]});}
            var Q547;
            {var subQ0=sQuery(id+"F0.wireOp",EDGE,"E14.22.1");var subQ1=sQuery(id+"F0.wireOp",EDGE,"E14.7.0");var subQ2=makeQuery(id+"F0.imprint","INTERSECT",VERTEX,{"derivedFrom":[subQ1,subQ0]});Q547=makeQuery(id+"F0.imprint","IMPRINT",FACE,{"disambiguationData":[TD([[makeQuery(id+"F0.imprint","IMPRINT",EDGE,{"disambiguationData":[TD([[subQ2,-1.0]])],"derivedFrom":subQ1}),-1.0]])]});}
            var Q548;
            {var subQ0=sQuery(id+"F0.wireOp",EDGE,"E14.32.1");var subQ1=sQuery(id+"F0.wireOp",EDGE,"E14.20.0");var subQ2=makeQuery(id+"F0.imprint","INTERSECT",VERTEX,{"derivedFrom":[subQ1,subQ0]});Q548=makeQuery(id+"F0.imprint","IMPRINT",FACE,{"disambiguationData":[TD([[makeQuery(id+"F0.imprint","IMPRINT",EDGE,{"disambiguationData":[TD([[subQ2,-1.0]])],"derivedFrom":subQ1}),-1.0]])]});}
            var Q549;
            {var subQ0=sQuery(id+"F0.wireOp",EDGE,"E14.29.0");var subQ1=sQuery(id+"F0.wireOp",EDGE,"E14.7.1");var subQ2=makeQuery(id+"F0.imprint","INTERSECT",VERTEX,{"derivedFrom":[subQ1,subQ0]});Q549=makeQuery(id+"F0.imprint","IMPRINT",FACE,{"disambiguationData":[TD([[makeQuery(id+"F0.imprint","IMPRINT",EDGE,{"disambiguationData":[TD([[subQ2,-1.0]])],"derivedFrom":subQ1}),-1.0]])]});}
            var Q550;
            {var subQ0=sQuery(id+"F0.wireOp",EDGE,"E14.24.1");var subQ1=sQuery(id+"F0.wireOp",EDGE,"E14.12.0");var subQ2=makeQuery(id+"F0.imprint","INTERSECT",VERTEX,{"derivedFrom":[subQ1,subQ0]});Q550=makeQuery(id+"F0.imprint","IMPRINT",FACE,{"disambiguationData":[TD([[makeQuery(id+"F0.imprint","IMPRINT",EDGE,{"disambiguationData":[TD([[subQ2,-1.0]])],"derivedFrom":subQ1}),-1.0]])]});}
            var Q551;
            {var subQ0=sQuery(id+"F0.wireOp",EDGE,"E14.27.1");var subQ1=sQuery(id+"F0.wireOp",EDGE,"E14.15.0");var subQ2=makeQuery(id+"F0.imprint","INTERSECT",VERTEX,{"derivedFrom":[subQ1,subQ0]});Q551=makeQuery(id+"F0.imprint","IMPRINT",FACE,{"disambiguationData":[TD([[makeQuery(id+"F0.imprint","IMPRINT",EDGE,{"disambiguationData":[TD([[subQ2,-1.0]])],"derivedFrom":subQ1}),-1.0]])]});}
            var Q552;
            {var subQ0=sQuery(id+"F0.wireOp",EDGE,"E14.25.0");var subQ1=sQuery(id+"F0.wireOp",EDGE,"E14.4.1");var subQ2=makeQuery(id+"F0.imprint","INTERSECT",VERTEX,{"derivedFrom":[subQ1,subQ0]});Q552=makeQuery(id+"F0.imprint","IMPRINT",FACE,{"disambiguationData":[TD([[makeQuery(id+"F0.imprint","IMPRINT",EDGE,{"disambiguationData":[TD([[subQ2,-1.0]])],"derivedFrom":subQ1}),-1.0]])]});}
            var Q553;
            {var subQ0=sQuery(id+"F0.wireOp",EDGE,"E14.31.0");var subQ1=sQuery(id+"F0.wireOp",EDGE,"E14.10.1");var subQ2=makeQuery(id+"F0.imprint","INTERSECT",VERTEX,{"derivedFrom":[subQ1,subQ0]});Q553=makeQuery(id+"F0.imprint","IMPRINT",FACE,{"disambiguationData":[TD([[makeQuery(id+"F0.imprint","IMPRINT",EDGE,{"disambiguationData":[TD([[subQ2,-1.0]])],"derivedFrom":subQ1}),-1.0]])]});}
            var Q554;
            {var subQ0=sQuery(id+"F0.wireOp",EDGE,"E14.23.0");var subQ1=sQuery(id+"F0.wireOp",EDGE,"E9.left");var subQ2=makeQuery(id+"F0.imprint","INTERSECT",VERTEX,{"derivedFrom":[subQ1,subQ0]});Q554=makeQuery(id+"F0.imprint","IMPRINT",FACE,{"disambiguationData":[TD([[makeQuery(id+"F0.imprint","IMPRINT",EDGE,{"disambiguationData":[TD([[subQ2,-1.0]])],"derivedFrom":subQ1}),1.0]])]});}
            var Q555;
            {var subQ0=sQuery(id+"F0.wireOp",EDGE,"E14.21.0");var subQ1=sQuery(id+"F0.wireOp",EDGE,"E14.1.1");var subQ2=makeQuery(id+"F0.imprint","INTERSECT",VERTEX,{"derivedFrom":[subQ1,subQ0]});Q555=makeQuery(id+"F0.imprint","IMPRINT",FACE,{"disambiguationData":[TD([[makeQuery(id+"F0.imprint","IMPRINT",EDGE,{"disambiguationData":[TD([[subQ2,-1.0]])],"derivedFrom":subQ1}),-1.0]])]});}
            var Q556;
            {var subQ0=sQuery(id+"F0.wireOp",EDGE,"E14.22.1");var subQ1=sQuery(id+"F0.wireOp",EDGE,"E14.12.0");var subQ2=makeQuery(id+"F0.imprint","INTERSECT",VERTEX,{"derivedFrom":[subQ1,subQ0]});Q556=makeQuery(id+"F0.imprint","IMPRINT",FACE,{"disambiguationData":[TD([[makeQuery(id+"F0.imprint","IMPRINT",EDGE,{"disambiguationData":[TD([[subQ2,-1.0]])],"derivedFrom":subQ1}),-1.0]])]});}
            var Q557;
            {var subQ0=sQuery(id+"F0.wireOp",EDGE,"E14.30.1");var subQ1=sQuery(id+"F0.wireOp",EDGE,"E14.12.0");var subQ2=makeQuery(id+"F0.imprint","INTERSECT",VERTEX,{"derivedFrom":[subQ1,subQ0]});Q557=makeQuery(id+"F0.imprint","IMPRINT",FACE,{"disambiguationData":[TD([[makeQuery(id+"F0.imprint","IMPRINT",EDGE,{"disambiguationData":[TD([[subQ2,-1.0]])],"derivedFrom":subQ1}),-1.0]])]});}
            var Q558;
            {var subQ0=sQuery(id+"F0.wireOp",EDGE,"E14.20.1");var subQ1=sQuery(id+"F0.wireOp",EDGE,"E14.6.0");var subQ2=makeQuery(id+"F0.imprint","INTERSECT",VERTEX,{"derivedFrom":[subQ1,subQ0]});Q558=makeQuery(id+"F0.imprint","IMPRINT",FACE,{"disambiguationData":[TD([[makeQuery(id+"F0.imprint","IMPRINT",EDGE,{"disambiguationData":[TD([[subQ2,-1.0]])],"derivedFrom":subQ1}),-1.0]])]});}
            var Q559;
            {var subQ0=sQuery(id+"F0.wireOp",EDGE,"E14.35.1");var subQ1=sQuery(id+"F0.wireOp",EDGE,"E14.19.0");var subQ2=makeQuery(id+"F0.imprint","INTERSECT",VERTEX,{"derivedFrom":[subQ1,subQ0]});Q559=makeQuery(id+"F0.imprint","IMPRINT",FACE,{"disambiguationData":[TD([[makeQuery(id+"F0.imprint","IMPRINT",EDGE,{"disambiguationData":[TD([[subQ2,-1.0]])],"derivedFrom":subQ1}),-1.0]])]});}
            var Q560;
            {var subQ0=sQuery(id+"F0.wireOp",EDGE,"E14.30.1");var subQ1=sQuery(id+"F0.wireOp",EDGE,"E14.19.0");var subQ2=makeQuery(id+"F0.imprint","INTERSECT",VERTEX,{"derivedFrom":[subQ1,subQ0]});Q560=makeQuery(id+"F0.imprint","IMPRINT",FACE,{"disambiguationData":[TD([[makeQuery(id+"F0.imprint","IMPRINT",EDGE,{"disambiguationData":[TD([[subQ2,-1.0]])],"derivedFrom":subQ1}),-1.0]])]});}
            var Q561;
            {var subQ0=sQuery(id+"F0.wireOp",EDGE,"E14.28.0");var subQ1=sQuery(id+"F0.wireOp",EDGE,"E14.6.1");var subQ2=makeQuery(id+"F0.imprint","INTERSECT",VERTEX,{"derivedFrom":[subQ1,subQ0]});Q561=makeQuery(id+"F0.imprint","IMPRINT",FACE,{"disambiguationData":[TD([[makeQuery(id+"F0.imprint","IMPRINT",EDGE,{"disambiguationData":[TD([[subQ2,-1.0]])],"derivedFrom":subQ1}),-1.0]])]});}
            var Q562;
            {var subQ0=sQuery(id+"F0.wireOp",EDGE,"E14.23.1");var subQ1=sQuery(id+"F0.wireOp",EDGE,"E14.9.0");var subQ2=makeQuery(id+"F0.imprint","INTERSECT",VERTEX,{"derivedFrom":[subQ1,subQ0]});Q562=makeQuery(id+"F0.imprint","IMPRINT",FACE,{"disambiguationData":[TD([[makeQuery(id+"F0.imprint","IMPRINT",EDGE,{"disambiguationData":[TD([[subQ2,-1.0]])],"derivedFrom":subQ1}),-1.0]])]});}
            var Q563;
            {var subQ0=sQuery(id+"F0.wireOp",EDGE,"E14.35.1");var subQ1=sQuery(id+"F0.wireOp",EDGE,"E14.20.0");var subQ2=makeQuery(id+"F0.imprint","INTERSECT",VERTEX,{"derivedFrom":[subQ1,subQ0]});Q563=makeQuery(id+"F0.imprint","IMPRINT",FACE,{"disambiguationData":[TD([[makeQuery(id+"F0.imprint","IMPRINT",EDGE,{"disambiguationData":[TD([[subQ2,-1.0]])],"derivedFrom":subQ1}),-1.0]])]});}
            var Q564;
            {var subQ0=sQuery(id+"F0.wireOp",EDGE,"E14.32.1");var subQ1=sQuery(id+"F0.wireOp",EDGE,"E14.22.0");var subQ2=makeQuery(id+"F0.imprint","INTERSECT",VERTEX,{"derivedFrom":[subQ1,subQ0]});Q564=makeQuery(id+"F0.imprint","IMPRINT",FACE,{"disambiguationData":[TD([[makeQuery(id+"F0.imprint","IMPRINT",EDGE,{"disambiguationData":[TD([[subQ2,-1.0]])],"derivedFrom":subQ1}),-1.0]])]});}
            var Q565;
            {var subQ0=sQuery(id+"F0.wireOp",EDGE,"E14.23.0");var subQ1=sQuery(id+"F0.wireOp",EDGE,"E9.left");var subQ2=makeQuery(id+"F0.imprint","INTERSECT",VERTEX,{"derivedFrom":[subQ1,subQ0]});Q565=makeQuery(id+"F0.imprint","IMPRINT",FACE,{"disambiguationData":[TD([[makeQuery(id+"F0.imprint","IMPRINT",EDGE,{"disambiguationData":[TD([[subQ2,-1.0]])],"derivedFrom":subQ1}),-1.0]])]});}
            var Q566;
            {var subQ0=sQuery(id+"F0.wireOp",EDGE,"E14.25.1");var subQ1=sQuery(id+"F0.wireOp",EDGE,"E14.10.0");var subQ2=makeQuery(id+"F0.imprint","INTERSECT",VERTEX,{"derivedFrom":[subQ1,subQ0]});Q566=makeQuery(id+"F0.imprint","IMPRINT",FACE,{"disambiguationData":[TD([[makeQuery(id+"F0.imprint","IMPRINT",EDGE,{"disambiguationData":[TD([[subQ2,-1.0]])],"derivedFrom":subQ1}),-1.0]])]});}
            var Q567;
            {var subQ0=sQuery(id+"F0.wireOp",EDGE,"E14.32.0");var subQ1=sQuery(id+"F0.wireOp",EDGE,"E14.13.1");var subQ2=makeQuery(id+"F0.imprint","INTERSECT",VERTEX,{"derivedFrom":[subQ1,subQ0]});Q567=makeQuery(id+"F0.imprint","IMPRINT",FACE,{"disambiguationData":[TD([[makeQuery(id+"F0.imprint","IMPRINT",EDGE,{"disambiguationData":[TD([[subQ2,-1.0]])],"derivedFrom":subQ1}),-1.0]])]});}
            var Q568;
            {var subQ0=sQuery(id+"F0.wireOp",EDGE,"E14.29.1");var subQ1=sQuery(id+"F0.wireOp",EDGE,"E14.17.0");var subQ2=makeQuery(id+"F0.imprint","INTERSECT",VERTEX,{"derivedFrom":[subQ1,subQ0]});Q568=makeQuery(id+"F0.imprint","IMPRINT",FACE,{"disambiguationData":[TD([[makeQuery(id+"F0.imprint","IMPRINT",EDGE,{"disambiguationData":[TD([[subQ2,-1.0]])],"derivedFrom":subQ1}),-1.0]])]});}
            var Q569;
            {var subQ0=sQuery(id+"F0.wireOp",EDGE,"E14.21.1");var subQ1=sQuery(id+"F0.wireOp",EDGE,"E14.6.0");var subQ2=makeQuery(id+"F0.imprint","INTERSECT",VERTEX,{"derivedFrom":[subQ1,subQ0]});Q569=makeQuery(id+"F0.imprint","IMPRINT",FACE,{"disambiguationData":[TD([[makeQuery(id+"F0.imprint","IMPRINT",EDGE,{"disambiguationData":[TD([[subQ2,-1.0]])],"derivedFrom":subQ1}),-1.0]])]});}
            var Q570;
            {var subQ0=sQuery(id+"F0.wireOp",EDGE,"E14.24.0");var subQ1=sQuery(id+"F0.wireOp",EDGE,"E14.4.1");var subQ2=makeQuery(id+"F0.imprint","INTERSECT",VERTEX,{"derivedFrom":[subQ1,subQ0]});Q570=makeQuery(id+"F0.imprint","IMPRINT",FACE,{"disambiguationData":[TD([[makeQuery(id+"F0.imprint","IMPRINT",EDGE,{"disambiguationData":[TD([[subQ2,-1.0]])],"derivedFrom":subQ1}),-1.0]])]});}
            var Q571;
            {var subQ0=sQuery(id+"F0.wireOp",EDGE,"E14.28.0");var subQ1=sQuery(id+"F0.wireOp",EDGE,"E14.8.1");var subQ2=makeQuery(id+"F0.imprint","INTERSECT",VERTEX,{"derivedFrom":[subQ1,subQ0]});Q571=makeQuery(id+"F0.imprint","IMPRINT",FACE,{"disambiguationData":[TD([[makeQuery(id+"F0.imprint","IMPRINT",EDGE,{"disambiguationData":[TD([[subQ2,-1.0]])],"derivedFrom":subQ1}),-1.0]])]});}
            var Q572;
            {var subQ0=sQuery(id+"F0.wireOp",EDGE,"E14.23.1");var subQ1=sQuery(id+"F0.wireOp",EDGE,"E14.8.0");var subQ2=makeQuery(id+"F0.imprint","INTERSECT",VERTEX,{"derivedFrom":[subQ1,subQ0]});Q572=makeQuery(id+"F0.imprint","IMPRINT",FACE,{"disambiguationData":[TD([[makeQuery(id+"F0.imprint","IMPRINT",EDGE,{"disambiguationData":[TD([[subQ2,-1.0]])],"derivedFrom":subQ1}),-1.0]])]});}
            var Q573;
            {var subQ0=sQuery(id+"F0.wireOp",EDGE,"E14.15.1");var subQ1=sQuery(id+"F0.wireOp",EDGE,"E14.5.0");var subQ2=makeQuery(id+"F0.imprint","INTERSECT",VERTEX,{"derivedFrom":[subQ1,subQ0]});Q573=makeQuery(id+"F0.imprint","IMPRINT",FACE,{"disambiguationData":[TD([[makeQuery(id+"F0.imprint","IMPRINT",EDGE,{"disambiguationData":[TD([[subQ2,-1.0]])],"derivedFrom":subQ1}),-1.0]])]});}
            var Q574;
            {var subQ0=sQuery(id+"F0.wireOp",EDGE,"E14.21.1");var subQ1=sQuery(id+"F0.wireOp",EDGE,"E14.3.0");var subQ2=makeQuery(id+"F0.imprint","INTERSECT",VERTEX,{"derivedFrom":[subQ1,subQ0]});Q574=makeQuery(id+"F0.imprint","IMPRINT",FACE,{"disambiguationData":[TD([[makeQuery(id+"F0.imprint","IMPRINT",EDGE,{"disambiguationData":[TD([[subQ2,-1.0]])],"derivedFrom":subQ1}),-1.0]])]});}
            var Q575;
            {var subQ0=sQuery(id+"F0.wireOp",EDGE,"E14.33.0");var subQ1=sQuery(id+"F0.wireOp",EDGE,"E14.12.1");var subQ2=makeQuery(id+"F0.imprint","INTERSECT",VERTEX,{"derivedFrom":[subQ1,subQ0]});Q575=makeQuery(id+"F0.imprint","IMPRINT",FACE,{"disambiguationData":[TD([[makeQuery(id+"F0.imprint","IMPRINT",EDGE,{"disambiguationData":[TD([[subQ2,-1.0]])],"derivedFrom":subQ1}),-1.0]])]});}
            var Q576;
            {var subQ0=sQuery(id+"F0.wireOp",EDGE,"E14.14.1");var subQ1=sQuery(id+"F0.wireOp",EDGE,"E14.4.0");var subQ2=makeQuery(id+"F0.imprint","INTERSECT",VERTEX,{"derivedFrom":[subQ1,subQ0]});Q576=makeQuery(id+"F0.imprint","IMPRINT",FACE,{"disambiguationData":[TD([[makeQuery(id+"F0.imprint","IMPRINT",EDGE,{"disambiguationData":[TD([[subQ2,-1.0]])],"derivedFrom":subQ1}),-1.0]])]});}
            var Q577;
            {var subQ0=sQuery(id+"F0.wireOp",EDGE,"E14.28.1");var subQ1=sQuery(id+"F0.wireOp",EDGE,"E14.14.0");var subQ2=makeQuery(id+"F0.imprint","INTERSECT",VERTEX,{"derivedFrom":[subQ1,subQ0]});Q577=makeQuery(id+"F0.imprint","IMPRINT",FACE,{"disambiguationData":[TD([[makeQuery(id+"F0.imprint","IMPRINT",EDGE,{"disambiguationData":[TD([[subQ2,-1.0]])],"derivedFrom":subQ1}),-1.0]])]});}
            var Q578;
            {var subQ0=sQuery(id+"F0.wireOp",EDGE,"E14.23.1");var subQ1=sQuery(id+"F0.wireOp",EDGE,"E14.5.0");var subQ2=makeQuery(id+"F0.imprint","INTERSECT",VERTEX,{"derivedFrom":[subQ1,subQ0]});Q578=makeQuery(id+"F0.imprint","IMPRINT",FACE,{"disambiguationData":[TD([[makeQuery(id+"F0.imprint","IMPRINT",EDGE,{"disambiguationData":[TD([[subQ2,-1.0]])],"derivedFrom":subQ1}),-1.0]])]});}
            var Q579;
            {var subQ0=sQuery(id+"F0.wireOp",EDGE,"E14.12.1");var subQ1=sQuery(id+"F0.wireOp",EDGE,"E14.2.0");var subQ2=makeQuery(id+"F0.imprint","INTERSECT",VERTEX,{"derivedFrom":[subQ1,subQ0]});Q579=makeQuery(id+"F0.imprint","IMPRINT",FACE,{"disambiguationData":[TD([[makeQuery(id+"F0.imprint","IMPRINT",EDGE,{"disambiguationData":[TD([[subQ2,-1.0]])],"derivedFrom":subQ1}),-1.0]])]});}
            var Q580;
            {var subQ0=sQuery(id+"F0.wireOp",EDGE,"E14.33.0");var subQ1=sQuery(id+"F0.wireOp",EDGE,"E14.14.1");var subQ2=makeQuery(id+"F0.imprint","INTERSECT",VERTEX,{"derivedFrom":[subQ1,subQ0]});Q580=makeQuery(id+"F0.imprint","IMPRINT",FACE,{"disambiguationData":[TD([[makeQuery(id+"F0.imprint","IMPRINT",EDGE,{"disambiguationData":[TD([[subQ2,-1.0]])],"derivedFrom":subQ1}),-1.0]])]});}
            var Q581;
            {var subQ0=sQuery(id+"F0.wireOp",EDGE,"E14.31.1");var subQ1=sQuery(id+"F0.wireOp",EDGE,"E14.20.0");var subQ2=makeQuery(id+"F0.imprint","INTERSECT",VERTEX,{"derivedFrom":[subQ1,subQ0]});Q581=makeQuery(id+"F0.imprint","IMPRINT",FACE,{"disambiguationData":[TD([[makeQuery(id+"F0.imprint","IMPRINT",EDGE,{"disambiguationData":[TD([[subQ2,-1.0]])],"derivedFrom":subQ1}),-1.0]])]});}
            var Q582;
            {var subQ0=sQuery(id+"F0.wireOp",EDGE,"E14.16.1");var subQ1=sQuery(id+"F0.wireOp",EDGE,"E14.6.0");var subQ2=makeQuery(id+"F0.imprint","INTERSECT",VERTEX,{"derivedFrom":[subQ1,subQ0]});Q582=makeQuery(id+"F0.imprint","IMPRINT",FACE,{"disambiguationData":[TD([[makeQuery(id+"F0.imprint","IMPRINT",EDGE,{"disambiguationData":[TD([[subQ2,-1.0]])],"derivedFrom":subQ1}),-1.0]])]});}
            var Q583;
            {var subQ0=sQuery(id+"F0.wireOp",EDGE,"E14.26.1");var subQ1=sQuery(id+"F0.wireOp",EDGE,"E14.15.0");var subQ2=makeQuery(id+"F0.imprint","INTERSECT",VERTEX,{"derivedFrom":[subQ1,subQ0]});Q583=makeQuery(id+"F0.imprint","IMPRINT",FACE,{"disambiguationData":[TD([[makeQuery(id+"F0.imprint","IMPRINT",EDGE,{"disambiguationData":[TD([[subQ2,-1.0]])],"derivedFrom":subQ1}),-1.0]])]});}
            var Q584;
            {var subQ0=sQuery(id+"F0.wireOp",EDGE,"E14.25.0");var subQ1=sQuery(id+"F0.wireOp",EDGE,"E14.6.1");var subQ2=makeQuery(id+"F0.imprint","INTERSECT",VERTEX,{"derivedFrom":[subQ1,subQ0]});Q584=makeQuery(id+"F0.imprint","IMPRINT",FACE,{"disambiguationData":[TD([[makeQuery(id+"F0.imprint","IMPRINT",EDGE,{"disambiguationData":[TD([[subQ2,-1.0]])],"derivedFrom":subQ1}),-1.0]])]});}
            var Q585;
            {var subQ0=sQuery(id+"F0.wireOp",EDGE,"E14.31.1");var subQ1=sQuery(id+"F0.wireOp",EDGE,"E14.18.0");var subQ2=makeQuery(id+"F0.imprint","INTERSECT",VERTEX,{"derivedFrom":[subQ1,subQ0]});Q585=makeQuery(id+"F0.imprint","IMPRINT",FACE,{"disambiguationData":[TD([[makeQuery(id+"F0.imprint","IMPRINT",EDGE,{"disambiguationData":[TD([[subQ2,-1.0]])],"derivedFrom":subQ1}),-1.0]])]});}
            var Q586;
            {var subQ0=sQuery(id+"F0.wireOp",EDGE,"E14.19.1");var subQ1=sQuery(id+"F0.wireOp",EDGE,"E14.1.0");var subQ2=makeQuery(id+"F0.imprint","INTERSECT",VERTEX,{"derivedFrom":[subQ1,subQ0]});Q586=makeQuery(id+"F0.imprint","IMPRINT",FACE,{"disambiguationData":[TD([[makeQuery(id+"F0.imprint","IMPRINT",EDGE,{"disambiguationData":[TD([[subQ2,-1.0]])],"derivedFrom":subQ1}),-1.0]])]});}
            var Q587;
            {var subQ0=sQuery(id+"F0.wireOp",EDGE,"E14.33.0");var subQ1=sQuery(id+"F0.wireOp",EDGE,"E14.10.1");var subQ2=makeQuery(id+"F0.imprint","INTERSECT",VERTEX,{"derivedFrom":[subQ1,subQ0]});Q587=makeQuery(id+"F0.imprint","IMPRINT",FACE,{"disambiguationData":[TD([[makeQuery(id+"F0.imprint","IMPRINT",EDGE,{"disambiguationData":[TD([[subQ2,-1.0]])],"derivedFrom":subQ1}),-1.0]])]});}
            var Q588;
            {var subQ0=sQuery(id+"F0.wireOp",EDGE,"E14.15.1");var subQ1=sQuery(id+"F0.wireOp",EDGE,"E14.6.0");var subQ2=makeQuery(id+"F0.imprint","INTERSECT",VERTEX,{"derivedFrom":[subQ1,subQ0]});Q588=makeQuery(id+"F0.imprint","IMPRINT",FACE,{"disambiguationData":[TD([[makeQuery(id+"F0.imprint","IMPRINT",EDGE,{"disambiguationData":[TD([[subQ2,-1.0]])],"derivedFrom":subQ1}),-1.0]])]});}
            var Q589;
            {var subQ0=sQuery(id+"F0.wireOp",EDGE,"E14.26.0");var subQ1=sQuery(id+"F0.wireOp",EDGE,"E14.1.1");var subQ2=makeQuery(id+"F0.imprint","INTERSECT",VERTEX,{"derivedFrom":[subQ1,subQ0]});Q589=makeQuery(id+"F0.imprint","IMPRINT",FACE,{"disambiguationData":[TD([[makeQuery(id+"F0.imprint","IMPRINT",EDGE,{"disambiguationData":[TD([[subQ2,-1.0]])],"derivedFrom":subQ1}),-1.0]])]});}
            var Q590;
            {var subQ0=sQuery(id+"F0.wireOp",EDGE,"E14.29.1");var subQ1=sQuery(id+"F0.wireOp",EDGE,"E14.19.0");var subQ2=makeQuery(id+"F0.imprint","INTERSECT",VERTEX,{"derivedFrom":[subQ1,subQ0]});Q590=makeQuery(id+"F0.imprint","IMPRINT",FACE,{"disambiguationData":[TD([[makeQuery(id+"F0.imprint","IMPRINT",EDGE,{"disambiguationData":[TD([[subQ2,-1.0]])],"derivedFrom":subQ1}),-1.0]])]});}
            var Q591;
            {var subQ0=sQuery(id+"F0.wireOp",EDGE,"E14.15.1");var subQ1=sQuery(id+"F0.wireOp",EDGE,"E14.4.0");var subQ2=makeQuery(id+"F0.imprint","INTERSECT",VERTEX,{"derivedFrom":[subQ1,subQ0]});Q591=makeQuery(id+"F0.imprint","IMPRINT",FACE,{"disambiguationData":[TD([[makeQuery(id+"F0.imprint","IMPRINT",EDGE,{"disambiguationData":[TD([[subQ2,-1.0]])],"derivedFrom":subQ1}),-1.0]])]});}
            var Q592;
            {var subQ0=sQuery(id+"F0.wireOp",EDGE,"E14.30.1");var subQ1=sQuery(id+"F0.wireOp",EDGE,"E14.20.0");var subQ2=makeQuery(id+"F0.imprint","INTERSECT",VERTEX,{"derivedFrom":[subQ1,subQ0]});Q592=makeQuery(id+"F0.imprint","IMPRINT",FACE,{"disambiguationData":[TD([[makeQuery(id+"F0.imprint","IMPRINT",EDGE,{"disambiguationData":[TD([[subQ2,-1.0]])],"derivedFrom":subQ1}),-1.0]])]});}
            var Q593;
            {var subQ0=sQuery(id+"F0.wireOp",EDGE,"E14.33.0");var subQ1=sQuery(id+"F0.wireOp",EDGE,"E14.13.1");var subQ2=makeQuery(id+"F0.imprint","INTERSECT",VERTEX,{"derivedFrom":[subQ1,subQ0]});Q593=makeQuery(id+"F0.imprint","IMPRINT",FACE,{"disambiguationData":[TD([[makeQuery(id+"F0.imprint","IMPRINT",EDGE,{"disambiguationData":[TD([[subQ2,-1.0]])],"derivedFrom":subQ1}),-1.0]])]});}
            var Q594;
            {var subQ0=sQuery(id+"F0.wireOp",EDGE,"E14.12.1");var subQ1=sQuery(id+"F0.wireOp",EDGE,"E14.1.0");var subQ2=makeQuery(id+"F0.imprint","INTERSECT",VERTEX,{"derivedFrom":[subQ1,subQ0]});Q594=makeQuery(id+"F0.imprint","IMPRINT",FACE,{"disambiguationData":[TD([[makeQuery(id+"F0.imprint","IMPRINT",EDGE,{"disambiguationData":[TD([[subQ2,-1.0]])],"derivedFrom":subQ1}),-1.0]])]});}
            var Q595;
            {var subQ0=sQuery(id+"F0.wireOp",EDGE,"E14.22.1");var subQ1=sQuery(id+"F0.wireOp",EDGE,"E14.9.0");var subQ2=makeQuery(id+"F0.imprint","INTERSECT",VERTEX,{"derivedFrom":[subQ1,subQ0]});Q595=makeQuery(id+"F0.imprint","IMPRINT",FACE,{"disambiguationData":[TD([[makeQuery(id+"F0.imprint","IMPRINT",EDGE,{"disambiguationData":[TD([[subQ2,-1.0]])],"derivedFrom":subQ1}),-1.0]])]});}
            var Q596;
            {var subQ0=sQuery(id+"F0.wireOp",EDGE,"E14.22.0");var subQ1=sQuery(id+"F0.wireOp",EDGE,"E9.left");var subQ2=makeQuery(id+"F0.imprint","INTERSECT",VERTEX,{"derivedFrom":[subQ1,subQ0]});Q596=makeQuery(id+"F0.imprint","IMPRINT",FACE,{"disambiguationData":[TD([[makeQuery(id+"F0.imprint","IMPRINT",EDGE,{"disambiguationData":[TD([[subQ2,-1.0]])],"derivedFrom":subQ1}),-1.0]])]});}
            var Q597;
            {var subQ0=sQuery(id+"F0.wireOp",EDGE,"E14.25.0");var subQ1=sQuery(id+"F0.wireOp",EDGE,"E14.3.1");var subQ2=makeQuery(id+"F0.imprint","INTERSECT",VERTEX,{"derivedFrom":[subQ1,subQ0]});Q597=makeQuery(id+"F0.imprint","IMPRINT",FACE,{"disambiguationData":[TD([[makeQuery(id+"F0.imprint","IMPRINT",EDGE,{"disambiguationData":[TD([[subQ2,-1.0]])],"derivedFrom":subQ1}),-1.0]])]});}
            var Q598;
            {var subQ0=sQuery(id+"F0.wireOp",EDGE,"E14.26.1");var subQ1=sQuery(id+"F0.wireOp",EDGE,"E14.13.0");var subQ2=makeQuery(id+"F0.imprint","INTERSECT",VERTEX,{"derivedFrom":[subQ1,subQ0]});Q598=makeQuery(id+"F0.imprint","IMPRINT",FACE,{"disambiguationData":[TD([[makeQuery(id+"F0.imprint","IMPRINT",EDGE,{"disambiguationData":[TD([[subQ2,-1.0]])],"derivedFrom":subQ1}),-1.0]])]});}
            var Q599;
            {var subQ0=sQuery(id+"F0.wireOp",EDGE,"E14.26.1");var subQ1=sQuery(id+"F0.wireOp",EDGE,"E14.9.0");var subQ2=makeQuery(id+"F0.imprint","INTERSECT",VERTEX,{"derivedFrom":[subQ1,subQ0]});Q599=makeQuery(id+"F0.imprint","IMPRINT",FACE,{"disambiguationData":[TD([[makeQuery(id+"F0.imprint","IMPRINT",EDGE,{"disambiguationData":[TD([[subQ2,-1.0]])],"derivedFrom":subQ1}),-1.0]])]});}
            var Q600;
            {var subQ0=sQuery(id+"F0.wireOp",EDGE,"E14.27.0");var subQ1=sQuery(id+"F0.wireOp",EDGE,"E14.8.1");var subQ2=makeQuery(id+"F0.imprint","INTERSECT",VERTEX,{"derivedFrom":[subQ1,subQ0]});Q600=makeQuery(id+"F0.imprint","IMPRINT",FACE,{"disambiguationData":[TD([[makeQuery(id+"F0.imprint","IMPRINT",EDGE,{"disambiguationData":[TD([[subQ2,-1.0]])],"derivedFrom":subQ1}),-1.0]])]});}
            var Q601;
            {var subQ0=sQuery(id+"F0.wireOp",EDGE,"E14.33.0");var subQ1=sQuery(id+"F0.wireOp",EDGE,"E14.11.1");var subQ2=makeQuery(id+"F0.imprint","INTERSECT",VERTEX,{"derivedFrom":[subQ1,subQ0]});Q601=makeQuery(id+"F0.imprint","IMPRINT",FACE,{"disambiguationData":[TD([[makeQuery(id+"F0.imprint","IMPRINT",EDGE,{"disambiguationData":[TD([[subQ2,-1.0]])],"derivedFrom":subQ1}),-1.0]])]});}
            var Q602;
            {var subQ0=sQuery(id+"F0.wireOp",EDGE,"E14.17.1");var subQ1=sQuery(id+"F0.wireOp",EDGE,"E14.6.0");var subQ2=makeQuery(id+"F0.imprint","INTERSECT",VERTEX,{"derivedFrom":[subQ1,subQ0]});Q602=makeQuery(id+"F0.imprint","IMPRINT",FACE,{"disambiguationData":[TD([[makeQuery(id+"F0.imprint","IMPRINT",EDGE,{"disambiguationData":[TD([[subQ2,-1.0]])],"derivedFrom":subQ1}),-1.0]])]});}
            var Q603;
            {var subQ0=sQuery(id+"F0.wireOp",EDGE,"E14.16.1");var subQ1=sQuery(id+"F0.wireOp",EDGE,"E14.5.0");var subQ2=makeQuery(id+"F0.imprint","INTERSECT",VERTEX,{"derivedFrom":[subQ1,subQ0]});Q603=makeQuery(id+"F0.imprint","IMPRINT",FACE,{"disambiguationData":[TD([[makeQuery(id+"F0.imprint","IMPRINT",EDGE,{"disambiguationData":[TD([[subQ2,-1.0]])],"derivedFrom":subQ1}),-1.0]])]});}
            var Q604;
            {var subQ0=sQuery(id+"F0.wireOp",EDGE,"E14.22.0");var subQ1=sQuery(id+"F0.wireOp",EDGE,"E9.left");var subQ2=makeQuery(id+"F0.imprint","INTERSECT",VERTEX,{"derivedFrom":[subQ1,subQ0]});Q604=makeQuery(id+"F0.imprint","IMPRINT",FACE,{"disambiguationData":[TD([[makeQuery(id+"F0.imprint","IMPRINT",EDGE,{"disambiguationData":[TD([[subQ2,-1.0]])],"derivedFrom":subQ1}),1.0]])]});}
            var Q605;
            {var subQ0=sQuery(id+"F0.wireOp",EDGE,"E14.30.1");var subQ1=sQuery(id+"F0.wireOp",EDGE,"E14.15.0");var subQ2=makeQuery(id+"F0.imprint","INTERSECT",VERTEX,{"derivedFrom":[subQ1,subQ0]});Q605=makeQuery(id+"F0.imprint","IMPRINT",FACE,{"disambiguationData":[TD([[makeQuery(id+"F0.imprint","IMPRINT",EDGE,{"disambiguationData":[TD([[subQ2,-1.0]])],"derivedFrom":subQ1}),-1.0]])]});}
            var Q606;
            {var subQ0=sQuery(id+"F0.wireOp",EDGE,"E14.14.1");var subQ1=sQuery(id+"F0.wireOp",EDGE,"E14.3.0");var subQ2=makeQuery(id+"F0.imprint","INTERSECT",VERTEX,{"derivedFrom":[subQ1,subQ0]});Q606=makeQuery(id+"F0.imprint","IMPRINT",FACE,{"disambiguationData":[TD([[makeQuery(id+"F0.imprint","IMPRINT",EDGE,{"disambiguationData":[TD([[subQ2,-1.0]])],"derivedFrom":subQ1}),-1.0]])]});}
            var Q607;
            {var subQ0=sQuery(id+"F0.wireOp",EDGE,"E14.20.1");var subQ1=sQuery(id+"F0.wireOp",EDGE,"E14.2.0");var subQ2=makeQuery(id+"F0.imprint","INTERSECT",VERTEX,{"derivedFrom":[subQ1,subQ0]});Q607=makeQuery(id+"F0.imprint","IMPRINT",FACE,{"disambiguationData":[TD([[makeQuery(id+"F0.imprint","IMPRINT",EDGE,{"disambiguationData":[TD([[subQ2,-1.0]])],"derivedFrom":subQ1}),-1.0]])]});}
            var Q608;
            {var subQ0=sQuery(id+"F0.wireOp",EDGE,"E14.34.1");var subQ1=sQuery(id+"F0.wireOp",EDGE,"E14.20.0");var subQ2=makeQuery(id+"F0.imprint","INTERSECT",VERTEX,{"derivedFrom":[subQ1,subQ0]});Q608=makeQuery(id+"F0.imprint","IMPRINT",FACE,{"disambiguationData":[TD([[makeQuery(id+"F0.imprint","IMPRINT",EDGE,{"disambiguationData":[TD([[subQ2,-1.0]])],"derivedFrom":subQ1}),-1.0]])]});}
            var Q609;
            {var subQ0=sQuery(id+"F0.wireOp",EDGE,"E14.30.1");var subQ1=sQuery(id+"F0.wireOp",EDGE,"E14.18.0");var subQ2=makeQuery(id+"F0.imprint","INTERSECT",VERTEX,{"derivedFrom":[subQ1,subQ0]});Q609=makeQuery(id+"F0.imprint","IMPRINT",FACE,{"disambiguationData":[TD([[makeQuery(id+"F0.imprint","IMPRINT",EDGE,{"disambiguationData":[TD([[subQ2,-1.0]])],"derivedFrom":subQ1}),-1.0]])]});}
            var Q610;
            {var subQ0=sQuery(id+"F0.wireOp",EDGE,"E14.18.1");var subQ1=sQuery(id+"F0.wireOp",EDGE,"E14.5.0");var subQ2=makeQuery(id+"F0.imprint","INTERSECT",VERTEX,{"derivedFrom":[subQ1,subQ0]});Q610=makeQuery(id+"F0.imprint","IMPRINT",FACE,{"disambiguationData":[TD([[makeQuery(id+"F0.imprint","IMPRINT",EDGE,{"disambiguationData":[TD([[subQ2,-1.0]])],"derivedFrom":subQ1}),-1.0]])]});}
            var Q611;
            {var subQ0=sQuery(id+"F0.wireOp",EDGE,"E14.17.1");var subQ1=sQuery(id+"F0.wireOp",EDGE,"E9.right");var subQ2=makeQuery(id+"F0.imprint","INTERSECT",VERTEX,{"derivedFrom":[subQ1,subQ0]});Q611=makeQuery(id+"F0.imprint","IMPRINT",FACE,{"disambiguationData":[TD([[makeQuery(id+"F0.imprint","IMPRINT",EDGE,{"disambiguationData":[TD([[subQ2,-1.0]])],"derivedFrom":subQ1}),1.0]])]});}
            var Q612;
            {var subQ0=sQuery(id+"F0.wireOp",EDGE,"E14.34.0");var subQ1=sQuery(id+"F0.wireOp",EDGE,"E14.11.1");var subQ2=makeQuery(id+"F0.imprint","INTERSECT",VERTEX,{"derivedFrom":[subQ1,subQ0]});Q612=makeQuery(id+"F0.imprint","IMPRINT",FACE,{"disambiguationData":[TD([[makeQuery(id+"F0.imprint","IMPRINT",EDGE,{"disambiguationData":[TD([[subQ2,-1.0]])],"derivedFrom":subQ1}),-1.0]])]});}
            var Q613;
            {var subQ0=sQuery(id+"F0.wireOp",EDGE,"E14.27.0");var subQ1=sQuery(id+"F0.wireOp",EDGE,"E14.3.1");var subQ2=makeQuery(id+"F0.imprint","INTERSECT",VERTEX,{"derivedFrom":[subQ1,subQ0]});Q613=makeQuery(id+"F0.imprint","IMPRINT",FACE,{"disambiguationData":[TD([[makeQuery(id+"F0.imprint","IMPRINT",EDGE,{"disambiguationData":[TD([[subQ2,-1.0]])],"derivedFrom":subQ1}),-1.0]])]});}
            var Q614;
            {var subQ0=sQuery(id+"F0.wireOp",EDGE,"E14.27.1");var subQ1=sQuery(id+"F0.wireOp",EDGE,"E14.11.0");var subQ2=makeQuery(id+"F0.imprint","INTERSECT",VERTEX,{"derivedFrom":[subQ1,subQ0]});Q614=makeQuery(id+"F0.imprint","IMPRINT",FACE,{"disambiguationData":[TD([[makeQuery(id+"F0.imprint","IMPRINT",EDGE,{"disambiguationData":[TD([[subQ2,-1.0]])],"derivedFrom":subQ1}),-1.0]])]});}
            var Q615;
            {var subQ0=sQuery(id+"F0.wireOp",EDGE,"E14.29.0");var subQ1=sQuery(id+"F0.wireOp",EDGE,"E14.8.1");var subQ2=makeQuery(id+"F0.imprint","INTERSECT",VERTEX,{"derivedFrom":[subQ1,subQ0]});Q615=makeQuery(id+"F0.imprint","IMPRINT",FACE,{"disambiguationData":[TD([[makeQuery(id+"F0.imprint","IMPRINT",EDGE,{"disambiguationData":[TD([[subQ2,-1.0]])],"derivedFrom":subQ1}),-1.0]])]});}
            var Q616;
            {var subQ0=sQuery(id+"F0.wireOp",EDGE,"E14.34.0");var subQ1=sQuery(id+"F0.wireOp",EDGE,"E14.13.1");var subQ2=makeQuery(id+"F0.imprint","INTERSECT",VERTEX,{"derivedFrom":[subQ1,subQ0]});Q616=makeQuery(id+"F0.imprint","IMPRINT",FACE,{"disambiguationData":[TD([[makeQuery(id+"F0.imprint","IMPRINT",EDGE,{"disambiguationData":[TD([[subQ2,-1.0]])],"derivedFrom":subQ1}),-1.0]])]});}
            var Q617;
            {var subQ0=sQuery(id+"F0.wireOp",EDGE,"E14.22.1");var subQ1=sQuery(id+"F0.wireOp",EDGE,"E14.6.0");var subQ2=makeQuery(id+"F0.imprint","INTERSECT",VERTEX,{"derivedFrom":[subQ1,subQ0]});Q617=makeQuery(id+"F0.imprint","IMPRINT",FACE,{"disambiguationData":[TD([[makeQuery(id+"F0.imprint","IMPRINT",EDGE,{"disambiguationData":[TD([[subQ2,-1.0]])],"derivedFrom":subQ1}),-1.0]])]});}
            var Q618;
            {var subQ0=sQuery(id+"F0.wireOp",EDGE,"E14.33.1");var subQ1=sQuery(id+"F0.wireOp",EDGE,"E14.21.0");var subQ2=makeQuery(id+"F0.imprint","INTERSECT",VERTEX,{"derivedFrom":[subQ1,subQ0]});Q618=makeQuery(id+"F0.imprint","IMPRINT",FACE,{"disambiguationData":[TD([[makeQuery(id+"F0.imprint","IMPRINT",EDGE,{"disambiguationData":[TD([[subQ2,-1.0]])],"derivedFrom":subQ1}),-1.0]])]});}
            var Q619;
            {var subQ0=sQuery(id+"F0.wireOp",EDGE,"E14.29.1");var subQ1=sQuery(id+"F0.wireOp",EDGE,"E14.18.0");var subQ2=makeQuery(id+"F0.imprint","INTERSECT",VERTEX,{"derivedFrom":[subQ1,subQ0]});Q619=makeQuery(id+"F0.imprint","IMPRINT",FACE,{"disambiguationData":[TD([[makeQuery(id+"F0.imprint","IMPRINT",EDGE,{"disambiguationData":[TD([[subQ2,-1.0]])],"derivedFrom":subQ1}),-1.0]])]});}
            var Q620;
            {var subQ0=sQuery(id+"F0.wireOp",EDGE,"E14.33.1");var subQ1=sQuery(id+"F0.wireOp",EDGE,"E14.18.0");var subQ2=makeQuery(id+"F0.imprint","INTERSECT",VERTEX,{"derivedFrom":[subQ1,subQ0]});Q620=makeQuery(id+"F0.imprint","IMPRINT",FACE,{"disambiguationData":[TD([[makeQuery(id+"F0.imprint","IMPRINT",EDGE,{"disambiguationData":[TD([[subQ2,-1.0]])],"derivedFrom":subQ1}),-1.0]])]});}
            var Q621;
            {var subQ0=sQuery(id+"F0.wireOp",EDGE,"E14.13.1");var subQ1=sQuery(id+"F0.wireOp",EDGE,"E14.2.0");var subQ2=makeQuery(id+"F0.imprint","INTERSECT",VERTEX,{"derivedFrom":[subQ1,subQ0]});Q621=makeQuery(id+"F0.imprint","IMPRINT",FACE,{"disambiguationData":[TD([[makeQuery(id+"F0.imprint","IMPRINT",EDGE,{"disambiguationData":[TD([[subQ2,-1.0]])],"derivedFrom":subQ1}),-1.0]])]});}
            var Q622;
            {var subQ0=sQuery(id+"F0.wireOp",EDGE,"E14.19.1");var subQ1=sQuery(id+"F0.wireOp",EDGE,"E14.3.0");var subQ2=makeQuery(id+"F0.imprint","INTERSECT",VERTEX,{"derivedFrom":[subQ1,subQ0]});Q622=makeQuery(id+"F0.imprint","IMPRINT",FACE,{"disambiguationData":[TD([[makeQuery(id+"F0.imprint","IMPRINT",EDGE,{"disambiguationData":[TD([[subQ2,-1.0]])],"derivedFrom":subQ1}),-1.0]])]});}
            var Q623;
            {var subQ0=sQuery(id+"F0.wireOp",EDGE,"E14.13.1");var subQ1=sQuery(id+"F0.wireOp",EDGE,"E14.1.0");var subQ2=makeQuery(id+"F0.imprint","INTERSECT",VERTEX,{"derivedFrom":[subQ1,subQ0]});Q623=makeQuery(id+"F0.imprint","IMPRINT",FACE,{"disambiguationData":[TD([[makeQuery(id+"F0.imprint","IMPRINT",EDGE,{"disambiguationData":[TD([[subQ2,-1.0]])],"derivedFrom":subQ1}),-1.0]])]});}
            var Q624;
            {var subQ0=sQuery(id+"F0.wireOp",EDGE,"E14.27.0");var subQ1=sQuery(id+"F0.wireOp",EDGE,"E14.6.1");var subQ2=makeQuery(id+"F0.imprint","INTERSECT",VERTEX,{"derivedFrom":[subQ1,subQ0]});Q624=makeQuery(id+"F0.imprint","IMPRINT",FACE,{"disambiguationData":[TD([[makeQuery(id+"F0.imprint","IMPRINT",EDGE,{"disambiguationData":[TD([[subQ2,-1.0]])],"derivedFrom":subQ1}),-1.0]])]});}
            var Q625;
            {var subQ0=sQuery(id+"F0.wireOp",EDGE,"E14.34.1");var subQ1=sQuery(id+"F0.wireOp",EDGE,"E14.22.0");var subQ2=makeQuery(id+"F0.imprint","INTERSECT",VERTEX,{"derivedFrom":[subQ1,subQ0]});Q625=makeQuery(id+"F0.imprint","IMPRINT",FACE,{"disambiguationData":[TD([[makeQuery(id+"F0.imprint","IMPRINT",EDGE,{"disambiguationData":[TD([[subQ2,-1.0]])],"derivedFrom":subQ1}),-1.0]])]});}
            var Q626;
            {var subQ0=sQuery(id+"F0.wireOp",EDGE,"E14.32.0");var subQ1=sQuery(id+"F0.wireOp",EDGE,"E14.12.1");var subQ2=makeQuery(id+"F0.imprint","INTERSECT",VERTEX,{"derivedFrom":[subQ1,subQ0]});Q626=makeQuery(id+"F0.imprint","IMPRINT",FACE,{"disambiguationData":[TD([[makeQuery(id+"F0.imprint","IMPRINT",EDGE,{"disambiguationData":[TD([[subQ2,-1.0]])],"derivedFrom":subQ1}),-1.0]])]});}
            var Q627;
            {var subQ0=sQuery(id+"F0.wireOp",EDGE,"E14.32.1");var subQ1=sQuery(id+"F0.wireOp",EDGE,"E14.19.0");var subQ2=makeQuery(id+"F0.imprint","INTERSECT",VERTEX,{"derivedFrom":[subQ1,subQ0]});Q627=makeQuery(id+"F0.imprint","IMPRINT",FACE,{"disambiguationData":[TD([[makeQuery(id+"F0.imprint","IMPRINT",EDGE,{"disambiguationData":[TD([[subQ2,-1.0]])],"derivedFrom":subQ1}),-1.0]])]});}
            var Q628;
            {var subQ0=sQuery(id+"F0.wireOp",EDGE,"E14.33.1");var subQ1=sQuery(id+"F0.wireOp",EDGE,"E14.15.0");var subQ2=makeQuery(id+"F0.imprint","INTERSECT",VERTEX,{"derivedFrom":[subQ1,subQ0]});Q628=makeQuery(id+"F0.imprint","IMPRINT",FACE,{"disambiguationData":[TD([[makeQuery(id+"F0.imprint","IMPRINT",EDGE,{"disambiguationData":[TD([[subQ2,-1.0]])],"derivedFrom":subQ1}),-1.0]])]});}
            var Q629;
            {var subQ0=sQuery(id+"F0.wireOp",EDGE,"E14.29.1");var subQ1=sQuery(id+"F0.wireOp",EDGE,"E14.15.0");var subQ2=makeQuery(id+"F0.imprint","INTERSECT",VERTEX,{"derivedFrom":[subQ1,subQ0]});Q629=makeQuery(id+"F0.imprint","IMPRINT",FACE,{"disambiguationData":[TD([[makeQuery(id+"F0.imprint","IMPRINT",EDGE,{"disambiguationData":[TD([[subQ2,-1.0]])],"derivedFrom":subQ1}),-1.0]])]});}
            var Q630;
            {var subQ0=sQuery(id+"F0.wireOp",EDGE,"E14.25.1");var subQ1=sQuery(id+"F0.wireOp",EDGE,"E14.13.0");var subQ2=makeQuery(id+"F0.imprint","INTERSECT",VERTEX,{"derivedFrom":[subQ1,subQ0]});Q630=makeQuery(id+"F0.imprint","IMPRINT",FACE,{"disambiguationData":[TD([[makeQuery(id+"F0.imprint","IMPRINT",EDGE,{"disambiguationData":[TD([[subQ2,-1.0]])],"derivedFrom":subQ1}),-1.0]])]});}
            var Q631;
            {var subQ0=sQuery(id+"F0.wireOp",EDGE,"E14.21.1");var subQ1=sQuery(id+"F0.wireOp",EDGE,"E14.9.0");var subQ2=makeQuery(id+"F0.imprint","INTERSECT",VERTEX,{"derivedFrom":[subQ1,subQ0]});Q631=makeQuery(id+"F0.imprint","IMPRINT",FACE,{"disambiguationData":[TD([[makeQuery(id+"F0.imprint","IMPRINT",EDGE,{"disambiguationData":[TD([[subQ2,-1.0]])],"derivedFrom":subQ1}),-1.0]])]});}
            var Q632;
            {var subQ0=sQuery(id+"F0.wireOp",EDGE,"E14.27.1");var subQ1=sQuery(id+"F0.wireOp",EDGE,"E14.13.0");var subQ2=makeQuery(id+"F0.imprint","INTERSECT",VERTEX,{"derivedFrom":[subQ1,subQ0]});Q632=makeQuery(id+"F0.imprint","IMPRINT",FACE,{"disambiguationData":[TD([[makeQuery(id+"F0.imprint","IMPRINT",EDGE,{"disambiguationData":[TD([[subQ2,-1.0]])],"derivedFrom":subQ1}),-1.0]])]});}
            var Q633;
            {var subQ0=sQuery(id+"F0.wireOp",EDGE,"E14.31.1");var subQ1=sQuery(id+"F0.wireOp",EDGE,"E14.19.0");var subQ2=makeQuery(id+"F0.imprint","INTERSECT",VERTEX,{"derivedFrom":[subQ1,subQ0]});Q633=makeQuery(id+"F0.imprint","IMPRINT",FACE,{"disambiguationData":[TD([[makeQuery(id+"F0.imprint","IMPRINT",EDGE,{"disambiguationData":[TD([[subQ2,-1.0]])],"derivedFrom":subQ1}),-1.0]])]});}
            var Q634;
            {var subQ0=sQuery(id+"F0.wireOp",EDGE,"E14.24.0");var subQ1=sQuery(id+"F0.wireOp",EDGE,"E14.3.1");var subQ2=makeQuery(id+"F0.imprint","INTERSECT",VERTEX,{"derivedFrom":[subQ1,subQ0]});Q634=makeQuery(id+"F0.imprint","IMPRINT",FACE,{"disambiguationData":[TD([[makeQuery(id+"F0.imprint","IMPRINT",EDGE,{"disambiguationData":[TD([[subQ2,-1.0]])],"derivedFrom":subQ1}),-1.0]])]});}
            var Q635;
            {var subQ0=sQuery(id+"F0.wireOp",EDGE,"E14.23.1");var subQ1=sQuery(id+"F0.wireOp",EDGE,"E14.6.0");var subQ2=makeQuery(id+"F0.imprint","INTERSECT",VERTEX,{"derivedFrom":[subQ1,subQ0]});Q635=makeQuery(id+"F0.imprint","IMPRINT",FACE,{"disambiguationData":[TD([[makeQuery(id+"F0.imprint","IMPRINT",EDGE,{"disambiguationData":[TD([[subQ2,-1.0]])],"derivedFrom":subQ1}),-1.0]])]});}
            var Q636;
            {var subQ0=sQuery(id+"F0.wireOp",EDGE,"E14.17.1");var subQ1=sQuery(id+"F0.wireOp",EDGE,"E14.5.0");var subQ2=makeQuery(id+"F0.imprint","INTERSECT",VERTEX,{"derivedFrom":[subQ1,subQ0]});Q636=makeQuery(id+"F0.imprint","IMPRINT",FACE,{"disambiguationData":[TD([[makeQuery(id+"F0.imprint","IMPRINT",EDGE,{"disambiguationData":[TD([[subQ2,-1.0]])],"derivedFrom":subQ1}),-1.0]])]});}
            var Q637;
            {var subQ0=sQuery(id+"F0.wireOp",EDGE,"E14.35.1");var subQ1=sQuery(id+"F0.wireOp",EDGE,"E14.24.0");var subQ2=makeQuery(id+"F0.imprint","INTERSECT",VERTEX,{"derivedFrom":[subQ1,subQ0]});Q637=makeQuery(id+"F0.imprint","IMPRINT",FACE,{"disambiguationData":[TD([[makeQuery(id+"F0.imprint","IMPRINT",EDGE,{"disambiguationData":[TD([[subQ2,-1.0]])],"derivedFrom":subQ1}),-1.0]])]});}
            var Q638;
            {var subQ0=sQuery(id+"F0.wireOp",EDGE,"E14.20.0");var subQ1=sQuery(id+"F0.wireOp",EDGE,"E14.1.1");var subQ2=makeQuery(id+"F0.imprint","INTERSECT",VERTEX,{"derivedFrom":[subQ1,subQ0]});Q638=makeQuery(id+"F0.imprint","IMPRINT",FACE,{"disambiguationData":[TD([[makeQuery(id+"F0.imprint","IMPRINT",EDGE,{"disambiguationData":[TD([[subQ2,-1.0]])],"derivedFrom":subQ1}),-1.0]])]});}
            var Q639;
            {var subQ0=sQuery(id+"F0.wireOp",EDGE,"E14.32.1");var subQ1=sQuery(id+"F0.wireOp",EDGE,"E14.21.0");var subQ2=makeQuery(id+"F0.imprint","INTERSECT",VERTEX,{"derivedFrom":[subQ1,subQ0]});Q639=makeQuery(id+"F0.imprint","IMPRINT",FACE,{"disambiguationData":[TD([[makeQuery(id+"F0.imprint","IMPRINT",EDGE,{"disambiguationData":[TD([[subQ2,-1.0]])],"derivedFrom":subQ1}),-1.0]])]});}
            var Q640;
            {var subQ0=sQuery(id+"F0.wireOp",EDGE,"E14.15.1");var subQ1=sQuery(id+"F0.wireOp",EDGE,"E14.3.0");var subQ2=makeQuery(id+"F0.imprint","INTERSECT",VERTEX,{"derivedFrom":[subQ1,subQ0]});Q640=makeQuery(id+"F0.imprint","IMPRINT",FACE,{"disambiguationData":[TD([[makeQuery(id+"F0.imprint","IMPRINT",EDGE,{"disambiguationData":[TD([[subQ2,-1.0]])],"derivedFrom":subQ1}),-1.0]])]});}
            var Q641;
            {var subQ0=sQuery(id+"F0.wireOp",EDGE,"E14.30.0");var subQ1=sQuery(id+"F0.wireOp",EDGE,"E14.7.1");var subQ2=makeQuery(id+"F0.imprint","INTERSECT",VERTEX,{"derivedFrom":[subQ1,subQ0]});Q641=makeQuery(id+"F0.imprint","IMPRINT",FACE,{"disambiguationData":[TD([[makeQuery(id+"F0.imprint","IMPRINT",EDGE,{"disambiguationData":[TD([[subQ2,-1.0]])],"derivedFrom":subQ1}),-1.0]])]});}
            var Q642;
            {var subQ0=sQuery(id+"F0.wireOp",EDGE,"E14.18.1");var subQ1=sQuery(id+"F0.wireOp",EDGE,"E14.6.0");var subQ2=makeQuery(id+"F0.imprint","INTERSECT",VERTEX,{"derivedFrom":[subQ1,subQ0]});Q642=makeQuery(id+"F0.imprint","IMPRINT",FACE,{"disambiguationData":[TD([[makeQuery(id+"F0.imprint","IMPRINT",EDGE,{"disambiguationData":[TD([[subQ2,-1.0]])],"derivedFrom":subQ1}),-1.0]])]});}
            var Q643;
            {var subQ0=sQuery(id+"F0.wireOp",EDGE,"E14.19.1");var subQ1=sQuery(id+"F0.wireOp",EDGE,"E14.5.0");var subQ2=makeQuery(id+"F0.imprint","INTERSECT",VERTEX,{"derivedFrom":[subQ1,subQ0]});Q643=makeQuery(id+"F0.imprint","IMPRINT",FACE,{"disambiguationData":[TD([[makeQuery(id+"F0.imprint","IMPRINT",EDGE,{"disambiguationData":[TD([[subQ2,-1.0]])],"derivedFrom":subQ1}),-1.0]])]});}
            var Q644;
            {var subQ0=sQuery(id+"F0.wireOp",EDGE,"E14.25.1");var subQ1=sQuery(id+"F0.wireOp",EDGE,"E14.11.0");var subQ2=makeQuery(id+"F0.imprint","INTERSECT",VERTEX,{"derivedFrom":[subQ1,subQ0]});Q644=makeQuery(id+"F0.imprint","IMPRINT",FACE,{"disambiguationData":[TD([[makeQuery(id+"F0.imprint","IMPRINT",EDGE,{"disambiguationData":[TD([[subQ2,-1.0]])],"derivedFrom":subQ1}),-1.0]])]});}
            var Q645;
            {var subQ0=sQuery(id+"F0.wireOp",EDGE,"E14.26.0");var subQ1=sQuery(id+"F0.wireOp",EDGE,"E14.3.1");var subQ2=makeQuery(id+"F0.imprint","INTERSECT",VERTEX,{"derivedFrom":[subQ1,subQ0]});Q645=makeQuery(id+"F0.imprint","IMPRINT",FACE,{"disambiguationData":[TD([[makeQuery(id+"F0.imprint","IMPRINT",EDGE,{"disambiguationData":[TD([[subQ2,-1.0]])],"derivedFrom":subQ1}),-1.0]])]});}
            var Q646;
            {var subQ0=sQuery(id+"F0.wireOp",EDGE,"E14.11.1");var subQ1=sQuery(id+"F0.wireOp",EDGE,"E9.right");var subQ2=makeQuery(id+"F0.imprint","INTERSECT",VERTEX,{"derivedFrom":[subQ1,subQ0]});Q646=makeQuery(id+"F0.imprint","IMPRINT",FACE,{"disambiguationData":[TD([[makeQuery(id+"F0.imprint","IMPRINT",EDGE,{"disambiguationData":[TD([[subQ2,-1.0]])],"derivedFrom":subQ1}),1.0]])]});}
            var Q647;
            {var subQ0=sQuery(id+"F0.wireOp",EDGE,"E14.32.0");var subQ1=sQuery(id+"F0.wireOp",EDGE,"E14.11.1");var subQ2=makeQuery(id+"F0.imprint","INTERSECT",VERTEX,{"derivedFrom":[subQ1,subQ0]});Q647=makeQuery(id+"F0.imprint","IMPRINT",FACE,{"disambiguationData":[TD([[makeQuery(id+"F0.imprint","IMPRINT",EDGE,{"disambiguationData":[TD([[subQ2,-1.0]])],"derivedFrom":subQ1}),-1.0]])]});}
            var Q648;
            {var subQ0=sQuery(id+"F0.wireOp",EDGE,"E14.34.1");var subQ1=sQuery(id+"F0.wireOp",EDGE,"E14.19.0");var subQ2=makeQuery(id+"F0.imprint","INTERSECT",VERTEX,{"derivedFrom":[subQ1,subQ0]});Q648=makeQuery(id+"F0.imprint","IMPRINT",FACE,{"disambiguationData":[TD([[makeQuery(id+"F0.imprint","IMPRINT",EDGE,{"disambiguationData":[TD([[subQ2,-1.0]])],"derivedFrom":subQ1}),-1.0]])]});}
            var Q649;
            {var subQ0=sQuery(id+"F0.wireOp",EDGE,"E14.14.1");var subQ1=sQuery(id+"F0.wireOp",EDGE,"E14.2.0");var subQ2=makeQuery(id+"F0.imprint","INTERSECT",VERTEX,{"derivedFrom":[subQ1,subQ0]});Q649=makeQuery(id+"F0.imprint","IMPRINT",FACE,{"disambiguationData":[TD([[makeQuery(id+"F0.imprint","IMPRINT",EDGE,{"disambiguationData":[TD([[subQ2,-1.0]])],"derivedFrom":subQ1}),-1.0]])]});}
            var Q650;
            {var subQ0=sQuery(id+"F0.wireOp",EDGE,"E14.31.0");var subQ1=sQuery(id+"F0.wireOp",EDGE,"E14.11.1");var subQ2=makeQuery(id+"F0.imprint","INTERSECT",VERTEX,{"derivedFrom":[subQ1,subQ0]});Q650=makeQuery(id+"F0.imprint","IMPRINT",FACE,{"disambiguationData":[TD([[makeQuery(id+"F0.imprint","IMPRINT",EDGE,{"disambiguationData":[TD([[subQ2,-1.0]])],"derivedFrom":subQ1}),-1.0]])]});}
            var Q651;
            {var subQ0=sQuery(id+"F0.wireOp",EDGE,"E14.16.1");var subQ1=sQuery(id+"F0.wireOp",EDGE,"E14.4.0");var subQ2=makeQuery(id+"F0.imprint","INTERSECT",VERTEX,{"derivedFrom":[subQ1,subQ0]});Q651=makeQuery(id+"F0.imprint","IMPRINT",FACE,{"disambiguationData":[TD([[makeQuery(id+"F0.imprint","IMPRINT",EDGE,{"disambiguationData":[TD([[subQ2,-1.0]])],"derivedFrom":subQ1}),-1.0]])]});}
            var Q652;
            {var subQ0=sQuery(id+"F0.wireOp",EDGE,"E14.32.1");var subQ1=sQuery(id+"F0.wireOp",EDGE,"E14.15.0");var subQ2=makeQuery(id+"F0.imprint","INTERSECT",VERTEX,{"derivedFrom":[subQ1,subQ0]});Q652=makeQuery(id+"F0.imprint","IMPRINT",FACE,{"disambiguationData":[TD([[makeQuery(id+"F0.imprint","IMPRINT",EDGE,{"disambiguationData":[TD([[subQ2,-1.0]])],"derivedFrom":subQ1}),-1.0]])]});}
            var Q653;
            {var subQ0=sQuery(id+"F0.wireOp",EDGE,"E14.20.1");var subQ1=sQuery(id+"F0.wireOp",EDGE,"E14.3.0");var subQ2=makeQuery(id+"F0.imprint","INTERSECT",VERTEX,{"derivedFrom":[subQ1,subQ0]});Q653=makeQuery(id+"F0.imprint","IMPRINT",FACE,{"disambiguationData":[TD([[makeQuery(id+"F0.imprint","IMPRINT",EDGE,{"disambiguationData":[TD([[subQ2,-1.0]])],"derivedFrom":subQ1}),-1.0]])]});}
            var Q654;
            {var subQ0=sQuery(id+"F0.wireOp",EDGE,"E14.33.1");var subQ1=sQuery(id+"F0.wireOp",EDGE,"E14.20.0");var subQ2=makeQuery(id+"F0.imprint","INTERSECT",VERTEX,{"derivedFrom":[subQ1,subQ0]});Q654=makeQuery(id+"F0.imprint","IMPRINT",FACE,{"disambiguationData":[TD([[makeQuery(id+"F0.imprint","IMPRINT",EDGE,{"disambiguationData":[TD([[subQ2,-1.0]])],"derivedFrom":subQ1}),-1.0]])]});}
            var Q655;
            {var subQ0=sQuery(id+"F0.wireOp",EDGE,"E14.25.1");var subQ1=sQuery(id+"F0.wireOp",EDGE,"E14.12.0");var subQ2=makeQuery(id+"F0.imprint","INTERSECT",VERTEX,{"derivedFrom":[subQ1,subQ0]});Q655=makeQuery(id+"F0.imprint","IMPRINT",FACE,{"disambiguationData":[TD([[makeQuery(id+"F0.imprint","IMPRINT",EDGE,{"disambiguationData":[TD([[subQ2,-1.0]])],"derivedFrom":subQ1}),-1.0]])]});}
            var Q656;
            {var subQ0=sQuery(id+"F0.wireOp",EDGE,"E14.29.1");var subQ1=sQuery(id+"F0.wireOp",EDGE,"E14.14.0");var subQ2=makeQuery(id+"F0.imprint","INTERSECT",VERTEX,{"derivedFrom":[subQ1,subQ0]});Q656=makeQuery(id+"F0.imprint","IMPRINT",FACE,{"disambiguationData":[TD([[makeQuery(id+"F0.imprint","IMPRINT",EDGE,{"disambiguationData":[TD([[subQ2,-1.0]])],"derivedFrom":subQ1}),-1.0]])]});}
            var Q657;
            {var subQ0=sQuery(id+"F0.wireOp",EDGE,"E14.30.0");var subQ1=sQuery(id+"F0.wireOp",EDGE,"E14.8.1");var subQ2=makeQuery(id+"F0.imprint","INTERSECT",VERTEX,{"derivedFrom":[subQ1,subQ0]});Q657=makeQuery(id+"F0.imprint","IMPRINT",FACE,{"disambiguationData":[TD([[makeQuery(id+"F0.imprint","IMPRINT",EDGE,{"disambiguationData":[TD([[subQ2,-1.0]])],"derivedFrom":subQ1}),-1.0]])]});}
            var Q658;
            {var subQ0=sQuery(id+"F0.wireOp",EDGE,"E14.17.1");var subQ1=sQuery(id+"F0.wireOp",EDGE,"E14.4.0");var subQ2=makeQuery(id+"F0.imprint","INTERSECT",VERTEX,{"derivedFrom":[subQ1,subQ0]});Q658=makeQuery(id+"F0.imprint","IMPRINT",FACE,{"disambiguationData":[TD([[makeQuery(id+"F0.imprint","IMPRINT",EDGE,{"disambiguationData":[TD([[subQ2,-1.0]])],"derivedFrom":subQ1}),-1.0]])]});}
            var Q659;
            {var subQ0=sQuery(id+"F0.wireOp",EDGE,"E14.28.1");var subQ1=sQuery(id+"F0.wireOp",EDGE,"E14.15.0");var subQ2=makeQuery(id+"F0.imprint","INTERSECT",VERTEX,{"derivedFrom":[subQ1,subQ0]});Q659=makeQuery(id+"F0.imprint","IMPRINT",FACE,{"disambiguationData":[TD([[makeQuery(id+"F0.imprint","IMPRINT",EDGE,{"disambiguationData":[TD([[subQ2,-1.0]])],"derivedFrom":subQ1}),-1.0]])]});}
            var Q660;
            {var subQ0=sQuery(id+"F0.wireOp",EDGE,"E14.22.1");var subQ1=sQuery(id+"F0.wireOp",EDGE,"E14.5.0");var subQ2=makeQuery(id+"F0.imprint","INTERSECT",VERTEX,{"derivedFrom":[subQ1,subQ0]});Q660=makeQuery(id+"F0.imprint","IMPRINT",FACE,{"disambiguationData":[TD([[makeQuery(id+"F0.imprint","IMPRINT",EDGE,{"disambiguationData":[TD([[subQ2,-1.0]])],"derivedFrom":subQ1}),-1.0]])]});}
            var Q661;
            {var subQ0=sQuery(id+"F0.wireOp",EDGE,"E14.22.0");var subQ1=sQuery(id+"F0.wireOp",EDGE,"E14.3.1");var subQ2=makeQuery(id+"F0.imprint","INTERSECT",VERTEX,{"derivedFrom":[subQ1,subQ0]});Q661=makeQuery(id+"F0.imprint","IMPRINT",FACE,{"disambiguationData":[TD([[makeQuery(id+"F0.imprint","IMPRINT",EDGE,{"disambiguationData":[TD([[subQ2,-1.0]])],"derivedFrom":subQ1}),-1.0]])]});}
            var Q662;
            {var subQ0=sQuery(id+"F0.wireOp",EDGE,"E14.21.0");var subQ1=sQuery(id+"F0.wireOp",EDGE,"E9.left");var subQ2=makeQuery(id+"F0.imprint","INTERSECT",VERTEX,{"derivedFrom":[subQ1,subQ0]});Q662=makeQuery(id+"F0.imprint","IMPRINT",FACE,{"disambiguationData":[TD([[makeQuery(id+"F0.imprint","IMPRINT",EDGE,{"disambiguationData":[TD([[subQ2,-1.0]])],"derivedFrom":subQ1}),1.0]])]});}
            var Q663;
            {var subQ0=sQuery(id+"F0.wireOp",EDGE,"E14.21.1");var subQ1=sQuery(id+"F0.wireOp",EDGE,"E14.5.0");var subQ2=makeQuery(id+"F0.imprint","INTERSECT",VERTEX,{"derivedFrom":[subQ1,subQ0]});Q663=makeQuery(id+"F0.imprint","IMPRINT",FACE,{"disambiguationData":[TD([[makeQuery(id+"F0.imprint","IMPRINT",EDGE,{"disambiguationData":[TD([[subQ2,-1.0]])],"derivedFrom":subQ1}),-1.0]])]});}
            var Q664;
            {var subQ0=sQuery(id+"F0.wireOp",EDGE,"E14.27.0");var subQ1=sQuery(id+"F0.wireOp",EDGE,"E14.2.1");var subQ2=makeQuery(id+"F0.imprint","INTERSECT",VERTEX,{"derivedFrom":[subQ1,subQ0]});Q664=makeQuery(id+"F0.imprint","IMPRINT",FACE,{"disambiguationData":[TD([[makeQuery(id+"F0.imprint","IMPRINT",EDGE,{"disambiguationData":[TD([[subQ2,-1.0]])],"derivedFrom":subQ1}),-1.0]])]});}
            var Q665;
            {var subQ0=sQuery(id+"F0.wireOp",EDGE,"E14.22.1");var subQ1=sQuery(id+"F0.wireOp",EDGE,"E14.8.0");var subQ2=makeQuery(id+"F0.imprint","INTERSECT",VERTEX,{"derivedFrom":[subQ1,subQ0]});Q665=makeQuery(id+"F0.imprint","IMPRINT",FACE,{"disambiguationData":[TD([[makeQuery(id+"F0.imprint","IMPRINT",EDGE,{"disambiguationData":[TD([[subQ2,-1.0]])],"derivedFrom":subQ1}),-1.0]])]});}
            var Q666;
            {var subQ1=sQuery(id+"F0.wireOp",EDGE,"E9.left");var subQ3=sQuery(id+"F0.wireOp",EDGE,"E14.19.0");var subQ4=makeQuery(id+"F0.imprint","INTERSECT",VERTEX,{"derivedFrom":[subQ1,subQ3]});Q666=makeQuery(id+"F0.imprint","IMPRINT",FACE,{"disambiguationData":[TD([[makeQuery(id+"F0.imprint","IMPRINT",EDGE,{"disambiguationData":[TD([[subQ4,-1.0]])],"derivedFrom":subQ3}),1.0]])]});}
            var Q667;
            {var subQ0=sQuery(id+"F0.wireOp",EDGE,"E14.33.1");var subQ1=sQuery(id+"F0.wireOp",EDGE,"E14.19.0");var subQ2=makeQuery(id+"F0.imprint","INTERSECT",VERTEX,{"derivedFrom":[subQ1,subQ0]});Q667=makeQuery(id+"F0.imprint","IMPRINT",FACE,{"disambiguationData":[TD([[makeQuery(id+"F0.imprint","IMPRINT",EDGE,{"disambiguationData":[TD([[subQ2,-1.0]])],"derivedFrom":subQ1}),-1.0]])]});}
            var Q668;
            {var subQ0=sQuery(id+"F0.wireOp",EDGE,"E14.27.0");var subQ1=sQuery(id+"F0.wireOp",EDGE,"E14.7.1");var subQ2=makeQuery(id+"F0.imprint","INTERSECT",VERTEX,{"derivedFrom":[subQ1,subQ0]});Q668=makeQuery(id+"F0.imprint","IMPRINT",FACE,{"disambiguationData":[TD([[makeQuery(id+"F0.imprint","IMPRINT",EDGE,{"disambiguationData":[TD([[subQ2,-1.0]])],"derivedFrom":subQ1}),-1.0]])]});}
            var Q669;
            {var subQ0=sQuery(id+"F0.wireOp",EDGE,"E14.12.1");var subQ1=sQuery(id+"F0.wireOp",EDGE,"E9.right");var subQ2=makeQuery(id+"F0.imprint","INTERSECT",VERTEX,{"derivedFrom":[subQ1,subQ0]});Q669=makeQuery(id+"F0.imprint","IMPRINT",FACE,{"disambiguationData":[TD([[makeQuery(id+"F0.imprint","IMPRINT",EDGE,{"disambiguationData":[TD([[subQ2,-1.0]])],"derivedFrom":subQ1}),1.0]])]});}
            var Q670;
            {var subQ0=sQuery(id+"F0.wireOp",EDGE,"E14.24.1");var subQ1=sQuery(id+"F0.wireOp",EDGE,"E14.11.0");var subQ2=makeQuery(id+"F0.imprint","INTERSECT",VERTEX,{"derivedFrom":[subQ1,subQ0]});Q670=makeQuery(id+"F0.imprint","IMPRINT",FACE,{"disambiguationData":[TD([[makeQuery(id+"F0.imprint","IMPRINT",EDGE,{"disambiguationData":[TD([[subQ2,-1.0]])],"derivedFrom":subQ1}),-1.0]])]});}
            var Q671;
            {var subQ0=sQuery(id+"F0.wireOp",EDGE,"E14.13.1");var subQ1=sQuery(id+"F0.wireOp",EDGE,"E14.3.0");var subQ2=makeQuery(id+"F0.imprint","INTERSECT",VERTEX,{"derivedFrom":[subQ1,subQ0]});Q671=makeQuery(id+"F0.imprint","IMPRINT",FACE,{"disambiguationData":[TD([[makeQuery(id+"F0.imprint","IMPRINT",EDGE,{"disambiguationData":[TD([[subQ2,-1.0]])],"derivedFrom":subQ1}),-1.0]])]});}
            var Q672;
            {var subQ0=sQuery(id+"F0.wireOp",EDGE,"E14.15.1");var subQ1=sQuery(id+"F0.wireOp",EDGE,"E14.2.0");var subQ2=makeQuery(id+"F0.imprint","INTERSECT",VERTEX,{"derivedFrom":[subQ1,subQ0]});Q672=makeQuery(id+"F0.imprint","IMPRINT",FACE,{"disambiguationData":[TD([[makeQuery(id+"F0.imprint","IMPRINT",EDGE,{"disambiguationData":[TD([[subQ2,-1.0]])],"derivedFrom":subQ1}),-1.0]])]});}
            var Q673;
            {var subQ0=sQuery(id+"F0.wireOp",EDGE,"E14.23.0");var subQ1=sQuery(id+"F0.wireOp",EDGE,"E14.4.1");var subQ2=makeQuery(id+"F0.imprint","INTERSECT",VERTEX,{"derivedFrom":[subQ1,subQ0]});Q673=makeQuery(id+"F0.imprint","IMPRINT",FACE,{"disambiguationData":[TD([[makeQuery(id+"F0.imprint","IMPRINT",EDGE,{"disambiguationData":[TD([[subQ2,-1.0]])],"derivedFrom":subQ1}),-1.0]])]});}
            var Q674;
            {var subQ0=sQuery(id+"F0.wireOp",EDGE,"E14.14.1");var subQ1=sQuery(id+"F0.wireOp",EDGE,"E14.1.0");var subQ2=makeQuery(id+"F0.imprint","INTERSECT",VERTEX,{"derivedFrom":[subQ1,subQ0]});Q674=makeQuery(id+"F0.imprint","IMPRINT",FACE,{"disambiguationData":[TD([[makeQuery(id+"F0.imprint","IMPRINT",EDGE,{"disambiguationData":[TD([[subQ2,-1.0]])],"derivedFrom":subQ1}),-1.0]])]});}
            var Q675;
            {var subQ0=sQuery(id+"F0.wireOp",EDGE,"E14.16.1");var subQ1=sQuery(id+"F0.wireOp",EDGE,"E14.3.0");var subQ2=makeQuery(id+"F0.imprint","INTERSECT",VERTEX,{"derivedFrom":[subQ1,subQ0]});Q675=makeQuery(id+"F0.imprint","IMPRINT",FACE,{"disambiguationData":[TD([[makeQuery(id+"F0.imprint","IMPRINT",EDGE,{"disambiguationData":[TD([[subQ2,-1.0]])],"derivedFrom":subQ1}),-1.0]])]});}
            var Q676;
            {var subQ0=sQuery(id+"F0.wireOp",EDGE,"E14.26.1");var subQ1=sQuery(id+"F0.wireOp",EDGE,"E14.12.0");var subQ2=makeQuery(id+"F0.imprint","INTERSECT",VERTEX,{"derivedFrom":[subQ1,subQ0]});Q676=makeQuery(id+"F0.imprint","IMPRINT",FACE,{"disambiguationData":[TD([[makeQuery(id+"F0.imprint","IMPRINT",EDGE,{"disambiguationData":[TD([[subQ2,-1.0]])],"derivedFrom":subQ1}),-1.0]])]});}
            var Q677;
            {var subQ0=sQuery(id+"F0.wireOp",EDGE,"E14.19.1");var subQ1=sQuery(id+"F0.wireOp",EDGE,"E14.2.0");var subQ2=makeQuery(id+"F0.imprint","INTERSECT",VERTEX,{"derivedFrom":[subQ1,subQ0]});Q677=makeQuery(id+"F0.imprint","IMPRINT",FACE,{"disambiguationData":[TD([[makeQuery(id+"F0.imprint","IMPRINT",EDGE,{"disambiguationData":[TD([[subQ2,-1.0]])],"derivedFrom":subQ1}),-1.0]])]});}
            var Q678;
            {var subQ0=sQuery(id+"F0.wireOp",EDGE,"E14.19.0");var subQ1=sQuery(id+"F0.wireOp",EDGE,"E9.left");var subQ2=makeQuery(id+"F0.imprint","INTERSECT",VERTEX,{"derivedFrom":[subQ1,subQ0]});Q678=makeQuery(id+"F0.imprint","IMPRINT",FACE,{"disambiguationData":[TD([[makeQuery(id+"F0.imprint","IMPRINT",EDGE,{"disambiguationData":[TD([[subQ2,-1.0]])],"derivedFrom":subQ1}),1.0]])]});}
            var Q679;
            {var subQ0=sQuery(id+"F0.wireOp",EDGE,"E14.34.1");var subQ1=sQuery(id+"F0.wireOp",EDGE,"E14.16.0");var subQ2=makeQuery(id+"F0.imprint","INTERSECT",VERTEX,{"derivedFrom":[subQ1,subQ0]});Q679=makeQuery(id+"F0.imprint","IMPRINT",FACE,{"disambiguationData":[TD([[makeQuery(id+"F0.imprint","IMPRINT",EDGE,{"disambiguationData":[TD([[subQ2,-1.0]])],"derivedFrom":subQ1}),-1.0]])]});}
            var Q680;
            {var subQ0=sQuery(id+"F0.wireOp",EDGE,"E14.21.0");var subQ1=sQuery(id+"F0.wireOp",EDGE,"E9.left");var subQ2=makeQuery(id+"F0.imprint","INTERSECT",VERTEX,{"derivedFrom":[subQ1,subQ0]});Q680=makeQuery(id+"F0.imprint","IMPRINT",FACE,{"disambiguationData":[TD([[makeQuery(id+"F0.imprint","IMPRINT",EDGE,{"disambiguationData":[TD([[subQ2,-1.0]])],"derivedFrom":subQ1}),-1.0]])]});}
            var Q681;
            {var subQ0=sQuery(id+"F0.wireOp",EDGE,"E14.24.0");var subQ1=sQuery(id+"F0.wireOp",EDGE,"E14.2.1");var subQ2=makeQuery(id+"F0.imprint","INTERSECT",VERTEX,{"derivedFrom":[subQ1,subQ0]});Q681=makeQuery(id+"F0.imprint","IMPRINT",FACE,{"disambiguationData":[TD([[makeQuery(id+"F0.imprint","IMPRINT",EDGE,{"disambiguationData":[TD([[subQ2,-1.0]])],"derivedFrom":subQ1}),-1.0]])]});}
            var Q682;
            {var subQ0=sQuery(id+"F0.wireOp",EDGE,"E14.12.1");var subQ1=sQuery(id+"F0.wireOp",EDGE,"E9.right");var subQ2=makeQuery(id+"F0.imprint","INTERSECT",VERTEX,{"derivedFrom":[subQ1,subQ0]});Q682=makeQuery(id+"F0.imprint","IMPRINT",FACE,{"disambiguationData":[TD([[makeQuery(id+"F0.imprint","IMPRINT",EDGE,{"disambiguationData":[TD([[subQ2,-1.0]])],"derivedFrom":subQ1}),-1.0]])]});}
            var Q683;
            {var subQ0=sQuery(id+"F0.wireOp",EDGE,"E14.24.1");var subQ1=sQuery(id+"F0.wireOp",EDGE,"E14.7.0");var subQ2=makeQuery(id+"F0.imprint","INTERSECT",VERTEX,{"derivedFrom":[subQ1,subQ0]});Q683=makeQuery(id+"F0.imprint","IMPRINT",FACE,{"disambiguationData":[TD([[makeQuery(id+"F0.imprint","IMPRINT",EDGE,{"disambiguationData":[TD([[subQ2,-1.0]])],"derivedFrom":subQ1}),-1.0]])]});}
            var Q684;
            {var subQ0=sQuery(id+"F0.wireOp",EDGE,"E14.18.1");var subQ1=sQuery(id+"F0.wireOp",EDGE,"E14.4.0");var subQ2=makeQuery(id+"F0.imprint","INTERSECT",VERTEX,{"derivedFrom":[subQ1,subQ0]});Q684=makeQuery(id+"F0.imprint","IMPRINT",FACE,{"disambiguationData":[TD([[makeQuery(id+"F0.imprint","IMPRINT",EDGE,{"disambiguationData":[TD([[subQ2,-1.0]])],"derivedFrom":subQ1}),-1.0]])]});}
            var Q685;
            {var subQ0=sQuery(id+"F0.wireOp",EDGE,"E14.31.0");var subQ1=sQuery(id+"F0.wireOp",EDGE,"E14.12.1");var subQ2=makeQuery(id+"F0.imprint","INTERSECT",VERTEX,{"derivedFrom":[subQ1,subQ0]});Q685=makeQuery(id+"F0.imprint","IMPRINT",FACE,{"disambiguationData":[TD([[makeQuery(id+"F0.imprint","IMPRINT",EDGE,{"disambiguationData":[TD([[subQ2,-1.0]])],"derivedFrom":subQ1}),-1.0]])]});}
            var Q686;
            {var subQ0=sQuery(id+"F0.wireOp",EDGE,"E14.28.0");var subQ1=sQuery(id+"F0.wireOp",EDGE,"E14.5.1");var subQ2=makeQuery(id+"F0.imprint","INTERSECT",VERTEX,{"derivedFrom":[subQ1,subQ0]});Q686=makeQuery(id+"F0.imprint","IMPRINT",FACE,{"disambiguationData":[TD([[makeQuery(id+"F0.imprint","IMPRINT",EDGE,{"disambiguationData":[TD([[subQ2,-1.0]])],"derivedFrom":subQ1}),-1.0]])]});}
            var Q687;
            {var subQ0=sQuery(id+"F0.wireOp",EDGE,"E14.28.1");var subQ1=sQuery(id+"F0.wireOp",EDGE,"E14.16.0");var subQ2=makeQuery(id+"F0.imprint","INTERSECT",VERTEX,{"derivedFrom":[subQ1,subQ0]});Q687=makeQuery(id+"F0.imprint","IMPRINT",FACE,{"disambiguationData":[TD([[makeQuery(id+"F0.imprint","IMPRINT",EDGE,{"disambiguationData":[TD([[subQ2,-1.0]])],"derivedFrom":subQ1}),-1.0]])]});}
            var Q688;
            {var subQ0=sQuery(id+"F0.wireOp",EDGE,"E14.19.1");var subQ1=sQuery(id+"F0.wireOp",EDGE,"E14.4.0");var subQ2=makeQuery(id+"F0.imprint","INTERSECT",VERTEX,{"derivedFrom":[subQ1,subQ0]});Q688=makeQuery(id+"F0.imprint","IMPRINT",FACE,{"disambiguationData":[TD([[makeQuery(id+"F0.imprint","IMPRINT",EDGE,{"disambiguationData":[TD([[subQ2,-1.0]])],"derivedFrom":subQ1}),-1.0]])]});}
            var Q689;
            {var subQ0=sQuery(id+"F0.wireOp",EDGE,"E14.31.1");var subQ1=sQuery(id+"F0.wireOp",EDGE,"E14.15.0");var subQ2=makeQuery(id+"F0.imprint","INTERSECT",VERTEX,{"derivedFrom":[subQ1,subQ0]});Q689=makeQuery(id+"F0.imprint","IMPRINT",FACE,{"disambiguationData":[TD([[makeQuery(id+"F0.imprint","IMPRINT",EDGE,{"disambiguationData":[TD([[subQ2,-1.0]])],"derivedFrom":subQ1}),-1.0]])]});}
            var Q690;
            {var subQ0=sQuery(id+"F0.wireOp",EDGE,"E14.28.1");var subQ1=sQuery(id+"F0.wireOp",EDGE,"E14.13.0");var subQ2=makeQuery(id+"F0.imprint","INTERSECT",VERTEX,{"derivedFrom":[subQ1,subQ0]});Q690=makeQuery(id+"F0.imprint","IMPRINT",FACE,{"disambiguationData":[TD([[makeQuery(id+"F0.imprint","IMPRINT",EDGE,{"disambiguationData":[TD([[subQ2,-1.0]])],"derivedFrom":subQ1}),-1.0]])]});}
            var Q691;
            {var subQ0=sQuery(id+"F0.wireOp",EDGE,"E14.24.1");var subQ1=sQuery(id+"F0.wireOp",EDGE,"E14.9.0");var subQ2=makeQuery(id+"F0.imprint","INTERSECT",VERTEX,{"derivedFrom":[subQ1,subQ0]});Q691=makeQuery(id+"F0.imprint","IMPRINT",FACE,{"disambiguationData":[TD([[makeQuery(id+"F0.imprint","IMPRINT",EDGE,{"disambiguationData":[TD([[subQ2,-1.0]])],"derivedFrom":subQ1}),-1.0]])]});}
            var Q692;
            {var subQ0=sQuery(id+"F0.wireOp",EDGE,"E14.18.1");var subQ1=sQuery(id+"F0.wireOp",EDGE,"E14.3.0");var subQ2=makeQuery(id+"F0.imprint","INTERSECT",VERTEX,{"derivedFrom":[subQ1,subQ0]});Q692=makeQuery(id+"F0.imprint","IMPRINT",FACE,{"disambiguationData":[TD([[makeQuery(id+"F0.imprint","IMPRINT",EDGE,{"disambiguationData":[TD([[subQ2,-1.0]])],"derivedFrom":subQ1}),-1.0]])]});}
            var Q693;
            {var subQ0=sQuery(id+"F0.wireOp",EDGE,"E14.32.1");var subQ1=sQuery(id+"F0.wireOp",EDGE,"E14.17.0");var subQ2=makeQuery(id+"F0.imprint","INTERSECT",VERTEX,{"derivedFrom":[subQ1,subQ0]});Q693=makeQuery(id+"F0.imprint","IMPRINT",FACE,{"disambiguationData":[TD([[makeQuery(id+"F0.imprint","IMPRINT",EDGE,{"disambiguationData":[TD([[subQ2,-1.0]])],"derivedFrom":subQ1}),-1.0]])]});}
            var Q694;
            {var subQ0=sQuery(id+"F0.wireOp",EDGE,"E14.25.0");var subQ1=sQuery(id+"F0.wireOp",EDGE,"E14.5.1");var subQ2=makeQuery(id+"F0.imprint","INTERSECT",VERTEX,{"derivedFrom":[subQ1,subQ0]});Q694=makeQuery(id+"F0.imprint","IMPRINT",FACE,{"disambiguationData":[TD([[makeQuery(id+"F0.imprint","IMPRINT",EDGE,{"disambiguationData":[TD([[subQ2,-1.0]])],"derivedFrom":subQ1}),-1.0]])]});}
            var Q695;
            {var subQ0=sQuery(id+"F0.wireOp",EDGE,"E14.14.1");var subQ1=sQuery(id+"F0.wireOp",EDGE,"E9.right");var subQ2=makeQuery(id+"F0.imprint","INTERSECT",VERTEX,{"derivedFrom":[subQ1,subQ0]});Q695=makeQuery(id+"F0.imprint","IMPRINT",FACE,{"disambiguationData":[TD([[makeQuery(id+"F0.imprint","IMPRINT",EDGE,{"disambiguationData":[TD([[subQ2,-1.0]])],"derivedFrom":subQ1}),-1.0]])]});}
            var Q696;
            {var subQ0=sQuery(id+"F0.wireOp",EDGE,"E14.32.0");var subQ1=sQuery(id+"F0.wireOp",EDGE,"E14.10.1");var subQ2=makeQuery(id+"F0.imprint","INTERSECT",VERTEX,{"derivedFrom":[subQ1,subQ0]});Q696=makeQuery(id+"F0.imprint","IMPRINT",FACE,{"disambiguationData":[TD([[makeQuery(id+"F0.imprint","IMPRINT",EDGE,{"disambiguationData":[TD([[subQ2,-1.0]])],"derivedFrom":subQ1}),-1.0]])]});}
            var Q697;
            {var subQ0=sQuery(id+"F0.wireOp",EDGE,"E14.27.1");var subQ1=sQuery(id+"F0.wireOp",EDGE,"E14.12.0");var subQ2=makeQuery(id+"F0.imprint","INTERSECT",VERTEX,{"derivedFrom":[subQ1,subQ0]});Q697=makeQuery(id+"F0.imprint","IMPRINT",FACE,{"disambiguationData":[TD([[makeQuery(id+"F0.imprint","IMPRINT",EDGE,{"disambiguationData":[TD([[subQ2,-1.0]])],"derivedFrom":subQ1}),-1.0]])]});}
            var Q698;
            {var subQ0=sQuery(id+"F0.wireOp",EDGE,"E14.23.0");var subQ1=sQuery(id+"F0.wireOp",EDGE,"E14.3.1");var subQ2=makeQuery(id+"F0.imprint","INTERSECT",VERTEX,{"derivedFrom":[subQ1,subQ0]});Q698=makeQuery(id+"F0.imprint","IMPRINT",FACE,{"disambiguationData":[TD([[makeQuery(id+"F0.imprint","IMPRINT",EDGE,{"disambiguationData":[TD([[subQ2,-1.0]])],"derivedFrom":subQ1}),-1.0]])]});}
            var Q699;
            {var subQ0=sQuery(id+"F0.wireOp",EDGE,"E14.29.1");var subQ1=sQuery(id+"F0.wireOp",EDGE,"E14.13.0");var subQ2=makeQuery(id+"F0.imprint","INTERSECT",VERTEX,{"derivedFrom":[subQ1,subQ0]});Q699=makeQuery(id+"F0.imprint","IMPRINT",FACE,{"disambiguationData":[TD([[makeQuery(id+"F0.imprint","IMPRINT",EDGE,{"disambiguationData":[TD([[subQ2,-1.0]])],"derivedFrom":subQ1}),-1.0]])]});}
            var Q700;
            {var subQ0=sQuery(id+"F0.wireOp",EDGE,"E14.28.0");var subQ1=sQuery(id+"F0.wireOp",EDGE,"E14.4.1");var subQ2=makeQuery(id+"F0.imprint","INTERSECT",VERTEX,{"derivedFrom":[subQ1,subQ0]});Q700=makeQuery(id+"F0.imprint","IMPRINT",FACE,{"disambiguationData":[TD([[makeQuery(id+"F0.imprint","IMPRINT",EDGE,{"disambiguationData":[TD([[subQ2,-1.0]])],"derivedFrom":subQ1}),-1.0]])]});}
            var Q701;
            {var subQ0=sQuery(id+"F0.wireOp",EDGE,"E14.26.1");var subQ1=sQuery(id+"F0.wireOp",EDGE,"E14.8.0");var subQ2=makeQuery(id+"F0.imprint","INTERSECT",VERTEX,{"derivedFrom":[subQ1,subQ0]});Q701=makeQuery(id+"F0.imprint","IMPRINT",FACE,{"disambiguationData":[TD([[makeQuery(id+"F0.imprint","IMPRINT",EDGE,{"disambiguationData":[TD([[subQ2,-1.0]])],"derivedFrom":subQ1}),-1.0]])]});}
            var Q702;
            {var subQ0=sQuery(id+"F0.wireOp",EDGE,"E14.17.1");var subQ1=sQuery(id+"F0.wireOp",EDGE,"E14.3.0");var subQ2=makeQuery(id+"F0.imprint","INTERSECT",VERTEX,{"derivedFrom":[subQ1,subQ0]});Q702=makeQuery(id+"F0.imprint","IMPRINT",FACE,{"disambiguationData":[TD([[makeQuery(id+"F0.imprint","IMPRINT",EDGE,{"disambiguationData":[TD([[subQ2,-1.0]])],"derivedFrom":subQ1}),-1.0]])]});}
            var Q703;
            {var subQ0=sQuery(id+"F0.wireOp",EDGE,"E14.33.1");var subQ1=sQuery(id+"F0.wireOp",EDGE,"E14.17.0");var subQ2=makeQuery(id+"F0.imprint","INTERSECT",VERTEX,{"derivedFrom":[subQ1,subQ0]});Q703=makeQuery(id+"F0.imprint","IMPRINT",FACE,{"disambiguationData":[TD([[makeQuery(id+"F0.imprint","IMPRINT",EDGE,{"disambiguationData":[TD([[subQ2,-1.0]])],"derivedFrom":subQ1}),-1.0]])]});}
            var Q704;
            {var subQ0=sQuery(id+"F0.wireOp",EDGE,"E14.20.0");var subQ1=sQuery(id+"F0.wireOp",EDGE,"E9.left");var subQ2=makeQuery(id+"F0.imprint","INTERSECT",VERTEX,{"derivedFrom":[subQ1,subQ0]});Q704=makeQuery(id+"F0.imprint","IMPRINT",FACE,{"disambiguationData":[TD([[makeQuery(id+"F0.imprint","IMPRINT",EDGE,{"disambiguationData":[TD([[subQ2,-1.0]])],"derivedFrom":subQ1}),-1.0]])]});}
            var Q705;
            {var subQ0=sQuery(id+"F0.wireOp",EDGE,"E14.29.1");var subQ1=sQuery(id+"F0.wireOp",EDGE,"E14.16.0");var subQ2=makeQuery(id+"F0.imprint","INTERSECT",VERTEX,{"derivedFrom":[subQ1,subQ0]});Q705=makeQuery(id+"F0.imprint","IMPRINT",FACE,{"disambiguationData":[TD([[makeQuery(id+"F0.imprint","IMPRINT",EDGE,{"disambiguationData":[TD([[subQ2,-1.0]])],"derivedFrom":subQ1}),-1.0]])]});}
            var Q706;
            {var subQ0=sQuery(id+"F0.wireOp",EDGE,"E14.20.1");var subQ1=sQuery(id+"F0.wireOp",EDGE,"E14.4.0");var subQ2=makeQuery(id+"F0.imprint","INTERSECT",VERTEX,{"derivedFrom":[subQ1,subQ0]});Q706=makeQuery(id+"F0.imprint","IMPRINT",FACE,{"disambiguationData":[TD([[makeQuery(id+"F0.imprint","IMPRINT",EDGE,{"disambiguationData":[TD([[subQ2,-1.0]])],"derivedFrom":subQ1}),-1.0]])]});}
            var Q707;
            {var subQ0=sQuery(id+"F0.wireOp",EDGE,"E14.13.1");var subQ1=sQuery(id+"F0.wireOp",EDGE,"E9.right");var subQ2=makeQuery(id+"F0.imprint","INTERSECT",VERTEX,{"derivedFrom":[subQ1,subQ0]});Q707=makeQuery(id+"F0.imprint","IMPRINT",FACE,{"disambiguationData":[TD([[makeQuery(id+"F0.imprint","IMPRINT",EDGE,{"disambiguationData":[TD([[subQ2,-1.0]])],"derivedFrom":subQ1}),1.0]])]});}
            var Q708;
            {var subQ0=sQuery(id+"F0.wireOp",EDGE,"E14.28.1");var subQ1=sQuery(id+"F0.wireOp",EDGE,"E14.12.0");var subQ2=makeQuery(id+"F0.imprint","INTERSECT",VERTEX,{"derivedFrom":[subQ1,subQ0]});Q708=makeQuery(id+"F0.imprint","IMPRINT",FACE,{"disambiguationData":[TD([[makeQuery(id+"F0.imprint","IMPRINT",EDGE,{"disambiguationData":[TD([[subQ2,-1.0]])],"derivedFrom":subQ1}),-1.0]])]});}
            var Q709;
            {var subQ0=sQuery(id+"F0.wireOp",EDGE,"E14.23.0");var subQ1=sQuery(id+"F0.wireOp",EDGE,"E14.2.1");var subQ2=makeQuery(id+"F0.imprint","INTERSECT",VERTEX,{"derivedFrom":[subQ1,subQ0]});Q709=makeQuery(id+"F0.imprint","IMPRINT",FACE,{"disambiguationData":[TD([[makeQuery(id+"F0.imprint","IMPRINT",EDGE,{"disambiguationData":[TD([[subQ2,-1.0]])],"derivedFrom":subQ1}),-1.0]])]});}
            var Q710;
            {var subQ0=sQuery(id+"F0.wireOp",EDGE,"E14.13.1");var subQ1=sQuery(id+"F0.wireOp",EDGE,"E9.right");var subQ2=makeQuery(id+"F0.imprint","INTERSECT",VERTEX,{"derivedFrom":[subQ1,subQ0]});Q710=makeQuery(id+"F0.imprint","IMPRINT",FACE,{"disambiguationData":[TD([[makeQuery(id+"F0.imprint","IMPRINT",EDGE,{"disambiguationData":[TD([[subQ2,-1.0]])],"derivedFrom":subQ1}),-1.0]])]});}
            var Q711;
            {var subQ0=sQuery(id+"F0.wireOp",EDGE,"E14.29.1");var subQ1=sQuery(id+"F0.wireOp",EDGE,"E14.12.0");var subQ2=makeQuery(id+"F0.imprint","INTERSECT",VERTEX,{"derivedFrom":[subQ1,subQ0]});Q711=makeQuery(id+"F0.imprint","IMPRINT",FACE,{"disambiguationData":[TD([[makeQuery(id+"F0.imprint","IMPRINT",EDGE,{"disambiguationData":[TD([[subQ2,-1.0]])],"derivedFrom":subQ1}),-1.0]])]});}
            var Q712;
            {var subQ0=sQuery(id+"F0.wireOp",EDGE,"E14.15.1");var subQ1=sQuery(id+"F0.wireOp",EDGE,"E9.right");var subQ2=makeQuery(id+"F0.imprint","INTERSECT",VERTEX,{"derivedFrom":[subQ1,subQ0]});Q712=makeQuery(id+"F0.imprint","IMPRINT",FACE,{"disambiguationData":[TD([[makeQuery(id+"F0.imprint","IMPRINT",EDGE,{"disambiguationData":[TD([[subQ2,-1.0]])],"derivedFrom":subQ1}),1.0]])]});}
            var Q713;
            {var subQ0=sQuery(id+"F0.wireOp",EDGE,"E14.26.0");var subQ1=sQuery(id+"F0.wireOp",EDGE,"E14.4.1");var subQ2=makeQuery(id+"F0.imprint","INTERSECT",VERTEX,{"derivedFrom":[subQ1,subQ0]});Q713=makeQuery(id+"F0.imprint","IMPRINT",FACE,{"disambiguationData":[TD([[makeQuery(id+"F0.imprint","IMPRINT",EDGE,{"disambiguationData":[TD([[subQ2,-1.0]])],"derivedFrom":subQ1}),-1.0]])]});}
            var Q714;
            {var subQ0=sQuery(id+"F0.wireOp",EDGE,"E14.28.1");var subQ1=sQuery(id+"F0.wireOp",EDGE,"E14.10.0");var subQ2=makeQuery(id+"F0.imprint","INTERSECT",VERTEX,{"derivedFrom":[subQ1,subQ0]});Q714=makeQuery(id+"F0.imprint","IMPRINT",FACE,{"disambiguationData":[TD([[makeQuery(id+"F0.imprint","IMPRINT",EDGE,{"disambiguationData":[TD([[subQ2,-1.0]])],"derivedFrom":subQ1}),-1.0]])]});}
            var Q715;
            {var subQ0=sQuery(id+"F0.wireOp",EDGE,"E14.35.1");var subQ1=sQuery(id+"F0.wireOp",EDGE,"E14.21.0");var subQ2=makeQuery(id+"F0.imprint","INTERSECT",VERTEX,{"derivedFrom":[subQ1,subQ0]});Q715=makeQuery(id+"F0.imprint","IMPRINT",FACE,{"disambiguationData":[TD([[makeQuery(id+"F0.imprint","IMPRINT",EDGE,{"disambiguationData":[TD([[subQ2,-1.0]])],"derivedFrom":subQ1}),-1.0]])]});}
            var Q716;
            {var subQ0=sQuery(id+"F0.wireOp",EDGE,"E14.25.1");var subQ1=sQuery(id+"F0.wireOp",EDGE,"E14.9.0");var subQ2=makeQuery(id+"F0.imprint","INTERSECT",VERTEX,{"derivedFrom":[subQ1,subQ0]});Q716=makeQuery(id+"F0.imprint","IMPRINT",FACE,{"disambiguationData":[TD([[makeQuery(id+"F0.imprint","IMPRINT",EDGE,{"disambiguationData":[TD([[subQ2,-1.0]])],"derivedFrom":subQ1}),-1.0]])]});}
            var Q717;
            {var subQ0=sQuery(id+"F0.wireOp",EDGE,"E14.30.1");var subQ1=sQuery(id+"F0.wireOp",EDGE,"E14.16.0");var subQ2=makeQuery(id+"F0.imprint","INTERSECT",VERTEX,{"derivedFrom":[subQ1,subQ0]});Q717=makeQuery(id+"F0.imprint","IMPRINT",FACE,{"disambiguationData":[TD([[makeQuery(id+"F0.imprint","IMPRINT",EDGE,{"disambiguationData":[TD([[subQ2,-1.0]])],"derivedFrom":subQ1}),-1.0]])]});}
            var Q718;
            {var subQ0=sQuery(id+"F0.wireOp",EDGE,"E14.16.1");var subQ1=sQuery(id+"F0.wireOp",EDGE,"E14.2.0");var subQ2=makeQuery(id+"F0.imprint","INTERSECT",VERTEX,{"derivedFrom":[subQ1,subQ0]});Q718=makeQuery(id+"F0.imprint","IMPRINT",FACE,{"disambiguationData":[TD([[makeQuery(id+"F0.imprint","IMPRINT",EDGE,{"disambiguationData":[TD([[subQ2,-1.0]])],"derivedFrom":subQ1}),-1.0]])]});}
            var Q719;
            {var subQ0=sQuery(id+"F0.wireOp",EDGE,"E14.21.1");var subQ1=sQuery(id+"F0.wireOp",EDGE,"E14.4.0");var subQ2=makeQuery(id+"F0.imprint","INTERSECT",VERTEX,{"derivedFrom":[subQ1,subQ0]});Q719=makeQuery(id+"F0.imprint","IMPRINT",FACE,{"disambiguationData":[TD([[makeQuery(id+"F0.imprint","IMPRINT",EDGE,{"disambiguationData":[TD([[subQ2,-1.0]])],"derivedFrom":subQ1}),-1.0]])]});}
            var Q720;
            {var subQ0=sQuery(id+"F0.wireOp",EDGE,"E14.34.1");var subQ1=sQuery(id+"F0.wireOp",EDGE,"E14.17.0");var subQ2=makeQuery(id+"F0.imprint","INTERSECT",VERTEX,{"derivedFrom":[subQ1,subQ0]});Q720=makeQuery(id+"F0.imprint","IMPRINT",FACE,{"disambiguationData":[TD([[makeQuery(id+"F0.imprint","IMPRINT",EDGE,{"disambiguationData":[TD([[subQ2,-1.0]])],"derivedFrom":subQ1}),-1.0]])]});}
            var Q721;
            {var subQ0=sQuery(id+"F0.wireOp",EDGE,"E14.17.1");var subQ1=sQuery(id+"F0.wireOp",EDGE,"E14.2.0");var subQ2=makeQuery(id+"F0.imprint","INTERSECT",VERTEX,{"derivedFrom":[subQ1,subQ0]});Q721=makeQuery(id+"F0.imprint","IMPRINT",FACE,{"disambiguationData":[TD([[makeQuery(id+"F0.imprint","IMPRINT",EDGE,{"disambiguationData":[TD([[subQ2,-1.0]])],"derivedFrom":subQ1}),-1.0]])]});}
            var Q722;
            {var subQ0=sQuery(id+"F0.wireOp",EDGE,"E14.29.1");var subQ1=sQuery(id+"F0.wireOp",EDGE,"E14.11.0");var subQ2=makeQuery(id+"F0.imprint","INTERSECT",VERTEX,{"derivedFrom":[subQ1,subQ0]});Q722=makeQuery(id+"F0.imprint","IMPRINT",FACE,{"disambiguationData":[TD([[makeQuery(id+"F0.imprint","IMPRINT",EDGE,{"disambiguationData":[TD([[subQ2,-1.0]])],"derivedFrom":subQ1}),-1.0]])]});}
            var Q723;
            {var subQ0=sQuery(id+"F0.wireOp",EDGE,"E14.34.0");var subQ1=sQuery(id+"F0.wireOp",EDGE,"E14.15.1");var subQ2=makeQuery(id+"F0.imprint","INTERSECT",VERTEX,{"derivedFrom":[subQ1,subQ0]});Q723=makeQuery(id+"F0.imprint","IMPRINT",FACE,{"disambiguationData":[TD([[makeQuery(id+"F0.imprint","IMPRINT",EDGE,{"disambiguationData":[TD([[subQ2,-1.0]])],"derivedFrom":subQ1}),-1.0]])]});}
            var Q724;
            {var subQ0=sQuery(id+"F0.wireOp",EDGE,"E14.22.0");var subQ1=sQuery(id+"F0.wireOp",EDGE,"E14.2.1");var subQ2=makeQuery(id+"F0.imprint","INTERSECT",VERTEX,{"derivedFrom":[subQ1,subQ0]});Q724=makeQuery(id+"F0.imprint","IMPRINT",FACE,{"disambiguationData":[TD([[makeQuery(id+"F0.imprint","IMPRINT",EDGE,{"disambiguationData":[TD([[subQ2,-1.0]])],"derivedFrom":subQ1}),-1.0]])]});}
            var Q725;
            {var subQ0=sQuery(id+"F0.wireOp",EDGE,"E14.15.1");var subQ1=sQuery(id+"F0.wireOp",EDGE,"E9.right");var subQ2=makeQuery(id+"F0.imprint","INTERSECT",VERTEX,{"derivedFrom":[subQ1,subQ0]});Q725=makeQuery(id+"F0.imprint","IMPRINT",FACE,{"disambiguationData":[TD([[makeQuery(id+"F0.imprint","IMPRINT",EDGE,{"disambiguationData":[TD([[subQ2,-1.0]])],"derivedFrom":subQ1}),-1.0]])]});}
            var Q726;
            {var subQ0=sQuery(id+"F0.wireOp",EDGE,"E14.34.1");var subQ1=sQuery(id+"F0.wireOp",EDGE,"E14.18.0");var subQ2=makeQuery(id+"F0.imprint","INTERSECT",VERTEX,{"derivedFrom":[subQ1,subQ0]});Q726=makeQuery(id+"F0.imprint","IMPRINT",FACE,{"disambiguationData":[TD([[makeQuery(id+"F0.imprint","IMPRINT",EDGE,{"disambiguationData":[TD([[subQ2,-1.0]])],"derivedFrom":subQ1}),-1.0]])]});}
            var Q727;
            {var subQ0=sQuery(id+"F0.wireOp",EDGE,"E14.22.1");var subQ1=sQuery(id+"F0.wireOp",EDGE,"E14.4.0");var subQ2=makeQuery(id+"F0.imprint","INTERSECT",VERTEX,{"derivedFrom":[subQ1,subQ0]});Q727=makeQuery(id+"F0.imprint","IMPRINT",FACE,{"disambiguationData":[TD([[makeQuery(id+"F0.imprint","IMPRINT",EDGE,{"disambiguationData":[TD([[subQ2,-1.0]])],"derivedFrom":subQ1}),-1.0]])]});}
            var Q728;
            {var subQ0=sQuery(id+"F0.wireOp",EDGE,"E14.24.1");var subQ1=sQuery(id+"F0.wireOp",EDGE,"E14.10.0");var subQ2=makeQuery(id+"F0.imprint","INTERSECT",VERTEX,{"derivedFrom":[subQ1,subQ0]});Q728=makeQuery(id+"F0.imprint","IMPRINT",FACE,{"disambiguationData":[TD([[makeQuery(id+"F0.imprint","IMPRINT",EDGE,{"disambiguationData":[TD([[subQ2,-1.0]])],"derivedFrom":subQ1}),-1.0]])]});}
            var Q729;
            {var subQ0=sQuery(id+"F0.wireOp",EDGE,"E14.28.1");var subQ1=sQuery(id+"F0.wireOp",EDGE,"E14.17.0");var subQ2=makeQuery(id+"F0.imprint","INTERSECT",VERTEX,{"derivedFrom":[subQ1,subQ0]});Q729=makeQuery(id+"F0.imprint","IMPRINT",FACE,{"disambiguationData":[TD([[makeQuery(id+"F0.imprint","IMPRINT",EDGE,{"disambiguationData":[TD([[subQ2,-1.0]])],"derivedFrom":subQ1}),-1.0]])]});}
            var Q730;
            {var subQ0=sQuery(id+"F0.wireOp",EDGE,"E14.31.1");var subQ1=sQuery(id+"F0.wireOp",EDGE,"E14.16.0");var subQ2=makeQuery(id+"F0.imprint","INTERSECT",VERTEX,{"derivedFrom":[subQ1,subQ0]});Q730=makeQuery(id+"F0.imprint","IMPRINT",FACE,{"disambiguationData":[TD([[makeQuery(id+"F0.imprint","IMPRINT",EDGE,{"disambiguationData":[TD([[subQ2,-1.0]])],"derivedFrom":subQ1}),-1.0]])]});}
            var Q731;
            {var subQ0=sQuery(id+"F0.wireOp",EDGE,"E14.34.1");var subQ1=sQuery(id+"F0.wireOp",EDGE,"E14.21.0");var subQ2=makeQuery(id+"F0.imprint","INTERSECT",VERTEX,{"derivedFrom":[subQ1,subQ0]});Q731=makeQuery(id+"F0.imprint","IMPRINT",FACE,{"disambiguationData":[TD([[makeQuery(id+"F0.imprint","IMPRINT",EDGE,{"disambiguationData":[TD([[subQ2,-1.0]])],"derivedFrom":subQ1}),-1.0]])]});}
            var Q732;
            {var subQ0=sQuery(id+"F0.wireOp",EDGE,"E14.31.1");var subQ1=sQuery(id+"F0.wireOp",EDGE,"E14.13.0");var subQ2=makeQuery(id+"F0.imprint","INTERSECT",VERTEX,{"derivedFrom":[subQ1,subQ0]});Q732=makeQuery(id+"F0.imprint","IMPRINT",FACE,{"disambiguationData":[TD([[makeQuery(id+"F0.imprint","IMPRINT",EDGE,{"disambiguationData":[TD([[subQ2,-1.0]])],"derivedFrom":subQ1}),-1.0]])]});}
            var Q733;
            {var subQ0=sQuery(id+"F0.wireOp",EDGE,"E14.23.1");var subQ1=sQuery(id+"F0.wireOp",EDGE,"E14.10.0");var subQ2=makeQuery(id+"F0.imprint","INTERSECT",VERTEX,{"derivedFrom":[subQ1,subQ0]});Q733=makeQuery(id+"F0.imprint","IMPRINT",FACE,{"disambiguationData":[TD([[makeQuery(id+"F0.imprint","IMPRINT",EDGE,{"disambiguationData":[TD([[subQ2,-1.0]])],"derivedFrom":subQ1}),-1.0]])]});}
            var Q734;
            {var subQ0=sQuery(id+"F0.wireOp",EDGE,"E14.28.1");var subQ1=sQuery(id+"F0.wireOp",EDGE,"E14.11.0");var subQ2=makeQuery(id+"F0.imprint","INTERSECT",VERTEX,{"derivedFrom":[subQ1,subQ0]});Q734=makeQuery(id+"F0.imprint","IMPRINT",FACE,{"disambiguationData":[TD([[makeQuery(id+"F0.imprint","IMPRINT",EDGE,{"disambiguationData":[TD([[subQ2,-1.0]])],"derivedFrom":subQ1}),-1.0]])]});}
            var Q735;
            {var subQ0=sQuery(id+"F0.wireOp",EDGE,"E14.18.1");var subQ1=sQuery(id+"F0.wireOp",EDGE,"E14.2.0");var subQ2=makeQuery(id+"F0.imprint","INTERSECT",VERTEX,{"derivedFrom":[subQ1,subQ0]});Q735=makeQuery(id+"F0.imprint","IMPRINT",FACE,{"disambiguationData":[TD([[makeQuery(id+"F0.imprint","IMPRINT",EDGE,{"disambiguationData":[TD([[subQ2,-1.0]])],"derivedFrom":subQ1}),-1.0]])]});}
            var Q736;
            {var subQ0=sQuery(id+"F0.wireOp",EDGE,"E14.30.1");var subQ1=sQuery(id+"F0.wireOp",EDGE,"E14.14.0");var subQ2=makeQuery(id+"F0.imprint","INTERSECT",VERTEX,{"derivedFrom":[subQ1,subQ0]});Q736=makeQuery(id+"F0.imprint","IMPRINT",FACE,{"disambiguationData":[TD([[makeQuery(id+"F0.imprint","IMPRINT",EDGE,{"disambiguationData":[TD([[subQ2,-1.0]])],"derivedFrom":subQ1}),-1.0]])]});}
            var Q737;
            {var subQ0=sQuery(id+"F0.wireOp",EDGE,"E14.20.1");var subQ1=sQuery(id+"F0.wireOp",EDGE,"E14.5.0");var subQ2=makeQuery(id+"F0.imprint","INTERSECT",VERTEX,{"derivedFrom":[subQ1,subQ0]});Q737=makeQuery(id+"F0.imprint","IMPRINT",FACE,{"disambiguationData":[TD([[makeQuery(id+"F0.imprint","IMPRINT",EDGE,{"disambiguationData":[TD([[subQ2,-1.0]])],"derivedFrom":subQ1}),-1.0]])]});}
            var Q738;
            {var subQ0=sQuery(id+"F0.wireOp",EDGE,"E14.16.1");var subQ1=sQuery(id+"F0.wireOp",EDGE,"E9.right");var subQ2=makeQuery(id+"F0.imprint","INTERSECT",VERTEX,{"derivedFrom":[subQ1,subQ0]});Q738=makeQuery(id+"F0.imprint","IMPRINT",FACE,{"disambiguationData":[TD([[makeQuery(id+"F0.imprint","IMPRINT",EDGE,{"disambiguationData":[TD([[subQ2,-1.0]])],"derivedFrom":subQ1}),1.0]])]});}
            var Q739;
            {var subQ0=sQuery(id+"F0.wireOp",EDGE,"E14.31.1");var subQ1=sQuery(id+"F0.wireOp",EDGE,"E14.17.0");var subQ2=makeQuery(id+"F0.imprint","INTERSECT",VERTEX,{"derivedFrom":[subQ1,subQ0]});Q739=makeQuery(id+"F0.imprint","IMPRINT",FACE,{"disambiguationData":[TD([[makeQuery(id+"F0.imprint","IMPRINT",EDGE,{"disambiguationData":[TD([[subQ2,-1.0]])],"derivedFrom":subQ1}),-1.0]])]});}
            var Q740;
            {var subQ0=sQuery(id+"F0.wireOp",EDGE,"E14.19.0");var subQ1=sQuery(id+"F0.wireOp",EDGE,"E9.left");var subQ2=makeQuery(id+"F0.imprint","INTERSECT",VERTEX,{"derivedFrom":[subQ1,subQ0]});Q740=makeQuery(id+"F0.imprint","IMPRINT",FACE,{"disambiguationData":[TD([[makeQuery(id+"F0.imprint","IMPRINT",EDGE,{"disambiguationData":[TD([[subQ2,-1.0]])],"derivedFrom":subQ1}),-1.0]])]});}
            var Q741;
            {var subQ0=sQuery(id+"F0.wireOp",EDGE,"E14.35.1");var subQ1=sQuery(id+"F0.wireOp",EDGE,"E14.18.0");var subQ2=makeQuery(id+"F0.imprint","INTERSECT",VERTEX,{"derivedFrom":[subQ1,subQ0]});Q741=makeQuery(id+"F0.imprint","IMPRINT",FACE,{"disambiguationData":[TD([[makeQuery(id+"F0.imprint","IMPRINT",EDGE,{"disambiguationData":[TD([[subQ2,-1.0]])],"derivedFrom":subQ1}),-1.0]])]});}
            var Q742;
            {var subQ0=sQuery(id+"F0.wireOp",EDGE,"E14.34.0");var subQ1=sQuery(id+"F0.wireOp",EDGE,"E14.14.1");var subQ2=makeQuery(id+"F0.imprint","INTERSECT",VERTEX,{"derivedFrom":[subQ1,subQ0]});Q742=makeQuery(id+"F0.imprint","IMPRINT",FACE,{"disambiguationData":[TD([[makeQuery(id+"F0.imprint","IMPRINT",EDGE,{"disambiguationData":[TD([[subQ2,-1.0]])],"derivedFrom":subQ1}),-1.0]])]});}
            var Q743;
            {var subQ0=sQuery(id+"F0.wireOp",EDGE,"E14.35.1");var subQ1=sQuery(id+"F0.wireOp",EDGE,"E14.17.0");var subQ2=makeQuery(id+"F0.imprint","INTERSECT",VERTEX,{"derivedFrom":[subQ1,subQ0]});Q743=makeQuery(id+"F0.imprint","IMPRINT",FACE,{"disambiguationData":[TD([[makeQuery(id+"F0.imprint","IMPRINT",EDGE,{"disambiguationData":[TD([[subQ2,-1.0]])],"derivedFrom":subQ1}),-1.0]])]});}
            var Q744;
            {var subQ0=sQuery(id+"F0.wireOp",EDGE,"E14.14.1");var subQ1=sQuery(id+"F0.wireOp",EDGE,"E9.right");var subQ2=makeQuery(id+"F0.imprint","INTERSECT",VERTEX,{"derivedFrom":[subQ1,subQ0]});Q744=makeQuery(id+"F0.imprint","IMPRINT",FACE,{"disambiguationData":[TD([[makeQuery(id+"F0.imprint","IMPRINT",EDGE,{"disambiguationData":[TD([[subQ2,-1.0]])],"derivedFrom":subQ1}),1.0]])]});}
            var Q745;
            {var subQ0=sQuery(id+"F0.wireOp",EDGE,"E14.20.0");var subQ1=sQuery(id+"F0.wireOp",EDGE,"E9.left");var subQ2=makeQuery(id+"F0.imprint","INTERSECT",VERTEX,{"derivedFrom":[subQ1,subQ0]});Q745=makeQuery(id+"F0.imprint","IMPRINT",FACE,{"disambiguationData":[TD([[makeQuery(id+"F0.imprint","IMPRINT",EDGE,{"disambiguationData":[TD([[subQ2,-1.0]])],"derivedFrom":subQ1}),1.0]])]});}
            var Q746;
            {var subQ0=sQuery(id+"F0.wireOp",EDGE,"E14.32.1");var subQ1=sQuery(id+"F0.wireOp",EDGE,"E14.14.0");var subQ2=makeQuery(id+"F0.imprint","INTERSECT",VERTEX,{"derivedFrom":[subQ1,subQ0]});Q746=makeQuery(id+"F0.imprint","IMPRINT",FACE,{"disambiguationData":[TD([[makeQuery(id+"F0.imprint","IMPRINT",EDGE,{"disambiguationData":[TD([[subQ2,-1.0]])],"derivedFrom":subQ1}),-1.0]])]});}
            var Q747;
            {var subQ0=sQuery(id+"F0.wireOp",EDGE,"E14.18.1");var subQ1=sQuery(id+"F0.wireOp",EDGE,"E14.1.0");var subQ2=makeQuery(id+"F0.imprint","INTERSECT",VERTEX,{"derivedFrom":[subQ1,subQ0]});Q747=makeQuery(id+"F0.imprint","IMPRINT",FACE,{"disambiguationData":[TD([[makeQuery(id+"F0.imprint","IMPRINT",EDGE,{"disambiguationData":[TD([[subQ2,-1.0]])],"derivedFrom":subQ1}),-1.0]])]});}
            var Q748;
            {var subQ0=sQuery(id+"F0.wireOp",EDGE,"E14.26.1");var subQ1=sQuery(id+"F0.wireOp",EDGE,"E14.11.0");var subQ2=makeQuery(id+"F0.imprint","INTERSECT",VERTEX,{"derivedFrom":[subQ1,subQ0]});Q748=makeQuery(id+"F0.imprint","IMPRINT",FACE,{"disambiguationData":[TD([[makeQuery(id+"F0.imprint","IMPRINT",EDGE,{"disambiguationData":[TD([[subQ2,-1.0]])],"derivedFrom":subQ1}),-1.0]])]});}
            var Q749;
            {var subQ0=sQuery(id+"F0.wireOp",EDGE,"E14.31.1");var subQ1=sQuery(id+"F0.wireOp",EDGE,"E14.14.0");var subQ2=makeQuery(id+"F0.imprint","INTERSECT",VERTEX,{"derivedFrom":[subQ1,subQ0]});Q749=makeQuery(id+"F0.imprint","IMPRINT",FACE,{"disambiguationData":[TD([[makeQuery(id+"F0.imprint","IMPRINT",EDGE,{"disambiguationData":[TD([[subQ2,-1.0]])],"derivedFrom":subQ1}),-1.0]])]});}
            var Q750;
            {var subQ0=sQuery(id+"F0.wireOp",EDGE,"E14.17.1");var subQ1=sQuery(id+"F0.wireOp",EDGE,"E9.right");var subQ2=makeQuery(id+"F0.imprint","INTERSECT",VERTEX,{"derivedFrom":[subQ1,subQ0]});Q750=makeQuery(id+"F0.imprint","IMPRINT",FACE,{"disambiguationData":[TD([[makeQuery(id+"F0.imprint","IMPRINT",EDGE,{"disambiguationData":[TD([[subQ2,-1.0]])],"derivedFrom":subQ1}),-1.0]])]});}
            var Q751;
            {var subQ0=sQuery(id+"F0.wireOp",EDGE,"E14.16.1");var subQ1=sQuery(id+"F0.wireOp",EDGE,"E14.1.0");var subQ2=makeQuery(id+"F0.imprint","INTERSECT",VERTEX,{"derivedFrom":[subQ1,subQ0]});Q751=makeQuery(id+"F0.imprint","IMPRINT",FACE,{"disambiguationData":[TD([[makeQuery(id+"F0.imprint","IMPRINT",EDGE,{"disambiguationData":[TD([[subQ2,-1.0]])],"derivedFrom":subQ1}),-1.0]])]});}
            var Q752;
            {var subQ0=sQuery(id+"F0.wireOp",EDGE,"E14.30.1");var subQ1=sQuery(id+"F0.wireOp",EDGE,"E14.13.0");var subQ2=makeQuery(id+"F0.imprint","INTERSECT",VERTEX,{"derivedFrom":[subQ1,subQ0]});Q752=makeQuery(id+"F0.imprint","IMPRINT",FACE,{"disambiguationData":[TD([[makeQuery(id+"F0.imprint","IMPRINT",EDGE,{"disambiguationData":[TD([[subQ2,-1.0]])],"derivedFrom":subQ1}),-1.0]])]});}
            var Q753;
            {var subQ0=sQuery(id+"F0.wireOp",EDGE,"E14.15.1");var subQ1=sQuery(id+"F0.wireOp",EDGE,"E14.1.0");var subQ2=makeQuery(id+"F0.imprint","INTERSECT",VERTEX,{"derivedFrom":[subQ1,subQ0]});Q753=makeQuery(id+"F0.imprint","IMPRINT",FACE,{"disambiguationData":[TD([[makeQuery(id+"F0.imprint","IMPRINT",EDGE,{"disambiguationData":[TD([[subQ2,-1.0]])],"derivedFrom":subQ1}),-1.0]])]});}
            var Q754;
            {var subQ0=sQuery(id+"F0.wireOp",EDGE,"E14.32.1");var subQ1=sQuery(id+"F0.wireOp",EDGE,"E14.16.0");var subQ2=makeQuery(id+"F0.imprint","INTERSECT",VERTEX,{"derivedFrom":[subQ1,subQ0]});Q754=makeQuery(id+"F0.imprint","IMPRINT",FACE,{"disambiguationData":[TD([[makeQuery(id+"F0.imprint","IMPRINT",EDGE,{"disambiguationData":[TD([[subQ2,-1.0]])],"derivedFrom":subQ1}),-1.0]])]});}
            var Q755;
            {var subQ0=sQuery(id+"F0.wireOp",EDGE,"E14.17.1");var subQ1=sQuery(id+"F0.wireOp",EDGE,"E14.1.0");var subQ2=makeQuery(id+"F0.imprint","INTERSECT",VERTEX,{"derivedFrom":[subQ1,subQ0]});Q755=makeQuery(id+"F0.imprint","IMPRINT",FACE,{"disambiguationData":[TD([[makeQuery(id+"F0.imprint","IMPRINT",EDGE,{"disambiguationData":[TD([[subQ2,-1.0]])],"derivedFrom":subQ1}),-1.0]])]});}
            var Q756;
            {var subQ0=sQuery(id+"F0.wireOp",EDGE,"E14.33.1");var subQ1=sQuery(id+"F0.wireOp",EDGE,"E14.16.0");var subQ2=makeQuery(id+"F0.imprint","INTERSECT",VERTEX,{"derivedFrom":[subQ1,subQ0]});Q756=makeQuery(id+"F0.imprint","IMPRINT",FACE,{"disambiguationData":[TD([[makeQuery(id+"F0.imprint","IMPRINT",EDGE,{"disambiguationData":[TD([[subQ2,-1.0]])],"derivedFrom":subQ1}),-1.0]])]});}
            var Q757;
            {var subQ0=sQuery(id+"F0.wireOp",EDGE,"E14.16.1");var subQ1=sQuery(id+"F0.wireOp",EDGE,"E9.right");var subQ2=makeQuery(id+"F0.imprint","INTERSECT",VERTEX,{"derivedFrom":[subQ1,subQ0]});Q757=makeQuery(id+"F0.imprint","IMPRINT",FACE,{"disambiguationData":[TD([[makeQuery(id+"F0.imprint","IMPRINT",EDGE,{"disambiguationData":[TD([[subQ2,-1.0]])],"derivedFrom":subQ1}),-1.0]])]});}
            var Q758;
            {var subQ0=sQuery(id+"F0.wireOp",EDGE,"E14.18.1");var subQ5=sQuery(id+"F0.wireOp",EDGE,"E14.1.0");var subQ6=makeQuery(id+"F0.imprint","INTERSECT",VERTEX,{"derivedFrom":[subQ5,subQ0]});Q758=makeQuery(id+"F0.imprint","IMPRINT",FACE,{"disambiguationData":[TD([[makeQuery(id+"F0.imprint","IMPRINT",EDGE,{"disambiguationData":[TD([[subQ6,-1.0]])],"derivedFrom":subQ5}),1.0]])]});}
            var Q759;
            {var subQ0=sQuery(id+"F0.wireOp",EDGE,"E17");Q759=makeQuery(id+"F0.imprint","IMPRINT",FACE,{"disambiguationData":[TD([[makeQuery(id+"F0.imprint","IMPRINT",EDGE,{"derivedFrom":subQ0}),-1.0]])]});}
            var Q760;
            {var subQ5=sQuery(id+"F0.wireOp",EDGE,"E0");var subQ7=sQuery(id+"F0.wireOp",EDGE,"E16.0");var subQ9=makeQuery(id+"F0.imprint","INTERSECT",VERTEX,{"derivedFrom":[subQ5,subQ7]});Q760=makeQuery(id+"F0.imprint","IMPRINT",FACE,{"disambiguationData":[TD([[makeQuery(id+"F0.imprint","IMPRINT",EDGE,{"disambiguationData":[TD([[subQ9,-1.0]])],"derivedFrom":subQ5}),-1.0]])]});}
            extrude(context, id + "F1", {"entities" : qUnion([Q0, Q1, Q2, Q3, Q4, Q5, Q6, Q7, Q8, Q9, Q10, Q11, Q12, Q13, Q14, Q15, Q16, Q17, Q18, Q19, Q20, Q21, Q22, Q23, Q24, Q25, Q26, Q27, Q28, Q29, Q30, Q31, Q32, Q33, Q34, Q35, Q36, Q37, Q38, Q39, Q40, Q41, Q42, Q43, Q44, Q45, Q46, Q47, Q48, Q49, Q50, Q51, Q52, Q53, Q54, Q55, Q56, Q57, Q58, Q59, Q60, Q61, Q62, Q63, Q64, Q65, Q66, Q67, Q68, Q69, Q70, Q71, Q72, Q73, Q74, Q75, Q76, Q77, Q78, Q79, Q80, Q81, Q82, Q83, Q84, Q85, Q86, Q87, Q88, Q89, Q90, Q91, Q92, Q93, Q94, Q95, Q96, Q97, Q98, Q99, Q100, Q101, Q102, Q103, Q104, Q105, Q106, Q107, Q108, Q109, Q110, Q111, Q112, Q113, Q114, Q115, Q116, Q117, Q118, Q119, Q120, Q121, Q122, Q123, Q124, Q125, Q126, Q127, Q128, Q129, Q130, Q131, Q132, Q133, Q134, Q135, Q136, Q137, Q138, Q139, Q140, Q141, Q142, Q143, Q144, Q145, Q146, Q147, Q148, Q149, Q150, Q151, Q152, Q153, Q154, Q155, Q156, Q157, Q158, Q159, Q160, Q161, Q162, Q163, Q164, Q165, Q166, Q167, Q168, Q169, Q170, Q171, Q172, Q173, Q174, Q175, Q176, Q177, Q178, Q179, Q180, Q181, Q182, Q183, Q184, Q185, Q186, Q187, Q188, Q189, Q190, Q191, Q192, Q193, Q194, Q195, Q196, Q197, Q198, Q199, Q200, Q201, Q202, Q203, Q204, Q205, Q206, Q207, Q208, Q209, Q210, Q211, Q212, Q213, Q214, Q215, Q216, Q217, Q218, Q219, Q220, Q221, Q222, Q223, Q224, Q225, Q226, Q227, Q228, Q229, Q230, Q231, Q232, Q233, Q234, Q235, Q236, Q237, Q238, Q239, Q240, Q241, Q242, Q243, Q244, Q245, Q246, Q247, Q248, Q249, Q250, Q251, Q252, Q253, Q254, Q255, Q256, Q257, Q258, Q259, Q260, Q261, Q262, Q263, Q264, Q265, Q266, Q267, Q268, Q269, Q270, Q271, Q272, Q273, Q274, Q275, Q276, Q277, Q278, Q279, Q280, Q281, Q282, Q283, Q284, Q285, Q286, Q287, Q288, Q289, Q290, Q291, Q292, Q293, Q294, Q295, Q296, Q297, Q298, Q299, Q300, Q301, Q302, Q303, Q304, Q305, Q306, Q307, Q308, Q309, Q310, Q311, Q312, Q313, Q314, Q315, Q316, Q317, Q318, Q319, Q320, Q321, Q322, Q323, Q324, Q325, Q326, Q327, Q328, Q329, Q330, Q331, Q332, Q333, Q334, Q335, Q336, Q337, Q338, Q339, Q340, Q341, Q342, Q343, Q344, Q345, Q346, Q347, Q348, Q349, Q350, Q351, Q352, Q353, Q354, Q355, Q356, Q357, Q358, Q359, Q360, Q361, Q362, Q363, Q364, Q365, Q366, Q367, Q368, Q369, Q370, Q371, Q372, Q373, Q374, Q375, Q376, Q377, Q378, Q379, Q380, Q381, Q382, Q383, Q384, Q385, Q386, Q387, Q388, Q389, Q390, Q391, Q392, Q393, Q394, Q395, Q396, Q397, Q398, Q399, Q400, Q401, Q402, Q403, Q404, Q405, Q406, Q407, Q408, Q409, Q410, Q411, Q412, Q413, Q414, Q415, Q416, Q417, Q418, Q419, Q420, Q421, Q422, Q423, Q424, Q425, Q426, Q427, Q428, Q429, Q430, Q431, Q432, Q433, Q434, Q435, Q436, Q437, Q438, Q439, Q440, Q441, Q442, Q443, Q444, Q445, Q446, Q447, Q448, Q449, Q450, Q451, Q452, Q453, Q454, Q455, Q456, Q457, Q458, Q459, Q460, Q461, Q462, Q463, Q464, Q465, Q466, Q467, Q468, Q469, Q470, Q471, Q472, Q473, Q474, Q475, Q476, Q477, Q478, Q479, Q480, Q481, Q482, Q483, Q484, Q485, Q486, Q487, Q488, Q489, Q490, Q491, Q492, Q493, Q494, Q495, Q496, Q497, Q498, Q499, Q500, Q501, Q502, Q503, Q504, Q505, Q506, Q507, Q508, Q509, Q510, Q511, Q512, Q513, Q514, Q515, Q516, Q517, Q518, Q519, Q520, Q521, Q522, Q523, Q524, Q525, Q526, Q527, Q528, Q529, Q530, Q531, Q532, Q533, Q534, Q535, Q536, Q537, Q538, Q539, Q540, Q541, Q542, Q543, Q544, Q545, Q546, Q547, Q548, Q549, Q550, Q551, Q552, Q553, Q554, Q555, Q556, Q557, Q558, Q559, Q560, Q561, Q562, Q563, Q564, Q565, Q566, Q567, Q568, Q569, Q570, Q571, Q572, Q573, Q574, Q575, Q576, Q577, Q578, Q579, Q580, Q581, Q582, Q583, Q584, Q585, Q586, Q587, Q588, Q589, Q590, Q591, Q592, Q593, Q594, Q595, Q596, Q597, Q598, Q599, Q600, Q601, Q602, Q603, Q604, Q605, Q606, Q607, Q608, Q609, Q610, Q611, Q612, Q613, Q614, Q615, Q616, Q617, Q618, Q619, Q620, Q621, Q622, Q623, Q624, Q625, Q626, Q627, Q628, Q629, Q630, Q631, Q632, Q633, Q634, Q635, Q636, Q637, Q638, Q639, Q640, Q641, Q642, Q643, Q644, Q645, Q646, Q647, Q648, Q649, Q650, Q651, Q652, Q653, Q654, Q655, Q656, Q657, Q658, Q659, Q660, Q661, Q662, Q663, Q664, Q665, Q666, Q667, Q668, Q669, Q670, Q671, Q672, Q673, Q674, Q675, Q676, Q677, Q678, Q679, Q680, Q681, Q682, Q683, Q684, Q685, Q686, Q687, Q688, Q689, Q690, Q691, Q692, Q693, Q694, Q695, Q696, Q697, Q698, Q699, Q700, Q701, Q702, Q703, Q704, Q705, Q706, Q707, Q708, Q709, Q710, Q711, Q712, Q713, Q714, Q715, Q716, Q717, Q718, Q719, Q720, Q721, Q722, Q723, Q724, Q725, Q726, Q727, Q728, Q729, Q730, Q731, Q732, Q733, Q734, Q735, Q736, Q737, Q738, Q739, Q740, Q741, Q742, Q743, Q744, Q745, Q746, Q747, Q748, Q749, Q750, Q751, Q752, Q753, Q754, Q755, Q756, Q757, Q758, Q759, Q760]), "depth" : 10 * mm, "offsetDistance" : 25 * mm});
        }
        {
            var Q0;
            Q0=makeQuery(id+"F1.opExtrude","CAP_FACE",FACE,{"disambiguationData":[OSD([sQuery(id+"F0.wireOp",EDGE,"E0"),sQuery(id+"F0.wireOp",EDGE,"E2.left"),sQuery(id+"F0.wireOp",EDGE,"E2.right"),sQuery(id+"F0.wireOp",EDGE,"E3"),sQuery(id+"F0.wireOp",EDGE,"E4"),sQuery(id+"F0.wireOp",EDGE,"E5"),sQuery(id+"F0.wireOp",EDGE,"E6.1.0"),sQuery(id+"F0.wireOp",EDGE,"E6.1.1"),sQuery(id+"F0.wireOp",EDGE,"E6.1.2"),sQuery(id+"F0.wireOp",EDGE,"E6.1.3"),sQuery(id+"F0.wireOp",EDGE,"E6.1.4"),sQuery(id+"F0.wireOp",EDGE,"E6.2.0"),sQuery(id+"F0.wireOp",EDGE,"E6.2.1"),sQuery(id+"F0.wireOp",EDGE,"E6.2.2"),sQuery(id+"F0.wireOp",EDGE,"E6.2.3"),sQuery(id+"F0.wireOp",EDGE,"E6.2.4"),sQuery(id+"F0.wireOp",EDGE,"E6.3.0"),sQuery(id+"F0.wireOp",EDGE,"E6.3.1"),sQuery(id+"F0.wireOp",EDGE,"E6.3.2"),sQuery(id+"F0.wireOp",EDGE,"E6.3.3"),sQuery(id+"F0.wireOp",EDGE,"E6.3.4"),sQuery(id+"F0.wireOp",EDGE,"E9.left"),sQuery(id+"F0.wireOp",EDGE,"E9.right"),sQuery(id+"F0.wireOp",EDGE,"E10"),sQuery(id+"F0.wireOp",EDGE,"E11"),sQuery(id+"F0.wireOp",EDGE,"E12"),sQuery(id+"F0.wireOp",EDGE,"E14.1.0"),sQuery(id+"F0.wireOp",EDGE,"E14.1.1"),sQuery(id+"F0.wireOp",EDGE,"E14.1.2"),sQuery(id+"F0.wireOp",EDGE,"E14.1.3"),sQuery(id+"F0.wireOp",EDGE,"E14.1.4"),sQuery(id+"F0.wireOp",EDGE,"E14.2.0"),sQuery(id+"F0.wireOp",EDGE,"E14.2.1"),sQuery(id+"F0.wireOp",EDGE,"E14.2.2"),sQuery(id+"F0.wireOp",EDGE,"E14.2.3"),sQuery(id+"F0.wireOp",EDGE,"E14.2.4"),sQuery(id+"F0.wireOp",EDGE,"E14.3.0"),sQuery(id+"F0.wireOp",EDGE,"E14.3.1"),sQuery(id+"F0.wireOp",EDGE,"E14.3.2"),sQuery(id+"F0.wireOp",EDGE,"E14.3.3"),sQuery(id+"F0.wireOp",EDGE,"E14.3.4"),sQuery(id+"F0.wireOp",EDGE,"E14.4.0"),sQuery(id+"F0.wireOp",EDGE,"E14.4.1"),sQuery(id+"F0.wireOp",EDGE,"E14.4.2"),sQuery(id+"F0.wireOp",EDGE,"E14.4.3"),sQuery(id+"F0.wireOp",EDGE,"E14.4.4"),sQuery(id+"F0.wireOp",EDGE,"E14.5.0"),sQuery(id+"F0.wireOp",EDGE,"E14.5.1"),sQuery(id+"F0.wireOp",EDGE,"E14.5.2"),sQuery(id+"F0.wireOp",EDGE,"E14.5.3"),sQuery(id+"F0.wireOp",EDGE,"E14.5.4"),sQuery(id+"F0.wireOp",EDGE,"E14.6.0"),sQuery(id+"F0.wireOp",EDGE,"E14.6.1"),sQuery(id+"F0.wireOp",EDGE,"E14.6.2"),sQuery(id+"F0.wireOp",EDGE,"E14.6.3"),sQuery(id+"F0.wireOp",EDGE,"E14.6.4"),sQuery(id+"F0.wireOp",EDGE,"E14.7.0"),sQuery(id+"F0.wireOp",EDGE,"E14.7.1"),sQuery(id+"F0.wireOp",EDGE,"E14.7.2"),sQuery(id+"F0.wireOp",EDGE,"E14.7.3"),sQuery(id+"F0.wireOp",EDGE,"E14.7.4"),sQuery(id+"F0.wireOp",EDGE,"E14.8.0"),sQuery(id+"F0.wireOp",EDGE,"E14.8.1"),sQuery(id+"F0.wireOp",EDGE,"E14.9.0"),sQuery(id+"F0.wireOp",EDGE,"E14.9.1"),sQuery(id+"F0.wireOp",EDGE,"E14.9.2"),sQuery(id+"F0.wireOp",EDGE,"E14.9.3"),sQuery(id+"F0.wireOp",EDGE,"E14.9.4"),sQuery(id+"F0.wireOp",EDGE,"E14.10.0"),sQuery(id+"F0.wireOp",EDGE,"E14.10.1"),sQuery(id+"F0.wireOp",EDGE,"E14.10.2"),sQuery(id+"F0.wireOp",EDGE,"E14.10.3"),sQuery(id+"F0.wireOp",EDGE,"E14.10.4"),sQuery(id+"F0.wireOp",EDGE,"E14.11.0"),sQuery(id+"F0.wireOp",EDGE,"E14.11.1"),sQuery(id+"F0.wireOp",EDGE,"E14.11.2"),sQuery(id+"F0.wireOp",EDGE,"E14.11.3"),sQuery(id+"F0.wireOp",EDGE,"E14.11.4"),sQuery(id+"F0.wireOp",EDGE,"E14.12.0"),sQuery(id+"F0.wireOp",EDGE,"E14.12.1"),sQuery(id+"F0.wireOp",EDGE,"E14.12.2"),sQuery(id+"F0.wireOp",EDGE,"E14.12.3"),sQuery(id+"F0.wireOp",EDGE,"E14.12.4"),sQuery(id+"F0.wireOp",EDGE,"E14.13.0"),sQuery(id+"F0.wireOp",EDGE,"E14.13.1"),sQuery(id+"F0.wireOp",EDGE,"E14.13.2"),sQuery(id+"F0.wireOp",EDGE,"E14.13.3"),sQuery(id+"F0.wireOp",EDGE,"E14.13.4"),sQuery(id+"F0.wireOp",EDGE,"E14.14.0"),sQuery(id+"F0.wireOp",EDGE,"E14.14.1"),sQuery(id+"F0.wireOp",EDGE,"E14.14.2"),sQuery(id+"F0.wireOp",EDGE,"E14.14.3"),sQuery(id+"F0.wireOp",EDGE,"E14.14.4"),sQuery(id+"F0.wireOp",EDGE,"E14.15.0"),sQuery(id+"F0.wireOp",EDGE,"E14.15.1"),sQuery(id+"F0.wireOp",EDGE,"E14.15.2"),sQuery(id+"F0.wireOp",EDGE,"E14.15.3"),sQuery(id+"F0.wireOp",EDGE,"E14.15.4"),sQuery(id+"F0.wireOp",EDGE,"E14.16.0"),sQuery(id+"F0.wireOp",EDGE,"E14.16.1"),sQuery(id+"F0.wireOp",EDGE,"E14.16.2"),sQuery(id+"F0.wireOp",EDGE,"E14.16.3"),sQuery(id+"F0.wireOp",EDGE,"E14.16.4"),sQuery(id+"F0.wireOp",EDGE,"E14.17.0"),sQuery(id+"F0.wireOp",EDGE,"E14.17.1"),sQuery(id+"F0.wireOp",EDGE,"E14.18.0"),sQuery(id+"F0.wireOp",EDGE,"E14.18.1"),sQuery(id+"F0.wireOp",EDGE,"E14.18.2"),sQuery(id+"F0.wireOp",EDGE,"E14.18.3"),sQuery(id+"F0.wireOp",EDGE,"E14.18.4"),sQuery(id+"F0.wireOp",EDGE,"E14.19.0"),sQuery(id+"F0.wireOp",EDGE,"E14.19.1"),sQuery(id+"F0.wireOp",EDGE,"E14.19.2"),sQuery(id+"F0.wireOp",EDGE,"E14.19.3"),sQuery(id+"F0.wireOp",EDGE,"E14.19.4"),sQuery(id+"F0.wireOp",EDGE,"E14.20.0"),sQuery(id+"F0.wireOp",EDGE,"E14.20.1"),sQuery(id+"F0.wireOp",EDGE,"E14.20.2"),sQuery(id+"F0.wireOp",EDGE,"E14.20.3"),sQuery(id+"F0.wireOp",EDGE,"E14.20.4"),sQuery(id+"F0.wireOp",EDGE,"E14.21.0"),sQuery(id+"F0.wireOp",EDGE,"E14.21.1"),sQuery(id+"F0.wireOp",EDGE,"E14.21.2"),sQuery(id+"F0.wireOp",EDGE,"E14.21.3"),sQuery(id+"F0.wireOp",EDGE,"E14.21.4"),sQuery(id+"F0.wireOp",EDGE,"E14.22.0"),sQuery(id+"F0.wireOp",EDGE,"E14.22.1"),sQuery(id+"F0.wireOp",EDGE,"E14.22.2"),sQuery(id+"F0.wireOp",EDGE,"E14.22.3"),sQuery(id+"F0.wireOp",EDGE,"E14.22.4"),sQuery(id+"F0.wireOp",EDGE,"E14.23.0"),sQuery(id+"F0.wireOp",EDGE,"E14.23.1"),sQuery(id+"F0.wireOp",EDGE,"E14.23.2"),sQuery(id+"F0.wireOp",EDGE,"E14.23.3"),sQuery(id+"F0.wireOp",EDGE,"E14.23.4"),sQuery(id+"F0.wireOp",EDGE,"E14.24.0"),sQuery(id+"F0.wireOp",EDGE,"E14.24.1"),sQuery(id+"F0.wireOp",EDGE,"E14.24.2"),sQuery(id+"F0.wireOp",EDGE,"E14.24.3"),sQuery(id+"F0.wireOp",EDGE,"E14.24.4"),sQuery(id+"F0.wireOp",EDGE,"E14.25.0"),sQuery(id+"F0.wireOp",EDGE,"E14.25.1"),sQuery(id+"F0.wireOp",EDGE,"E14.25.2"),sQuery(id+"F0.wireOp",EDGE,"E14.25.3"),sQuery(id+"F0.wireOp",EDGE,"E14.25.4"),sQuery(id+"F0.wireOp",EDGE,"E14.26.0"),sQuery(id+"F0.wireOp",EDGE,"E14.26.1"),sQuery(id+"F0.wireOp",EDGE,"E14.27.0"),sQuery(id+"F0.wireOp",EDGE,"E14.27.1"),sQuery(id+"F0.wireOp",EDGE,"E14.27.2"),sQuery(id+"F0.wireOp",EDGE,"E14.27.3"),sQuery(id+"F0.wireOp",EDGE,"E14.27.4"),sQuery(id+"F0.wireOp",EDGE,"E14.28.0"),sQuery(id+"F0.wireOp",EDGE,"E14.28.1"),sQuery(id+"F0.wireOp",EDGE,"E14.28.2"),sQuery(id+"F0.wireOp",EDGE,"E14.28.3"),sQuery(id+"F0.wireOp",EDGE,"E14.28.4"),sQuery(id+"F0.wireOp",EDGE,"E14.29.0"),sQuery(id+"F0.wireOp",EDGE,"E14.29.1"),sQuery(id+"F0.wireOp",EDGE,"E14.29.2"),sQuery(id+"F0.wireOp",EDGE,"E14.29.3"),sQuery(id+"F0.wireOp",EDGE,"E14.29.4"),sQuery(id+"F0.wireOp",EDGE,"E14.30.0"),sQuery(id+"F0.wireOp",EDGE,"E14.30.1"),sQuery(id+"F0.wireOp",EDGE,"E14.30.2"),sQuery(id+"F0.wireOp",EDGE,"E14.30.3"),sQuery(id+"F0.wireOp",EDGE,"E14.30.4"),sQuery(id+"F0.wireOp",EDGE,"E14.31.0"),sQuery(id+"F0.wireOp",EDGE,"E14.31.1"),sQuery(id+"F0.wireOp",EDGE,"E14.31.2"),sQuery(id+"F0.wireOp",EDGE,"E14.31.3"),sQuery(id+"F0.wireOp",EDGE,"E14.31.4"),sQuery(id+"F0.wireOp",EDGE,"E14.32.0"),sQuery(id+"F0.wireOp",EDGE,"E14.32.1"),sQuery(id+"F0.wireOp",EDGE,"E14.32.2"),sQuery(id+"F0.wireOp",EDGE,"E14.32.3"),sQuery(id+"F0.wireOp",EDGE,"E14.32.4"),sQuery(id+"F0.wireOp",EDGE,"E14.33.0"),sQuery(id+"F0.wireOp",EDGE,"E14.33.1"),sQuery(id+"F0.wireOp",EDGE,"E14.33.2"),sQuery(id+"F0.wireOp",EDGE,"E14.33.3"),sQuery(id+"F0.wireOp",EDGE,"E14.33.4"),sQuery(id+"F0.wireOp",EDGE,"E14.34.0"),sQuery(id+"F0.wireOp",EDGE,"E14.34.1"),sQuery(id+"F0.wireOp",EDGE,"E14.34.2"),sQuery(id+"F0.wireOp",EDGE,"E14.34.3"),sQuery(id+"F0.wireOp",EDGE,"E14.34.4"),sQuery(id+"F0.wireOp",EDGE,"E14.35.0"),sQuery(id+"F0.wireOp",EDGE,"E14.35.1"),sQuery(id+"F0.wireOp",EDGE,"E16.0"),sQuery(id+"F0.wireOp",EDGE,"E17"),sQuery(id+"F0.wireOp",EDGE,"E19.trimOffspring"),sQuery(id+"F0.wireOp",EDGE,"E20.trimOffspring")])],"isStart":false});
            var sketch = newSketch(context, id + "F2", { "sketchPlane" : qUnion([Q0])});
            skLineSegment(sketch, "E22", {"start": v(-7.19, 1.27) * mm, "end": v(0, 0) * mm});
            skLineSegment(sketch, "E23", {"start": v(0, 0) * mm, "end": v(-7.05, 1.89) * mm});
            skPoint(sketch, "E23.endSnap0", {"position": v(-7.02, 1.34) * mm});
            skLineSegment(sketch, "E24", {"start": v(0, 0) * mm, "end": v(-7.27, 0.64) * mm});
            skArc(sketch, "E25", {"start": v(-7.05, 1.89) * mm, "mid": v(-7.19, 1.27) * mm, "end": v(-7.27, 0.64) * mm});
            skSolve(sketch);
        }
        {
            var Q0;
            Q0 = qSketchRegion(id + "F2", true);
            var Q1;
            Q1=sQuery(id+"F2.wireOp",EDGE,"E25");
            var Q2;
            Q2=sQuery(id+"F2.wireOp",EDGE,"E24");
            var Q3;
            Q3=sQuery(id+"F2.wireOp",EDGE,"E23");
            var Q4;
            Q4=sQuery(id+"F2.wireOp",VERTEX,"E23.end");
            extrude(context, id + "F3", {"entities" : qUnion([Q0]), "operationType" : NewBodyOperationType.ADD, "surfaceOperationType" : NewSurfaceOperationType.ADD, "surfaceEntities" : qUnion([Q1, Q2, Q3]), "depth" : 2 * mm, "endBoundEntityVertex" : qUnion([Q4]), "offsetDistance" : 25 * mm});
        }
        {
            var Q0;
            Q0=makeQuery(id+"F3.opExtrude","SWEPT_FACE",FACE,{"disambiguationData":[OSD([sQuery(id+"F2.wireOp",EDGE,"E24")])]});
            var sketch = newSketch(context, id + "F4", { "sketchPlane" : qUnion([Q0])});
            skLineSegment(sketch, "E26.0", {"start": v(0, 12) * mm, "end": v(-7.3, 12) * mm});
            skSolve(sketch);
        }
    });
